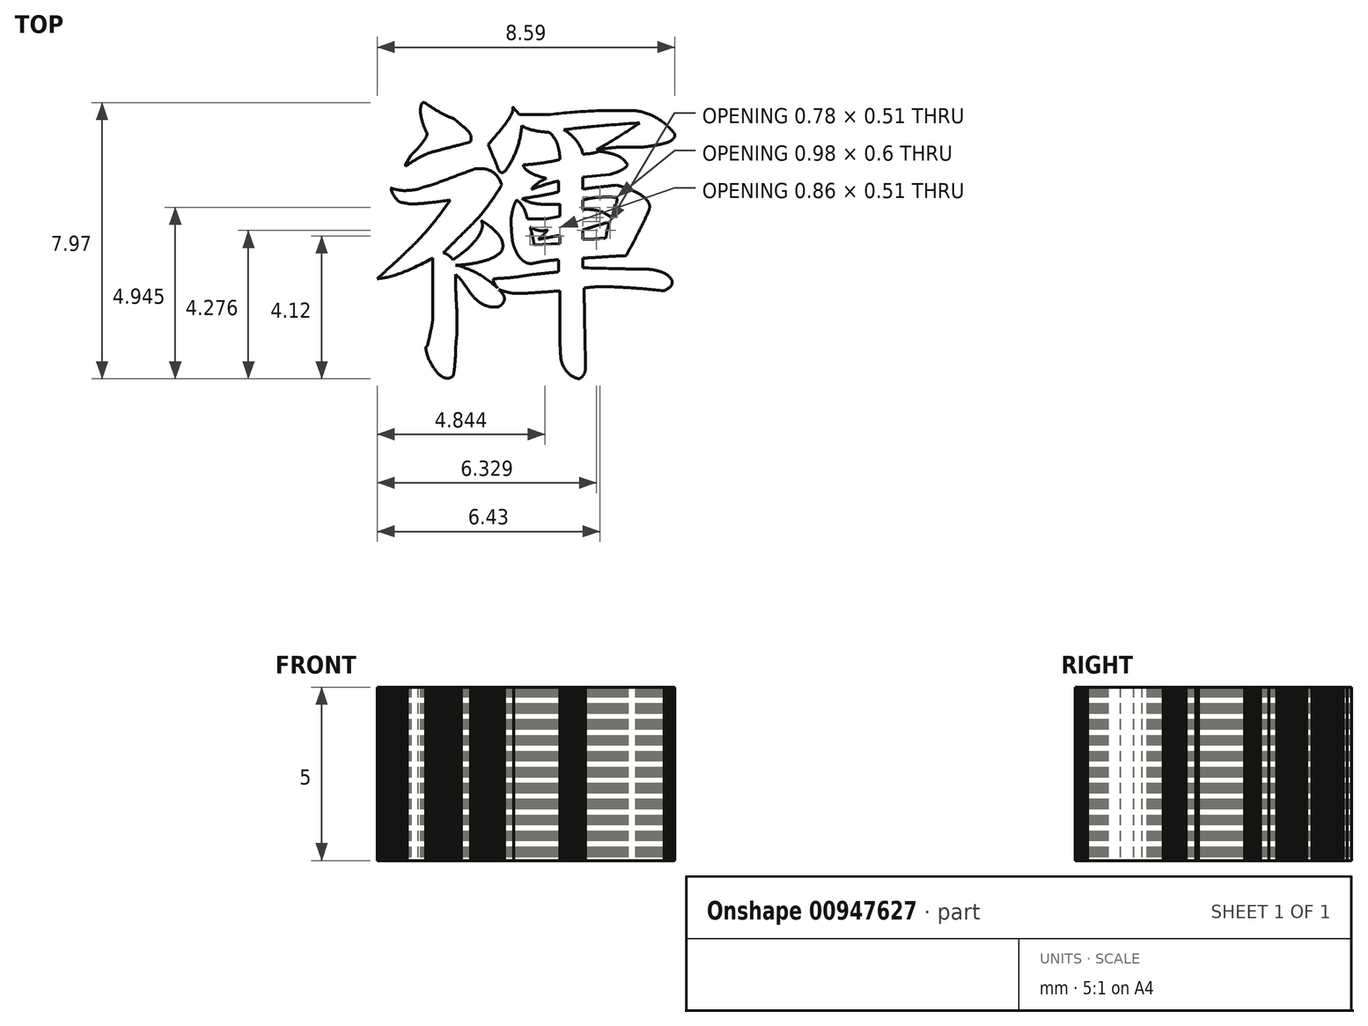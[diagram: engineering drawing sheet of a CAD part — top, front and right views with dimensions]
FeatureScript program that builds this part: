
annotation { "Feature Type Name" : "Feature", "Feature Type Description" : "" }
export const myFeature = defineFeature(function(context is Context, id is Id, definition is map)
    precondition{}
    {
        {
            var Q0;
            Q0=qCreatedBy(makeId("Top.planeOp"), FACE);
            var sketch = newSketch(context, id + "F0", { "sketchPlane" : qUnion([Q0])});
            skLineSegment(sketch, "E0", {"start": v(0.5, 4.13) * mm, "end": v(0.53, 4.13) * mm});
            skLineSegment(sketch, "E1", {"start": v(0.53, 4.13) * mm, "end": v(0.57, 4.12) * mm});
            skLineSegment(sketch, "E2", {"start": v(0.57, 4.12) * mm, "end": v(0.6, 4.11) * mm});
            skLineSegment(sketch, "E3", {"start": v(0.6, 4.11) * mm, "end": v(0.65, 4.1) * mm});
            skLineSegment(sketch, "E4", {"start": v(0.65, 4.1) * mm, "end": v(0.68, 4.1) * mm});
            skLineSegment(sketch, "E5", {"start": v(0.68, 4.1) * mm, "end": v(0.72, 4.09) * mm});
            skLineSegment(sketch, "E6", {"start": v(0.72, 4.09) * mm, "end": v(0.76, 4.08) * mm});
            skLineSegment(sketch, "E7", {"start": v(0.76, 4.08) * mm, "end": v(0.8, 4.06) * mm});
            skLineSegment(sketch, "E8", {"start": v(0.8, 4.06) * mm, "end": v(0.83, 4.05) * mm});
            skLineSegment(sketch, "E9", {"start": v(0.83, 4.05) * mm, "end": v(0.87, 4.04) * mm});
            skLineSegment(sketch, "E10", {"start": v(0.87, 4.04) * mm, "end": v(0.9, 4.02) * mm});
            skLineSegment(sketch, "E11", {"start": v(0.9, 4.02) * mm, "end": v(0.94, 4) * mm});
            skLineSegment(sketch, "E12", {"start": v(0.94, 4) * mm, "end": v(0.97, 4) * mm});
            skLineSegment(sketch, "E13", {"start": v(0.97, 4) * mm, "end": v(1, 3.97) * mm});
            skLineSegment(sketch, "E14", {"start": v(1, 3.97) * mm, "end": v(1.04, 3.96) * mm});
            skLineSegment(sketch, "E15", {"start": v(1.04, 3.96) * mm, "end": v(1.08, 3.94) * mm});
            skLineSegment(sketch, "E16", {"start": v(1.08, 3.94) * mm, "end": v(1.11, 3.92) * mm});
            skLineSegment(sketch, "E17", {"start": v(1.11, 3.92) * mm, "end": v(1.15, 3.9) * mm});
            skLineSegment(sketch, "E18", {"start": v(1.15, 3.9) * mm, "end": v(1.18, 3.87) * mm});
            skLineSegment(sketch, "E19", {"start": v(1.18, 3.87) * mm, "end": v(1.21, 3.85) * mm});
            skLineSegment(sketch, "E20", {"start": v(1.21, 3.85) * mm, "end": v(1.24, 3.83) * mm});
            skLineSegment(sketch, "E21", {"start": v(1.24, 3.83) * mm, "end": v(1.28, 3.8) * mm});
            skLineSegment(sketch, "E22", {"start": v(1.28, 3.8) * mm, "end": v(1.3, 3.78) * mm});
            skLineSegment(sketch, "E23", {"start": v(1.3, 3.78) * mm, "end": v(1.34, 3.75) * mm});
            skLineSegment(sketch, "E24", {"start": v(1.34, 3.75) * mm, "end": v(1.37, 3.72) * mm});
            skLineSegment(sketch, "E25", {"start": v(1.37, 3.72) * mm, "end": v(1.4, 3.7) * mm});
            skLineSegment(sketch, "E26", {"start": v(1.4, 3.7) * mm, "end": v(1.43, 3.67) * mm});
            skLineSegment(sketch, "E27", {"start": v(1.43, 3.67) * mm, "end": v(1.47, 3.64) * mm});
            skLineSegment(sketch, "E28", {"start": v(1.47, 3.64) * mm, "end": v(1.5, 3.6) * mm});
            skLineSegment(sketch, "E29", {"start": v(1.5, 3.6) * mm, "end": v(1.53, 3.57) * mm});
            skLineSegment(sketch, "E30", {"start": v(1.53, 3.57) * mm, "end": v(1.56, 3.54) * mm});
            skLineSegment(sketch, "E31", {"start": v(1.56, 3.54) * mm, "end": v(1.59, 3.5) * mm});
            skLineSegment(sketch, "E32", {"start": v(1.59, 3.5) * mm, "end": v(1.6, 3.5) * mm});
            skLineSegment(sketch, "E33", {"start": v(1.6, 3.5) * mm, "end": v(1.6, 3.5) * mm});
            skLineSegment(sketch, "E34", {"start": v(1.6, 3.5) * mm, "end": v(1.6, 3.49) * mm});
            skLineSegment(sketch, "E35", {"start": v(1.6, 3.49) * mm, "end": v(1.6, 3.48) * mm});
            skLineSegment(sketch, "E36", {"start": v(1.6, 3.48) * mm, "end": v(1.61, 3.47) * mm});
            skLineSegment(sketch, "E37", {"start": v(1.61, 3.47) * mm, "end": v(1.62, 3.46) * mm});
            skLineSegment(sketch, "E38", {"start": v(1.62, 3.46) * mm, "end": v(1.62, 3.45) * mm});
            skLineSegment(sketch, "E39", {"start": v(1.62, 3.45) * mm, "end": v(1.62, 3.45) * mm});
            skLineSegment(sketch, "E40", {"start": v(1.62, 3.45) * mm, "end": v(1.62, 3.44) * mm});
            skLineSegment(sketch, "E41", {"start": v(1.62, 3.44) * mm, "end": v(1.62, 3.43) * mm});
            skLineSegment(sketch, "E42", {"start": v(1.62, 3.43) * mm, "end": v(1.62, 3.42) * mm});
            skLineSegment(sketch, "E43", {"start": v(1.62, 3.42) * mm, "end": v(1.62, 3.41) * mm});
            skLineSegment(sketch, "E44", {"start": v(1.62, 3.41) * mm, "end": v(1.62, 3.4) * mm});
            skLineSegment(sketch, "E45", {"start": v(1.62, 3.4) * mm, "end": v(1.62, 3.4) * mm});
            skLineSegment(sketch, "E46", {"start": v(1.62, 3.4) * mm, "end": v(1.62, 3.39) * mm});
            skLineSegment(sketch, "E47", {"start": v(1.62, 3.39) * mm, "end": v(1.61, 3.38) * mm});
            skLineSegment(sketch, "E48", {"start": v(1.61, 3.38) * mm, "end": v(1.61, 3.37) * mm});
            skLineSegment(sketch, "E49", {"start": v(1.61, 3.37) * mm, "end": v(1.6, 3.36) * mm});
            skLineSegment(sketch, "E50", {"start": v(1.6, 3.36) * mm, "end": v(1.6, 3.35) * mm});
            skLineSegment(sketch, "E51", {"start": v(1.6, 3.35) * mm, "end": v(1.6, 3.35) * mm});
            skLineSegment(sketch, "E52", {"start": v(1.6, 3.35) * mm, "end": v(1.59, 3.34) * mm});
            skLineSegment(sketch, "E53", {"start": v(1.59, 3.34) * mm, "end": v(1.58, 3.33) * mm});
            skLineSegment(sketch, "E54", {"start": v(1.58, 3.33) * mm, "end": v(1.57, 3.32) * mm});
            skLineSegment(sketch, "E55", {"start": v(1.57, 3.32) * mm, "end": v(1.56, 3.31) * mm});
            skLineSegment(sketch, "E56", {"start": v(1.56, 3.31) * mm, "end": v(1.55, 3.3) * mm});
            skLineSegment(sketch, "E57", {"start": v(1.55, 3.3) * mm, "end": v(1.54, 3.3) * mm});
            skLineSegment(sketch, "E58", {"start": v(1.54, 3.3) * mm, "end": v(1.53, 3.28) * mm});
            skLineSegment(sketch, "E59", {"start": v(1.53, 3.28) * mm, "end": v(1.52, 3.27) * mm});
            skLineSegment(sketch, "E60", {"start": v(1.52, 3.27) * mm, "end": v(1.5, 3.26) * mm});
            skLineSegment(sketch, "E61", {"start": v(1.5, 3.26) * mm, "end": v(1.5, 3.25) * mm});
            skLineSegment(sketch, "E62", {"start": v(1.5, 3.25) * mm, "end": v(1.48, 3.24) * mm});
            skLineSegment(sketch, "E63", {"start": v(1.48, 3.24) * mm, "end": v(1.47, 3.23) * mm});
            skLineSegment(sketch, "E64", {"start": v(1.47, 3.23) * mm, "end": v(1.44, 3.23) * mm});
            skLineSegment(sketch, "E65", {"start": v(1.44, 3.23) * mm, "end": v(1.42, 3.22) * mm});
            skLineSegment(sketch, "E66", {"start": v(1.42, 3.22) * mm, "end": v(1.4, 3.21) * mm});
            skLineSegment(sketch, "E67", {"start": v(1.4, 3.21) * mm, "end": v(1.37, 3.2) * mm});
            skLineSegment(sketch, "E68", {"start": v(1.37, 3.2) * mm, "end": v(1.35, 3.2) * mm});
            skLineSegment(sketch, "E69", {"start": v(1.35, 3.2) * mm, "end": v(1.32, 3.2) * mm});
            skLineSegment(sketch, "E70", {"start": v(1.32, 3.2) * mm, "end": v(1.3, 3.19) * mm});
            skLineSegment(sketch, "E71", {"start": v(1.3, 3.19) * mm, "end": v(1.27, 3.18) * mm});
            skLineSegment(sketch, "E72", {"start": v(1.27, 3.18) * mm, "end": v(1.25, 3.17) * mm});
            skLineSegment(sketch, "E73", {"start": v(1.25, 3.17) * mm, "end": v(1.22, 3.17) * mm});
            skLineSegment(sketch, "E74", {"start": v(1.22, 3.17) * mm, "end": v(1.2, 3.16) * mm});
            skLineSegment(sketch, "E75", {"start": v(1.2, 3.16) * mm, "end": v(1.17, 3.16) * mm});
            skLineSegment(sketch, "E76", {"start": v(1.17, 3.16) * mm, "end": v(1.14, 3.15) * mm});
            skLineSegment(sketch, "E77", {"start": v(1.14, 3.15) * mm, "end": v(1.12, 3.15) * mm});
            skLineSegment(sketch, "E78", {"start": v(1.12, 3.15) * mm, "end": v(1.1, 3.14) * mm});
            skLineSegment(sketch, "E79", {"start": v(1.1, 3.14) * mm, "end": v(1.07, 3.14) * mm});
            skLineSegment(sketch, "E80", {"start": v(1.07, 3.14) * mm, "end": v(1.04, 3.13) * mm});
            skLineSegment(sketch, "E81", {"start": v(1.04, 3.13) * mm, "end": v(1.02, 3.13) * mm});
            skLineSegment(sketch, "E82", {"start": v(1.02, 3.13) * mm, "end": v(1, 3.12) * mm});
            skLineSegment(sketch, "E83", {"start": v(1, 3.12) * mm, "end": v(0.96, 3.12) * mm});
            skLineSegment(sketch, "E84", {"start": v(0.96, 3.12) * mm, "end": v(0.94, 3.11) * mm});
            skLineSegment(sketch, "E85", {"start": v(0.94, 3.11) * mm, "end": v(0.91, 3.11) * mm});
            skLineSegment(sketch, "E86", {"start": v(0.91, 3.11) * mm, "end": v(0.89, 3.1) * mm});
            skLineSegment(sketch, "E87", {"start": v(0.89, 3.1) * mm, "end": v(0.86, 3.1) * mm});
            skLineSegment(sketch, "E88", {"start": v(0.86, 3.1) * mm, "end": v(0.83, 3.1) * mm});
            skLineSegment(sketch, "E89", {"start": v(0.83, 3.1) * mm, "end": v(0.8, 3.1) * mm});
            skLineSegment(sketch, "E90", {"start": v(0.8, 3.1) * mm, "end": v(0.78, 3.1) * mm});
            skLineSegment(sketch, "E91", {"start": v(0.78, 3.1) * mm, "end": v(0.76, 3.09) * mm});
            skLineSegment(sketch, "E92", {"start": v(0.76, 3.09) * mm, "end": v(0.73, 3.09) * mm});
            skLineSegment(sketch, "E93", {"start": v(0.73, 3.09) * mm, "end": v(0.7, 3.08) * mm});
            skLineSegment(sketch, "E94", {"start": v(0.7, 3.08) * mm, "end": v(0.68, 3.08) * mm});
            skLineSegment(sketch, "E95", {"start": v(0.68, 3.08) * mm, "end": v(0.65, 3.08) * mm});
            skLineSegment(sketch, "E96", {"start": v(0.65, 3.08) * mm, "end": v(0.02, 3.08) * mm});
            skLineSegment(sketch, "E97", {"start": v(0.02, 3.08) * mm, "end": v(0.01, 3.08) * mm});
            skLineSegment(sketch, "E98", {"start": v(0.01, 3.08) * mm, "end": v(0, 3.08) * mm});
            skLineSegment(sketch, "E99", {"start": v(0, 3.08) * mm, "end": v(-0.02, 3.08) * mm});
            skLineSegment(sketch, "E100", {"start": v(-0.02, 3.08) * mm, "end": v(-0.03, 3.08) * mm});
            skLineSegment(sketch, "E101", {"start": v(-0.03, 3.08) * mm, "end": v(-0.04, 3.08) * mm});
            skLineSegment(sketch, "E102", {"start": v(-0.04, 3.08) * mm, "end": v(-0.06, 3.08) * mm});
            skLineSegment(sketch, "E103", {"start": v(-0.06, 3.08) * mm, "end": v(-0.08, 3.07) * mm});
            skLineSegment(sketch, "E104", {"start": v(-0.08, 3.07) * mm, "end": v(-0.1, 3.07) * mm});
            skLineSegment(sketch, "E105", {"start": v(-0.1, 3.07) * mm, "end": v(-0.1, 3.07) * mm});
            skLineSegment(sketch, "E106", {"start": v(-0.1, 3.07) * mm, "end": v(-0.13, 3.07) * mm});
            skLineSegment(sketch, "E107", {"start": v(-0.13, 3.07) * mm, "end": v(-0.14, 3.07) * mm});
            skLineSegment(sketch, "E108", {"start": v(-0.14, 3.07) * mm, "end": v(-0.16, 3.07) * mm});
            skLineSegment(sketch, "E109", {"start": v(-0.16, 3.07) * mm, "end": v(-0.18, 3.07) * mm});
            skLineSegment(sketch, "E110", {"start": v(-0.18, 3.07) * mm, "end": v(-0.2, 3.06) * mm});
            skLineSegment(sketch, "E111", {"start": v(-0.2, 3.06) * mm, "end": v(-0.22, 3.06) * mm});
            skLineSegment(sketch, "E112", {"start": v(-0.22, 3.06) * mm, "end": v(-0.24, 3.06) * mm});
            skLineSegment(sketch, "E113", {"start": v(-0.24, 3.06) * mm, "end": v(-0.26, 3.06) * mm});
            skLineSegment(sketch, "E114", {"start": v(-0.26, 3.06) * mm, "end": v(-0.28, 3.05) * mm});
            skLineSegment(sketch, "E115", {"start": v(-0.28, 3.05) * mm, "end": v(-0.3, 3.05) * mm});
            skLineSegment(sketch, "E116", {"start": v(-0.3, 3.05) * mm, "end": v(-0.33, 3.05) * mm});
            skLineSegment(sketch, "E117", {"start": v(-0.33, 3.05) * mm, "end": v(-0.35, 3.04) * mm});
            skLineSegment(sketch, "E118", {"start": v(-0.35, 3.04) * mm, "end": v(-0.37, 3.04) * mm});
            skLineSegment(sketch, "E119", {"start": v(-0.37, 3.04) * mm, "end": v(-0.4, 3.04) * mm});
            skLineSegment(sketch, "E120", {"start": v(-0.4, 3.04) * mm, "end": v(-0.42, 3.03) * mm});
            skLineSegment(sketch, "E121", {"start": v(-0.42, 3.03) * mm, "end": v(-0.45, 3.03) * mm});
            skLineSegment(sketch, "E122", {"start": v(-0.45, 3.03) * mm, "end": v(-0.48, 3.03) * mm});
            skLineSegment(sketch, "E123", {"start": v(-0.48, 3.03) * mm, "end": v(-0.5, 3.02) * mm});
            skLineSegment(sketch, "E124", {"start": v(-0.5, 3.02) * mm, "end": v(-0.53, 3.02) * mm});
            skLineSegment(sketch, "E125", {"start": v(-0.53, 3.02) * mm, "end": v(-0.56, 3.01) * mm});
            skLineSegment(sketch, "E126", {"start": v(-0.56, 3.01) * mm, "end": v(-0.58, 3) * mm});
            skLineSegment(sketch, "E127", {"start": v(-0.58, 3) * mm, "end": v(-0.61, 3) * mm});
            skLineSegment(sketch, "E128", {"start": v(-0.61, 3) * mm, "end": v(-0.64, 3) * mm});
            skLineSegment(sketch, "E129", {"start": v(-0.64, 3) * mm, "end": v(-0.6, 3.03) * mm});
            skLineSegment(sketch, "E130", {"start": v(-0.6, 3.03) * mm, "end": v(-0.55, 3.05) * mm});
            skLineSegment(sketch, "E131", {"start": v(-0.55, 3.05) * mm, "end": v(-0.5, 3.08) * mm});
            skLineSegment(sketch, "E132", {"start": v(-0.5, 3.08) * mm, "end": v(-0.46, 3.1) * mm});
            skLineSegment(sketch, "E133", {"start": v(-0.46, 3.1) * mm, "end": v(-0.41, 3.13) * mm});
            skLineSegment(sketch, "E134", {"start": v(-0.41, 3.13) * mm, "end": v(-0.37, 3.16) * mm});
            skLineSegment(sketch, "E135", {"start": v(-0.37, 3.16) * mm, "end": v(-0.33, 3.18) * mm});
            skLineSegment(sketch, "E136", {"start": v(-0.33, 3.18) * mm, "end": v(-0.28, 3.21) * mm});
            skLineSegment(sketch, "E137", {"start": v(-0.28, 3.21) * mm, "end": v(-0.24, 3.24) * mm});
            skLineSegment(sketch, "E138", {"start": v(-0.24, 3.24) * mm, "end": v(-0.2, 3.26) * mm});
            skLineSegment(sketch, "E139", {"start": v(-0.2, 3.26) * mm, "end": v(-0.16, 3.29) * mm});
            skLineSegment(sketch, "E140", {"start": v(-0.16, 3.29) * mm, "end": v(-0.12, 3.31) * mm});
            skLineSegment(sketch, "E141", {"start": v(-0.12, 3.31) * mm, "end": v(-0.08, 3.34) * mm});
            skLineSegment(sketch, "E142", {"start": v(-0.08, 3.34) * mm, "end": v(-0.04, 3.36) * mm});
            skLineSegment(sketch, "E143", {"start": v(-0.04, 3.36) * mm, "end": v(0, 3.39) * mm});
            skLineSegment(sketch, "E144", {"start": v(0, 3.39) * mm, "end": v(0.04, 3.41) * mm});
            skLineSegment(sketch, "E145", {"start": v(0.04, 3.41) * mm, "end": v(0.08, 3.43) * mm});
            skLineSegment(sketch, "E146", {"start": v(0.08, 3.43) * mm, "end": v(0.12, 3.46) * mm});
            skLineSegment(sketch, "E147", {"start": v(0.12, 3.46) * mm, "end": v(0.16, 3.48) * mm});
            skLineSegment(sketch, "E148", {"start": v(0.16, 3.48) * mm, "end": v(0.2, 3.5) * mm});
            skLineSegment(sketch, "E149", {"start": v(0.2, 3.5) * mm, "end": v(0.23, 3.53) * mm});
            skLineSegment(sketch, "E150", {"start": v(0.23, 3.53) * mm, "end": v(0.27, 3.55) * mm});
            skLineSegment(sketch, "E151", {"start": v(0.27, 3.55) * mm, "end": v(0.3, 3.58) * mm});
            skLineSegment(sketch, "E152", {"start": v(0.3, 3.58) * mm, "end": v(0.34, 3.6) * mm});
            skLineSegment(sketch, "E153", {"start": v(0.34, 3.6) * mm, "end": v(0.38, 3.62) * mm});
            skLineSegment(sketch, "E154", {"start": v(0.38, 3.62) * mm, "end": v(0.41, 3.65) * mm});
            skLineSegment(sketch, "E155", {"start": v(0.41, 3.65) * mm, "end": v(0.44, 3.67) * mm});
            skLineSegment(sketch, "E156", {"start": v(0.44, 3.67) * mm, "end": v(0.48, 3.7) * mm});
            skLineSegment(sketch, "E157", {"start": v(0.48, 3.7) * mm, "end": v(0.51, 3.72) * mm});
            skLineSegment(sketch, "E158", {"start": v(0.51, 3.72) * mm, "end": v(0.54, 3.74) * mm});
            skLineSegment(sketch, "E159", {"start": v(0.54, 3.74) * mm, "end": v(0.58, 3.76) * mm});
            skLineSegment(sketch, "E160", {"start": v(0.58, 3.76) * mm, "end": v(0.6, 3.78) * mm});
            skLineSegment(sketch, "E161", {"start": v(0.6, 3.78) * mm, "end": v(0.53, 3.78) * mm});
            skLineSegment(sketch, "E162", {"start": v(0.53, 3.78) * mm, "end": v(0.45, 3.77) * mm});
            skLineSegment(sketch, "E163", {"start": v(0.45, 3.77) * mm, "end": v(0.38, 3.77) * mm});
            skLineSegment(sketch, "E164", {"start": v(0.38, 3.77) * mm, "end": v(0.3, 3.76) * mm});
            skLineSegment(sketch, "E165", {"start": v(0.3, 3.76) * mm, "end": v(0.23, 3.76) * mm});
            skLineSegment(sketch, "E166", {"start": v(0.23, 3.76) * mm, "end": v(0.15, 3.75) * mm});
            skLineSegment(sketch, "E167", {"start": v(0.15, 3.75) * mm, "end": v(0.08, 3.75) * mm});
            skLineSegment(sketch, "E168", {"start": v(0.08, 3.75) * mm, "end": v(0, 3.74) * mm});
            skLineSegment(sketch, "E169", {"start": v(0, 3.74) * mm, "end": v(-0.07, 3.73) * mm});
            skLineSegment(sketch, "E170", {"start": v(-0.07, 3.73) * mm, "end": v(-0.14, 3.73) * mm});
            skLineSegment(sketch, "E171", {"start": v(-0.14, 3.73) * mm, "end": v(-0.21, 3.72) * mm});
            skLineSegment(sketch, "E172", {"start": v(-0.21, 3.72) * mm, "end": v(-0.28, 3.72) * mm});
            skLineSegment(sketch, "E173", {"start": v(-0.28, 3.72) * mm, "end": v(-0.36, 3.71) * mm});
            skLineSegment(sketch, "E174", {"start": v(-0.36, 3.71) * mm, "end": v(-0.43, 3.7) * mm});
            skLineSegment(sketch, "E175", {"start": v(-0.43, 3.7) * mm, "end": v(-0.5, 3.7) * mm});
            skLineSegment(sketch, "E176", {"start": v(-0.5, 3.7) * mm, "end": v(-0.56, 3.7) * mm});
            skLineSegment(sketch, "E177", {"start": v(-0.56, 3.7) * mm, "end": v(-0.63, 3.69) * mm});
            skLineSegment(sketch, "E178", {"start": v(-0.63, 3.69) * mm, "end": v(-0.7, 3.68) * mm});
            skLineSegment(sketch, "E179", {"start": v(-0.7, 3.68) * mm, "end": v(-0.77, 3.67) * mm});
            skLineSegment(sketch, "E180", {"start": v(-0.77, 3.67) * mm, "end": v(-0.83, 3.67) * mm});
            skLineSegment(sketch, "E181", {"start": v(-0.83, 3.67) * mm, "end": v(-0.9, 3.66) * mm});
            skLineSegment(sketch, "E182", {"start": v(-0.9, 3.66) * mm, "end": v(-0.96, 3.66) * mm});
            skLineSegment(sketch, "E183", {"start": v(-0.96, 3.66) * mm, "end": v(-1.03, 3.65) * mm});
            skLineSegment(sketch, "E184", {"start": v(-1.03, 3.65) * mm, "end": v(-1.1, 3.64) * mm});
            skLineSegment(sketch, "E185", {"start": v(-1.1, 3.64) * mm, "end": v(-1.15, 3.64) * mm});
            skLineSegment(sketch, "E186", {"start": v(-1.15, 3.64) * mm, "end": v(-1.22, 3.63) * mm});
            skLineSegment(sketch, "E187", {"start": v(-1.22, 3.63) * mm, "end": v(-1.28, 3.62) * mm});
            skLineSegment(sketch, "E188", {"start": v(-1.28, 3.62) * mm, "end": v(-1.34, 3.61) * mm});
            skLineSegment(sketch, "E189", {"start": v(-1.34, 3.61) * mm, "end": v(-1.4, 3.6) * mm});
            skLineSegment(sketch, "E190", {"start": v(-1.4, 3.6) * mm, "end": v(-1.46, 3.6) * mm});
            skLineSegment(sketch, "E191", {"start": v(-1.46, 3.6) * mm, "end": v(-1.52, 3.6) * mm});
            skLineSegment(sketch, "E192", {"start": v(-1.52, 3.6) * mm, "end": v(-1.58, 3.59) * mm});
            skLineSegment(sketch, "E193", {"start": v(-1.58, 3.59) * mm, "end": v(-1.55, 3.57) * mm});
            skLineSegment(sketch, "E194", {"start": v(-1.55, 3.57) * mm, "end": v(-1.52, 3.55) * mm});
            skLineSegment(sketch, "E195", {"start": v(-1.52, 3.55) * mm, "end": v(-1.5, 3.53) * mm});
            skLineSegment(sketch, "E196", {"start": v(-1.5, 3.53) * mm, "end": v(-1.47, 3.5) * mm});
            skLineSegment(sketch, "E197", {"start": v(-1.47, 3.5) * mm, "end": v(-1.44, 3.49) * mm});
            skLineSegment(sketch, "E198", {"start": v(-1.44, 3.49) * mm, "end": v(-1.42, 3.47) * mm});
            skLineSegment(sketch, "E199", {"start": v(-1.42, 3.47) * mm, "end": v(-1.4, 3.45) * mm});
            skLineSegment(sketch, "E200", {"start": v(-1.4, 3.45) * mm, "end": v(-1.37, 3.43) * mm});
            skLineSegment(sketch, "E201", {"start": v(-1.37, 3.43) * mm, "end": v(-1.35, 3.4) * mm});
            skLineSegment(sketch, "E202", {"start": v(-1.35, 3.4) * mm, "end": v(-1.32, 3.38) * mm});
            skLineSegment(sketch, "E203", {"start": v(-1.32, 3.38) * mm, "end": v(-1.3, 3.36) * mm});
            skLineSegment(sketch, "E204", {"start": v(-1.3, 3.36) * mm, "end": v(-1.28, 3.34) * mm});
            skLineSegment(sketch, "E205", {"start": v(-1.28, 3.34) * mm, "end": v(-1.26, 3.32) * mm});
            skLineSegment(sketch, "E206", {"start": v(-1.26, 3.32) * mm, "end": v(-1.24, 3.3) * mm});
            skLineSegment(sketch, "E207", {"start": v(-1.24, 3.3) * mm, "end": v(-1.23, 3.28) * mm});
            skLineSegment(sketch, "E208", {"start": v(-1.23, 3.28) * mm, "end": v(-1.2, 3.25) * mm});
            skLineSegment(sketch, "E209", {"start": v(-1.2, 3.25) * mm, "end": v(-1.2, 3.23) * mm});
            skLineSegment(sketch, "E210", {"start": v(-1.2, 3.23) * mm, "end": v(-1.18, 3.2) * mm});
            skLineSegment(sketch, "E211", {"start": v(-1.18, 3.2) * mm, "end": v(-1.16, 3.19) * mm});
            skLineSegment(sketch, "E212", {"start": v(-1.16, 3.19) * mm, "end": v(-1.15, 3.16) * mm});
            skLineSegment(sketch, "E213", {"start": v(-1.15, 3.16) * mm, "end": v(-1.13, 3.14) * mm});
            skLineSegment(sketch, "E214", {"start": v(-1.13, 3.14) * mm, "end": v(-1.12, 3.12) * mm});
            skLineSegment(sketch, "E215", {"start": v(-1.12, 3.12) * mm, "end": v(-1.1, 3.1) * mm});
            skLineSegment(sketch, "E216", {"start": v(-1.1, 3.1) * mm, "end": v(-1.1, 3.07) * mm});
            skLineSegment(sketch, "E217", {"start": v(-1.1, 3.07) * mm, "end": v(-1.08, 3.05) * mm});
            skLineSegment(sketch, "E218", {"start": v(-1.08, 3.05) * mm, "end": v(-1.07, 3.03) * mm});
            skLineSegment(sketch, "E219", {"start": v(-1.07, 3.03) * mm, "end": v(-1.07, 3) * mm});
            skLineSegment(sketch, "E220", {"start": v(-1.07, 3) * mm, "end": v(-1.06, 2.98) * mm});
            skLineSegment(sketch, "E221", {"start": v(-1.06, 2.98) * mm, "end": v(-1.05, 2.96) * mm});
            skLineSegment(sketch, "E222", {"start": v(-1.05, 2.96) * mm, "end": v(-1.04, 2.93) * mm});
            skLineSegment(sketch, "E223", {"start": v(-1.04, 2.93) * mm, "end": v(-1.04, 2.9) * mm});
            skLineSegment(sketch, "E224", {"start": v(-1.04, 2.9) * mm, "end": v(-1.03, 2.88) * mm});
            skLineSegment(sketch, "E225", {"start": v(-1.03, 2.88) * mm, "end": v(-1.01, 2.88) * mm});
            skLineSegment(sketch, "E226", {"start": v(-1.01, 2.88) * mm, "end": v(-1, 2.88) * mm});
            skLineSegment(sketch, "E227", {"start": v(-1, 2.88) * mm, "end": v(-0.98, 2.88) * mm});
            skLineSegment(sketch, "E228", {"start": v(-0.98, 2.88) * mm, "end": v(-0.96, 2.88) * mm});
            skLineSegment(sketch, "E229", {"start": v(-0.96, 2.88) * mm, "end": v(-0.95, 2.88) * mm});
            skLineSegment(sketch, "E230", {"start": v(-0.95, 2.88) * mm, "end": v(-0.93, 2.89) * mm});
            skLineSegment(sketch, "E231", {"start": v(-0.93, 2.89) * mm, "end": v(-0.92, 2.89) * mm});
            skLineSegment(sketch, "E232", {"start": v(-0.92, 2.89) * mm, "end": v(-0.9, 2.89) * mm});
            skLineSegment(sketch, "E233", {"start": v(-0.9, 2.89) * mm, "end": v(-0.88, 2.89) * mm});
            skLineSegment(sketch, "E234", {"start": v(-0.88, 2.89) * mm, "end": v(-0.87, 2.9) * mm});
            skLineSegment(sketch, "E235", {"start": v(-0.87, 2.9) * mm, "end": v(-0.85, 2.9) * mm});
            skLineSegment(sketch, "E236", {"start": v(-0.85, 2.9) * mm, "end": v(-0.84, 2.9) * mm});
            skLineSegment(sketch, "E237", {"start": v(-0.84, 2.9) * mm, "end": v(-0.82, 2.9) * mm});
            skLineSegment(sketch, "E238", {"start": v(-0.82, 2.9) * mm, "end": v(-0.8, 2.9) * mm});
            skLineSegment(sketch, "E239", {"start": v(-0.8, 2.9) * mm, "end": v(-0.8, 2.9) * mm});
            skLineSegment(sketch, "E240", {"start": v(-0.8, 2.9) * mm, "end": v(-0.78, 2.9) * mm});
            skLineSegment(sketch, "E241", {"start": v(-0.78, 2.9) * mm, "end": v(-0.76, 2.9) * mm});
            skLineSegment(sketch, "E242", {"start": v(-0.76, 2.9) * mm, "end": v(-0.75, 2.9) * mm});
            skLineSegment(sketch, "E243", {"start": v(-0.75, 2.9) * mm, "end": v(-0.74, 2.91) * mm});
            skLineSegment(sketch, "E244", {"start": v(-0.74, 2.91) * mm, "end": v(-0.72, 2.91) * mm});
            skLineSegment(sketch, "E245", {"start": v(-0.72, 2.91) * mm, "end": v(-0.7, 2.92) * mm});
            skLineSegment(sketch, "E246", {"start": v(-0.7, 2.92) * mm, "end": v(-0.7, 2.92) * mm});
            skLineSegment(sketch, "E247", {"start": v(-0.7, 2.92) * mm, "end": v(-0.68, 2.92) * mm});
            skLineSegment(sketch, "E248", {"start": v(-0.68, 2.92) * mm, "end": v(-0.67, 2.93) * mm});
            skLineSegment(sketch, "E249", {"start": v(-0.67, 2.93) * mm, "end": v(-0.65, 2.93) * mm});
            skLineSegment(sketch, "E250", {"start": v(-0.65, 2.93) * mm, "end": v(-0.64, 2.93) * mm});
            skLineSegment(sketch, "E251", {"start": v(-0.64, 2.93) * mm, "end": v(-0.63, 2.94) * mm});
            skLineSegment(sketch, "E252", {"start": v(-0.63, 2.94) * mm, "end": v(-0.61, 2.94) * mm});
            skLineSegment(sketch, "E253", {"start": v(-0.61, 2.94) * mm, "end": v(-0.6, 2.95) * mm});
            skLineSegment(sketch, "E254", {"start": v(-0.6, 2.95) * mm, "end": v(-0.59, 2.95) * mm});
            skLineSegment(sketch, "E255", {"start": v(-0.59, 2.95) * mm, "end": v(-0.58, 2.96) * mm});
            skLineSegment(sketch, "E256", {"start": v(-0.58, 2.96) * mm, "end": v(-0.56, 2.96) * mm});
            skLineSegment(sketch, "E257", {"start": v(-0.56, 2.96) * mm, "end": v(-0.54, 2.96) * mm});
            skLineSegment(sketch, "E258", {"start": v(-0.54, 2.96) * mm, "end": v(-0.52, 2.96) * mm});
            skLineSegment(sketch, "E259", {"start": v(-0.52, 2.96) * mm, "end": v(-0.5, 2.95) * mm});
            skLineSegment(sketch, "E260", {"start": v(-0.5, 2.95) * mm, "end": v(-0.49, 2.95) * mm});
            skLineSegment(sketch, "E261", {"start": v(-0.49, 2.95) * mm, "end": v(-0.47, 2.95) * mm});
            skLineSegment(sketch, "E262", {"start": v(-0.47, 2.95) * mm, "end": v(-0.45, 2.94) * mm});
            skLineSegment(sketch, "E263", {"start": v(-0.45, 2.94) * mm, "end": v(-0.43, 2.94) * mm});
            skLineSegment(sketch, "E264", {"start": v(-0.43, 2.94) * mm, "end": v(-0.41, 2.94) * mm});
            skLineSegment(sketch, "E265", {"start": v(-0.41, 2.94) * mm, "end": v(-0.4, 2.94) * mm});
            skLineSegment(sketch, "E266", {"start": v(-0.4, 2.94) * mm, "end": v(-0.38, 2.93) * mm});
            skLineSegment(sketch, "E267", {"start": v(-0.38, 2.93) * mm, "end": v(-0.36, 2.93) * mm});
            skLineSegment(sketch, "E268", {"start": v(-0.36, 2.93) * mm, "end": v(-0.35, 2.93) * mm});
            skLineSegment(sketch, "E269", {"start": v(-0.35, 2.93) * mm, "end": v(-0.33, 2.92) * mm});
            skLineSegment(sketch, "E270", {"start": v(-0.33, 2.92) * mm, "end": v(-0.31, 2.92) * mm});
            skLineSegment(sketch, "E271", {"start": v(-0.31, 2.92) * mm, "end": v(-0.3, 2.92) * mm});
            skLineSegment(sketch, "E272", {"start": v(-0.3, 2.92) * mm, "end": v(-0.28, 2.91) * mm});
            skLineSegment(sketch, "E273", {"start": v(-0.28, 2.91) * mm, "end": v(-0.26, 2.9) * mm});
            skLineSegment(sketch, "E274", {"start": v(-0.26, 2.9) * mm, "end": v(-0.25, 2.9) * mm});
            skLineSegment(sketch, "E275", {"start": v(-0.25, 2.9) * mm, "end": v(-0.23, 2.9) * mm});
            skLineSegment(sketch, "E276", {"start": v(-0.23, 2.9) * mm, "end": v(-0.22, 2.9) * mm});
            skLineSegment(sketch, "E277", {"start": v(-0.22, 2.9) * mm, "end": v(-0.2, 2.9) * mm});
            skLineSegment(sketch, "E278", {"start": v(-0.2, 2.9) * mm, "end": v(-0.19, 2.89) * mm});
            skLineSegment(sketch, "E279", {"start": v(-0.19, 2.89) * mm, "end": v(-0.17, 2.88) * mm});
            skLineSegment(sketch, "E280", {"start": v(-0.17, 2.88) * mm, "end": v(-0.16, 2.88) * mm});
            skLineSegment(sketch, "E281", {"start": v(-0.16, 2.88) * mm, "end": v(-0.15, 2.88) * mm});
            skLineSegment(sketch, "E282", {"start": v(-0.15, 2.88) * mm, "end": v(-0.13, 2.87) * mm});
            skLineSegment(sketch, "E283", {"start": v(-0.13, 2.87) * mm, "end": v(-0.12, 2.87) * mm});
            skLineSegment(sketch, "E284", {"start": v(-0.12, 2.87) * mm, "end": v(-0.1, 2.86) * mm});
            skLineSegment(sketch, "E285", {"start": v(-0.1, 2.86) * mm, "end": v(-0.1, 2.86) * mm});
            skLineSegment(sketch, "E286", {"start": v(-0.1, 2.86) * mm, "end": v(-0.08, 2.85) * mm});
            skLineSegment(sketch, "E287", {"start": v(-0.08, 2.85) * mm, "end": v(-0.07, 2.85) * mm});
            skLineSegment(sketch, "E288", {"start": v(-0.07, 2.85) * mm, "end": v(-0.06, 2.84) * mm});
            skLineSegment(sketch, "E289", {"start": v(-0.06, 2.84) * mm, "end": v(-0.04, 2.84) * mm});
            skLineSegment(sketch, "E290", {"start": v(-0.04, 2.84) * mm, "end": v(-0.03, 2.83) * mm});
            skLineSegment(sketch, "E291", {"start": v(-0.03, 2.83) * mm, "end": v(-0.02, 2.83) * mm});
            skLineSegment(sketch, "E292", {"start": v(-0.02, 2.83) * mm, "end": v(0, 2.82) * mm});
            skLineSegment(sketch, "E293", {"start": v(0, 2.82) * mm, "end": v(0, 2.82) * mm});
            skLineSegment(sketch, "E294", {"start": v(0, 2.82) * mm, "end": v(0.02, 2.81) * mm});
            skLineSegment(sketch, "E295", {"start": v(0.02, 2.81) * mm, "end": v(0.03, 2.8) * mm});
            skLineSegment(sketch, "E296", {"start": v(0.03, 2.8) * mm, "end": v(0.04, 2.8) * mm});
            skLineSegment(sketch, "E297", {"start": v(0.04, 2.8) * mm, "end": v(0.05, 2.8) * mm});
            skLineSegment(sketch, "E298", {"start": v(0.05, 2.8) * mm, "end": v(0.06, 2.78) * mm});
            skLineSegment(sketch, "E299", {"start": v(0.06, 2.78) * mm, "end": v(0.07, 2.78) * mm});
            skLineSegment(sketch, "E300", {"start": v(0.07, 2.78) * mm, "end": v(0.08, 2.77) * mm});
            skLineSegment(sketch, "E301", {"start": v(0.08, 2.77) * mm, "end": v(0.1, 2.76) * mm});
            skLineSegment(sketch, "E302", {"start": v(0.1, 2.76) * mm, "end": v(0.1, 2.75) * mm});
            skLineSegment(sketch, "E303", {"start": v(0.1, 2.75) * mm, "end": v(0.11, 2.75) * mm});
            skLineSegment(sketch, "E304", {"start": v(0.11, 2.75) * mm, "end": v(0.12, 2.74) * mm});
            skLineSegment(sketch, "E305", {"start": v(0.12, 2.74) * mm, "end": v(0.13, 2.73) * mm});
            skLineSegment(sketch, "E306", {"start": v(0.13, 2.73) * mm, "end": v(0.14, 2.72) * mm});
            skLineSegment(sketch, "E307", {"start": v(0.14, 2.72) * mm, "end": v(0.15, 2.71) * mm});
            skLineSegment(sketch, "E308", {"start": v(0.15, 2.71) * mm, "end": v(0.16, 2.7) * mm});
            skLineSegment(sketch, "E309", {"start": v(0.16, 2.7) * mm, "end": v(0.17, 2.7) * mm});
            skLineSegment(sketch, "E310", {"start": v(0.17, 2.7) * mm, "end": v(0.18, 2.68) * mm});
            skLineSegment(sketch, "E311", {"start": v(0.18, 2.68) * mm, "end": v(0.19, 2.67) * mm});
            skLineSegment(sketch, "E312", {"start": v(0.19, 2.67) * mm, "end": v(0.2, 2.66) * mm});
            skLineSegment(sketch, "E313", {"start": v(0.2, 2.66) * mm, "end": v(0.2, 2.65) * mm});
            skLineSegment(sketch, "E314", {"start": v(0.2, 2.65) * mm, "end": v(0.21, 2.64) * mm});
            skLineSegment(sketch, "E315", {"start": v(0.21, 2.64) * mm, "end": v(0.22, 2.63) * mm});
            skLineSegment(sketch, "E316", {"start": v(0.22, 2.63) * mm, "end": v(0.23, 2.62) * mm});
            skLineSegment(sketch, "E317", {"start": v(0.23, 2.62) * mm, "end": v(0.23, 2.6) * mm});
            skLineSegment(sketch, "E318", {"start": v(0.23, 2.6) * mm, "end": v(0.24, 2.6) * mm});
            skLineSegment(sketch, "E319", {"start": v(0.24, 2.6) * mm, "end": v(0.25, 2.58) * mm});
            skLineSegment(sketch, "E320", {"start": v(0.25, 2.58) * mm, "end": v(0.26, 2.57) * mm});
            skLineSegment(sketch, "E321", {"start": v(0.26, 2.57) * mm, "end": v(0.25, 2.56) * mm});
            skLineSegment(sketch, "E322", {"start": v(0.25, 2.56) * mm, "end": v(0.25, 2.55) * mm});
            skLineSegment(sketch, "E323", {"start": v(0.25, 2.55) * mm, "end": v(0.24, 2.54) * mm});
            skLineSegment(sketch, "E324", {"start": v(0.24, 2.54) * mm, "end": v(0.23, 2.53) * mm});
            skLineSegment(sketch, "E325", {"start": v(0.23, 2.53) * mm, "end": v(0.22, 2.52) * mm});
            skLineSegment(sketch, "E326", {"start": v(0.22, 2.52) * mm, "end": v(0.22, 2.51) * mm});
            skLineSegment(sketch, "E327", {"start": v(0.22, 2.51) * mm, "end": v(0.2, 2.5) * mm});
            skLineSegment(sketch, "E328", {"start": v(0.2, 2.5) * mm, "end": v(0.2, 2.5) * mm});
            skLineSegment(sketch, "E329", {"start": v(0.2, 2.5) * mm, "end": v(0.19, 2.49) * mm});
            skLineSegment(sketch, "E330", {"start": v(0.19, 2.49) * mm, "end": v(0.17, 2.48) * mm});
            skLineSegment(sketch, "E331", {"start": v(0.17, 2.48) * mm, "end": v(0.16, 2.47) * mm});
            skLineSegment(sketch, "E332", {"start": v(0.16, 2.47) * mm, "end": v(0.15, 2.46) * mm});
            skLineSegment(sketch, "E333", {"start": v(0.15, 2.46) * mm, "end": v(0.14, 2.45) * mm});
            skLineSegment(sketch, "E334", {"start": v(0.14, 2.45) * mm, "end": v(0.12, 2.44) * mm});
            skLineSegment(sketch, "E335", {"start": v(0.12, 2.44) * mm, "end": v(0.1, 2.43) * mm});
            skLineSegment(sketch, "E336", {"start": v(0.1, 2.43) * mm, "end": v(0.1, 2.42) * mm});
            skLineSegment(sketch, "E337", {"start": v(0.1, 2.42) * mm, "end": v(0.07, 2.42) * mm});
            skLineSegment(sketch, "E338", {"start": v(0.07, 2.42) * mm, "end": v(0.06, 2.4) * mm});
            skLineSegment(sketch, "E339", {"start": v(0.06, 2.4) * mm, "end": v(0.04, 2.4) * mm});
            skLineSegment(sketch, "E340", {"start": v(0.04, 2.4) * mm, "end": v(0.02, 2.4) * mm});
            skLineSegment(sketch, "E341", {"start": v(0.02, 2.4) * mm, "end": v(0, 2.38) * mm});
            skLineSegment(sketch, "E342", {"start": v(0, 2.38) * mm, "end": v(-0.02, 2.37) * mm});
            skLineSegment(sketch, "E343", {"start": v(-0.02, 2.37) * mm, "end": v(-0.04, 2.37) * mm});
            skLineSegment(sketch, "E344", {"start": v(-0.04, 2.37) * mm, "end": v(-0.06, 2.36) * mm});
            skLineSegment(sketch, "E345", {"start": v(-0.06, 2.36) * mm, "end": v(-0.08, 2.35) * mm});
            skLineSegment(sketch, "E346", {"start": v(-0.08, 2.35) * mm, "end": v(-0.1, 2.34) * mm});
            skLineSegment(sketch, "E347", {"start": v(-0.1, 2.34) * mm, "end": v(-0.13, 2.33) * mm});
            skLineSegment(sketch, "E348", {"start": v(-0.13, 2.33) * mm, "end": v(-0.15, 2.33) * mm});
            skLineSegment(sketch, "E349", {"start": v(-0.15, 2.33) * mm, "end": v(-0.17, 2.32) * mm});
            skLineSegment(sketch, "E350", {"start": v(-0.17, 2.32) * mm, "end": v(-0.2, 2.31) * mm});
            skLineSegment(sketch, "E351", {"start": v(-0.2, 2.31) * mm, "end": v(-0.22, 2.3) * mm});
            skLineSegment(sketch, "E352", {"start": v(-0.22, 2.3) * mm, "end": v(-0.25, 2.3) * mm});
            skLineSegment(sketch, "E353", {"start": v(-0.25, 2.3) * mm, "end": v(-1.03, 2.22) * mm});
            skLineSegment(sketch, "E354", {"start": v(-1.03, 2.22) * mm, "end": v(-1.03, 1.87) * mm});
            skLineSegment(sketch, "E355", {"start": v(-1.03, 1.87) * mm, "end": v(-1.02, 1.87) * mm});
            skLineSegment(sketch, "E356", {"start": v(-1.02, 1.87) * mm, "end": v(-1, 1.87) * mm});
            skLineSegment(sketch, "E357", {"start": v(-1, 1.87) * mm, "end": v(-0.99, 1.88) * mm});
            skLineSegment(sketch, "E358", {"start": v(-0.99, 1.88) * mm, "end": v(-0.97, 1.88) * mm});
            skLineSegment(sketch, "E359", {"start": v(-0.97, 1.88) * mm, "end": v(-0.96, 1.88) * mm});
            skLineSegment(sketch, "E360", {"start": v(-0.96, 1.88) * mm, "end": v(-0.94, 1.88) * mm});
            skLineSegment(sketch, "E361", {"start": v(-0.94, 1.88) * mm, "end": v(-0.92, 1.89) * mm});
            skLineSegment(sketch, "E362", {"start": v(-0.92, 1.89) * mm, "end": v(-0.9, 1.89) * mm});
            skLineSegment(sketch, "E363", {"start": v(-0.9, 1.89) * mm, "end": v(-0.88, 1.9) * mm});
            skLineSegment(sketch, "E364", {"start": v(-0.88, 1.9) * mm, "end": v(-0.85, 1.9) * mm});
            skLineSegment(sketch, "E365", {"start": v(-0.85, 1.9) * mm, "end": v(-0.83, 1.9) * mm});
            skLineSegment(sketch, "E366", {"start": v(-0.83, 1.9) * mm, "end": v(-0.8, 1.9) * mm});
            skLineSegment(sketch, "E367", {"start": v(-0.8, 1.9) * mm, "end": v(-0.78, 1.9) * mm});
            skLineSegment(sketch, "E368", {"start": v(-0.78, 1.9) * mm, "end": v(-0.75, 1.9) * mm});
            skLineSegment(sketch, "E369", {"start": v(-0.75, 1.9) * mm, "end": v(-0.72, 1.91) * mm});
            skLineSegment(sketch, "E370", {"start": v(-0.72, 1.91) * mm, "end": v(-0.69, 1.92) * mm});
            skLineSegment(sketch, "E371", {"start": v(-0.69, 1.92) * mm, "end": v(-0.66, 1.92) * mm});
            skLineSegment(sketch, "E372", {"start": v(-0.66, 1.92) * mm, "end": v(-0.63, 1.92) * mm});
            skLineSegment(sketch, "E373", {"start": v(-0.63, 1.92) * mm, "end": v(-0.6, 1.93) * mm});
            skLineSegment(sketch, "E374", {"start": v(-0.6, 1.93) * mm, "end": v(-0.56, 1.93) * mm});
            skLineSegment(sketch, "E375", {"start": v(-0.56, 1.93) * mm, "end": v(-0.52, 1.94) * mm});
            skLineSegment(sketch, "E376", {"start": v(-0.52, 1.94) * mm, "end": v(-0.49, 1.94) * mm});
            skLineSegment(sketch, "E377", {"start": v(-0.49, 1.94) * mm, "end": v(-0.45, 1.94) * mm});
            skLineSegment(sketch, "E378", {"start": v(-0.45, 1.94) * mm, "end": v(-0.4, 1.95) * mm});
            skLineSegment(sketch, "E379", {"start": v(-0.4, 1.95) * mm, "end": v(-0.37, 1.95) * mm});
            skLineSegment(sketch, "E380", {"start": v(-0.37, 1.95) * mm, "end": v(-0.33, 1.96) * mm});
            skLineSegment(sketch, "E381", {"start": v(-0.33, 1.96) * mm, "end": v(-0.28, 1.96) * mm});
            skLineSegment(sketch, "E382", {"start": v(-0.28, 1.96) * mm, "end": v(-0.24, 1.97) * mm});
            skLineSegment(sketch, "E383", {"start": v(-0.24, 1.97) * mm, "end": v(-0.2, 1.97) * mm});
            skLineSegment(sketch, "E384", {"start": v(-0.2, 1.97) * mm, "end": v(-0.15, 1.97) * mm});
            skLineSegment(sketch, "E385", {"start": v(-0.15, 1.97) * mm, "end": v(-0.1, 1.98) * mm});
            skLineSegment(sketch, "E386", {"start": v(-0.1, 1.98) * mm, "end": v(-0.06, 1.98) * mm});
            skLineSegment(sketch, "E387", {"start": v(-0.06, 1.98) * mm, "end": v(-0.04, 1.98) * mm});
            skLineSegment(sketch, "E388", {"start": v(-0.04, 1.98) * mm, "end": v(-0.02, 1.97) * mm});
            skLineSegment(sketch, "E389", {"start": v(-0.02, 1.97) * mm, "end": v(0, 1.97) * mm});
            skLineSegment(sketch, "E390", {"start": v(0, 1.97) * mm, "end": v(0.02, 1.96) * mm});
            skLineSegment(sketch, "E391", {"start": v(0.02, 1.96) * mm, "end": v(0.04, 1.96) * mm});
            skLineSegment(sketch, "E392", {"start": v(0.04, 1.96) * mm, "end": v(0.06, 1.95) * mm});
            skLineSegment(sketch, "E393", {"start": v(0.06, 1.95) * mm, "end": v(0.08, 1.95) * mm});
            skLineSegment(sketch, "E394", {"start": v(0.08, 1.95) * mm, "end": v(0.1, 1.94) * mm});
            skLineSegment(sketch, "E395", {"start": v(0.1, 1.94) * mm, "end": v(0.12, 1.93) * mm});
            skLineSegment(sketch, "E396", {"start": v(0.12, 1.93) * mm, "end": v(0.14, 1.93) * mm});
            skLineSegment(sketch, "E397", {"start": v(0.14, 1.93) * mm, "end": v(0.16, 1.92) * mm});
            skLineSegment(sketch, "E398", {"start": v(0.16, 1.92) * mm, "end": v(0.18, 1.91) * mm});
            skLineSegment(sketch, "E399", {"start": v(0.18, 1.91) * mm, "end": v(0.2, 1.9) * mm});
            skLineSegment(sketch, "E400", {"start": v(0.2, 1.9) * mm, "end": v(0.22, 1.9) * mm});
            skLineSegment(sketch, "E401", {"start": v(0.22, 1.9) * mm, "end": v(0.24, 1.9) * mm});
            skLineSegment(sketch, "E402", {"start": v(0.24, 1.9) * mm, "end": v(0.26, 1.89) * mm});
            skLineSegment(sketch, "E403", {"start": v(0.26, 1.89) * mm, "end": v(0.28, 1.88) * mm});
            skLineSegment(sketch, "E404", {"start": v(0.28, 1.88) * mm, "end": v(0.3, 1.87) * mm});
            skLineSegment(sketch, "E405", {"start": v(0.3, 1.87) * mm, "end": v(0.32, 1.86) * mm});
            skLineSegment(sketch, "E406", {"start": v(0.32, 1.86) * mm, "end": v(0.34, 1.86) * mm});
            skLineSegment(sketch, "E407", {"start": v(0.34, 1.86) * mm, "end": v(0.35, 1.85) * mm});
            skLineSegment(sketch, "E408", {"start": v(0.35, 1.85) * mm, "end": v(0.37, 1.84) * mm});
            skLineSegment(sketch, "E409", {"start": v(0.37, 1.84) * mm, "end": v(0.4, 1.83) * mm});
            skLineSegment(sketch, "E410", {"start": v(0.4, 1.83) * mm, "end": v(0.41, 1.82) * mm});
            skLineSegment(sketch, "E411", {"start": v(0.41, 1.82) * mm, "end": v(0.43, 1.81) * mm});
            skLineSegment(sketch, "E412", {"start": v(0.43, 1.81) * mm, "end": v(0.45, 1.8) * mm});
            skLineSegment(sketch, "E413", {"start": v(0.45, 1.8) * mm, "end": v(0.47, 1.8) * mm});
            skLineSegment(sketch, "E414", {"start": v(0.47, 1.8) * mm, "end": v(0.5, 1.79) * mm});
            skLineSegment(sketch, "E415", {"start": v(0.5, 1.79) * mm, "end": v(0.51, 1.78) * mm});
            skLineSegment(sketch, "E416", {"start": v(0.51, 1.78) * mm, "end": v(0.53, 1.77) * mm});
            skLineSegment(sketch, "E417", {"start": v(0.53, 1.77) * mm, "end": v(0.55, 1.76) * mm});
            skLineSegment(sketch, "E418", {"start": v(0.55, 1.76) * mm, "end": v(0.57, 1.75) * mm});
            skLineSegment(sketch, "E419", {"start": v(0.57, 1.75) * mm, "end": v(0.6, 1.74) * mm});
            skLineSegment(sketch, "E420", {"start": v(0.6, 1.74) * mm, "end": v(0.62, 1.72) * mm});
            skLineSegment(sketch, "E421", {"start": v(0.62, 1.72) * mm, "end": v(0.64, 1.7) * mm});
            skLineSegment(sketch, "E422", {"start": v(0.64, 1.7) * mm, "end": v(0.66, 1.7) * mm});
            skLineSegment(sketch, "E423", {"start": v(0.66, 1.7) * mm, "end": v(0.68, 1.68) * mm});
            skLineSegment(sketch, "E424", {"start": v(0.68, 1.68) * mm, "end": v(0.7, 1.66) * mm});
            skLineSegment(sketch, "E425", {"start": v(0.7, 1.66) * mm, "end": v(0.72, 1.65) * mm});
            skLineSegment(sketch, "E426", {"start": v(0.72, 1.65) * mm, "end": v(0.74, 1.63) * mm});
            skLineSegment(sketch, "E427", {"start": v(0.74, 1.63) * mm, "end": v(0.75, 1.62) * mm});
            skLineSegment(sketch, "E428", {"start": v(0.75, 1.62) * mm, "end": v(0.77, 1.6) * mm});
            skLineSegment(sketch, "E429", {"start": v(0.77, 1.6) * mm, "end": v(0.78, 1.59) * mm});
            skLineSegment(sketch, "E430", {"start": v(0.78, 1.59) * mm, "end": v(0.8, 1.57) * mm});
            skLineSegment(sketch, "E431", {"start": v(0.8, 1.57) * mm, "end": v(0.8, 1.56) * mm});
            skLineSegment(sketch, "E432", {"start": v(0.8, 1.56) * mm, "end": v(0.82, 1.55) * mm});
            skLineSegment(sketch, "E433", {"start": v(0.82, 1.55) * mm, "end": v(0.83, 1.53) * mm});
            skLineSegment(sketch, "E434", {"start": v(0.83, 1.53) * mm, "end": v(0.84, 1.52) * mm});
            skLineSegment(sketch, "E435", {"start": v(0.84, 1.52) * mm, "end": v(0.85, 1.5) * mm});
            skLineSegment(sketch, "E436", {"start": v(0.85, 1.5) * mm, "end": v(0.86, 1.49) * mm});
            skLineSegment(sketch, "E437", {"start": v(0.86, 1.49) * mm, "end": v(0.87, 1.47) * mm});
            skLineSegment(sketch, "E438", {"start": v(0.87, 1.47) * mm, "end": v(0.87, 1.46) * mm});
            skLineSegment(sketch, "E439", {"start": v(0.87, 1.46) * mm, "end": v(0.88, 1.44) * mm});
            skLineSegment(sketch, "E440", {"start": v(0.88, 1.44) * mm, "end": v(0.89, 1.43) * mm});
            skLineSegment(sketch, "E441", {"start": v(0.89, 1.43) * mm, "end": v(0.89, 1.41) * mm});
            skLineSegment(sketch, "E442", {"start": v(0.89, 1.41) * mm, "end": v(0.9, 1.4) * mm});
            skLineSegment(sketch, "E443", {"start": v(0.9, 1.4) * mm, "end": v(0.9, 1.38) * mm});
            skLineSegment(sketch, "E444", {"start": v(0.9, 1.38) * mm, "end": v(0.9, 1.37) * mm});
            skLineSegment(sketch, "E445", {"start": v(0.9, 1.37) * mm, "end": v(0.9, 1.35) * mm});
            skLineSegment(sketch, "E446", {"start": v(0.9, 1.35) * mm, "end": v(0.9, 1.34) * mm});
            skLineSegment(sketch, "E447", {"start": v(0.9, 1.34) * mm, "end": v(0.9, 1.33) * mm});
            skLineSegment(sketch, "E448", {"start": v(0.9, 1.33) * mm, "end": v(0.89, 1.31) * mm});
            skLineSegment(sketch, "E449", {"start": v(0.89, 1.31) * mm, "end": v(0.89, 1.3) * mm});
            skLineSegment(sketch, "E450", {"start": v(0.89, 1.3) * mm, "end": v(0.88, 1.28) * mm});
            skLineSegment(sketch, "E451", {"start": v(0.88, 1.28) * mm, "end": v(0.87, 1.25) * mm});
            skLineSegment(sketch, "E452", {"start": v(0.87, 1.25) * mm, "end": v(0.86, 1.22) * mm});
            skLineSegment(sketch, "E453", {"start": v(0.86, 1.22) * mm, "end": v(0.84, 1.2) * mm});
            skLineSegment(sketch, "E454", {"start": v(0.84, 1.2) * mm, "end": v(0.83, 1.16) * mm});
            skLineSegment(sketch, "E455", {"start": v(0.83, 1.16) * mm, "end": v(0.81, 1.13) * mm});
            skLineSegment(sketch, "E456", {"start": v(0.81, 1.13) * mm, "end": v(0.8, 1.1) * mm});
            skLineSegment(sketch, "E457", {"start": v(0.8, 1.1) * mm, "end": v(0.78, 1.06) * mm});
            skLineSegment(sketch, "E458", {"start": v(0.78, 1.06) * mm, "end": v(0.77, 1.02) * mm});
            skLineSegment(sketch, "E459", {"start": v(0.77, 1.02) * mm, "end": v(0.75, 0.99) * mm});
            skLineSegment(sketch, "E460", {"start": v(0.75, 0.99) * mm, "end": v(0.73, 0.95) * mm});
            skLineSegment(sketch, "E461", {"start": v(0.73, 0.95) * mm, "end": v(0.72, 0.91) * mm});
            skLineSegment(sketch, "E462", {"start": v(0.72, 0.91) * mm, "end": v(0.7, 0.88) * mm});
            skLineSegment(sketch, "E463", {"start": v(0.7, 0.88) * mm, "end": v(0.68, 0.84) * mm});
            skLineSegment(sketch, "E464", {"start": v(0.68, 0.84) * mm, "end": v(0.66, 0.8) * mm});
            skLineSegment(sketch, "E465", {"start": v(0.66, 0.8) * mm, "end": v(0.64, 0.76) * mm});
            skLineSegment(sketch, "E466", {"start": v(0.64, 0.76) * mm, "end": v(0.62, 0.72) * mm});
            skLineSegment(sketch, "E467", {"start": v(0.62, 0.72) * mm, "end": v(0.6, 0.67) * mm});
            skLineSegment(sketch, "E468", {"start": v(0.6, 0.67) * mm, "end": v(0.58, 0.63) * mm});
            skLineSegment(sketch, "E469", {"start": v(0.58, 0.63) * mm, "end": v(0.55, 0.59) * mm});
            skLineSegment(sketch, "E470", {"start": v(0.55, 0.59) * mm, "end": v(0.53, 0.54) * mm});
            skLineSegment(sketch, "E471", {"start": v(0.53, 0.54) * mm, "end": v(0.5, 0.5) * mm});
            skLineSegment(sketch, "E472", {"start": v(0.5, 0.5) * mm, "end": v(0.48, 0.45) * mm});
            skLineSegment(sketch, "E473", {"start": v(0.48, 0.45) * mm, "end": v(0.46, 0.4) * mm});
            skLineSegment(sketch, "E474", {"start": v(0.46, 0.4) * mm, "end": v(0.44, 0.36) * mm});
            skLineSegment(sketch, "E475", {"start": v(0.44, 0.36) * mm, "end": v(0.41, 0.31) * mm});
            skLineSegment(sketch, "E476", {"start": v(0.41, 0.31) * mm, "end": v(0.38, 0.26) * mm});
            skLineSegment(sketch, "E477", {"start": v(0.38, 0.26) * mm, "end": v(0.36, 0.21) * mm});
            skLineSegment(sketch, "E478", {"start": v(0.36, 0.21) * mm, "end": v(0.33, 0.16) * mm});
            skLineSegment(sketch, "E479", {"start": v(0.33, 0.16) * mm, "end": v(0.3, 0.11) * mm});
            skLineSegment(sketch, "E480", {"start": v(0.3, 0.11) * mm, "end": v(0.28, 0.06) * mm});
            skLineSegment(sketch, "E481", {"start": v(0.28, 0.06) * mm, "end": v(0.25, 0) * mm});
            skLineSegment(sketch, "E482", {"start": v(0.25, 0) * mm, "end": v(0.22, -0.05) * mm});
            skLineSegment(sketch, "E483", {"start": v(0.22, -0.05) * mm, "end": v(0.17, -0.05) * mm});
            skLineSegment(sketch, "E484", {"start": v(0.17, -0.05) * mm, "end": v(0.13, -0.05) * mm});
            skLineSegment(sketch, "E485", {"start": v(0.13, -0.05) * mm, "end": v(0.08, -0.05) * mm});
            skLineSegment(sketch, "E486", {"start": v(0.08, -0.05) * mm, "end": v(0.04, -0.06) * mm});
            skLineSegment(sketch, "E487", {"start": v(0.04, -0.06) * mm, "end": v(0, -0.06) * mm});
            skLineSegment(sketch, "E488", {"start": v(0, -0.06) * mm, "end": v(-0.05, -0.06) * mm});
            skLineSegment(sketch, "E489", {"start": v(-0.05, -0.06) * mm, "end": v(-0.1, -0.06) * mm});
            skLineSegment(sketch, "E490", {"start": v(-0.1, -0.06) * mm, "end": v(-0.14, -0.07) * mm});
            skLineSegment(sketch, "E491", {"start": v(-0.14, -0.07) * mm, "end": v(-0.18, -0.07) * mm});
            skLineSegment(sketch, "E492", {"start": v(-0.18, -0.07) * mm, "end": v(-0.22, -0.07) * mm});
            skLineSegment(sketch, "E493", {"start": v(-0.22, -0.07) * mm, "end": v(-0.26, -0.07) * mm});
            skLineSegment(sketch, "E494", {"start": v(-0.26, -0.07) * mm, "end": v(-0.3, -0.08) * mm});
            skLineSegment(sketch, "E495", {"start": v(-0.3, -0.08) * mm, "end": v(-0.35, -0.08) * mm});
            skLineSegment(sketch, "E496", {"start": v(-0.35, -0.08) * mm, "end": v(-0.39, -0.08) * mm});
            skLineSegment(sketch, "E497", {"start": v(-0.39, -0.08) * mm, "end": v(-0.43, -0.08) * mm});
            skLineSegment(sketch, "E498", {"start": v(-0.43, -0.08) * mm, "end": v(-0.47, -0.09) * mm});
            skLineSegment(sketch, "E499", {"start": v(-0.47, -0.09) * mm, "end": v(-0.5, -0.09) * mm});
            skLineSegment(sketch, "E500", {"start": v(-0.5, -0.09) * mm, "end": v(-0.54, -0.1) * mm});
            skLineSegment(sketch, "E501", {"start": v(-0.54, -0.1) * mm, "end": v(-0.58, -0.1) * mm});
            skLineSegment(sketch, "E502", {"start": v(-0.58, -0.1) * mm, "end": v(-0.62, -0.1) * mm});
            skLineSegment(sketch, "E503", {"start": v(-0.62, -0.1) * mm, "end": v(-0.66, -0.1) * mm});
            skLineSegment(sketch, "E504", {"start": v(-0.66, -0.1) * mm, "end": v(-0.7, -0.1) * mm});
            skLineSegment(sketch, "E505", {"start": v(-0.7, -0.1) * mm, "end": v(-0.73, -0.1) * mm});
            skLineSegment(sketch, "E506", {"start": v(-0.73, -0.1) * mm, "end": v(-0.76, -0.1) * mm});
            skLineSegment(sketch, "E507", {"start": v(-0.76, -0.1) * mm, "end": v(-0.8, -0.1) * mm});
            skLineSegment(sketch, "E508", {"start": v(-0.8, -0.1) * mm, "end": v(-0.83, -0.11) * mm});
            skLineSegment(sketch, "E509", {"start": v(-0.83, -0.11) * mm, "end": v(-0.87, -0.11) * mm});
            skLineSegment(sketch, "E510", {"start": v(-0.87, -0.11) * mm, "end": v(-0.9, -0.12) * mm});
            skLineSegment(sketch, "E511", {"start": v(-0.9, -0.12) * mm, "end": v(-0.93, -0.12) * mm});
            skLineSegment(sketch, "E512", {"start": v(-0.93, -0.12) * mm, "end": v(-0.97, -0.12) * mm});
            skLineSegment(sketch, "E513", {"start": v(-0.97, -0.12) * mm, "end": v(-1, -0.12) * mm});
            skLineSegment(sketch, "E514", {"start": v(-1, -0.12) * mm, "end": v(-1.03, -0.13) * mm});
            skLineSegment(sketch, "E515", {"start": v(-1.03, -0.13) * mm, "end": v(-1.03, -0.4) * mm});
            skLineSegment(sketch, "E516", {"start": v(-1.03, -0.4) * mm, "end": v(-0.95, -0.4) * mm});
            skLineSegment(sketch, "E517", {"start": v(-0.95, -0.4) * mm, "end": v(-0.87, -0.4) * mm});
            skLineSegment(sketch, "E518", {"start": v(-0.87, -0.4) * mm, "end": v(-0.8, -0.4) * mm});
            skLineSegment(sketch, "E519", {"start": v(-0.8, -0.4) * mm, "end": v(-0.71, -0.4) * mm});
            skLineSegment(sketch, "E520", {"start": v(-0.71, -0.4) * mm, "end": v(-0.64, -0.4) * mm});
            skLineSegment(sketch, "E521", {"start": v(-0.64, -0.4) * mm, "end": v(-0.57, -0.41) * mm});
            skLineSegment(sketch, "E522", {"start": v(-0.57, -0.41) * mm, "end": v(-0.5, -0.41) * mm});
            skLineSegment(sketch, "E523", {"start": v(-0.5, -0.41) * mm, "end": v(-0.42, -0.42) * mm});
            skLineSegment(sketch, "E524", {"start": v(-0.42, -0.42) * mm, "end": v(-0.36, -0.42) * mm});
            skLineSegment(sketch, "E525", {"start": v(-0.36, -0.42) * mm, "end": v(-0.29, -0.42) * mm});
            skLineSegment(sketch, "E526", {"start": v(-0.29, -0.42) * mm, "end": v(-0.22, -0.42) * mm});
            skLineSegment(sketch, "E527", {"start": v(-0.22, -0.42) * mm, "end": v(-0.16, -0.42) * mm});
            skLineSegment(sketch, "E528", {"start": v(-0.16, -0.42) * mm, "end": v(-0.1, -0.42) * mm});
            skLineSegment(sketch, "E529", {"start": v(-0.1, -0.42) * mm, "end": v(-0.04, -0.43) * mm});
            skLineSegment(sketch, "E530", {"start": v(-0.04, -0.43) * mm, "end": v(0.02, -0.43) * mm});
            skLineSegment(sketch, "E531", {"start": v(0.02, -0.43) * mm, "end": v(0.07, -0.43) * mm});
            skLineSegment(sketch, "E532", {"start": v(0.07, -0.43) * mm, "end": v(0.13, -0.43) * mm});
            skLineSegment(sketch, "E533", {"start": v(0.13, -0.43) * mm, "end": v(0.18, -0.43) * mm});
            skLineSegment(sketch, "E534", {"start": v(0.18, -0.43) * mm, "end": v(0.23, -0.43) * mm});
            skLineSegment(sketch, "E535", {"start": v(0.23, -0.43) * mm, "end": v(0.28, -0.43) * mm});
            skLineSegment(sketch, "E536", {"start": v(0.28, -0.43) * mm, "end": v(0.32, -0.43) * mm});
            skLineSegment(sketch, "E537", {"start": v(0.32, -0.43) * mm, "end": v(0.37, -0.43) * mm});
            skLineSegment(sketch, "E538", {"start": v(0.37, -0.43) * mm, "end": v(0.41, -0.43) * mm});
            skLineSegment(sketch, "E539", {"start": v(0.41, -0.43) * mm, "end": v(0.46, -0.43) * mm});
            skLineSegment(sketch, "E540", {"start": v(0.46, -0.43) * mm, "end": v(0.5, -0.44) * mm});
            skLineSegment(sketch, "E541", {"start": v(0.5, -0.44) * mm, "end": v(0.53, -0.44) * mm});
            skLineSegment(sketch, "E542", {"start": v(0.53, -0.44) * mm, "end": v(0.57, -0.44) * mm});
            skLineSegment(sketch, "E543", {"start": v(0.57, -0.44) * mm, "end": v(0.6, -0.44) * mm});
            skLineSegment(sketch, "E544", {"start": v(0.6, -0.44) * mm, "end": v(0.64, -0.44) * mm});
            skLineSegment(sketch, "E545", {"start": v(0.64, -0.44) * mm, "end": v(0.67, -0.44) * mm});
            skLineSegment(sketch, "E546", {"start": v(0.67, -0.44) * mm, "end": v(0.7, -0.44) * mm});
            skLineSegment(sketch, "E547", {"start": v(0.7, -0.44) * mm, "end": v(0.73, -0.44) * mm});
            skLineSegment(sketch, "E548", {"start": v(0.73, -0.44) * mm, "end": v(0.75, -0.44) * mm});
            skLineSegment(sketch, "E549", {"start": v(0.75, -0.44) * mm, "end": v(0.77, -0.44) * mm});
            skLineSegment(sketch, "E550", {"start": v(0.77, -0.44) * mm, "end": v(0.8, -0.44) * mm});
            skLineSegment(sketch, "E551", {"start": v(0.8, -0.44) * mm, "end": v(0.82, -0.44) * mm});
            skLineSegment(sketch, "E552", {"start": v(0.82, -0.44) * mm, "end": v(0.85, -0.44) * mm});
            skLineSegment(sketch, "E553", {"start": v(0.85, -0.44) * mm, "end": v(0.87, -0.44) * mm});
            skLineSegment(sketch, "E554", {"start": v(0.87, -0.44) * mm, "end": v(0.9, -0.44) * mm});
            skLineSegment(sketch, "E555", {"start": v(0.9, -0.44) * mm, "end": v(0.91, -0.45) * mm});
            skLineSegment(sketch, "E556", {"start": v(0.91, -0.45) * mm, "end": v(0.94, -0.45) * mm});
            skLineSegment(sketch, "E557", {"start": v(0.94, -0.45) * mm, "end": v(0.96, -0.45) * mm});
            skLineSegment(sketch, "E558", {"start": v(0.96, -0.45) * mm, "end": v(0.98, -0.46) * mm});
            skLineSegment(sketch, "E559", {"start": v(0.98, -0.46) * mm, "end": v(1, -0.46) * mm});
            skLineSegment(sketch, "E560", {"start": v(1, -0.46) * mm, "end": v(1.02, -0.46) * mm});
            skLineSegment(sketch, "E561", {"start": v(1.02, -0.46) * mm, "end": v(1.05, -0.47) * mm});
            skLineSegment(sketch, "E562", {"start": v(1.05, -0.47) * mm, "end": v(1.07, -0.47) * mm});
            skLineSegment(sketch, "E563", {"start": v(1.07, -0.47) * mm, "end": v(1.09, -0.48) * mm});
            skLineSegment(sketch, "E564", {"start": v(1.09, -0.48) * mm, "end": v(1.1, -0.48) * mm});
            skLineSegment(sketch, "E565", {"start": v(1.1, -0.48) * mm, "end": v(1.13, -0.49) * mm});
            skLineSegment(sketch, "E566", {"start": v(1.13, -0.49) * mm, "end": v(1.15, -0.5) * mm});
            skLineSegment(sketch, "E567", {"start": v(1.15, -0.5) * mm, "end": v(1.17, -0.5) * mm});
            skLineSegment(sketch, "E568", {"start": v(1.17, -0.5) * mm, "end": v(1.19, -0.5) * mm});
            skLineSegment(sketch, "E569", {"start": v(1.19, -0.5) * mm, "end": v(1.2, -0.51) * mm});
            skLineSegment(sketch, "E570", {"start": v(1.2, -0.51) * mm, "end": v(1.23, -0.52) * mm});
            skLineSegment(sketch, "E571", {"start": v(1.23, -0.52) * mm, "end": v(1.25, -0.53) * mm});
            skLineSegment(sketch, "E572", {"start": v(1.25, -0.53) * mm, "end": v(1.26, -0.53) * mm});
            skLineSegment(sketch, "E573", {"start": v(1.26, -0.53) * mm, "end": v(1.28, -0.54) * mm});
            skLineSegment(sketch, "E574", {"start": v(1.28, -0.54) * mm, "end": v(1.3, -0.55) * mm});
            skLineSegment(sketch, "E575", {"start": v(1.3, -0.55) * mm, "end": v(1.32, -0.56) * mm});
            skLineSegment(sketch, "E576", {"start": v(1.32, -0.56) * mm, "end": v(1.34, -0.57) * mm});
            skLineSegment(sketch, "E577", {"start": v(1.34, -0.57) * mm, "end": v(1.36, -0.57) * mm});
            skLineSegment(sketch, "E578", {"start": v(1.36, -0.57) * mm, "end": v(1.37, -0.58) * mm});
            skLineSegment(sketch, "E579", {"start": v(1.37, -0.58) * mm, "end": v(1.4, -0.6) * mm});
            skLineSegment(sketch, "E580", {"start": v(1.4, -0.6) * mm, "end": v(1.41, -0.61) * mm});
            skLineSegment(sketch, "E581", {"start": v(1.41, -0.61) * mm, "end": v(1.43, -0.63) * mm});
            skLineSegment(sketch, "E582", {"start": v(1.43, -0.63) * mm, "end": v(1.45, -0.64) * mm});
            skLineSegment(sketch, "E583", {"start": v(1.45, -0.64) * mm, "end": v(1.47, -0.66) * mm});
            skLineSegment(sketch, "E584", {"start": v(1.47, -0.66) * mm, "end": v(1.48, -0.68) * mm});
            skLineSegment(sketch, "E585", {"start": v(1.48, -0.68) * mm, "end": v(1.5, -0.7) * mm});
            skLineSegment(sketch, "E586", {"start": v(1.5, -0.7) * mm, "end": v(1.5, -0.7) * mm});
            skLineSegment(sketch, "E587", {"start": v(1.5, -0.7) * mm, "end": v(1.52, -0.73) * mm});
            skLineSegment(sketch, "E588", {"start": v(1.52, -0.73) * mm, "end": v(1.53, -0.74) * mm});
            skLineSegment(sketch, "E589", {"start": v(1.53, -0.74) * mm, "end": v(1.53, -0.76) * mm});
            skLineSegment(sketch, "E590", {"start": v(1.53, -0.76) * mm, "end": v(1.54, -0.77) * mm});
            skLineSegment(sketch, "E591", {"start": v(1.54, -0.77) * mm, "end": v(1.54, -0.79) * mm});
            skLineSegment(sketch, "E592", {"start": v(1.54, -0.79) * mm, "end": v(1.55, -0.8) * mm});
            skLineSegment(sketch, "E593", {"start": v(1.55, -0.8) * mm, "end": v(1.55, -0.82) * mm});
            skLineSegment(sketch, "E594", {"start": v(1.55, -0.82) * mm, "end": v(1.55, -0.83) * mm});
            skLineSegment(sketch, "E595", {"start": v(1.55, -0.83) * mm, "end": v(1.55, -0.85) * mm});
            skLineSegment(sketch, "E596", {"start": v(1.55, -0.85) * mm, "end": v(1.54, -0.86) * mm});
            skLineSegment(sketch, "E597", {"start": v(1.54, -0.86) * mm, "end": v(1.54, -0.88) * mm});
            skLineSegment(sketch, "E598", {"start": v(1.54, -0.88) * mm, "end": v(1.53, -0.9) * mm});
            skLineSegment(sketch, "E599", {"start": v(1.53, -0.9) * mm, "end": v(1.52, -0.9) * mm});
            skLineSegment(sketch, "E600", {"start": v(1.52, -0.9) * mm, "end": v(1.52, -0.92) * mm});
            skLineSegment(sketch, "E601", {"start": v(1.52, -0.92) * mm, "end": v(1.5, -0.93) * mm});
            skLineSegment(sketch, "E602", {"start": v(1.5, -0.93) * mm, "end": v(1.5, -0.95) * mm});
            skLineSegment(sketch, "E603", {"start": v(1.5, -0.95) * mm, "end": v(1.48, -0.96) * mm});
            skLineSegment(sketch, "E604", {"start": v(1.48, -0.96) * mm, "end": v(1.46, -0.97) * mm});
            skLineSegment(sketch, "E605", {"start": v(1.46, -0.97) * mm, "end": v(1.45, -0.99) * mm});
            skLineSegment(sketch, "E606", {"start": v(1.45, -0.99) * mm, "end": v(1.43, -1) * mm});
            skLineSegment(sketch, "E607", {"start": v(1.43, -1) * mm, "end": v(1.4, -1.01) * mm});
            skLineSegment(sketch, "E608", {"start": v(1.4, -1.01) * mm, "end": v(1.39, -1.03) * mm});
            skLineSegment(sketch, "E609", {"start": v(1.39, -1.03) * mm, "end": v(1.36, -1.04) * mm});
            skLineSegment(sketch, "E610", {"start": v(1.36, -1.04) * mm, "end": v(1.34, -1.05) * mm});
            skLineSegment(sketch, "E611", {"start": v(1.34, -1.05) * mm, "end": v(1.31, -1.06) * mm});
            skLineSegment(sketch, "E612", {"start": v(1.31, -1.06) * mm, "end": v(1.24, -1.06) * mm});
            skLineSegment(sketch, "E613", {"start": v(1.24, -1.06) * mm, "end": v(1.18, -1.05) * mm});
            skLineSegment(sketch, "E614", {"start": v(1.18, -1.05) * mm, "end": v(1.11, -1.04) * mm});
            skLineSegment(sketch, "E615", {"start": v(1.11, -1.04) * mm, "end": v(1.04, -1.03) * mm});
            skLineSegment(sketch, "E616", {"start": v(1.04, -1.03) * mm, "end": v(0.98, -1.03) * mm});
            skLineSegment(sketch, "E617", {"start": v(0.98, -1.03) * mm, "end": v(0.92, -1.02) * mm});
            skLineSegment(sketch, "E618", {"start": v(0.92, -1.02) * mm, "end": v(0.85, -1.02) * mm});
            skLineSegment(sketch, "E619", {"start": v(0.85, -1.02) * mm, "end": v(0.79, -1.01) * mm});
            skLineSegment(sketch, "E620", {"start": v(0.79, -1.01) * mm, "end": v(0.73, -1) * mm});
            skLineSegment(sketch, "E621", {"start": v(0.73, -1) * mm, "end": v(0.67, -1) * mm});
            skLineSegment(sketch, "E622", {"start": v(0.67, -1) * mm, "end": v(0.6, -1) * mm});
            skLineSegment(sketch, "E623", {"start": v(0.6, -1) * mm, "end": v(0.55, -1) * mm});
            skLineSegment(sketch, "E624", {"start": v(0.55, -1) * mm, "end": v(0.49, -0.99) * mm});
            skLineSegment(sketch, "E625", {"start": v(0.49, -0.99) * mm, "end": v(0.43, -0.98) * mm});
            skLineSegment(sketch, "E626", {"start": v(0.43, -0.98) * mm, "end": v(0.37, -0.98) * mm});
            skLineSegment(sketch, "E627", {"start": v(0.37, -0.98) * mm, "end": v(0.32, -0.97) * mm});
            skLineSegment(sketch, "E628", {"start": v(0.32, -0.97) * mm, "end": v(0.26, -0.97) * mm});
            skLineSegment(sketch, "E629", {"start": v(0.26, -0.97) * mm, "end": v(0.2, -0.97) * mm});
            skLineSegment(sketch, "E630", {"start": v(0.2, -0.97) * mm, "end": v(0.15, -0.96) * mm});
            skLineSegment(sketch, "E631", {"start": v(0.15, -0.96) * mm, "end": v(0.1, -0.96) * mm});
            skLineSegment(sketch, "E632", {"start": v(0.1, -0.96) * mm, "end": v(0.04, -0.96) * mm});
            skLineSegment(sketch, "E633", {"start": v(0.04, -0.96) * mm, "end": v(0, -0.96) * mm});
            skLineSegment(sketch, "E634", {"start": v(0, -0.96) * mm, "end": v(-0.06, -0.95) * mm});
            skLineSegment(sketch, "E635", {"start": v(-0.06, -0.95) * mm, "end": v(-0.1, -0.95) * mm});
            skLineSegment(sketch, "E636", {"start": v(-0.1, -0.95) * mm, "end": v(-0.16, -0.95) * mm});
            skLineSegment(sketch, "E637", {"start": v(-0.16, -0.95) * mm, "end": v(-0.2, -0.95) * mm});
            skLineSegment(sketch, "E638", {"start": v(-0.2, -0.95) * mm, "end": v(-0.26, -0.95) * mm});
            skLineSegment(sketch, "E639", {"start": v(-0.26, -0.95) * mm, "end": v(-0.3, -0.95) * mm});
            skLineSegment(sketch, "E640", {"start": v(-0.3, -0.95) * mm, "end": v(-0.35, -0.95) * mm});
            skLineSegment(sketch, "E641", {"start": v(-0.35, -0.95) * mm, "end": v(-0.4, -0.95) * mm});
            skLineSegment(sketch, "E642", {"start": v(-0.4, -0.95) * mm, "end": v(-0.44, -0.95) * mm});
            skLineSegment(sketch, "E643", {"start": v(-0.44, -0.95) * mm, "end": v(-0.49, -0.95) * mm});
            skLineSegment(sketch, "E644", {"start": v(-0.49, -0.95) * mm, "end": v(-0.5, -0.95) * mm});
            skLineSegment(sketch, "E645", {"start": v(-0.5, -0.95) * mm, "end": v(-0.52, -0.95) * mm});
            skLineSegment(sketch, "E646", {"start": v(-0.52, -0.95) * mm, "end": v(-0.54, -0.95) * mm});
            skLineSegment(sketch, "E647", {"start": v(-0.54, -0.95) * mm, "end": v(-0.55, -0.95) * mm});
            skLineSegment(sketch, "E648", {"start": v(-0.55, -0.95) * mm, "end": v(-0.57, -0.95) * mm});
            skLineSegment(sketch, "E649", {"start": v(-0.57, -0.95) * mm, "end": v(-0.59, -0.95) * mm});
            skLineSegment(sketch, "E650", {"start": v(-0.59, -0.95) * mm, "end": v(-0.6, -0.95) * mm});
            skLineSegment(sketch, "E651", {"start": v(-0.6, -0.95) * mm, "end": v(-0.62, -0.95) * mm});
            skLineSegment(sketch, "E652", {"start": v(-0.62, -0.95) * mm, "end": v(-0.64, -0.95) * mm});
            skLineSegment(sketch, "E653", {"start": v(-0.64, -0.95) * mm, "end": v(-0.65, -0.95) * mm});
            skLineSegment(sketch, "E654", {"start": v(-0.65, -0.95) * mm, "end": v(-0.67, -0.95) * mm});
            skLineSegment(sketch, "E655", {"start": v(-0.67, -0.95) * mm, "end": v(-0.68, -0.95) * mm});
            skLineSegment(sketch, "E656", {"start": v(-0.68, -0.95) * mm, "end": v(-0.7, -0.95) * mm});
            skLineSegment(sketch, "E657", {"start": v(-0.7, -0.95) * mm, "end": v(-0.72, -0.95) * mm});
            skLineSegment(sketch, "E658", {"start": v(-0.72, -0.95) * mm, "end": v(-0.73, -0.95) * mm});
            skLineSegment(sketch, "E659", {"start": v(-0.73, -0.95) * mm, "end": v(-0.75, -0.96) * mm});
            skLineSegment(sketch, "E660", {"start": v(-0.75, -0.96) * mm, "end": v(-0.76, -0.96) * mm});
            skLineSegment(sketch, "E661", {"start": v(-0.76, -0.96) * mm, "end": v(-0.78, -0.96) * mm});
            skLineSegment(sketch, "E662", {"start": v(-0.78, -0.96) * mm, "end": v(-0.8, -0.96) * mm});
            skLineSegment(sketch, "E663", {"start": v(-0.8, -0.96) * mm, "end": v(-0.81, -0.96) * mm});
            skLineSegment(sketch, "E664", {"start": v(-0.81, -0.96) * mm, "end": v(-0.83, -0.96) * mm});
            skLineSegment(sketch, "E665", {"start": v(-0.83, -0.96) * mm, "end": v(-0.84, -0.96) * mm});
            skLineSegment(sketch, "E666", {"start": v(-0.84, -0.96) * mm, "end": v(-0.86, -0.97) * mm});
            skLineSegment(sketch, "E667", {"start": v(-0.86, -0.97) * mm, "end": v(-0.87, -0.97) * mm});
            skLineSegment(sketch, "E668", {"start": v(-0.87, -0.97) * mm, "end": v(-0.89, -0.97) * mm});
            skLineSegment(sketch, "E669", {"start": v(-0.89, -0.97) * mm, "end": v(-0.9, -0.97) * mm});
            skLineSegment(sketch, "E670", {"start": v(-0.9, -0.97) * mm, "end": v(-0.92, -0.97) * mm});
            skLineSegment(sketch, "E671", {"start": v(-0.92, -0.97) * mm, "end": v(-0.93, -0.98) * mm});
            skLineSegment(sketch, "E672", {"start": v(-0.93, -0.98) * mm, "end": v(-0.95, -0.98) * mm});
            skLineSegment(sketch, "E673", {"start": v(-0.95, -0.98) * mm, "end": v(-0.96, -0.98) * mm});
            skLineSegment(sketch, "E674", {"start": v(-0.96, -0.98) * mm, "end": v(-0.98, -0.98) * mm});
            skLineSegment(sketch, "E675", {"start": v(-0.98, -0.98) * mm, "end": v(-1, -0.98) * mm});
            skLineSegment(sketch, "E676", {"start": v(-1, -0.98) * mm, "end": v(-1, -1.02) * mm});
            skLineSegment(sketch, "E677", {"start": v(-1, -1.02) * mm, "end": v(-1, -1.06) * mm});
            skLineSegment(sketch, "E678", {"start": v(-1, -1.06) * mm, "end": v(-1, -1.1) * mm});
            skLineSegment(sketch, "E679", {"start": v(-1, -1.1) * mm, "end": v(-1, -1.14) * mm});
            skLineSegment(sketch, "E680", {"start": v(-1, -1.14) * mm, "end": v(-1, -1.18) * mm});
            skLineSegment(sketch, "E681", {"start": v(-1, -1.18) * mm, "end": v(-1, -1.23) * mm});
            skLineSegment(sketch, "E682", {"start": v(-1, -1.23) * mm, "end": v(-1, -1.28) * mm});
            skLineSegment(sketch, "E683", {"start": v(-1, -1.28) * mm, "end": v(-1, -1.33) * mm});
            skLineSegment(sketch, "E684", {"start": v(-1, -1.33) * mm, "end": v(-0.99, -1.38) * mm});
            skLineSegment(sketch, "E685", {"start": v(-0.99, -1.38) * mm, "end": v(-0.99, -1.44) * mm});
            skLineSegment(sketch, "E686", {"start": v(-0.99, -1.44) * mm, "end": v(-0.99, -1.5) * mm});
            skLineSegment(sketch, "E687", {"start": v(-0.99, -1.5) * mm, "end": v(-0.99, -1.56) * mm});
            skLineSegment(sketch, "E688", {"start": v(-0.99, -1.56) * mm, "end": v(-0.99, -1.62) * mm});
            skLineSegment(sketch, "E689", {"start": v(-0.99, -1.62) * mm, "end": v(-0.99, -1.69) * mm});
            skLineSegment(sketch, "E690", {"start": v(-0.99, -1.69) * mm, "end": v(-0.98, -1.75) * mm});
            skLineSegment(sketch, "E691", {"start": v(-0.98, -1.75) * mm, "end": v(-0.98, -1.82) * mm});
            skLineSegment(sketch, "E692", {"start": v(-0.98, -1.82) * mm, "end": v(-0.98, -1.9) * mm});
            skLineSegment(sketch, "E693", {"start": v(-0.98, -1.9) * mm, "end": v(-0.98, -1.97) * mm});
            skLineSegment(sketch, "E694", {"start": v(-0.98, -1.97) * mm, "end": v(-0.98, -2.05) * mm});
            skLineSegment(sketch, "E695", {"start": v(-0.98, -2.05) * mm, "end": v(-0.98, -2.13) * mm});
            skLineSegment(sketch, "E696", {"start": v(-0.98, -2.13) * mm, "end": v(-0.98, -2.2) * mm});
            skLineSegment(sketch, "E697", {"start": v(-0.98, -2.2) * mm, "end": v(-0.97, -2.29) * mm});
            skLineSegment(sketch, "E698", {"start": v(-0.97, -2.29) * mm, "end": v(-0.97, -2.38) * mm});
            skLineSegment(sketch, "E699", {"start": v(-0.97, -2.38) * mm, "end": v(-0.97, -2.46) * mm});
            skLineSegment(sketch, "E700", {"start": v(-0.97, -2.46) * mm, "end": v(-0.97, -2.55) * mm});
            skLineSegment(sketch, "E701", {"start": v(-0.97, -2.55) * mm, "end": v(-0.97, -2.65) * mm});
            skLineSegment(sketch, "E702", {"start": v(-0.97, -2.65) * mm, "end": v(-0.96, -2.74) * mm});
            skLineSegment(sketch, "E703", {"start": v(-0.96, -2.74) * mm, "end": v(-0.96, -2.84) * mm});
            skLineSegment(sketch, "E704", {"start": v(-0.96, -2.84) * mm, "end": v(-0.96, -2.94) * mm});
            skLineSegment(sketch, "E705", {"start": v(-0.96, -2.94) * mm, "end": v(-0.96, -3.04) * mm});
            skLineSegment(sketch, "E706", {"start": v(-0.96, -3.04) * mm, "end": v(-0.96, -3.14) * mm});
            skLineSegment(sketch, "E707", {"start": v(-0.96, -3.14) * mm, "end": v(-0.95, -3.25) * mm});
            skLineSegment(sketch, "E708", {"start": v(-0.95, -3.25) * mm, "end": v(-0.95, -3.27) * mm});
            skLineSegment(sketch, "E709", {"start": v(-0.95, -3.27) * mm, "end": v(-0.95, -3.28) * mm});
            skLineSegment(sketch, "E710", {"start": v(-0.95, -3.28) * mm, "end": v(-0.96, -3.3) * mm});
            skLineSegment(sketch, "E711", {"start": v(-0.96, -3.3) * mm, "end": v(-0.96, -3.32) * mm});
            skLineSegment(sketch, "E712", {"start": v(-0.96, -3.32) * mm, "end": v(-0.96, -3.33) * mm});
            skLineSegment(sketch, "E713", {"start": v(-0.96, -3.33) * mm, "end": v(-0.96, -3.35) * mm});
            skLineSegment(sketch, "E714", {"start": v(-0.96, -3.35) * mm, "end": v(-0.96, -3.36) * mm});
            skLineSegment(sketch, "E715", {"start": v(-0.96, -3.36) * mm, "end": v(-0.97, -3.37) * mm});
            skLineSegment(sketch, "E716", {"start": v(-0.97, -3.37) * mm, "end": v(-0.97, -3.39) * mm});
            skLineSegment(sketch, "E717", {"start": v(-0.97, -3.39) * mm, "end": v(-0.97, -3.4) * mm});
            skLineSegment(sketch, "E718", {"start": v(-0.97, -3.4) * mm, "end": v(-0.98, -3.41) * mm});
            skLineSegment(sketch, "E719", {"start": v(-0.98, -3.41) * mm, "end": v(-0.98, -3.43) * mm});
            skLineSegment(sketch, "E720", {"start": v(-0.98, -3.43) * mm, "end": v(-0.99, -3.44) * mm});
            skLineSegment(sketch, "E721", {"start": v(-0.99, -3.44) * mm, "end": v(-1, -3.45) * mm});
            skLineSegment(sketch, "E722", {"start": v(-1, -3.45) * mm, "end": v(-1, -3.46) * mm});
            skLineSegment(sketch, "E723", {"start": v(-1, -3.46) * mm, "end": v(-1, -3.47) * mm});
            skLineSegment(sketch, "E724", {"start": v(-1, -3.47) * mm, "end": v(-1, -3.49) * mm});
            skLineSegment(sketch, "E725", {"start": v(-1, -3.49) * mm, "end": v(-1.02, -3.5) * mm});
            skLineSegment(sketch, "E726", {"start": v(-1.02, -3.5) * mm, "end": v(-1.02, -3.5) * mm});
            skLineSegment(sketch, "E727", {"start": v(-1.02, -3.5) * mm, "end": v(-1.03, -3.52) * mm});
            skLineSegment(sketch, "E728", {"start": v(-1.03, -3.52) * mm, "end": v(-1.04, -3.52) * mm});
            skLineSegment(sketch, "E729", {"start": v(-1.04, -3.52) * mm, "end": v(-1.05, -3.53) * mm});
            skLineSegment(sketch, "E730", {"start": v(-1.05, -3.53) * mm, "end": v(-1.05, -3.54) * mm});
            skLineSegment(sketch, "E731", {"start": v(-1.05, -3.54) * mm, "end": v(-1.06, -3.55) * mm});
            skLineSegment(sketch, "E732", {"start": v(-1.06, -3.55) * mm, "end": v(-1.07, -3.56) * mm});
            skLineSegment(sketch, "E733", {"start": v(-1.07, -3.56) * mm, "end": v(-1.08, -3.57) * mm});
            skLineSegment(sketch, "E734", {"start": v(-1.08, -3.57) * mm, "end": v(-1.1, -3.57) * mm});
            skLineSegment(sketch, "E735", {"start": v(-1.1, -3.57) * mm, "end": v(-1.1, -3.58) * mm});
            skLineSegment(sketch, "E736", {"start": v(-1.1, -3.58) * mm, "end": v(-1.11, -3.58) * mm});
            skLineSegment(sketch, "E737", {"start": v(-1.11, -3.58) * mm, "end": v(-1.13, -3.6) * mm});
            skLineSegment(sketch, "E738", {"start": v(-1.13, -3.6) * mm, "end": v(-1.14, -3.6) * mm});
            skLineSegment(sketch, "E739", {"start": v(-1.14, -3.6) * mm, "end": v(-1.15, -3.6) * mm});
            skLineSegment(sketch, "E740", {"start": v(-1.15, -3.6) * mm, "end": v(-1.17, -3.6) * mm});
            skLineSegment(sketch, "E741", {"start": v(-1.17, -3.6) * mm, "end": v(-1.2, -3.6) * mm});
            skLineSegment(sketch, "E742", {"start": v(-1.2, -3.6) * mm, "end": v(-1.21, -3.58) * mm});
            skLineSegment(sketch, "E743", {"start": v(-1.21, -3.58) * mm, "end": v(-1.23, -3.58) * mm});
            skLineSegment(sketch, "E744", {"start": v(-1.23, -3.58) * mm, "end": v(-1.25, -3.57) * mm});
            skLineSegment(sketch, "E745", {"start": v(-1.25, -3.57) * mm, "end": v(-1.27, -3.56) * mm});
            skLineSegment(sketch, "E746", {"start": v(-1.27, -3.56) * mm, "end": v(-1.3, -3.55) * mm});
            skLineSegment(sketch, "E747", {"start": v(-1.3, -3.55) * mm, "end": v(-1.31, -3.54) * mm});
            skLineSegment(sketch, "E748", {"start": v(-1.31, -3.54) * mm, "end": v(-1.33, -3.53) * mm});
            skLineSegment(sketch, "E749", {"start": v(-1.33, -3.53) * mm, "end": v(-1.35, -3.52) * mm});
            skLineSegment(sketch, "E750", {"start": v(-1.35, -3.52) * mm, "end": v(-1.37, -3.5) * mm});
            skLineSegment(sketch, "E751", {"start": v(-1.37, -3.5) * mm, "end": v(-1.39, -3.5) * mm});
            skLineSegment(sketch, "E752", {"start": v(-1.39, -3.5) * mm, "end": v(-1.4, -3.48) * mm});
            skLineSegment(sketch, "E753", {"start": v(-1.4, -3.48) * mm, "end": v(-1.42, -3.47) * mm});
            skLineSegment(sketch, "E754", {"start": v(-1.42, -3.47) * mm, "end": v(-1.44, -3.45) * mm});
            skLineSegment(sketch, "E755", {"start": v(-1.44, -3.45) * mm, "end": v(-1.45, -3.44) * mm});
            skLineSegment(sketch, "E756", {"start": v(-1.45, -3.44) * mm, "end": v(-1.47, -3.42) * mm});
            skLineSegment(sketch, "E757", {"start": v(-1.47, -3.42) * mm, "end": v(-1.48, -3.4) * mm});
            skLineSegment(sketch, "E758", {"start": v(-1.48, -3.4) * mm, "end": v(-1.5, -3.38) * mm});
            skLineSegment(sketch, "E759", {"start": v(-1.5, -3.38) * mm, "end": v(-1.51, -3.37) * mm});
            skLineSegment(sketch, "E760", {"start": v(-1.51, -3.37) * mm, "end": v(-1.53, -3.35) * mm});
            skLineSegment(sketch, "E761", {"start": v(-1.53, -3.35) * mm, "end": v(-1.54, -3.33) * mm});
            skLineSegment(sketch, "E762", {"start": v(-1.54, -3.33) * mm, "end": v(-1.55, -3.3) * mm});
            skLineSegment(sketch, "E763", {"start": v(-1.55, -3.3) * mm, "end": v(-1.57, -3.29) * mm});
            skLineSegment(sketch, "E764", {"start": v(-1.57, -3.29) * mm, "end": v(-1.58, -3.26) * mm});
            skLineSegment(sketch, "E765", {"start": v(-1.58, -3.26) * mm, "end": v(-1.6, -3.24) * mm});
            skLineSegment(sketch, "E766", {"start": v(-1.6, -3.24) * mm, "end": v(-1.6, -3.22) * mm});
            skLineSegment(sketch, "E767", {"start": v(-1.6, -3.22) * mm, "end": v(-1.61, -3.2) * mm});
            skLineSegment(sketch, "E768", {"start": v(-1.61, -3.2) * mm, "end": v(-1.63, -3.17) * mm});
            skLineSegment(sketch, "E769", {"start": v(-1.63, -3.17) * mm, "end": v(-1.64, -3.15) * mm});
            skLineSegment(sketch, "E770", {"start": v(-1.64, -3.15) * mm, "end": v(-1.65, -3.12) * mm});
            skLineSegment(sketch, "E771", {"start": v(-1.65, -3.12) * mm, "end": v(-1.66, -3.1) * mm});
            skLineSegment(sketch, "E772", {"start": v(-1.66, -3.1) * mm, "end": v(-1.66, -3.07) * mm});
            skLineSegment(sketch, "E773", {"start": v(-1.66, -3.07) * mm, "end": v(-1.66, -3.05) * mm});
            skLineSegment(sketch, "E774", {"start": v(-1.66, -3.05) * mm, "end": v(-1.66, -3.03) * mm});
            skLineSegment(sketch, "E775", {"start": v(-1.66, -3.03) * mm, "end": v(-1.67, -3.01) * mm});
            skLineSegment(sketch, "E776", {"start": v(-1.67, -3.01) * mm, "end": v(-1.67, -2.99) * mm});
            skLineSegment(sketch, "E777", {"start": v(-1.67, -2.99) * mm, "end": v(-1.67, -2.97) * mm});
            skLineSegment(sketch, "E778", {"start": v(-1.67, -2.97) * mm, "end": v(-1.67, -2.94) * mm});
            skLineSegment(sketch, "E779", {"start": v(-1.67, -2.94) * mm, "end": v(-1.67, -2.92) * mm});
            skLineSegment(sketch, "E780", {"start": v(-1.67, -2.92) * mm, "end": v(-1.68, -2.9) * mm});
            skLineSegment(sketch, "E781", {"start": v(-1.68, -2.9) * mm, "end": v(-1.68, -2.87) * mm});
            skLineSegment(sketch, "E782", {"start": v(-1.68, -2.87) * mm, "end": v(-1.68, -2.85) * mm});
            skLineSegment(sketch, "E783", {"start": v(-1.68, -2.85) * mm, "end": v(-1.68, -2.82) * mm});
            skLineSegment(sketch, "E784", {"start": v(-1.68, -2.82) * mm, "end": v(-1.68, -2.8) * mm});
            skLineSegment(sketch, "E785", {"start": v(-1.68, -2.8) * mm, "end": v(-1.68, -2.77) * mm});
            skLineSegment(sketch, "E786", {"start": v(-1.68, -2.77) * mm, "end": v(-1.69, -2.74) * mm});
            skLineSegment(sketch, "E787", {"start": v(-1.69, -2.74) * mm, "end": v(-1.69, -2.71) * mm});
            skLineSegment(sketch, "E788", {"start": v(-1.69, -2.71) * mm, "end": v(-1.69, -2.68) * mm});
            skLineSegment(sketch, "E789", {"start": v(-1.69, -2.68) * mm, "end": v(-1.69, -2.66) * mm});
            skLineSegment(sketch, "E790", {"start": v(-1.69, -2.66) * mm, "end": v(-1.7, -2.63) * mm});
            skLineSegment(sketch, "E791", {"start": v(-1.7, -2.63) * mm, "end": v(-1.7, -2.6) * mm});
            skLineSegment(sketch, "E792", {"start": v(-1.7, -2.6) * mm, "end": v(-1.7, -2.57) * mm});
            skLineSegment(sketch, "E793", {"start": v(-1.7, -2.57) * mm, "end": v(-1.7, -2.53) * mm});
            skLineSegment(sketch, "E794", {"start": v(-1.7, -2.53) * mm, "end": v(-1.7, -2.5) * mm});
            skLineSegment(sketch, "E795", {"start": v(-1.7, -2.5) * mm, "end": v(-1.7, -2.47) * mm});
            skLineSegment(sketch, "E796", {"start": v(-1.7, -2.47) * mm, "end": v(-1.7, -2.44) * mm});
            skLineSegment(sketch, "E797", {"start": v(-1.7, -2.44) * mm, "end": v(-1.7, -2.4) * mm});
            skLineSegment(sketch, "E798", {"start": v(-1.7, -2.4) * mm, "end": v(-1.7, -2.37) * mm});
            skLineSegment(sketch, "E799", {"start": v(-1.7, -2.37) * mm, "end": v(-1.7, -2.34) * mm});
            skLineSegment(sketch, "E800", {"start": v(-1.7, -2.34) * mm, "end": v(-1.7, -2.3) * mm});
            skLineSegment(sketch, "E801", {"start": v(-1.7, -2.3) * mm, "end": v(-1.7, -2.27) * mm});
            skLineSegment(sketch, "E802", {"start": v(-1.7, -2.27) * mm, "end": v(-1.7, -2.23) * mm});
            skLineSegment(sketch, "E803", {"start": v(-1.7, -2.23) * mm, "end": v(-1.7, -2.2) * mm});
            skLineSegment(sketch, "E804", {"start": v(-1.7, -2.2) * mm, "end": v(-1.7, -1.06) * mm});
            skLineSegment(sketch, "E805", {"start": v(-1.7, -1.06) * mm, "end": v(-1.75, -1.07) * mm});
            skLineSegment(sketch, "E806", {"start": v(-1.75, -1.07) * mm, "end": v(-1.8, -1.07) * mm});
            skLineSegment(sketch, "E807", {"start": v(-1.8, -1.07) * mm, "end": v(-1.86, -1.08) * mm});
            skLineSegment(sketch, "E808", {"start": v(-1.86, -1.08) * mm, "end": v(-1.91, -1.08) * mm});
            skLineSegment(sketch, "E809", {"start": v(-1.91, -1.08) * mm, "end": v(-1.97, -1.08) * mm});
            skLineSegment(sketch, "E810", {"start": v(-1.97, -1.08) * mm, "end": v(-2.02, -1.09) * mm});
            skLineSegment(sketch, "E811", {"start": v(-2.02, -1.09) * mm, "end": v(-2.07, -1.1) * mm});
            skLineSegment(sketch, "E812", {"start": v(-2.07, -1.1) * mm, "end": v(-2.12, -1.1) * mm});
            skLineSegment(sketch, "E813", {"start": v(-2.12, -1.1) * mm, "end": v(-2.16, -1.1) * mm});
            skLineSegment(sketch, "E814", {"start": v(-2.16, -1.1) * mm, "end": v(-2.21, -1.1) * mm});
            skLineSegment(sketch, "E815", {"start": v(-2.21, -1.1) * mm, "end": v(-2.26, -1.1) * mm});
            skLineSegment(sketch, "E816", {"start": v(-2.26, -1.1) * mm, "end": v(-2.3, -1.1) * mm});
            skLineSegment(sketch, "E817", {"start": v(-2.3, -1.1) * mm, "end": v(-2.35, -1.11) * mm});
            skLineSegment(sketch, "E818", {"start": v(-2.35, -1.11) * mm, "end": v(-2.4, -1.12) * mm});
            skLineSegment(sketch, "E819", {"start": v(-2.4, -1.12) * mm, "end": v(-2.44, -1.12) * mm});
            skLineSegment(sketch, "E820", {"start": v(-2.44, -1.12) * mm, "end": v(-2.48, -1.12) * mm});
            skLineSegment(sketch, "E821", {"start": v(-2.48, -1.12) * mm, "end": v(-2.52, -1.12) * mm});
            skLineSegment(sketch, "E822", {"start": v(-2.52, -1.12) * mm, "end": v(-2.56, -1.13) * mm});
            skLineSegment(sketch, "E823", {"start": v(-2.56, -1.13) * mm, "end": v(-2.6, -1.13) * mm});
            skLineSegment(sketch, "E824", {"start": v(-2.6, -1.13) * mm, "end": v(-2.64, -1.13) * mm});
            skLineSegment(sketch, "E825", {"start": v(-2.64, -1.13) * mm, "end": v(-2.67, -1.13) * mm});
            skLineSegment(sketch, "E826", {"start": v(-2.67, -1.13) * mm, "end": v(-2.71, -1.13) * mm});
            skLineSegment(sketch, "E827", {"start": v(-2.71, -1.13) * mm, "end": v(-2.75, -1.13) * mm});
            skLineSegment(sketch, "E828", {"start": v(-2.75, -1.13) * mm, "end": v(-2.78, -1.14) * mm});
            skLineSegment(sketch, "E829", {"start": v(-2.78, -1.14) * mm, "end": v(-2.81, -1.14) * mm});
            skLineSegment(sketch, "E830", {"start": v(-2.81, -1.14) * mm, "end": v(-2.85, -1.14) * mm});
            skLineSegment(sketch, "E831", {"start": v(-2.85, -1.14) * mm, "end": v(-2.88, -1.14) * mm});
            skLineSegment(sketch, "E832", {"start": v(-2.88, -1.14) * mm, "end": v(-2.9, -1.14) * mm});
            skLineSegment(sketch, "E833", {"start": v(-2.9, -1.14) * mm, "end": v(-2.94, -1.14) * mm});
            skLineSegment(sketch, "E834", {"start": v(-2.94, -1.14) * mm, "end": v(-2.97, -1.14) * mm});
            skLineSegment(sketch, "E835", {"start": v(-2.97, -1.14) * mm, "end": v(-3, -1.14) * mm});
            skLineSegment(sketch, "E836", {"start": v(-3, -1.14) * mm, "end": v(-3.02, -1.14) * mm});
            skLineSegment(sketch, "E837", {"start": v(-3.02, -1.14) * mm, "end": v(-3.04, -1.14) * mm});
            skLineSegment(sketch, "E838", {"start": v(-3.04, -1.14) * mm, "end": v(-3.05, -1.14) * mm});
            skLineSegment(sketch, "E839", {"start": v(-3.05, -1.14) * mm, "end": v(-3.07, -1.13) * mm});
            skLineSegment(sketch, "E840", {"start": v(-3.07, -1.13) * mm, "end": v(-3.08, -1.13) * mm});
            skLineSegment(sketch, "E841", {"start": v(-3.08, -1.13) * mm, "end": v(-3.1, -1.13) * mm});
            skLineSegment(sketch, "E842", {"start": v(-3.1, -1.13) * mm, "end": v(-3.11, -1.12) * mm});
            skLineSegment(sketch, "E843", {"start": v(-3.11, -1.12) * mm, "end": v(-3.13, -1.12) * mm});
            skLineSegment(sketch, "E844", {"start": v(-3.13, -1.12) * mm, "end": v(-3.14, -1.12) * mm});
            skLineSegment(sketch, "E845", {"start": v(-3.14, -1.12) * mm, "end": v(-3.15, -1.12) * mm});
            skLineSegment(sketch, "E846", {"start": v(-3.15, -1.12) * mm, "end": v(-3.17, -1.11) * mm});
            skLineSegment(sketch, "E847", {"start": v(-3.17, -1.11) * mm, "end": v(-3.18, -1.1) * mm});
            skLineSegment(sketch, "E848", {"start": v(-3.18, -1.1) * mm, "end": v(-3.2, -1.1) * mm});
            skLineSegment(sketch, "E849", {"start": v(-3.2, -1.1) * mm, "end": v(-3.2, -1.1) * mm});
            skLineSegment(sketch, "E850", {"start": v(-3.2, -1.1) * mm, "end": v(-3.22, -1.1) * mm});
            skLineSegment(sketch, "E851", {"start": v(-3.22, -1.1) * mm, "end": v(-3.24, -1.1) * mm});
            skLineSegment(sketch, "E852", {"start": v(-3.24, -1.1) * mm, "end": v(-3.25, -1.1) * mm});
            skLineSegment(sketch, "E853", {"start": v(-3.25, -1.1) * mm, "end": v(-3.26, -1.09) * mm});
            skLineSegment(sketch, "E854", {"start": v(-3.26, -1.09) * mm, "end": v(-3.28, -1.08) * mm});
            skLineSegment(sketch, "E855", {"start": v(-3.28, -1.08) * mm, "end": v(-3.29, -1.08) * mm});
            skLineSegment(sketch, "E856", {"start": v(-3.29, -1.08) * mm, "end": v(-3.3, -1.08) * mm});
            skLineSegment(sketch, "E857", {"start": v(-3.3, -1.08) * mm, "end": v(-3.32, -1.07) * mm});
            skLineSegment(sketch, "E858", {"start": v(-3.32, -1.07) * mm, "end": v(-3.33, -1.07) * mm});
            skLineSegment(sketch, "E859", {"start": v(-3.33, -1.07) * mm, "end": v(-3.34, -1.06) * mm});
            skLineSegment(sketch, "E860", {"start": v(-3.34, -1.06) * mm, "end": v(-3.35, -1.06) * mm});
            skLineSegment(sketch, "E861", {"start": v(-3.35, -1.06) * mm, "end": v(-3.37, -1.06) * mm});
            skLineSegment(sketch, "E862", {"start": v(-3.37, -1.06) * mm, "end": v(-3.38, -1.05) * mm});
            skLineSegment(sketch, "E863", {"start": v(-3.38, -1.05) * mm, "end": v(-3.4, -1.05) * mm});
            skLineSegment(sketch, "E864", {"start": v(-3.4, -1.05) * mm, "end": v(-3.4, -1.04) * mm});
            skLineSegment(sketch, "E865", {"start": v(-3.4, -1.04) * mm, "end": v(-3.42, -1.04) * mm});
            skLineSegment(sketch, "E866", {"start": v(-3.42, -1.04) * mm, "end": v(-3.43, -1.03) * mm});
            skLineSegment(sketch, "E867", {"start": v(-3.43, -1.03) * mm, "end": v(-3.44, -1.03) * mm});
            skLineSegment(sketch, "E868", {"start": v(-3.44, -1.03) * mm, "end": v(-3.45, -1.02) * mm});
            skLineSegment(sketch, "E869", {"start": v(-3.45, -1.02) * mm, "end": v(-3.44, -1.04) * mm});
            skLineSegment(sketch, "E870", {"start": v(-3.44, -1.04) * mm, "end": v(-3.43, -1.05) * mm});
            skLineSegment(sketch, "E871", {"start": v(-3.43, -1.05) * mm, "end": v(-3.42, -1.06) * mm});
            skLineSegment(sketch, "E872", {"start": v(-3.42, -1.06) * mm, "end": v(-3.4, -1.07) * mm});
            skLineSegment(sketch, "E873", {"start": v(-3.4, -1.07) * mm, "end": v(-3.4, -1.08) * mm});
            skLineSegment(sketch, "E874", {"start": v(-3.4, -1.08) * mm, "end": v(-3.39, -1.1) * mm});
            skLineSegment(sketch, "E875", {"start": v(-3.39, -1.1) * mm, "end": v(-3.38, -1.1) * mm});
            skLineSegment(sketch, "E876", {"start": v(-3.38, -1.1) * mm, "end": v(-3.37, -1.12) * mm});
            skLineSegment(sketch, "E877", {"start": v(-3.37, -1.12) * mm, "end": v(-3.36, -1.13) * mm});
            skLineSegment(sketch, "E878", {"start": v(-3.36, -1.13) * mm, "end": v(-3.35, -1.14) * mm});
            skLineSegment(sketch, "E879", {"start": v(-3.35, -1.14) * mm, "end": v(-3.35, -1.15) * mm});
            skLineSegment(sketch, "E880", {"start": v(-3.35, -1.15) * mm, "end": v(-3.34, -1.16) * mm});
            skLineSegment(sketch, "E881", {"start": v(-3.34, -1.16) * mm, "end": v(-3.33, -1.17) * mm});
            skLineSegment(sketch, "E882", {"start": v(-3.33, -1.17) * mm, "end": v(-3.33, -1.18) * mm});
            skLineSegment(sketch, "E883", {"start": v(-3.33, -1.18) * mm, "end": v(-3.32, -1.19) * mm});
            skLineSegment(sketch, "E884", {"start": v(-3.32, -1.19) * mm, "end": v(-3.32, -1.2) * mm});
            skLineSegment(sketch, "E885", {"start": v(-3.32, -1.2) * mm, "end": v(-3.31, -1.2) * mm});
            skLineSegment(sketch, "E886", {"start": v(-3.31, -1.2) * mm, "end": v(-3.3, -1.22) * mm});
            skLineSegment(sketch, "E887", {"start": v(-3.3, -1.22) * mm, "end": v(-3.3, -1.23) * mm});
            skLineSegment(sketch, "E888", {"start": v(-3.3, -1.23) * mm, "end": v(-3.3, -1.24) * mm});
            skLineSegment(sketch, "E889", {"start": v(-3.3, -1.24) * mm, "end": v(-3.3, -1.25) * mm});
            skLineSegment(sketch, "E890", {"start": v(-3.3, -1.25) * mm, "end": v(-3.3, -1.26) * mm});
            skLineSegment(sketch, "E891", {"start": v(-3.3, -1.26) * mm, "end": v(-3.3, -1.26) * mm});
            skLineSegment(sketch, "E892", {"start": v(-3.3, -1.26) * mm, "end": v(-3.3, -1.27) * mm});
            skLineSegment(sketch, "E893", {"start": v(-3.3, -1.27) * mm, "end": v(-3.3, -1.28) * mm});
            skLineSegment(sketch, "E894", {"start": v(-3.3, -1.28) * mm, "end": v(-3.3, -1.29) * mm});
            skLineSegment(sketch, "E895", {"start": v(-3.3, -1.29) * mm, "end": v(-3.3, -1.3) * mm});
            skLineSegment(sketch, "E896", {"start": v(-3.3, -1.3) * mm, "end": v(-3.3, -1.3) * mm});
            skLineSegment(sketch, "E897", {"start": v(-3.3, -1.3) * mm, "end": v(-3.3, -1.31) * mm});
            skLineSegment(sketch, "E898", {"start": v(-3.3, -1.31) * mm, "end": v(-3.3, -1.32) * mm});
            skLineSegment(sketch, "E899", {"start": v(-3.3, -1.32) * mm, "end": v(-3.3, -1.33) * mm});
            skLineSegment(sketch, "E900", {"start": v(-3.3, -1.33) * mm, "end": v(-3.3, -1.34) * mm});
            skLineSegment(sketch, "E901", {"start": v(-3.3, -1.34) * mm, "end": v(-3.3, -1.35) * mm});
            skLineSegment(sketch, "E902", {"start": v(-3.3, -1.35) * mm, "end": v(-3.3, -1.36) * mm});
            skLineSegment(sketch, "E903", {"start": v(-3.3, -1.36) * mm, "end": v(-3.31, -1.37) * mm});
            skLineSegment(sketch, "E904", {"start": v(-3.31, -1.37) * mm, "end": v(-3.32, -1.38) * mm});
            skLineSegment(sketch, "E905", {"start": v(-3.32, -1.38) * mm, "end": v(-3.32, -1.4) * mm});
            skLineSegment(sketch, "E906", {"start": v(-3.32, -1.4) * mm, "end": v(-3.33, -1.4) * mm});
            skLineSegment(sketch, "E907", {"start": v(-3.33, -1.4) * mm, "end": v(-3.34, -1.41) * mm});
            skLineSegment(sketch, "E908", {"start": v(-3.34, -1.41) * mm, "end": v(-3.34, -1.42) * mm});
            skLineSegment(sketch, "E909", {"start": v(-3.34, -1.42) * mm, "end": v(-3.35, -1.43) * mm});
            skLineSegment(sketch, "E910", {"start": v(-3.35, -1.43) * mm, "end": v(-3.35, -1.44) * mm});
            skLineSegment(sketch, "E911", {"start": v(-3.35, -1.44) * mm, "end": v(-3.36, -1.45) * mm});
            skLineSegment(sketch, "E912", {"start": v(-3.36, -1.45) * mm, "end": v(-3.37, -1.45) * mm});
            skLineSegment(sketch, "E913", {"start": v(-3.37, -1.45) * mm, "end": v(-3.37, -1.46) * mm});
            skLineSegment(sketch, "E914", {"start": v(-3.37, -1.46) * mm, "end": v(-3.38, -1.47) * mm});
            skLineSegment(sketch, "E915", {"start": v(-3.38, -1.47) * mm, "end": v(-3.39, -1.48) * mm});
            skLineSegment(sketch, "E916", {"start": v(-3.39, -1.48) * mm, "end": v(-3.4, -1.48) * mm});
            skLineSegment(sketch, "E917", {"start": v(-3.4, -1.48) * mm, "end": v(-3.4, -1.49) * mm});
            skLineSegment(sketch, "E918", {"start": v(-3.4, -1.49) * mm, "end": v(-3.41, -1.5) * mm});
            skLineSegment(sketch, "E919", {"start": v(-3.41, -1.5) * mm, "end": v(-3.42, -1.5) * mm});
            skLineSegment(sketch, "E920", {"start": v(-3.42, -1.5) * mm, "end": v(-3.43, -1.5) * mm});
            skLineSegment(sketch, "E921", {"start": v(-3.43, -1.5) * mm, "end": v(-3.43, -1.5) * mm});
            skLineSegment(sketch, "E922", {"start": v(-3.43, -1.5) * mm, "end": v(-3.44, -1.51) * mm});
            skLineSegment(sketch, "E923", {"start": v(-3.44, -1.51) * mm, "end": v(-3.45, -1.52) * mm});
            skLineSegment(sketch, "E924", {"start": v(-3.45, -1.52) * mm, "end": v(-3.46, -1.52) * mm});
            skLineSegment(sketch, "E925", {"start": v(-3.46, -1.52) * mm, "end": v(-3.47, -1.52) * mm});
            skLineSegment(sketch, "E926", {"start": v(-3.47, -1.52) * mm, "end": v(-3.48, -1.52) * mm});
            skLineSegment(sketch, "E927", {"start": v(-3.48, -1.52) * mm, "end": v(-3.49, -1.53) * mm});
            skLineSegment(sketch, "E928", {"start": v(-3.49, -1.53) * mm, "end": v(-3.5, -1.53) * mm});
            skLineSegment(sketch, "E929", {"start": v(-3.5, -1.53) * mm, "end": v(-3.5, -1.53) * mm});
            skLineSegment(sketch, "E930", {"start": v(-3.5, -1.53) * mm, "end": v(-3.51, -1.53) * mm});
            skLineSegment(sketch, "E931", {"start": v(-3.51, -1.53) * mm, "end": v(-3.52, -1.53) * mm});
            skLineSegment(sketch, "E932", {"start": v(-3.52, -1.53) * mm, "end": v(-3.53, -1.53) * mm});
            skLineSegment(sketch, "E933", {"start": v(-3.53, -1.53) * mm, "end": v(-3.56, -1.53) * mm});
            skLineSegment(sketch, "E934", {"start": v(-3.56, -1.53) * mm, "end": v(-3.58, -1.53) * mm});
            skLineSegment(sketch, "E935", {"start": v(-3.58, -1.53) * mm, "end": v(-3.6, -1.53) * mm});
            skLineSegment(sketch, "E936", {"start": v(-3.6, -1.53) * mm, "end": v(-3.63, -1.53) * mm});
            skLineSegment(sketch, "E937", {"start": v(-3.63, -1.53) * mm, "end": v(-3.65, -1.53) * mm});
            skLineSegment(sketch, "E938", {"start": v(-3.65, -1.53) * mm, "end": v(-3.68, -1.53) * mm});
            skLineSegment(sketch, "E939", {"start": v(-3.68, -1.53) * mm, "end": v(-3.7, -1.53) * mm});
            skLineSegment(sketch, "E940", {"start": v(-3.7, -1.53) * mm, "end": v(-3.73, -1.52) * mm});
            skLineSegment(sketch, "E941", {"start": v(-3.73, -1.52) * mm, "end": v(-3.75, -1.52) * mm});
            skLineSegment(sketch, "E942", {"start": v(-3.75, -1.52) * mm, "end": v(-3.77, -1.5) * mm});
            skLineSegment(sketch, "E943", {"start": v(-3.77, -1.5) * mm, "end": v(-3.8, -1.5) * mm});
            skLineSegment(sketch, "E944", {"start": v(-3.8, -1.5) * mm, "end": v(-3.82, -1.5) * mm});
            skLineSegment(sketch, "E945", {"start": v(-3.82, -1.5) * mm, "end": v(-3.84, -1.49) * mm});
            skLineSegment(sketch, "E946", {"start": v(-3.84, -1.49) * mm, "end": v(-3.87, -1.48) * mm});
            skLineSegment(sketch, "E947", {"start": v(-3.87, -1.48) * mm, "end": v(-3.9, -1.46) * mm});
            skLineSegment(sketch, "E948", {"start": v(-3.9, -1.46) * mm, "end": v(-3.91, -1.45) * mm});
            skLineSegment(sketch, "E949", {"start": v(-3.91, -1.45) * mm, "end": v(-3.94, -1.44) * mm});
            skLineSegment(sketch, "E950", {"start": v(-3.94, -1.44) * mm, "end": v(-3.96, -1.43) * mm});
            skLineSegment(sketch, "E951", {"start": v(-3.96, -1.43) * mm, "end": v(-3.98, -1.41) * mm});
            skLineSegment(sketch, "E952", {"start": v(-3.98, -1.41) * mm, "end": v(-4, -1.4) * mm});
            skLineSegment(sketch, "E953", {"start": v(-4, -1.4) * mm, "end": v(-4.03, -1.38) * mm});
            skLineSegment(sketch, "E954", {"start": v(-4.03, -1.38) * mm, "end": v(-4.05, -1.36) * mm});
            skLineSegment(sketch, "E955", {"start": v(-4.05, -1.36) * mm, "end": v(-4.07, -1.35) * mm});
            skLineSegment(sketch, "E956", {"start": v(-4.07, -1.35) * mm, "end": v(-4.1, -1.33) * mm});
            skLineSegment(sketch, "E957", {"start": v(-4.1, -1.33) * mm, "end": v(-4.12, -1.3) * mm});
            skLineSegment(sketch, "E958", {"start": v(-4.12, -1.3) * mm, "end": v(-4.14, -1.29) * mm});
            skLineSegment(sketch, "E959", {"start": v(-4.14, -1.29) * mm, "end": v(-4.16, -1.26) * mm});
            skLineSegment(sketch, "E960", {"start": v(-4.16, -1.26) * mm, "end": v(-4.19, -1.24) * mm});
            skLineSegment(sketch, "E961", {"start": v(-4.19, -1.24) * mm, "end": v(-4.2, -1.22) * mm});
            skLineSegment(sketch, "E962", {"start": v(-4.2, -1.22) * mm, "end": v(-4.23, -1.2) * mm});
            skLineSegment(sketch, "E963", {"start": v(-4.23, -1.2) * mm, "end": v(-4.25, -1.17) * mm});
            skLineSegment(sketch, "E964", {"start": v(-4.25, -1.17) * mm, "end": v(-4.27, -1.14) * mm});
            skLineSegment(sketch, "E965", {"start": v(-4.27, -1.14) * mm, "end": v(-4.3, -1.11) * mm});
            skLineSegment(sketch, "E966", {"start": v(-4.3, -1.11) * mm, "end": v(-4.3, -1.09) * mm});
            skLineSegment(sketch, "E967", {"start": v(-4.3, -1.09) * mm, "end": v(-4.33, -1.06) * mm});
            skLineSegment(sketch, "E968", {"start": v(-4.33, -1.06) * mm, "end": v(-4.34, -1.04) * mm});
            skLineSegment(sketch, "E969", {"start": v(-4.34, -1.04) * mm, "end": v(-4.36, -1.01) * mm});
            skLineSegment(sketch, "E970", {"start": v(-4.36, -1.01) * mm, "end": v(-4.37, -1) * mm});
            skLineSegment(sketch, "E971", {"start": v(-4.37, -1) * mm, "end": v(-4.39, -0.97) * mm});
            skLineSegment(sketch, "E972", {"start": v(-4.39, -0.97) * mm, "end": v(-4.4, -0.95) * mm});
            skLineSegment(sketch, "E973", {"start": v(-4.4, -0.95) * mm, "end": v(-4.42, -0.92) * mm});
            skLineSegment(sketch, "E974", {"start": v(-4.42, -0.92) * mm, "end": v(-4.43, -0.9) * mm});
            skLineSegment(sketch, "E975", {"start": v(-4.43, -0.9) * mm, "end": v(-4.45, -0.88) * mm});
            skLineSegment(sketch, "E976", {"start": v(-4.45, -0.88) * mm, "end": v(-4.46, -0.86) * mm});
            skLineSegment(sketch, "E977", {"start": v(-4.46, -0.86) * mm, "end": v(-4.48, -0.84) * mm});
            skLineSegment(sketch, "E978", {"start": v(-4.48, -0.84) * mm, "end": v(-4.5, -0.82) * mm});
            skLineSegment(sketch, "E979", {"start": v(-4.5, -0.82) * mm, "end": v(-4.5, -0.8) * mm});
            skLineSegment(sketch, "E980", {"start": v(-4.5, -0.8) * mm, "end": v(-4.52, -0.79) * mm});
            skLineSegment(sketch, "E981", {"start": v(-4.52, -0.79) * mm, "end": v(-4.53, -0.77) * mm});
            skLineSegment(sketch, "E982", {"start": v(-4.53, -0.77) * mm, "end": v(-4.55, -0.76) * mm});
            skLineSegment(sketch, "E983", {"start": v(-4.55, -0.76) * mm, "end": v(-4.56, -0.74) * mm});
            skLineSegment(sketch, "E984", {"start": v(-4.56, -0.74) * mm, "end": v(-4.57, -0.73) * mm});
            skLineSegment(sketch, "E985", {"start": v(-4.57, -0.73) * mm, "end": v(-4.58, -0.71) * mm});
            skLineSegment(sketch, "E986", {"start": v(-4.58, -0.71) * mm, "end": v(-4.6, -0.7) * mm});
            skLineSegment(sketch, "E987", {"start": v(-4.6, -0.7) * mm, "end": v(-4.6, -0.68) * mm});
            skLineSegment(sketch, "E988", {"start": v(-4.6, -0.68) * mm, "end": v(-4.62, -0.67) * mm});
            skLineSegment(sketch, "E989", {"start": v(-4.62, -0.67) * mm, "end": v(-4.63, -0.66) * mm});
            skLineSegment(sketch, "E990", {"start": v(-4.63, -0.66) * mm, "end": v(-4.64, -0.65) * mm});
            skLineSegment(sketch, "E991", {"start": v(-4.64, -0.65) * mm, "end": v(-4.65, -0.64) * mm});
            skLineSegment(sketch, "E992", {"start": v(-4.65, -0.64) * mm, "end": v(-4.66, -0.63) * mm});
            skLineSegment(sketch, "E993", {"start": v(-4.66, -0.63) * mm, "end": v(-4.67, -0.62) * mm});
            skLineSegment(sketch, "E994", {"start": v(-4.67, -0.62) * mm, "end": v(-4.68, -0.6) * mm});
            skLineSegment(sketch, "E995", {"start": v(-4.68, -0.6) * mm, "end": v(-4.7, -0.6) * mm});
            skLineSegment(sketch, "E996", {"start": v(-4.7, -0.6) * mm, "end": v(-4.7, -0.6) * mm});
            skLineSegment(sketch, "E997", {"start": v(-4.7, -0.6) * mm, "end": v(-4.7, -0.63) * mm});
            skLineSegment(sketch, "E998", {"start": v(-4.7, -0.63) * mm, "end": v(-4.7, -0.67) * mm});
            skLineSegment(sketch, "E999", {"start": v(-4.7, -0.67) * mm, "end": v(-4.7, -0.7) * mm});
            skLineSegment(sketch, "E1000", {"start": v(-4.7, -0.7) * mm, "end": v(-4.7, -0.74) * mm});
            skLineSegment(sketch, "E1001", {"start": v(-4.7, -0.74) * mm, "end": v(-4.7, -0.77) * mm});
            skLineSegment(sketch, "E1002", {"start": v(-4.7, -0.77) * mm, "end": v(-4.7, -0.81) * mm});
            skLineSegment(sketch, "E1003", {"start": v(-4.7, -0.81) * mm, "end": v(-4.7, -0.85) * mm});
            skLineSegment(sketch, "E1004", {"start": v(-4.7, -0.85) * mm, "end": v(-4.7, -0.88) * mm});
            skLineSegment(sketch, "E1005", {"start": v(-4.7, -0.88) * mm, "end": v(-4.7, -0.92) * mm});
            skLineSegment(sketch, "E1006", {"start": v(-4.7, -0.92) * mm, "end": v(-4.7, -0.95) * mm});
            skLineSegment(sketch, "E1007", {"start": v(-4.7, -0.95) * mm, "end": v(-4.7, -0.99) * mm});
            skLineSegment(sketch, "E1008", {"start": v(-4.7, -0.99) * mm, "end": v(-4.7, -1.02) * mm});
            skLineSegment(sketch, "E1009", {"start": v(-4.7, -1.02) * mm, "end": v(-4.7, -1.06) * mm});
            skLineSegment(sketch, "E1010", {"start": v(-4.7, -1.06) * mm, "end": v(-4.7, -1.1) * mm});
            skLineSegment(sketch, "E1011", {"start": v(-4.7, -1.1) * mm, "end": v(-4.7, -1.13) * mm});
            skLineSegment(sketch, "E1012", {"start": v(-4.7, -1.13) * mm, "end": v(-4.7, -1.16) * mm});
            skLineSegment(sketch, "E1013", {"start": v(-4.7, -1.16) * mm, "end": v(-4.7, -1.2) * mm});
            skLineSegment(sketch, "E1014", {"start": v(-4.7, -1.2) * mm, "end": v(-4.7, -1.23) * mm});
            skLineSegment(sketch, "E1015", {"start": v(-4.7, -1.23) * mm, "end": v(-4.7, -1.26) * mm});
            skLineSegment(sketch, "E1016", {"start": v(-4.7, -1.26) * mm, "end": v(-4.69, -1.3) * mm});
            skLineSegment(sketch, "E1017", {"start": v(-4.69, -1.3) * mm, "end": v(-4.69, -1.33) * mm});
            skLineSegment(sketch, "E1018", {"start": v(-4.69, -1.33) * mm, "end": v(-4.69, -1.36) * mm});
            skLineSegment(sketch, "E1019", {"start": v(-4.69, -1.36) * mm, "end": v(-4.68, -1.4) * mm});
            skLineSegment(sketch, "E1020", {"start": v(-4.68, -1.4) * mm, "end": v(-4.68, -1.43) * mm});
            skLineSegment(sketch, "E1021", {"start": v(-4.68, -1.43) * mm, "end": v(-4.68, -1.46) * mm});
            skLineSegment(sketch, "E1022", {"start": v(-4.68, -1.46) * mm, "end": v(-4.68, -1.5) * mm});
            skLineSegment(sketch, "E1023", {"start": v(-4.68, -1.5) * mm, "end": v(-4.68, -1.53) * mm});
            skLineSegment(sketch, "E1024", {"start": v(-4.68, -1.53) * mm, "end": v(-4.67, -1.56) * mm});
            skLineSegment(sketch, "E1025", {"start": v(-4.67, -1.56) * mm, "end": v(-4.67, -1.6) * mm});
            skLineSegment(sketch, "E1026", {"start": v(-4.67, -1.6) * mm, "end": v(-4.67, -1.62) * mm});
            skLineSegment(sketch, "E1027", {"start": v(-4.67, -1.62) * mm, "end": v(-4.67, -1.66) * mm});
            skLineSegment(sketch, "E1028", {"start": v(-4.67, -1.66) * mm, "end": v(-4.67, -1.69) * mm});
            skLineSegment(sketch, "E1029", {"start": v(-4.67, -1.69) * mm, "end": v(-4.67, -2.31) * mm});
            skLineSegment(sketch, "E1030", {"start": v(-4.67, -2.31) * mm, "end": v(-4.67, -2.33) * mm});
            skLineSegment(sketch, "E1031", {"start": v(-4.67, -2.33) * mm, "end": v(-4.67, -2.35) * mm});
            skLineSegment(sketch, "E1032", {"start": v(-4.67, -2.35) * mm, "end": v(-4.67, -2.36) * mm});
            skLineSegment(sketch, "E1033", {"start": v(-4.67, -2.36) * mm, "end": v(-4.67, -2.38) * mm});
            skLineSegment(sketch, "E1034", {"start": v(-4.67, -2.38) * mm, "end": v(-4.68, -2.4) * mm});
            skLineSegment(sketch, "E1035", {"start": v(-4.68, -2.4) * mm, "end": v(-4.68, -2.42) * mm});
            skLineSegment(sketch, "E1036", {"start": v(-4.68, -2.42) * mm, "end": v(-4.68, -2.43) * mm});
            skLineSegment(sketch, "E1037", {"start": v(-4.68, -2.43) * mm, "end": v(-4.68, -2.45) * mm});
            skLineSegment(sketch, "E1038", {"start": v(-4.68, -2.45) * mm, "end": v(-4.68, -2.47) * mm});
            skLineSegment(sketch, "E1039", {"start": v(-4.68, -2.47) * mm, "end": v(-4.69, -2.49) * mm});
            skLineSegment(sketch, "E1040", {"start": v(-4.69, -2.49) * mm, "end": v(-4.69, -2.5) * mm});
            skLineSegment(sketch, "E1041", {"start": v(-4.69, -2.5) * mm, "end": v(-4.69, -2.52) * mm});
            skLineSegment(sketch, "E1042", {"start": v(-4.69, -2.52) * mm, "end": v(-4.7, -2.54) * mm});
            skLineSegment(sketch, "E1043", {"start": v(-4.7, -2.54) * mm, "end": v(-4.7, -2.56) * mm});
            skLineSegment(sketch, "E1044", {"start": v(-4.7, -2.56) * mm, "end": v(-4.7, -2.58) * mm});
            skLineSegment(sketch, "E1045", {"start": v(-4.7, -2.58) * mm, "end": v(-4.7, -2.6) * mm});
            skLineSegment(sketch, "E1046", {"start": v(-4.7, -2.6) * mm, "end": v(-4.7, -2.61) * mm});
            skLineSegment(sketch, "E1047", {"start": v(-4.7, -2.61) * mm, "end": v(-4.7, -2.63) * mm});
            skLineSegment(sketch, "E1048", {"start": v(-4.7, -2.63) * mm, "end": v(-4.7, -2.65) * mm});
            skLineSegment(sketch, "E1049", {"start": v(-4.7, -2.65) * mm, "end": v(-4.7, -2.67) * mm});
            skLineSegment(sketch, "E1050", {"start": v(-4.7, -2.67) * mm, "end": v(-4.7, -2.69) * mm});
            skLineSegment(sketch, "E1051", {"start": v(-4.7, -2.69) * mm, "end": v(-4.7, -2.7) * mm});
            skLineSegment(sketch, "E1052", {"start": v(-4.7, -2.7) * mm, "end": v(-4.7, -2.73) * mm});
            skLineSegment(sketch, "E1053", {"start": v(-4.7, -2.73) * mm, "end": v(-4.7, -2.74) * mm});
            skLineSegment(sketch, "E1054", {"start": v(-4.7, -2.74) * mm, "end": v(-4.7, -2.76) * mm});
            skLineSegment(sketch, "E1055", {"start": v(-4.7, -2.76) * mm, "end": v(-4.7, -2.78) * mm});
            skLineSegment(sketch, "E1056", {"start": v(-4.7, -2.78) * mm, "end": v(-4.7, -2.8) * mm});
            skLineSegment(sketch, "E1057", {"start": v(-4.7, -2.8) * mm, "end": v(-4.7, -2.82) * mm});
            skLineSegment(sketch, "E1058", {"start": v(-4.7, -2.82) * mm, "end": v(-4.7, -2.84) * mm});
            skLineSegment(sketch, "E1059", {"start": v(-4.7, -2.84) * mm, "end": v(-4.7, -2.86) * mm});
            skLineSegment(sketch, "E1060", {"start": v(-4.7, -2.86) * mm, "end": v(-4.7, -2.88) * mm});
            skLineSegment(sketch, "E1061", {"start": v(-4.7, -2.88) * mm, "end": v(-4.7, -2.9) * mm});
            skLineSegment(sketch, "E1062", {"start": v(-4.7, -2.9) * mm, "end": v(-4.7, -2.93) * mm});
            skLineSegment(sketch, "E1063", {"start": v(-4.7, -2.93) * mm, "end": v(-4.7, -2.97) * mm});
            skLineSegment(sketch, "E1064", {"start": v(-4.7, -2.97) * mm, "end": v(-4.71, -3) * mm});
            skLineSegment(sketch, "E1065", {"start": v(-4.71, -3) * mm, "end": v(-4.71, -3.04) * mm});
            skLineSegment(sketch, "E1066", {"start": v(-4.71, -3.04) * mm, "end": v(-4.72, -3.07) * mm});
            skLineSegment(sketch, "E1067", {"start": v(-4.72, -3.07) * mm, "end": v(-4.72, -3.1) * mm});
            skLineSegment(sketch, "E1068", {"start": v(-4.72, -3.1) * mm, "end": v(-4.72, -3.13) * mm});
            skLineSegment(sketch, "E1069", {"start": v(-4.72, -3.13) * mm, "end": v(-4.72, -3.16) * mm});
            skLineSegment(sketch, "E1070", {"start": v(-4.72, -3.16) * mm, "end": v(-4.73, -3.18) * mm});
            skLineSegment(sketch, "E1071", {"start": v(-4.73, -3.18) * mm, "end": v(-4.73, -3.21) * mm});
            skLineSegment(sketch, "E1072", {"start": v(-4.73, -3.21) * mm, "end": v(-4.73, -3.24) * mm});
            skLineSegment(sketch, "E1073", {"start": v(-4.73, -3.24) * mm, "end": v(-4.73, -3.26) * mm});
            skLineSegment(sketch, "E1074", {"start": v(-4.73, -3.26) * mm, "end": v(-4.74, -3.28) * mm});
            skLineSegment(sketch, "E1075", {"start": v(-4.74, -3.28) * mm, "end": v(-4.74, -3.3) * mm});
            skLineSegment(sketch, "E1076", {"start": v(-4.74, -3.3) * mm, "end": v(-4.74, -3.33) * mm});
            skLineSegment(sketch, "E1077", {"start": v(-4.74, -3.33) * mm, "end": v(-4.74, -3.35) * mm});
            skLineSegment(sketch, "E1078", {"start": v(-4.74, -3.35) * mm, "end": v(-4.75, -3.37) * mm});
            skLineSegment(sketch, "E1079", {"start": v(-4.75, -3.37) * mm, "end": v(-4.75, -3.38) * mm});
            skLineSegment(sketch, "E1080", {"start": v(-4.75, -3.38) * mm, "end": v(-4.75, -3.4) * mm});
            skLineSegment(sketch, "E1081", {"start": v(-4.75, -3.4) * mm, "end": v(-4.75, -3.42) * mm});
            skLineSegment(sketch, "E1082", {"start": v(-4.75, -3.42) * mm, "end": v(-4.76, -3.43) * mm});
            skLineSegment(sketch, "E1083", {"start": v(-4.76, -3.43) * mm, "end": v(-4.76, -3.45) * mm});
            skLineSegment(sketch, "E1084", {"start": v(-4.76, -3.45) * mm, "end": v(-4.76, -3.46) * mm});
            skLineSegment(sketch, "E1085", {"start": v(-4.76, -3.46) * mm, "end": v(-4.76, -3.47) * mm});
            skLineSegment(sketch, "E1086", {"start": v(-4.76, -3.47) * mm, "end": v(-4.77, -3.48) * mm});
            skLineSegment(sketch, "E1087", {"start": v(-4.77, -3.48) * mm, "end": v(-4.77, -3.49) * mm});
            skLineSegment(sketch, "E1088", {"start": v(-4.77, -3.49) * mm, "end": v(-4.77, -3.5) * mm});
            skLineSegment(sketch, "E1089", {"start": v(-4.77, -3.5) * mm, "end": v(-4.77, -3.5) * mm});
            skLineSegment(sketch, "E1090", {"start": v(-4.77, -3.5) * mm, "end": v(-4.78, -3.51) * mm});
            skLineSegment(sketch, "E1091", {"start": v(-4.78, -3.51) * mm, "end": v(-4.78, -3.52) * mm});
            skLineSegment(sketch, "E1092", {"start": v(-4.78, -3.52) * mm, "end": v(-4.78, -3.52) * mm});
            skLineSegment(sketch, "E1093", {"start": v(-4.78, -3.52) * mm, "end": v(-4.8, -3.53) * mm});
            skLineSegment(sketch, "E1094", {"start": v(-4.8, -3.53) * mm, "end": v(-4.8, -3.54) * mm});
            skLineSegment(sketch, "E1095", {"start": v(-4.8, -3.54) * mm, "end": v(-4.82, -3.55) * mm});
            skLineSegment(sketch, "E1096", {"start": v(-4.82, -3.55) * mm, "end": v(-4.83, -3.56) * mm});
            skLineSegment(sketch, "E1097", {"start": v(-4.83, -3.56) * mm, "end": v(-4.84, -3.56) * mm});
            skLineSegment(sketch, "E1098", {"start": v(-4.84, -3.56) * mm, "end": v(-4.86, -3.57) * mm});
            skLineSegment(sketch, "E1099", {"start": v(-4.86, -3.57) * mm, "end": v(-4.87, -3.57) * mm});
            skLineSegment(sketch, "E1100", {"start": v(-4.87, -3.57) * mm, "end": v(-4.88, -3.58) * mm});
            skLineSegment(sketch, "E1101", {"start": v(-4.88, -3.58) * mm, "end": v(-4.9, -3.58) * mm});
            skLineSegment(sketch, "E1102", {"start": v(-4.9, -3.58) * mm, "end": v(-4.9, -3.58) * mm});
            skLineSegment(sketch, "E1103", {"start": v(-4.9, -3.58) * mm, "end": v(-4.92, -3.58) * mm});
            skLineSegment(sketch, "E1104", {"start": v(-4.92, -3.58) * mm, "end": v(-4.93, -3.59) * mm});
            skLineSegment(sketch, "E1105", {"start": v(-4.93, -3.59) * mm, "end": v(-4.95, -3.59) * mm});
            skLineSegment(sketch, "E1106", {"start": v(-4.95, -3.59) * mm, "end": v(-4.96, -3.59) * mm});
            skLineSegment(sketch, "E1107", {"start": v(-4.96, -3.59) * mm, "end": v(-4.97, -3.58) * mm});
            skLineSegment(sketch, "E1108", {"start": v(-4.97, -3.58) * mm, "end": v(-4.99, -3.58) * mm});
            skLineSegment(sketch, "E1109", {"start": v(-4.99, -3.58) * mm, "end": v(-5, -3.58) * mm});
            skLineSegment(sketch, "E1110", {"start": v(-5, -3.58) * mm, "end": v(-5.01, -3.58) * mm});
            skLineSegment(sketch, "E1111", {"start": v(-5.01, -3.58) * mm, "end": v(-5.03, -3.57) * mm});
            skLineSegment(sketch, "E1112", {"start": v(-5.03, -3.57) * mm, "end": v(-5.04, -3.57) * mm});
            skLineSegment(sketch, "E1113", {"start": v(-5.04, -3.57) * mm, "end": v(-5.06, -3.56) * mm});
            skLineSegment(sketch, "E1114", {"start": v(-5.06, -3.56) * mm, "end": v(-5.07, -3.55) * mm});
            skLineSegment(sketch, "E1115", {"start": v(-5.07, -3.55) * mm, "end": v(-5.08, -3.55) * mm});
            skLineSegment(sketch, "E1116", {"start": v(-5.08, -3.55) * mm, "end": v(-5.1, -3.54) * mm});
            skLineSegment(sketch, "E1117", {"start": v(-5.1, -3.54) * mm, "end": v(-5.11, -3.53) * mm});
            skLineSegment(sketch, "E1118", {"start": v(-5.11, -3.53) * mm, "end": v(-5.13, -3.52) * mm});
            skLineSegment(sketch, "E1119", {"start": v(-5.13, -3.52) * mm, "end": v(-5.14, -3.5) * mm});
            skLineSegment(sketch, "E1120", {"start": v(-5.14, -3.5) * mm, "end": v(-5.15, -3.5) * mm});
            skLineSegment(sketch, "E1121", {"start": v(-5.15, -3.5) * mm, "end": v(-5.17, -3.49) * mm});
            skLineSegment(sketch, "E1122", {"start": v(-5.17, -3.49) * mm, "end": v(-5.18, -3.47) * mm});
            skLineSegment(sketch, "E1123", {"start": v(-5.18, -3.47) * mm, "end": v(-5.2, -3.46) * mm});
            skLineSegment(sketch, "E1124", {"start": v(-5.2, -3.46) * mm, "end": v(-5.21, -3.44) * mm});
            skLineSegment(sketch, "E1125", {"start": v(-5.21, -3.44) * mm, "end": v(-5.23, -3.42) * mm});
            skLineSegment(sketch, "E1126", {"start": v(-5.23, -3.42) * mm, "end": v(-5.25, -3.4) * mm});
            skLineSegment(sketch, "E1127", {"start": v(-5.25, -3.4) * mm, "end": v(-5.27, -3.38) * mm});
            skLineSegment(sketch, "E1128", {"start": v(-5.27, -3.38) * mm, "end": v(-5.29, -3.36) * mm});
            skLineSegment(sketch, "E1129", {"start": v(-5.29, -3.36) * mm, "end": v(-5.3, -3.33) * mm});
            skLineSegment(sketch, "E1130", {"start": v(-5.3, -3.33) * mm, "end": v(-5.32, -3.31) * mm});
            skLineSegment(sketch, "E1131", {"start": v(-5.32, -3.31) * mm, "end": v(-5.34, -3.29) * mm});
            skLineSegment(sketch, "E1132", {"start": v(-5.34, -3.29) * mm, "end": v(-5.35, -3.27) * mm});
            skLineSegment(sketch, "E1133", {"start": v(-5.35, -3.27) * mm, "end": v(-5.37, -3.24) * mm});
            skLineSegment(sketch, "E1134", {"start": v(-5.37, -3.24) * mm, "end": v(-5.38, -3.22) * mm});
            skLineSegment(sketch, "E1135", {"start": v(-5.38, -3.22) * mm, "end": v(-5.4, -3.2) * mm});
            skLineSegment(sketch, "E1136", {"start": v(-5.4, -3.2) * mm, "end": v(-5.4, -3.18) * mm});
            skLineSegment(sketch, "E1137", {"start": v(-5.4, -3.18) * mm, "end": v(-5.42, -3.15) * mm});
            skLineSegment(sketch, "E1138", {"start": v(-5.42, -3.15) * mm, "end": v(-5.43, -3.13) * mm});
            skLineSegment(sketch, "E1139", {"start": v(-5.43, -3.13) * mm, "end": v(-5.45, -3.1) * mm});
            skLineSegment(sketch, "E1140", {"start": v(-5.45, -3.1) * mm, "end": v(-5.46, -3.08) * mm});
            skLineSegment(sketch, "E1141", {"start": v(-5.46, -3.08) * mm, "end": v(-5.47, -3.06) * mm});
            skLineSegment(sketch, "E1142", {"start": v(-5.47, -3.06) * mm, "end": v(-5.48, -3.04) * mm});
            skLineSegment(sketch, "E1143", {"start": v(-5.48, -3.04) * mm, "end": v(-5.49, -3.01) * mm});
            skLineSegment(sketch, "E1144", {"start": v(-5.49, -3.01) * mm, "end": v(-5.5, -3) * mm});
            skLineSegment(sketch, "E1145", {"start": v(-5.5, -3) * mm, "end": v(-5.5, -2.97) * mm});
            skLineSegment(sketch, "E1146", {"start": v(-5.5, -2.97) * mm, "end": v(-5.51, -2.94) * mm});
            skLineSegment(sketch, "E1147", {"start": v(-5.51, -2.94) * mm, "end": v(-5.52, -2.92) * mm});
            skLineSegment(sketch, "E1148", {"start": v(-5.52, -2.92) * mm, "end": v(-5.53, -2.9) * mm});
            skLineSegment(sketch, "E1149", {"start": v(-5.53, -2.9) * mm, "end": v(-5.53, -2.87) * mm});
            skLineSegment(sketch, "E1150", {"start": v(-5.53, -2.87) * mm, "end": v(-5.54, -2.85) * mm});
            skLineSegment(sketch, "E1151", {"start": v(-5.54, -2.85) * mm, "end": v(-5.55, -2.82) * mm});
            skLineSegment(sketch, "E1152", {"start": v(-5.55, -2.82) * mm, "end": v(-5.55, -2.8) * mm});
            skLineSegment(sketch, "E1153", {"start": v(-5.55, -2.8) * mm, "end": v(-5.55, -2.78) * mm});
            skLineSegment(sketch, "E1154", {"start": v(-5.55, -2.78) * mm, "end": v(-5.56, -2.75) * mm});
            skLineSegment(sketch, "E1155", {"start": v(-5.56, -2.75) * mm, "end": v(-5.56, -2.73) * mm});
            skLineSegment(sketch, "E1156", {"start": v(-5.56, -2.73) * mm, "end": v(-5.56, -2.7) * mm});
            skLineSegment(sketch, "E1157", {"start": v(-5.56, -2.7) * mm, "end": v(-5.52, -2.66) * mm});
            skLineSegment(sketch, "E1158", {"start": v(-5.52, -2.66) * mm, "end": v(-5.52, -2.64) * mm});
            skLineSegment(sketch, "E1159", {"start": v(-5.52, -2.64) * mm, "end": v(-5.51, -2.6) * mm});
            skLineSegment(sketch, "E1160", {"start": v(-5.51, -2.6) * mm, "end": v(-5.5, -2.58) * mm});
            skLineSegment(sketch, "E1161", {"start": v(-5.5, -2.58) * mm, "end": v(-5.5, -2.55) * mm});
            skLineSegment(sketch, "E1162", {"start": v(-5.5, -2.55) * mm, "end": v(-5.49, -2.52) * mm});
            skLineSegment(sketch, "E1163", {"start": v(-5.49, -2.52) * mm, "end": v(-5.48, -2.5) * mm});
            skLineSegment(sketch, "E1164", {"start": v(-5.48, -2.5) * mm, "end": v(-5.48, -2.47) * mm});
            skLineSegment(sketch, "E1165", {"start": v(-5.48, -2.47) * mm, "end": v(-5.47, -2.44) * mm});
            skLineSegment(sketch, "E1166", {"start": v(-5.47, -2.44) * mm, "end": v(-5.46, -2.42) * mm});
            skLineSegment(sketch, "E1167", {"start": v(-5.46, -2.42) * mm, "end": v(-5.46, -2.4) * mm});
            skLineSegment(sketch, "E1168", {"start": v(-5.46, -2.4) * mm, "end": v(-5.45, -2.36) * mm});
            skLineSegment(sketch, "E1169", {"start": v(-5.45, -2.36) * mm, "end": v(-5.45, -2.34) * mm});
            skLineSegment(sketch, "E1170", {"start": v(-5.45, -2.34) * mm, "end": v(-5.44, -2.32) * mm});
            skLineSegment(sketch, "E1171", {"start": v(-5.44, -2.32) * mm, "end": v(-5.44, -2.3) * mm});
            skLineSegment(sketch, "E1172", {"start": v(-5.44, -2.3) * mm, "end": v(-5.43, -2.27) * mm});
            skLineSegment(sketch, "E1173", {"start": v(-5.43, -2.27) * mm, "end": v(-5.43, -2.24) * mm});
            skLineSegment(sketch, "E1174", {"start": v(-5.43, -2.24) * mm, "end": v(-5.42, -2.22) * mm});
            skLineSegment(sketch, "E1175", {"start": v(-5.42, -2.22) * mm, "end": v(-5.42, -2.2) * mm});
            skLineSegment(sketch, "E1176", {"start": v(-5.42, -2.2) * mm, "end": v(-5.41, -2.18) * mm});
            skLineSegment(sketch, "E1177", {"start": v(-5.41, -2.18) * mm, "end": v(-5.4, -2.15) * mm});
            skLineSegment(sketch, "E1178", {"start": v(-5.4, -2.15) * mm, "end": v(-5.4, -2.13) * mm});
            skLineSegment(sketch, "E1179", {"start": v(-5.4, -2.13) * mm, "end": v(-5.4, -2.11) * mm});
            skLineSegment(sketch, "E1180", {"start": v(-5.4, -2.11) * mm, "end": v(-5.4, -2.1) * mm});
            skLineSegment(sketch, "E1181", {"start": v(-5.4, -2.1) * mm, "end": v(-5.4, -2.07) * mm});
            skLineSegment(sketch, "E1182", {"start": v(-5.4, -2.07) * mm, "end": v(-5.39, -2.05) * mm});
            skLineSegment(sketch, "E1183", {"start": v(-5.39, -2.05) * mm, "end": v(-5.39, -2.03) * mm});
            skLineSegment(sketch, "E1184", {"start": v(-5.39, -2.03) * mm, "end": v(-5.38, -2.01) * mm});
            skLineSegment(sketch, "E1185", {"start": v(-5.38, -2.01) * mm, "end": v(-5.38, -2) * mm});
            skLineSegment(sketch, "E1186", {"start": v(-5.38, -2) * mm, "end": v(-5.38, -1.97) * mm});
            skLineSegment(sketch, "E1187", {"start": v(-5.38, -1.97) * mm, "end": v(-5.37, -1.96) * mm});
            skLineSegment(sketch, "E1188", {"start": v(-5.37, -1.96) * mm, "end": v(-5.37, -1.94) * mm});
            skLineSegment(sketch, "E1189", {"start": v(-5.37, -1.94) * mm, "end": v(-5.37, -1.92) * mm});
            skLineSegment(sketch, "E1190", {"start": v(-5.37, -1.92) * mm, "end": v(-5.37, -0.13) * mm});
            skLineSegment(sketch, "E1191", {"start": v(-5.37, -0.13) * mm, "end": v(-5.44, -0.16) * mm});
            skLineSegment(sketch, "E1192", {"start": v(-5.44, -0.16) * mm, "end": v(-5.5, -0.2) * mm});
            skLineSegment(sketch, "E1193", {"start": v(-5.5, -0.2) * mm, "end": v(-5.57, -0.23) * mm});
            skLineSegment(sketch, "E1194", {"start": v(-5.57, -0.23) * mm, "end": v(-5.63, -0.26) * mm});
            skLineSegment(sketch, "E1195", {"start": v(-5.63, -0.26) * mm, "end": v(-5.7, -0.3) * mm});
            skLineSegment(sketch, "E1196", {"start": v(-5.7, -0.3) * mm, "end": v(-5.76, -0.32) * mm});
            skLineSegment(sketch, "E1197", {"start": v(-5.76, -0.32) * mm, "end": v(-5.82, -0.35) * mm});
            skLineSegment(sketch, "E1198", {"start": v(-5.82, -0.35) * mm, "end": v(-5.88, -0.38) * mm});
            skLineSegment(sketch, "E1199", {"start": v(-5.88, -0.38) * mm, "end": v(-5.94, -0.4) * mm});
            skLineSegment(sketch, "E1200", {"start": v(-5.94, -0.4) * mm, "end": v(-6, -0.43) * mm});
            skLineSegment(sketch, "E1201", {"start": v(-6, -0.43) * mm, "end": v(-6.05, -0.46) * mm});
            skLineSegment(sketch, "E1202", {"start": v(-6.05, -0.46) * mm, "end": v(-6.1, -0.48) * mm});
            skLineSegment(sketch, "E1203", {"start": v(-6.1, -0.48) * mm, "end": v(-6.16, -0.5) * mm});
            skLineSegment(sketch, "E1204", {"start": v(-6.16, -0.5) * mm, "end": v(-6.21, -0.53) * mm});
            skLineSegment(sketch, "E1205", {"start": v(-6.21, -0.53) * mm, "end": v(-6.27, -0.55) * mm});
            skLineSegment(sketch, "E1206", {"start": v(-6.27, -0.55) * mm, "end": v(-6.32, -0.56) * mm});
            skLineSegment(sketch, "E1207", {"start": v(-6.32, -0.56) * mm, "end": v(-6.37, -0.58) * mm});
            skLineSegment(sketch, "E1208", {"start": v(-6.37, -0.58) * mm, "end": v(-6.41, -0.6) * mm});
            skLineSegment(sketch, "E1209", {"start": v(-6.41, -0.6) * mm, "end": v(-6.46, -0.61) * mm});
            skLineSegment(sketch, "E1210", {"start": v(-6.46, -0.61) * mm, "end": v(-6.5, -0.63) * mm});
            skLineSegment(sketch, "E1211", {"start": v(-6.5, -0.63) * mm, "end": v(-6.55, -0.64) * mm});
            skLineSegment(sketch, "E1212", {"start": v(-6.55, -0.64) * mm, "end": v(-6.6, -0.65) * mm});
            skLineSegment(sketch, "E1213", {"start": v(-6.6, -0.65) * mm, "end": v(-6.64, -0.66) * mm});
            skLineSegment(sketch, "E1214", {"start": v(-6.64, -0.66) * mm, "end": v(-6.68, -0.67) * mm});
            skLineSegment(sketch, "E1215", {"start": v(-6.68, -0.67) * mm, "end": v(-6.72, -0.68) * mm});
            skLineSegment(sketch, "E1216", {"start": v(-6.72, -0.68) * mm, "end": v(-6.76, -0.7) * mm});
            skLineSegment(sketch, "E1217", {"start": v(-6.76, -0.7) * mm, "end": v(-6.8, -0.7) * mm});
            skLineSegment(sketch, "E1218", {"start": v(-6.8, -0.7) * mm, "end": v(-6.83, -0.7) * mm});
            skLineSegment(sketch, "E1219", {"start": v(-6.83, -0.7) * mm, "end": v(-6.87, -0.7) * mm});
            skLineSegment(sketch, "E1220", {"start": v(-6.87, -0.7) * mm, "end": v(-6.9, -0.7) * mm});
            skLineSegment(sketch, "E1221", {"start": v(-6.9, -0.7) * mm, "end": v(-6.94, -0.71) * mm});
            skLineSegment(sketch, "E1222", {"start": v(-6.94, -0.71) * mm, "end": v(-6.97, -0.71) * mm});
            skLineSegment(sketch, "E1223", {"start": v(-6.97, -0.71) * mm, "end": v(-6.93, -0.68) * mm});
            skLineSegment(sketch, "E1224", {"start": v(-6.93, -0.68) * mm, "end": v(-6.9, -0.64) * mm});
            skLineSegment(sketch, "E1225", {"start": v(-6.9, -0.64) * mm, "end": v(-6.85, -0.6) * mm});
            skLineSegment(sketch, "E1226", {"start": v(-6.85, -0.6) * mm, "end": v(-6.82, -0.58) * mm});
            skLineSegment(sketch, "E1227", {"start": v(-6.82, -0.58) * mm, "end": v(-6.78, -0.54) * mm});
            skLineSegment(sketch, "E1228", {"start": v(-6.78, -0.54) * mm, "end": v(-6.74, -0.5) * mm});
            skLineSegment(sketch, "E1229", {"start": v(-6.74, -0.5) * mm, "end": v(-6.7, -0.48) * mm});
            skLineSegment(sketch, "E1230", {"start": v(-6.7, -0.48) * mm, "end": v(-6.67, -0.44) * mm});
            skLineSegment(sketch, "E1231", {"start": v(-6.67, -0.44) * mm, "end": v(-6.63, -0.4) * mm});
            skLineSegment(sketch, "E1232", {"start": v(-6.63, -0.4) * mm, "end": v(-6.6, -0.38) * mm});
            skLineSegment(sketch, "E1233", {"start": v(-6.6, -0.38) * mm, "end": v(-6.56, -0.34) * mm});
            skLineSegment(sketch, "E1234", {"start": v(-6.56, -0.34) * mm, "end": v(-6.52, -0.31) * mm});
            skLineSegment(sketch, "E1235", {"start": v(-6.52, -0.31) * mm, "end": v(-6.49, -0.28) * mm});
            skLineSegment(sketch, "E1236", {"start": v(-6.49, -0.28) * mm, "end": v(-6.45, -0.25) * mm});
            skLineSegment(sketch, "E1237", {"start": v(-6.45, -0.25) * mm, "end": v(-6.42, -0.22) * mm});
            skLineSegment(sketch, "E1238", {"start": v(-6.42, -0.22) * mm, "end": v(-6.38, -0.18) * mm});
            skLineSegment(sketch, "E1239", {"start": v(-6.38, -0.18) * mm, "end": v(-6.35, -0.15) * mm});
            skLineSegment(sketch, "E1240", {"start": v(-6.35, -0.15) * mm, "end": v(-6.32, -0.12) * mm});
            skLineSegment(sketch, "E1241", {"start": v(-6.32, -0.12) * mm, "end": v(-6.28, -0.09) * mm});
            skLineSegment(sketch, "E1242", {"start": v(-6.28, -0.09) * mm, "end": v(-6.25, -0.06) * mm});
            skLineSegment(sketch, "E1243", {"start": v(-6.25, -0.06) * mm, "end": v(-6.22, -0.03) * mm});
            skLineSegment(sketch, "E1244", {"start": v(-6.22, -0.03) * mm, "end": v(-6.19, 0) * mm});
            skLineSegment(sketch, "E1245", {"start": v(-6.19, 0) * mm, "end": v(-6.15, 0.04) * mm});
            skLineSegment(sketch, "E1246", {"start": v(-6.15, 0.04) * mm, "end": v(-6.12, 0.07) * mm});
            skLineSegment(sketch, "E1247", {"start": v(-6.12, 0.07) * mm, "end": v(-6.09, 0.1) * mm});
            skLineSegment(sketch, "E1248", {"start": v(-6.09, 0.1) * mm, "end": v(-6.06, 0.13) * mm});
            skLineSegment(sketch, "E1249", {"start": v(-6.06, 0.13) * mm, "end": v(-6.03, 0.16) * mm});
            skLineSegment(sketch, "E1250", {"start": v(-6.03, 0.16) * mm, "end": v(-6, 0.19) * mm});
            skLineSegment(sketch, "E1251", {"start": v(-6, 0.19) * mm, "end": v(-5.97, 0.22) * mm});
            skLineSegment(sketch, "E1252", {"start": v(-5.97, 0.22) * mm, "end": v(-5.94, 0.25) * mm});
            skLineSegment(sketch, "E1253", {"start": v(-5.94, 0.25) * mm, "end": v(-5.9, 0.28) * mm});
            skLineSegment(sketch, "E1254", {"start": v(-5.9, 0.28) * mm, "end": v(-5.88, 0.3) * mm});
            skLineSegment(sketch, "E1255", {"start": v(-5.88, 0.3) * mm, "end": v(-5.85, 0.34) * mm});
            skLineSegment(sketch, "E1256", {"start": v(-5.85, 0.34) * mm, "end": v(-5.81, 0.37) * mm});
            skLineSegment(sketch, "E1257", {"start": v(-5.81, 0.37) * mm, "end": v(-5.78, 0.4) * mm});
            skLineSegment(sketch, "E1258", {"start": v(-5.78, 0.4) * mm, "end": v(-5.75, 0.44) * mm});
            skLineSegment(sketch, "E1259", {"start": v(-5.75, 0.44) * mm, "end": v(-5.72, 0.47) * mm});
            skLineSegment(sketch, "E1260", {"start": v(-5.72, 0.47) * mm, "end": v(-5.69, 0.5) * mm});
            skLineSegment(sketch, "E1261", {"start": v(-5.69, 0.5) * mm, "end": v(-5.65, 0.54) * mm});
            skLineSegment(sketch, "E1262", {"start": v(-5.65, 0.54) * mm, "end": v(-5.62, 0.57) * mm});
            skLineSegment(sketch, "E1263", {"start": v(-5.62, 0.57) * mm, "end": v(-5.6, 0.6) * mm});
            skLineSegment(sketch, "E1264", {"start": v(-5.6, 0.6) * mm, "end": v(-5.56, 0.65) * mm});
            skLineSegment(sketch, "E1265", {"start": v(-5.56, 0.65) * mm, "end": v(-5.53, 0.68) * mm});
            skLineSegment(sketch, "E1266", {"start": v(-5.53, 0.68) * mm, "end": v(-5.5, 0.72) * mm});
            skLineSegment(sketch, "E1267", {"start": v(-5.5, 0.72) * mm, "end": v(-5.46, 0.76) * mm});
            skLineSegment(sketch, "E1268", {"start": v(-5.46, 0.76) * mm, "end": v(-5.43, 0.8) * mm});
            skLineSegment(sketch, "E1269", {"start": v(-5.43, 0.8) * mm, "end": v(-5.4, 0.83) * mm});
            skLineSegment(sketch, "E1270", {"start": v(-5.4, 0.83) * mm, "end": v(-5.37, 0.87) * mm});
            skLineSegment(sketch, "E1271", {"start": v(-5.37, 0.87) * mm, "end": v(-5.34, 0.91) * mm});
            skLineSegment(sketch, "E1272", {"start": v(-5.34, 0.91) * mm, "end": v(-5.3, 0.95) * mm});
            skLineSegment(sketch, "E1273", {"start": v(-5.3, 0.95) * mm, "end": v(-5.27, 1) * mm});
            skLineSegment(sketch, "E1274", {"start": v(-5.27, 1) * mm, "end": v(-5.24, 1.03) * mm});
            skLineSegment(sketch, "E1275", {"start": v(-5.24, 1.03) * mm, "end": v(-5.2, 1.07) * mm});
            skLineSegment(sketch, "E1276", {"start": v(-5.2, 1.07) * mm, "end": v(-5.18, 1.11) * mm});
            skLineSegment(sketch, "E1277", {"start": v(-5.18, 1.11) * mm, "end": v(-5.15, 1.16) * mm});
            skLineSegment(sketch, "E1278", {"start": v(-5.15, 1.16) * mm, "end": v(-5.11, 1.2) * mm});
            skLineSegment(sketch, "E1279", {"start": v(-5.11, 1.2) * mm, "end": v(-5.08, 1.24) * mm});
            skLineSegment(sketch, "E1280", {"start": v(-5.08, 1.24) * mm, "end": v(-5.05, 1.28) * mm});
            skLineSegment(sketch, "E1281", {"start": v(-5.05, 1.28) * mm, "end": v(-5.02, 1.33) * mm});
            skLineSegment(sketch, "E1282", {"start": v(-5.02, 1.33) * mm, "end": v(-4.99, 1.37) * mm});
            skLineSegment(sketch, "E1283", {"start": v(-4.99, 1.37) * mm, "end": v(-4.96, 1.42) * mm});
            skLineSegment(sketch, "E1284", {"start": v(-4.96, 1.42) * mm, "end": v(-4.92, 1.46) * mm});
            skLineSegment(sketch, "E1285", {"start": v(-4.92, 1.46) * mm, "end": v(-4.9, 1.5) * mm});
            skLineSegment(sketch, "E1286", {"start": v(-4.9, 1.5) * mm, "end": v(-4.86, 1.55) * mm});
            skLineSegment(sketch, "E1287", {"start": v(-4.86, 1.55) * mm, "end": v(-4.91, 1.55) * mm});
            skLineSegment(sketch, "E1288", {"start": v(-4.91, 1.55) * mm, "end": v(-4.96, 1.54) * mm});
            skLineSegment(sketch, "E1289", {"start": v(-4.96, 1.54) * mm, "end": v(-5.01, 1.53) * mm});
            skLineSegment(sketch, "E1290", {"start": v(-5.01, 1.53) * mm, "end": v(-5.06, 1.53) * mm});
            skLineSegment(sketch, "E1291", {"start": v(-5.06, 1.53) * mm, "end": v(-5.1, 1.52) * mm});
            skLineSegment(sketch, "E1292", {"start": v(-5.1, 1.52) * mm, "end": v(-5.15, 1.51) * mm});
            skLineSegment(sketch, "E1293", {"start": v(-5.15, 1.51) * mm, "end": v(-5.2, 1.5) * mm});
            skLineSegment(sketch, "E1294", {"start": v(-5.2, 1.5) * mm, "end": v(-5.24, 1.5) * mm});
            skLineSegment(sketch, "E1295", {"start": v(-5.24, 1.5) * mm, "end": v(-5.29, 1.5) * mm});
            skLineSegment(sketch, "E1296", {"start": v(-5.29, 1.5) * mm, "end": v(-5.33, 1.5) * mm});
            skLineSegment(sketch, "E1297", {"start": v(-5.33, 1.5) * mm, "end": v(-5.37, 1.49) * mm});
            skLineSegment(sketch, "E1298", {"start": v(-5.37, 1.49) * mm, "end": v(-5.41, 1.48) * mm});
            skLineSegment(sketch, "E1299", {"start": v(-5.41, 1.48) * mm, "end": v(-5.45, 1.48) * mm});
            skLineSegment(sketch, "E1300", {"start": v(-5.45, 1.48) * mm, "end": v(-5.49, 1.47) * mm});
            skLineSegment(sketch, "E1301", {"start": v(-5.49, 1.47) * mm, "end": v(-5.53, 1.47) * mm});
            skLineSegment(sketch, "E1302", {"start": v(-5.53, 1.47) * mm, "end": v(-5.56, 1.47) * mm});
            skLineSegment(sketch, "E1303", {"start": v(-5.56, 1.47) * mm, "end": v(-5.6, 1.46) * mm});
            skLineSegment(sketch, "E1304", {"start": v(-5.6, 1.46) * mm, "end": v(-5.64, 1.46) * mm});
            skLineSegment(sketch, "E1305", {"start": v(-5.64, 1.46) * mm, "end": v(-5.67, 1.46) * mm});
            skLineSegment(sketch, "E1306", {"start": v(-5.67, 1.46) * mm, "end": v(-5.7, 1.45) * mm});
            skLineSegment(sketch, "E1307", {"start": v(-5.7, 1.45) * mm, "end": v(-5.74, 1.45) * mm});
            skLineSegment(sketch, "E1308", {"start": v(-5.74, 1.45) * mm, "end": v(-5.77, 1.45) * mm});
            skLineSegment(sketch, "E1309", {"start": v(-5.77, 1.45) * mm, "end": v(-5.8, 1.45) * mm});
            skLineSegment(sketch, "E1310", {"start": v(-5.8, 1.45) * mm, "end": v(-5.83, 1.45) * mm});
            skLineSegment(sketch, "E1311", {"start": v(-5.83, 1.45) * mm, "end": v(-5.86, 1.44) * mm});
            skLineSegment(sketch, "E1312", {"start": v(-5.86, 1.44) * mm, "end": v(-5.88, 1.44) * mm});
            skLineSegment(sketch, "E1313", {"start": v(-5.88, 1.44) * mm, "end": v(-5.91, 1.44) * mm});
            skLineSegment(sketch, "E1314", {"start": v(-5.91, 1.44) * mm, "end": v(-5.94, 1.44) * mm});
            skLineSegment(sketch, "E1315", {"start": v(-5.94, 1.44) * mm, "end": v(-5.96, 1.44) * mm});
            skLineSegment(sketch, "E1316", {"start": v(-5.96, 1.44) * mm, "end": v(-5.99, 1.44) * mm});
            skLineSegment(sketch, "E1317", {"start": v(-5.99, 1.44) * mm, "end": v(-6.01, 1.44) * mm});
            skLineSegment(sketch, "E1318", {"start": v(-6.01, 1.44) * mm, "end": v(-6.03, 1.44) * mm});
            skLineSegment(sketch, "E1319", {"start": v(-6.03, 1.44) * mm, "end": v(-6.04, 1.44) * mm});
            skLineSegment(sketch, "E1320", {"start": v(-6.04, 1.44) * mm, "end": v(-6.05, 1.44) * mm});
            skLineSegment(sketch, "E1321", {"start": v(-6.05, 1.44) * mm, "end": v(-6.05, 1.44) * mm});
            skLineSegment(sketch, "E1322", {"start": v(-6.05, 1.44) * mm, "end": v(-6.06, 1.45) * mm});
            skLineSegment(sketch, "E1323", {"start": v(-6.06, 1.45) * mm, "end": v(-6.07, 1.45) * mm});
            skLineSegment(sketch, "E1324", {"start": v(-6.07, 1.45) * mm, "end": v(-6.08, 1.45) * mm});
            skLineSegment(sketch, "E1325", {"start": v(-6.08, 1.45) * mm, "end": v(-6.08, 1.45) * mm});
            skLineSegment(sketch, "E1326", {"start": v(-6.08, 1.45) * mm, "end": v(-6.09, 1.45) * mm});
            skLineSegment(sketch, "E1327", {"start": v(-6.09, 1.45) * mm, "end": v(-6.1, 1.46) * mm});
            skLineSegment(sketch, "E1328", {"start": v(-6.1, 1.46) * mm, "end": v(-6.1, 1.46) * mm});
            skLineSegment(sketch, "E1329", {"start": v(-6.1, 1.46) * mm, "end": v(-6.12, 1.46) * mm});
            skLineSegment(sketch, "E1330", {"start": v(-6.12, 1.46) * mm, "end": v(-6.12, 1.46) * mm});
            skLineSegment(sketch, "E1331", {"start": v(-6.12, 1.46) * mm, "end": v(-6.13, 1.46) * mm});
            skLineSegment(sketch, "E1332", {"start": v(-6.13, 1.46) * mm, "end": v(-6.13, 1.47) * mm});
            skLineSegment(sketch, "E1333", {"start": v(-6.13, 1.47) * mm, "end": v(-6.14, 1.47) * mm});
            skLineSegment(sketch, "E1334", {"start": v(-6.14, 1.47) * mm, "end": v(-6.15, 1.47) * mm});
            skLineSegment(sketch, "E1335", {"start": v(-6.15, 1.47) * mm, "end": v(-6.15, 1.47) * mm});
            skLineSegment(sketch, "E1336", {"start": v(-6.15, 1.47) * mm, "end": v(-6.16, 1.47) * mm});
            skLineSegment(sketch, "E1337", {"start": v(-6.16, 1.47) * mm, "end": v(-6.16, 1.47) * mm});
            skLineSegment(sketch, "E1338", {"start": v(-6.16, 1.47) * mm, "end": v(-6.17, 1.47) * mm});
            skLineSegment(sketch, "E1339", {"start": v(-6.17, 1.47) * mm, "end": v(-6.18, 1.47) * mm});
            skLineSegment(sketch, "E1340", {"start": v(-6.18, 1.47) * mm, "end": v(-6.18, 1.47) * mm});
            skLineSegment(sketch, "E1341", {"start": v(-6.18, 1.47) * mm, "end": v(-6.19, 1.47) * mm});
            skLineSegment(sketch, "E1342", {"start": v(-6.19, 1.47) * mm, "end": v(-6.2, 1.47) * mm});
            skLineSegment(sketch, "E1343", {"start": v(-6.2, 1.47) * mm, "end": v(-6.2, 1.48) * mm});
            skLineSegment(sketch, "E1344", {"start": v(-6.2, 1.48) * mm, "end": v(-6.2, 1.48) * mm});
            skLineSegment(sketch, "E1345", {"start": v(-6.2, 1.48) * mm, "end": v(-6.21, 1.48) * mm});
            skLineSegment(sketch, "E1346", {"start": v(-6.21, 1.48) * mm, "end": v(-6.22, 1.48) * mm});
            skLineSegment(sketch, "E1347", {"start": v(-6.22, 1.48) * mm, "end": v(-6.22, 1.48) * mm});
            skLineSegment(sketch, "E1348", {"start": v(-6.22, 1.48) * mm, "end": v(-6.23, 1.48) * mm});
            skLineSegment(sketch, "E1349", {"start": v(-6.23, 1.48) * mm, "end": v(-6.24, 1.48) * mm});
            skLineSegment(sketch, "E1350", {"start": v(-6.24, 1.48) * mm, "end": v(-6.26, 1.48) * mm});
            skLineSegment(sketch, "E1351", {"start": v(-6.26, 1.48) * mm, "end": v(-6.27, 1.49) * mm});
            skLineSegment(sketch, "E1352", {"start": v(-6.27, 1.49) * mm, "end": v(-6.28, 1.5) * mm});
            skLineSegment(sketch, "E1353", {"start": v(-6.28, 1.5) * mm, "end": v(-6.3, 1.5) * mm});
            skLineSegment(sketch, "E1354", {"start": v(-6.3, 1.5) * mm, "end": v(-6.31, 1.5) * mm});
            skLineSegment(sketch, "E1355", {"start": v(-6.31, 1.5) * mm, "end": v(-6.33, 1.51) * mm});
            skLineSegment(sketch, "E1356", {"start": v(-6.33, 1.51) * mm, "end": v(-6.34, 1.52) * mm});
            skLineSegment(sketch, "E1357", {"start": v(-6.34, 1.52) * mm, "end": v(-6.35, 1.53) * mm});
            skLineSegment(sketch, "E1358", {"start": v(-6.35, 1.53) * mm, "end": v(-6.36, 1.54) * mm});
            skLineSegment(sketch, "E1359", {"start": v(-6.36, 1.54) * mm, "end": v(-6.38, 1.55) * mm});
            skLineSegment(sketch, "E1360", {"start": v(-6.38, 1.55) * mm, "end": v(-6.39, 1.56) * mm});
            skLineSegment(sketch, "E1361", {"start": v(-6.39, 1.56) * mm, "end": v(-6.4, 1.57) * mm});
            skLineSegment(sketch, "E1362", {"start": v(-6.4, 1.57) * mm, "end": v(-6.41, 1.58) * mm});
            skLineSegment(sketch, "E1363", {"start": v(-6.41, 1.58) * mm, "end": v(-6.42, 1.6) * mm});
            skLineSegment(sketch, "E1364", {"start": v(-6.42, 1.6) * mm, "end": v(-6.43, 1.6) * mm});
            skLineSegment(sketch, "E1365", {"start": v(-6.43, 1.6) * mm, "end": v(-6.44, 1.62) * mm});
            skLineSegment(sketch, "E1366", {"start": v(-6.44, 1.62) * mm, "end": v(-6.45, 1.63) * mm});
            skLineSegment(sketch, "E1367", {"start": v(-6.45, 1.63) * mm, "end": v(-6.46, 1.65) * mm});
            skLineSegment(sketch, "E1368", {"start": v(-6.46, 1.65) * mm, "end": v(-6.48, 1.66) * mm});
            skLineSegment(sketch, "E1369", {"start": v(-6.48, 1.66) * mm, "end": v(-6.49, 1.68) * mm});
            skLineSegment(sketch, "E1370", {"start": v(-6.49, 1.68) * mm, "end": v(-6.5, 1.7) * mm});
            skLineSegment(sketch, "E1371", {"start": v(-6.5, 1.7) * mm, "end": v(-6.5, 1.71) * mm});
            skLineSegment(sketch, "E1372", {"start": v(-6.5, 1.71) * mm, "end": v(-6.51, 1.73) * mm});
            skLineSegment(sketch, "E1373", {"start": v(-6.51, 1.73) * mm, "end": v(-6.52, 1.75) * mm});
            skLineSegment(sketch, "E1374", {"start": v(-6.52, 1.75) * mm, "end": v(-6.53, 1.77) * mm});
            skLineSegment(sketch, "E1375", {"start": v(-6.53, 1.77) * mm, "end": v(-6.54, 1.8) * mm});
            skLineSegment(sketch, "E1376", {"start": v(-6.54, 1.8) * mm, "end": v(-6.55, 1.81) * mm});
            skLineSegment(sketch, "E1377", {"start": v(-6.55, 1.81) * mm, "end": v(-6.56, 1.84) * mm});
            skLineSegment(sketch, "E1378", {"start": v(-6.56, 1.84) * mm, "end": v(-6.56, 1.86) * mm});
            skLineSegment(sketch, "E1379", {"start": v(-6.56, 1.86) * mm, "end": v(-6.57, 1.88) * mm});
            skLineSegment(sketch, "E1380", {"start": v(-6.57, 1.88) * mm, "end": v(-6.58, 1.9) * mm});
            skLineSegment(sketch, "E1381", {"start": v(-6.58, 1.9) * mm, "end": v(-6.57, 1.9) * mm});
            skLineSegment(sketch, "E1382", {"start": v(-6.57, 1.9) * mm, "end": v(-6.57, 1.9) * mm});
            skLineSegment(sketch, "E1383", {"start": v(-6.57, 1.9) * mm, "end": v(-6.56, 1.9) * mm});
            skLineSegment(sketch, "E1384", {"start": v(-6.56, 1.9) * mm, "end": v(-6.56, 1.9) * mm});
            skLineSegment(sketch, "E1385", {"start": v(-6.56, 1.9) * mm, "end": v(-6.55, 1.9) * mm});
            skLineSegment(sketch, "E1386", {"start": v(-6.55, 1.9) * mm, "end": v(-6.54, 1.9) * mm});
            skLineSegment(sketch, "E1387", {"start": v(-6.54, 1.9) * mm, "end": v(-6.54, 1.89) * mm});
            skLineSegment(sketch, "E1388", {"start": v(-6.54, 1.89) * mm, "end": v(-6.53, 1.89) * mm});
            skLineSegment(sketch, "E1389", {"start": v(-6.53, 1.89) * mm, "end": v(-6.52, 1.88) * mm});
            skLineSegment(sketch, "E1390", {"start": v(-6.52, 1.88) * mm, "end": v(-6.51, 1.88) * mm});
            skLineSegment(sketch, "E1391", {"start": v(-6.51, 1.88) * mm, "end": v(-6.5, 1.88) * mm});
            skLineSegment(sketch, "E1392", {"start": v(-6.5, 1.88) * mm, "end": v(-6.5, 1.88) * mm});
            skLineSegment(sketch, "E1393", {"start": v(-6.5, 1.88) * mm, "end": v(-6.48, 1.87) * mm});
            skLineSegment(sketch, "E1394", {"start": v(-6.48, 1.87) * mm, "end": v(-6.47, 1.87) * mm});
            skLineSegment(sketch, "E1395", {"start": v(-6.47, 1.87) * mm, "end": v(-6.46, 1.87) * mm});
            skLineSegment(sketch, "E1396", {"start": v(-6.46, 1.87) * mm, "end": v(-6.45, 1.87) * mm});
            skLineSegment(sketch, "E1397", {"start": v(-6.45, 1.87) * mm, "end": v(-6.44, 1.86) * mm});
            skLineSegment(sketch, "E1398", {"start": v(-6.44, 1.86) * mm, "end": v(-6.43, 1.86) * mm});
            skLineSegment(sketch, "E1399", {"start": v(-6.43, 1.86) * mm, "end": v(-6.42, 1.86) * mm});
            skLineSegment(sketch, "E1400", {"start": v(-6.42, 1.86) * mm, "end": v(-6.4, 1.86) * mm});
            skLineSegment(sketch, "E1401", {"start": v(-6.4, 1.86) * mm, "end": v(-6.4, 1.86) * mm});
            skLineSegment(sketch, "E1402", {"start": v(-6.4, 1.86) * mm, "end": v(-6.38, 1.85) * mm});
            skLineSegment(sketch, "E1403", {"start": v(-6.38, 1.85) * mm, "end": v(-6.37, 1.85) * mm});
            skLineSegment(sketch, "E1404", {"start": v(-6.37, 1.85) * mm, "end": v(-6.35, 1.85) * mm});
            skLineSegment(sketch, "E1405", {"start": v(-6.35, 1.85) * mm, "end": v(-6.34, 1.85) * mm});
            skLineSegment(sketch, "E1406", {"start": v(-6.34, 1.85) * mm, "end": v(-6.32, 1.84) * mm});
            skLineSegment(sketch, "E1407", {"start": v(-6.32, 1.84) * mm, "end": v(-6.3, 1.84) * mm});
            skLineSegment(sketch, "E1408", {"start": v(-6.3, 1.84) * mm, "end": v(-6.3, 1.84) * mm});
            skLineSegment(sketch, "E1409", {"start": v(-6.3, 1.84) * mm, "end": v(-6.28, 1.84) * mm});
            skLineSegment(sketch, "E1410", {"start": v(-6.28, 1.84) * mm, "end": v(-6.26, 1.83) * mm});
            skLineSegment(sketch, "E1411", {"start": v(-6.26, 1.83) * mm, "end": v(-6.25, 1.83) * mm});
            skLineSegment(sketch, "E1412", {"start": v(-6.25, 1.83) * mm, "end": v(-6.23, 1.83) * mm});
            skLineSegment(sketch, "E1413", {"start": v(-6.23, 1.83) * mm, "end": v(-6.21, 1.83) * mm});
            skLineSegment(sketch, "E1414", {"start": v(-6.21, 1.83) * mm, "end": v(-6.2, 1.83) * mm});
            skLineSegment(sketch, "E1415", {"start": v(-6.2, 1.83) * mm, "end": v(-6.18, 1.83) * mm});
            skLineSegment(sketch, "E1416", {"start": v(-6.18, 1.83) * mm, "end": v(-6.17, 1.83) * mm});
            skLineSegment(sketch, "E1417", {"start": v(-6.17, 1.83) * mm, "end": v(-6.16, 1.83) * mm});
            skLineSegment(sketch, "E1418", {"start": v(-6.16, 1.83) * mm, "end": v(-6.14, 1.83) * mm});
            skLineSegment(sketch, "E1419", {"start": v(-6.14, 1.83) * mm, "end": v(-6.13, 1.83) * mm});
            skLineSegment(sketch, "E1420", {"start": v(-6.13, 1.83) * mm, "end": v(-6.11, 1.83) * mm});
            skLineSegment(sketch, "E1421", {"start": v(-6.11, 1.83) * mm, "end": v(-6.1, 1.83) * mm});
            skLineSegment(sketch, "E1422", {"start": v(-6.1, 1.83) * mm, "end": v(-6.09, 1.83) * mm});
            skLineSegment(sketch, "E1423", {"start": v(-6.09, 1.83) * mm, "end": v(-6.07, 1.83) * mm});
            skLineSegment(sketch, "E1424", {"start": v(-6.07, 1.83) * mm, "end": v(-6.06, 1.83) * mm});
            skLineSegment(sketch, "E1425", {"start": v(-6.06, 1.83) * mm, "end": v(-6.04, 1.83) * mm});
            skLineSegment(sketch, "E1426", {"start": v(-6.04, 1.83) * mm, "end": v(-6.03, 1.84) * mm});
            skLineSegment(sketch, "E1427", {"start": v(-6.03, 1.84) * mm, "end": v(-6.02, 1.84) * mm});
            skLineSegment(sketch, "E1428", {"start": v(-6.02, 1.84) * mm, "end": v(-6, 1.84) * mm});
            skLineSegment(sketch, "E1429", {"start": v(-6, 1.84) * mm, "end": v(-6, 1.84) * mm});
            skLineSegment(sketch, "E1430", {"start": v(-6, 1.84) * mm, "end": v(-5.98, 1.84) * mm});
            skLineSegment(sketch, "E1431", {"start": v(-5.98, 1.84) * mm, "end": v(-5.96, 1.84) * mm});
            skLineSegment(sketch, "E1432", {"start": v(-5.96, 1.84) * mm, "end": v(-5.95, 1.84) * mm});
            skLineSegment(sketch, "E1433", {"start": v(-5.95, 1.84) * mm, "end": v(-5.94, 1.84) * mm});
            skLineSegment(sketch, "E1434", {"start": v(-5.94, 1.84) * mm, "end": v(-5.92, 1.85) * mm});
            skLineSegment(sketch, "E1435", {"start": v(-5.92, 1.85) * mm, "end": v(-5.91, 1.85) * mm});
            skLineSegment(sketch, "E1436", {"start": v(-5.91, 1.85) * mm, "end": v(-5.9, 1.85) * mm});
            skLineSegment(sketch, "E1437", {"start": v(-5.9, 1.85) * mm, "end": v(-5.89, 1.85) * mm});
            skLineSegment(sketch, "E1438", {"start": v(-5.89, 1.85) * mm, "end": v(-5.87, 1.85) * mm});
            skLineSegment(sketch, "E1439", {"start": v(-5.87, 1.85) * mm, "end": v(-5.86, 1.86) * mm});
            skLineSegment(sketch, "E1440", {"start": v(-5.86, 1.86) * mm, "end": v(-5.85, 1.86) * mm});
            skLineSegment(sketch, "E1441", {"start": v(-5.85, 1.86) * mm, "end": v(-5.84, 1.86) * mm});
            skLineSegment(sketch, "E1442", {"start": v(-5.84, 1.86) * mm, "end": v(-5.82, 1.86) * mm});
            skLineSegment(sketch, "E1443", {"start": v(-5.82, 1.86) * mm, "end": v(-5.81, 1.86) * mm});
            skLineSegment(sketch, "E1444", {"start": v(-5.81, 1.86) * mm, "end": v(-5.8, 1.87) * mm});
            skLineSegment(sketch, "E1445", {"start": v(-5.8, 1.87) * mm, "end": v(-5.79, 1.87) * mm});
            skLineSegment(sketch, "E1446", {"start": v(-5.79, 1.87) * mm, "end": v(-5.77, 1.88) * mm});
            skLineSegment(sketch, "E1447", {"start": v(-5.77, 1.88) * mm, "end": v(-5.76, 1.88) * mm});
            skLineSegment(sketch, "E1448", {"start": v(-5.76, 1.88) * mm, "end": v(-5.75, 1.89) * mm});
            skLineSegment(sketch, "E1449", {"start": v(-5.75, 1.89) * mm, "end": v(-5.74, 1.9) * mm});
            skLineSegment(sketch, "E1450", {"start": v(-5.74, 1.9) * mm, "end": v(-5.73, 1.9) * mm});
            skLineSegment(sketch, "E1451", {"start": v(-5.73, 1.9) * mm, "end": v(-5.71, 1.9) * mm});
            skLineSegment(sketch, "E1452", {"start": v(-5.71, 1.9) * mm, "end": v(-5.7, 1.9) * mm});
            skLineSegment(sketch, "E1453", {"start": v(-5.7, 1.9) * mm, "end": v(-5.69, 1.9) * mm});
            skLineSegment(sketch, "E1454", {"start": v(-5.69, 1.9) * mm, "end": v(-5.68, 1.91) * mm});
            skLineSegment(sketch, "E1455", {"start": v(-5.68, 1.91) * mm, "end": v(-5.66, 1.92) * mm});
            skLineSegment(sketch, "E1456", {"start": v(-5.66, 1.92) * mm, "end": v(-5.65, 1.92) * mm});
            skLineSegment(sketch, "E1457", {"start": v(-5.65, 1.92) * mm, "end": v(-5.64, 1.92) * mm});
            skLineSegment(sketch, "E1458", {"start": v(-5.64, 1.92) * mm, "end": v(-5.63, 1.93) * mm});
            skLineSegment(sketch, "E1459", {"start": v(-5.63, 1.93) * mm, "end": v(-5.62, 1.93) * mm});
            skLineSegment(sketch, "E1460", {"start": v(-5.62, 1.93) * mm, "end": v(-5.6, 1.94) * mm});
            skLineSegment(sketch, "E1461", {"start": v(-5.6, 1.94) * mm, "end": v(-5.6, 1.94) * mm});
            skLineSegment(sketch, "E1462", {"start": v(-5.6, 1.94) * mm, "end": v(-5.58, 1.94) * mm});
            skLineSegment(sketch, "E1463", {"start": v(-5.58, 1.94) * mm, "end": v(-5.57, 1.95) * mm});
            skLineSegment(sketch, "E1464", {"start": v(-5.57, 1.95) * mm, "end": v(-5.55, 1.95) * mm});
            skLineSegment(sketch, "E1465", {"start": v(-5.55, 1.95) * mm, "end": v(-5.54, 1.95) * mm});
            skLineSegment(sketch, "E1466", {"start": v(-5.54, 1.95) * mm, "end": v(-5.53, 1.96) * mm});
            skLineSegment(sketch, "E1467", {"start": v(-5.53, 1.96) * mm, "end": v(-5.52, 1.96) * mm});
            skLineSegment(sketch, "E1468", {"start": v(-5.52, 1.96) * mm, "end": v(-5.5, 1.96) * mm});
            skLineSegment(sketch, "E1469", {"start": v(-5.5, 1.96) * mm, "end": v(-5.5, 1.97) * mm});
            skLineSegment(sketch, "E1470", {"start": v(-5.5, 1.97) * mm, "end": v(-5.48, 1.97) * mm});
            skLineSegment(sketch, "E1471", {"start": v(-5.48, 1.97) * mm, "end": v(-5.47, 1.97) * mm});
            skLineSegment(sketch, "E1472", {"start": v(-5.47, 1.97) * mm, "end": v(-5.46, 1.97) * mm});
            skLineSegment(sketch, "E1473", {"start": v(-5.46, 1.97) * mm, "end": v(-5.44, 1.98) * mm});
            skLineSegment(sketch, "E1474", {"start": v(-5.44, 1.98) * mm, "end": v(-5.43, 1.98) * mm});
            skLineSegment(sketch, "E1475", {"start": v(-5.43, 1.98) * mm, "end": v(-5.42, 1.98) * mm});
            skLineSegment(sketch, "E1476", {"start": v(-5.42, 1.98) * mm, "end": v(-5.4, 1.98) * mm});
            skLineSegment(sketch, "E1477", {"start": v(-5.4, 1.98) * mm, "end": v(-5.37, 2) * mm});
            skLineSegment(sketch, "E1478", {"start": v(-5.37, 2) * mm, "end": v(-5.33, 2.01) * mm});
            skLineSegment(sketch, "E1479", {"start": v(-5.33, 2.01) * mm, "end": v(-5.3, 2.03) * mm});
            skLineSegment(sketch, "E1480", {"start": v(-5.3, 2.03) * mm, "end": v(-5.25, 2.04) * mm});
            skLineSegment(sketch, "E1481", {"start": v(-5.25, 2.04) * mm, "end": v(-5.21, 2.06) * mm});
            skLineSegment(sketch, "E1482", {"start": v(-5.21, 2.06) * mm, "end": v(-5.17, 2.07) * mm});
            skLineSegment(sketch, "E1483", {"start": v(-5.17, 2.07) * mm, "end": v(-5.13, 2.09) * mm});
            skLineSegment(sketch, "E1484", {"start": v(-5.13, 2.09) * mm, "end": v(-5.1, 2.1) * mm});
            skLineSegment(sketch, "E1485", {"start": v(-5.1, 2.1) * mm, "end": v(-5.06, 2.12) * mm});
            skLineSegment(sketch, "E1486", {"start": v(-5.06, 2.12) * mm, "end": v(-5.02, 2.13) * mm});
            skLineSegment(sketch, "E1487", {"start": v(-5.02, 2.13) * mm, "end": v(-4.98, 2.15) * mm});
            skLineSegment(sketch, "E1488", {"start": v(-4.98, 2.15) * mm, "end": v(-4.94, 2.16) * mm});
            skLineSegment(sketch, "E1489", {"start": v(-4.94, 2.16) * mm, "end": v(-4.9, 2.17) * mm});
            skLineSegment(sketch, "E1490", {"start": v(-4.9, 2.17) * mm, "end": v(-4.86, 2.19) * mm});
            skLineSegment(sketch, "E1491", {"start": v(-4.86, 2.19) * mm, "end": v(-4.82, 2.2) * mm});
            skLineSegment(sketch, "E1492", {"start": v(-4.82, 2.2) * mm, "end": v(-4.78, 2.22) * mm});
            skLineSegment(sketch, "E1493", {"start": v(-4.78, 2.22) * mm, "end": v(-4.74, 2.23) * mm});
            skLineSegment(sketch, "E1494", {"start": v(-4.74, 2.23) * mm, "end": v(-4.7, 2.25) * mm});
            skLineSegment(sketch, "E1495", {"start": v(-4.7, 2.25) * mm, "end": v(-4.67, 2.26) * mm});
            skLineSegment(sketch, "E1496", {"start": v(-4.67, 2.26) * mm, "end": v(-4.63, 2.28) * mm});
            skLineSegment(sketch, "E1497", {"start": v(-4.63, 2.28) * mm, "end": v(-4.59, 2.3) * mm});
            skLineSegment(sketch, "E1498", {"start": v(-4.59, 2.3) * mm, "end": v(-4.55, 2.3) * mm});
            skLineSegment(sketch, "E1499", {"start": v(-4.55, 2.3) * mm, "end": v(-4.5, 2.32) * mm});
            skLineSegment(sketch, "E1500", {"start": v(-4.5, 2.32) * mm, "end": v(-4.47, 2.34) * mm});
            skLineSegment(sketch, "E1501", {"start": v(-4.47, 2.34) * mm, "end": v(-4.43, 2.35) * mm});
            skLineSegment(sketch, "E1502", {"start": v(-4.43, 2.35) * mm, "end": v(-4.4, 2.37) * mm});
            skLineSegment(sketch, "E1503", {"start": v(-4.4, 2.37) * mm, "end": v(-4.35, 2.38) * mm});
            skLineSegment(sketch, "E1504", {"start": v(-4.35, 2.38) * mm, "end": v(-4.31, 2.4) * mm});
            skLineSegment(sketch, "E1505", {"start": v(-4.31, 2.4) * mm, "end": v(-4.27, 2.4) * mm});
            skLineSegment(sketch, "E1506", {"start": v(-4.27, 2.4) * mm, "end": v(-4.24, 2.42) * mm});
            skLineSegment(sketch, "E1507", {"start": v(-4.24, 2.42) * mm, "end": v(-4.2, 2.44) * mm});
            skLineSegment(sketch, "E1508", {"start": v(-4.2, 2.44) * mm, "end": v(-4.16, 2.45) * mm});
            skLineSegment(sketch, "E1509", {"start": v(-4.16, 2.45) * mm, "end": v(-4.12, 2.46) * mm});
            skLineSegment(sketch, "E1510", {"start": v(-4.12, 2.46) * mm, "end": v(-4.08, 2.46) * mm});
            skLineSegment(sketch, "E1511", {"start": v(-4.08, 2.46) * mm, "end": v(-4.04, 2.46) * mm});
            skLineSegment(sketch, "E1512", {"start": v(-4.04, 2.46) * mm, "end": v(-4, 2.46) * mm});
            skLineSegment(sketch, "E1513", {"start": v(-4, 2.46) * mm, "end": v(-3.97, 2.46) * mm});
            skLineSegment(sketch, "E1514", {"start": v(-3.97, 2.46) * mm, "end": v(-3.94, 2.46) * mm});
            skLineSegment(sketch, "E1515", {"start": v(-3.94, 2.46) * mm, "end": v(-3.9, 2.46) * mm});
            skLineSegment(sketch, "E1516", {"start": v(-3.9, 2.46) * mm, "end": v(-3.87, 2.45) * mm});
            skLineSegment(sketch, "E1517", {"start": v(-3.87, 2.45) * mm, "end": v(-3.84, 2.45) * mm});
            skLineSegment(sketch, "E1518", {"start": v(-3.84, 2.45) * mm, "end": v(-3.81, 2.44) * mm});
            skLineSegment(sketch, "E1519", {"start": v(-3.81, 2.44) * mm, "end": v(-3.78, 2.43) * mm});
            skLineSegment(sketch, "E1520", {"start": v(-3.78, 2.43) * mm, "end": v(-3.75, 2.42) * mm});
            skLineSegment(sketch, "E1521", {"start": v(-3.75, 2.42) * mm, "end": v(-3.73, 2.41) * mm});
            skLineSegment(sketch, "E1522", {"start": v(-3.73, 2.41) * mm, "end": v(-3.7, 2.4) * mm});
            skLineSegment(sketch, "E1523", {"start": v(-3.7, 2.4) * mm, "end": v(-3.67, 2.39) * mm});
            skLineSegment(sketch, "E1524", {"start": v(-3.67, 2.39) * mm, "end": v(-3.65, 2.38) * mm});
            skLineSegment(sketch, "E1525", {"start": v(-3.65, 2.38) * mm, "end": v(-3.63, 2.36) * mm});
            skLineSegment(sketch, "E1526", {"start": v(-3.63, 2.36) * mm, "end": v(-3.6, 2.34) * mm});
            skLineSegment(sketch, "E1527", {"start": v(-3.6, 2.34) * mm, "end": v(-3.58, 2.33) * mm});
            skLineSegment(sketch, "E1528", {"start": v(-3.58, 2.33) * mm, "end": v(-3.56, 2.3) * mm});
            skLineSegment(sketch, "E1529", {"start": v(-3.56, 2.3) * mm, "end": v(-3.54, 2.29) * mm});
            skLineSegment(sketch, "E1530", {"start": v(-3.54, 2.29) * mm, "end": v(-3.52, 2.27) * mm});
            skLineSegment(sketch, "E1531", {"start": v(-3.52, 2.27) * mm, "end": v(-3.5, 2.24) * mm});
            skLineSegment(sketch, "E1532", {"start": v(-3.5, 2.24) * mm, "end": v(-3.48, 2.22) * mm});
            skLineSegment(sketch, "E1533", {"start": v(-3.48, 2.22) * mm, "end": v(-3.47, 2.2) * mm});
            skLineSegment(sketch, "E1534", {"start": v(-3.47, 2.2) * mm, "end": v(-3.45, 2.17) * mm});
            skLineSegment(sketch, "E1535", {"start": v(-3.45, 2.17) * mm, "end": v(-3.44, 2.14) * mm});
            skLineSegment(sketch, "E1536", {"start": v(-3.44, 2.14) * mm, "end": v(-3.42, 2.11) * mm});
            skLineSegment(sketch, "E1537", {"start": v(-3.42, 2.11) * mm, "end": v(-3.4, 2.08) * mm});
            skLineSegment(sketch, "E1538", {"start": v(-3.4, 2.08) * mm, "end": v(-3.4, 2.05) * mm});
            skLineSegment(sketch, "E1539", {"start": v(-3.4, 2.05) * mm, "end": v(-3.39, 2.02) * mm});
            skLineSegment(sketch, "E1540", {"start": v(-3.39, 2.02) * mm, "end": v(-3.38, 1.98) * mm});
            skLineSegment(sketch, "E1541", {"start": v(-3.38, 1.98) * mm, "end": v(-3.4, 1.94) * mm});
            skLineSegment(sketch, "E1542", {"start": v(-3.4, 1.94) * mm, "end": v(-3.44, 1.89) * mm});
            skLineSegment(sketch, "E1543", {"start": v(-3.44, 1.89) * mm, "end": v(-3.46, 1.84) * mm});
            skLineSegment(sketch, "E1544", {"start": v(-3.46, 1.84) * mm, "end": v(-3.5, 1.8) * mm});
            skLineSegment(sketch, "E1545", {"start": v(-3.5, 1.8) * mm, "end": v(-3.52, 1.75) * mm});
            skLineSegment(sketch, "E1546", {"start": v(-3.52, 1.75) * mm, "end": v(-3.55, 1.7) * mm});
            skLineSegment(sketch, "E1547", {"start": v(-3.55, 1.7) * mm, "end": v(-3.59, 1.66) * mm});
            skLineSegment(sketch, "E1548", {"start": v(-3.59, 1.66) * mm, "end": v(-3.62, 1.61) * mm});
            skLineSegment(sketch, "E1549", {"start": v(-3.62, 1.61) * mm, "end": v(-3.65, 1.57) * mm});
            skLineSegment(sketch, "E1550", {"start": v(-3.65, 1.57) * mm, "end": v(-3.68, 1.52) * mm});
            skLineSegment(sketch, "E1551", {"start": v(-3.68, 1.52) * mm, "end": v(-3.7, 1.48) * mm});
            skLineSegment(sketch, "E1552", {"start": v(-3.7, 1.48) * mm, "end": v(-3.74, 1.44) * mm});
            skLineSegment(sketch, "E1553", {"start": v(-3.74, 1.44) * mm, "end": v(-3.77, 1.4) * mm});
            skLineSegment(sketch, "E1554", {"start": v(-3.77, 1.4) * mm, "end": v(-3.8, 1.35) * mm});
            skLineSegment(sketch, "E1555", {"start": v(-3.8, 1.35) * mm, "end": v(-3.83, 1.31) * mm});
            skLineSegment(sketch, "E1556", {"start": v(-3.83, 1.31) * mm, "end": v(-3.86, 1.27) * mm});
            skLineSegment(sketch, "E1557", {"start": v(-3.86, 1.27) * mm, "end": v(-3.9, 1.23) * mm});
            skLineSegment(sketch, "E1558", {"start": v(-3.9, 1.23) * mm, "end": v(-3.93, 1.2) * mm});
            skLineSegment(sketch, "E1559", {"start": v(-3.93, 1.2) * mm, "end": v(-3.96, 1.15) * mm});
            skLineSegment(sketch, "E1560", {"start": v(-3.96, 1.15) * mm, "end": v(-4, 1.11) * mm});
            skLineSegment(sketch, "E1561", {"start": v(-4, 1.11) * mm, "end": v(-4.03, 1.08) * mm});
            skLineSegment(sketch, "E1562", {"start": v(-4.03, 1.08) * mm, "end": v(-4.06, 1.04) * mm});
            skLineSegment(sketch, "E1563", {"start": v(-4.06, 1.04) * mm, "end": v(-4.1, 1) * mm});
            skLineSegment(sketch, "E1564", {"start": v(-4.1, 1) * mm, "end": v(-4.12, 0.97) * mm});
            skLineSegment(sketch, "E1565", {"start": v(-4.12, 0.97) * mm, "end": v(-4.16, 0.93) * mm});
            skLineSegment(sketch, "E1566", {"start": v(-4.16, 0.93) * mm, "end": v(-4.19, 0.9) * mm});
            skLineSegment(sketch, "E1567", {"start": v(-4.19, 0.9) * mm, "end": v(-4.22, 0.86) * mm});
            skLineSegment(sketch, "E1568", {"start": v(-4.22, 0.86) * mm, "end": v(-4.26, 0.83) * mm});
            skLineSegment(sketch, "E1569", {"start": v(-4.26, 0.83) * mm, "end": v(-4.29, 0.8) * mm});
            skLineSegment(sketch, "E1570", {"start": v(-4.29, 0.8) * mm, "end": v(-4.32, 0.76) * mm});
            skLineSegment(sketch, "E1571", {"start": v(-4.32, 0.76) * mm, "end": v(-4.36, 0.73) * mm});
            skLineSegment(sketch, "E1572", {"start": v(-4.36, 0.73) * mm, "end": v(-4.4, 0.7) * mm});
            skLineSegment(sketch, "E1573", {"start": v(-4.4, 0.7) * mm, "end": v(-4.42, 0.66) * mm});
            skLineSegment(sketch, "E1574", {"start": v(-4.42, 0.66) * mm, "end": v(-4.45, 0.63) * mm});
            skLineSegment(sketch, "E1575", {"start": v(-4.45, 0.63) * mm, "end": v(-4.48, 0.6) * mm});
            skLineSegment(sketch, "E1576", {"start": v(-4.48, 0.6) * mm, "end": v(-4.51, 0.57) * mm});
            skLineSegment(sketch, "E1577", {"start": v(-4.51, 0.57) * mm, "end": v(-4.54, 0.55) * mm});
            skLineSegment(sketch, "E1578", {"start": v(-4.54, 0.55) * mm, "end": v(-4.57, 0.52) * mm});
            skLineSegment(sketch, "E1579", {"start": v(-4.57, 0.52) * mm, "end": v(-4.6, 0.5) * mm});
            skLineSegment(sketch, "E1580", {"start": v(-4.6, 0.5) * mm, "end": v(-4.62, 0.46) * mm});
            skLineSegment(sketch, "E1581", {"start": v(-4.62, 0.46) * mm, "end": v(-4.65, 0.44) * mm});
            skLineSegment(sketch, "E1582", {"start": v(-4.65, 0.44) * mm, "end": v(-4.68, 0.41) * mm});
            skLineSegment(sketch, "E1583", {"start": v(-4.68, 0.41) * mm, "end": v(-4.7, 0.39) * mm});
            skLineSegment(sketch, "E1584", {"start": v(-4.7, 0.39) * mm, "end": v(-4.72, 0.36) * mm});
            skLineSegment(sketch, "E1585", {"start": v(-4.72, 0.36) * mm, "end": v(-4.75, 0.34) * mm});
            skLineSegment(sketch, "E1586", {"start": v(-4.75, 0.34) * mm, "end": v(-4.77, 0.32) * mm});
            skLineSegment(sketch, "E1587", {"start": v(-4.77, 0.32) * mm, "end": v(-4.8, 0.3) * mm});
            skLineSegment(sketch, "E1588", {"start": v(-4.8, 0.3) * mm, "end": v(-4.81, 0.28) * mm});
            skLineSegment(sketch, "E1589", {"start": v(-4.81, 0.28) * mm, "end": v(-4.83, 0.26) * mm});
            skLineSegment(sketch, "E1590", {"start": v(-4.83, 0.26) * mm, "end": v(-4.85, 0.24) * mm});
            skLineSegment(sketch, "E1591", {"start": v(-4.85, 0.24) * mm, "end": v(-4.87, 0.22) * mm});
            skLineSegment(sketch, "E1592", {"start": v(-4.87, 0.22) * mm, "end": v(-4.89, 0.2) * mm});
            skLineSegment(sketch, "E1593", {"start": v(-4.89, 0.2) * mm, "end": v(-4.9, 0.18) * mm});
            skLineSegment(sketch, "E1594", {"start": v(-4.9, 0.18) * mm, "end": v(-4.92, 0.16) * mm});
            skLineSegment(sketch, "E1595", {"start": v(-4.92, 0.16) * mm, "end": v(-4.94, 0.15) * mm});
            skLineSegment(sketch, "E1596", {"start": v(-4.94, 0.15) * mm, "end": v(-4.96, 0.13) * mm});
            skLineSegment(sketch, "E1597", {"start": v(-4.96, 0.13) * mm, "end": v(-4.97, 0.12) * mm});
            skLineSegment(sketch, "E1598", {"start": v(-4.97, 0.12) * mm, "end": v(-4.98, 0.1) * mm});
            skLineSegment(sketch, "E1599", {"start": v(-4.98, 0.1) * mm, "end": v(-5, 0.09) * mm});
            skLineSegment(sketch, "E1600", {"start": v(-5, 0.09) * mm, "end": v(-5.01, 0.08) * mm});
            skLineSegment(sketch, "E1601", {"start": v(-5.01, 0.08) * mm, "end": v(-5.02, 0.06) * mm});
            skLineSegment(sketch, "E1602", {"start": v(-5.02, 0.06) * mm, "end": v(-5.03, 0.05) * mm});
            skLineSegment(sketch, "E1603", {"start": v(-5.03, 0.05) * mm, "end": v(-5.05, 0.04) * mm});
            skLineSegment(sketch, "E1604", {"start": v(-5.05, 0.04) * mm, "end": v(-5.06, 0.03) * mm});
            skLineSegment(sketch, "E1605", {"start": v(-5.06, 0.03) * mm, "end": v(-5.05, 0.03) * mm});
            skLineSegment(sketch, "E1606", {"start": v(-5.05, 0.03) * mm, "end": v(-5.04, 0.03) * mm});
            skLineSegment(sketch, "E1607", {"start": v(-5.04, 0.03) * mm, "end": v(-5.03, 0.02) * mm});
            skLineSegment(sketch, "E1608", {"start": v(-5.03, 0.02) * mm, "end": v(-5.02, 0.02) * mm});
            skLineSegment(sketch, "E1609", {"start": v(-5.02, 0.02) * mm, "end": v(-5, 0.02) * mm});
            skLineSegment(sketch, "E1610", {"start": v(-5, 0.02) * mm, "end": v(-5, 0.01) * mm});
            skLineSegment(sketch, "E1611", {"start": v(-5, 0.01) * mm, "end": v(-4.99, 0) * mm});
            skLineSegment(sketch, "E1612", {"start": v(-4.99, 0) * mm, "end": v(-4.98, 0) * mm});
            skLineSegment(sketch, "E1613", {"start": v(-4.98, 0) * mm, "end": v(-4.97, 0) * mm});
            skLineSegment(sketch, "E1614", {"start": v(-4.97, 0) * mm, "end": v(-4.96, 0) * mm});
            skLineSegment(sketch, "E1615", {"start": v(-4.96, 0) * mm, "end": v(-4.95, 0) * mm});
            skLineSegment(sketch, "E1616", {"start": v(-4.95, 0) * mm, "end": v(-4.94, -0.01) * mm});
            skLineSegment(sketch, "E1617", {"start": v(-4.94, -0.01) * mm, "end": v(-4.94, -0.02) * mm});
            skLineSegment(sketch, "E1618", {"start": v(-4.94, -0.02) * mm, "end": v(-4.93, -0.03) * mm});
            skLineSegment(sketch, "E1619", {"start": v(-4.93, -0.03) * mm, "end": v(-4.92, -0.03) * mm});
            skLineSegment(sketch, "E1620", {"start": v(-4.92, -0.03) * mm, "end": v(-4.9, -0.04) * mm});
            skLineSegment(sketch, "E1621", {"start": v(-4.9, -0.04) * mm, "end": v(-4.9, -0.04) * mm});
            skLineSegment(sketch, "E1622", {"start": v(-4.9, -0.04) * mm, "end": v(-4.9, -0.05) * mm});
            skLineSegment(sketch, "E1623", {"start": v(-4.9, -0.05) * mm, "end": v(-4.88, -0.06) * mm});
            skLineSegment(sketch, "E1624", {"start": v(-4.88, -0.06) * mm, "end": v(-4.88, -0.06) * mm});
            skLineSegment(sketch, "E1625", {"start": v(-4.88, -0.06) * mm, "end": v(-4.87, -0.07) * mm});
            skLineSegment(sketch, "E1626", {"start": v(-4.87, -0.07) * mm, "end": v(-4.86, -0.08) * mm});
            skLineSegment(sketch, "E1627", {"start": v(-4.86, -0.08) * mm, "end": v(-4.85, -0.09) * mm});
            skLineSegment(sketch, "E1628", {"start": v(-4.85, -0.09) * mm, "end": v(-4.84, -0.1) * mm});
            skLineSegment(sketch, "E1629", {"start": v(-4.84, -0.1) * mm, "end": v(-4.84, -0.1) * mm});
            skLineSegment(sketch, "E1630", {"start": v(-4.84, -0.1) * mm, "end": v(-4.83, -0.1) * mm});
            skLineSegment(sketch, "E1631", {"start": v(-4.83, -0.1) * mm, "end": v(-4.82, -0.12) * mm});
            skLineSegment(sketch, "E1632", {"start": v(-4.82, -0.12) * mm, "end": v(-4.81, -0.13) * mm});
            skLineSegment(sketch, "E1633", {"start": v(-4.81, -0.13) * mm, "end": v(-4.8, -0.14) * mm});
            skLineSegment(sketch, "E1634", {"start": v(-4.8, -0.14) * mm, "end": v(-4.8, -0.14) * mm});
            skLineSegment(sketch, "E1635", {"start": v(-4.8, -0.14) * mm, "end": v(-4.79, -0.15) * mm});
            skLineSegment(sketch, "E1636", {"start": v(-4.79, -0.15) * mm, "end": v(-4.78, -0.16) * mm});
            skLineSegment(sketch, "E1637", {"start": v(-4.78, -0.16) * mm, "end": v(-4.75, -0.14) * mm});
            skLineSegment(sketch, "E1638", {"start": v(-4.75, -0.14) * mm, "end": v(-4.72, -0.12) * mm});
            skLineSegment(sketch, "E1639", {"start": v(-4.72, -0.12) * mm, "end": v(-4.68, -0.1) * mm});
            skLineSegment(sketch, "E1640", {"start": v(-4.68, -0.1) * mm, "end": v(-4.65, -0.08) * mm});
            skLineSegment(sketch, "E1641", {"start": v(-4.65, -0.08) * mm, "end": v(-4.62, -0.05) * mm});
            skLineSegment(sketch, "E1642", {"start": v(-4.62, -0.05) * mm, "end": v(-4.59, -0.03) * mm});
            skLineSegment(sketch, "E1643", {"start": v(-4.59, -0.03) * mm, "end": v(-4.56, 0) * mm});
            skLineSegment(sketch, "E1644", {"start": v(-4.56, 0) * mm, "end": v(-4.53, 0.01) * mm});
            skLineSegment(sketch, "E1645", {"start": v(-4.53, 0.01) * mm, "end": v(-4.5, 0.04) * mm});
            skLineSegment(sketch, "E1646", {"start": v(-4.5, 0.04) * mm, "end": v(-4.47, 0.06) * mm});
            skLineSegment(sketch, "E1647", {"start": v(-4.47, 0.06) * mm, "end": v(-4.44, 0.08) * mm});
            skLineSegment(sketch, "E1648", {"start": v(-4.44, 0.08) * mm, "end": v(-4.42, 0.1) * mm});
            skLineSegment(sketch, "E1649", {"start": v(-4.42, 0.1) * mm, "end": v(-4.39, 0.13) * mm});
            skLineSegment(sketch, "E1650", {"start": v(-4.39, 0.13) * mm, "end": v(-4.36, 0.15) * mm});
            skLineSegment(sketch, "E1651", {"start": v(-4.36, 0.15) * mm, "end": v(-4.34, 0.17) * mm});
            skLineSegment(sketch, "E1652", {"start": v(-4.34, 0.17) * mm, "end": v(-4.31, 0.2) * mm});
            skLineSegment(sketch, "E1653", {"start": v(-4.31, 0.2) * mm, "end": v(-4.29, 0.22) * mm});
            skLineSegment(sketch, "E1654", {"start": v(-4.29, 0.22) * mm, "end": v(-4.27, 0.24) * mm});
            skLineSegment(sketch, "E1655", {"start": v(-4.27, 0.24) * mm, "end": v(-4.24, 0.27) * mm});
            skLineSegment(sketch, "E1656", {"start": v(-4.24, 0.27) * mm, "end": v(-4.22, 0.3) * mm});
            skLineSegment(sketch, "E1657", {"start": v(-4.22, 0.3) * mm, "end": v(-4.2, 0.31) * mm});
            skLineSegment(sketch, "E1658", {"start": v(-4.2, 0.31) * mm, "end": v(-4.18, 0.34) * mm});
            skLineSegment(sketch, "E1659", {"start": v(-4.18, 0.34) * mm, "end": v(-4.16, 0.36) * mm});
            skLineSegment(sketch, "E1660", {"start": v(-4.16, 0.36) * mm, "end": v(-4.14, 0.39) * mm});
            skLineSegment(sketch, "E1661", {"start": v(-4.14, 0.39) * mm, "end": v(-4.12, 0.4) * mm});
            skLineSegment(sketch, "E1662", {"start": v(-4.12, 0.4) * mm, "end": v(-4.1, 0.43) * mm});
            skLineSegment(sketch, "E1663", {"start": v(-4.1, 0.43) * mm, "end": v(-4.08, 0.46) * mm});
            skLineSegment(sketch, "E1664", {"start": v(-4.08, 0.46) * mm, "end": v(-4.06, 0.48) * mm});
            skLineSegment(sketch, "E1665", {"start": v(-4.06, 0.48) * mm, "end": v(-4.05, 0.5) * mm});
            skLineSegment(sketch, "E1666", {"start": v(-4.05, 0.5) * mm, "end": v(-4.03, 0.53) * mm});
            skLineSegment(sketch, "E1667", {"start": v(-4.03, 0.53) * mm, "end": v(-4.02, 0.55) * mm});
            skLineSegment(sketch, "E1668", {"start": v(-4.02, 0.55) * mm, "end": v(-4, 0.58) * mm});
            skLineSegment(sketch, "E1669", {"start": v(-4, 0.58) * mm, "end": v(-4, 0.6) * mm});
            skLineSegment(sketch, "E1670", {"start": v(-4, 0.6) * mm, "end": v(-3.99, 0.6) * mm});
            skLineSegment(sketch, "E1671", {"start": v(-3.99, 0.6) * mm, "end": v(-3.98, 0.62) * mm});
            skLineSegment(sketch, "E1672", {"start": v(-3.98, 0.62) * mm, "end": v(-3.97, 0.64) * mm});
            skLineSegment(sketch, "E1673", {"start": v(-3.97, 0.64) * mm, "end": v(-3.97, 0.65) * mm});
            skLineSegment(sketch, "E1674", {"start": v(-3.97, 0.65) * mm, "end": v(-3.96, 0.66) * mm});
            skLineSegment(sketch, "E1675", {"start": v(-3.96, 0.66) * mm, "end": v(-3.96, 0.68) * mm});
            skLineSegment(sketch, "E1676", {"start": v(-3.96, 0.68) * mm, "end": v(-3.95, 0.7) * mm});
            skLineSegment(sketch, "E1677", {"start": v(-3.95, 0.7) * mm, "end": v(-3.95, 0.7) * mm});
            skLineSegment(sketch, "E1678", {"start": v(-3.95, 0.7) * mm, "end": v(-3.95, 0.72) * mm});
            skLineSegment(sketch, "E1679", {"start": v(-3.95, 0.72) * mm, "end": v(-3.94, 0.73) * mm});
            skLineSegment(sketch, "E1680", {"start": v(-3.94, 0.73) * mm, "end": v(-3.94, 0.74) * mm});
            skLineSegment(sketch, "E1681", {"start": v(-3.94, 0.74) * mm, "end": v(-3.94, 0.76) * mm});
            skLineSegment(sketch, "E1682", {"start": v(-3.94, 0.76) * mm, "end": v(-3.94, 0.77) * mm});
            skLineSegment(sketch, "E1683", {"start": v(-3.94, 0.77) * mm, "end": v(-3.93, 0.78) * mm});
            skLineSegment(sketch, "E1684", {"start": v(-3.93, 0.78) * mm, "end": v(-3.93, 0.8) * mm});
            skLineSegment(sketch, "E1685", {"start": v(-3.93, 0.8) * mm, "end": v(-3.93, 0.8) * mm});
            skLineSegment(sketch, "E1686", {"start": v(-3.93, 0.8) * mm, "end": v(-3.93, 0.82) * mm});
            skLineSegment(sketch, "E1687", {"start": v(-3.93, 0.82) * mm, "end": v(-3.93, 0.83) * mm});
            skLineSegment(sketch, "E1688", {"start": v(-3.93, 0.83) * mm, "end": v(-3.93, 0.84) * mm});
            skLineSegment(sketch, "E1689", {"start": v(-3.93, 0.84) * mm, "end": v(-3.93, 0.85) * mm});
            skLineSegment(sketch, "E1690", {"start": v(-3.93, 0.85) * mm, "end": v(-3.93, 0.86) * mm});
            skLineSegment(sketch, "E1691", {"start": v(-3.93, 0.86) * mm, "end": v(-3.93, 0.87) * mm});
            skLineSegment(sketch, "E1692", {"start": v(-3.93, 0.87) * mm, "end": v(-3.94, 0.89) * mm});
            skLineSegment(sketch, "E1693", {"start": v(-3.94, 0.89) * mm, "end": v(-3.94, 0.9) * mm});
            skLineSegment(sketch, "E1694", {"start": v(-3.94, 0.9) * mm, "end": v(-3.94, 0.9) * mm});
            skLineSegment(sketch, "E1695", {"start": v(-3.94, 0.9) * mm, "end": v(-3.94, 0.92) * mm});
            skLineSegment(sketch, "E1696", {"start": v(-3.94, 0.92) * mm, "end": v(-3.95, 0.93) * mm});
            skLineSegment(sketch, "E1697", {"start": v(-3.95, 0.93) * mm, "end": v(-3.95, 0.94) * mm});
            skLineSegment(sketch, "E1698", {"start": v(-3.95, 0.94) * mm, "end": v(-3.95, 0.95) * mm});
            skLineSegment(sketch, "E1699", {"start": v(-3.95, 0.95) * mm, "end": v(-3.96, 0.96) * mm});
            skLineSegment(sketch, "E1700", {"start": v(-3.96, 0.96) * mm, "end": v(-3.96, 0.97) * mm});
            skLineSegment(sketch, "E1701", {"start": v(-3.96, 0.97) * mm, "end": v(-3.92, 0.94) * mm});
            skLineSegment(sketch, "E1702", {"start": v(-3.92, 0.94) * mm, "end": v(-3.89, 0.92) * mm});
            skLineSegment(sketch, "E1703", {"start": v(-3.89, 0.92) * mm, "end": v(-3.85, 0.9) * mm});
            skLineSegment(sketch, "E1704", {"start": v(-3.85, 0.9) * mm, "end": v(-3.82, 0.87) * mm});
            skLineSegment(sketch, "E1705", {"start": v(-3.82, 0.87) * mm, "end": v(-3.78, 0.85) * mm});
            skLineSegment(sketch, "E1706", {"start": v(-3.78, 0.85) * mm, "end": v(-3.75, 0.82) * mm});
            skLineSegment(sketch, "E1707", {"start": v(-3.75, 0.82) * mm, "end": v(-3.72, 0.8) * mm});
            skLineSegment(sketch, "E1708", {"start": v(-3.72, 0.8) * mm, "end": v(-3.69, 0.78) * mm});
            skLineSegment(sketch, "E1709", {"start": v(-3.69, 0.78) * mm, "end": v(-3.66, 0.75) * mm});
            skLineSegment(sketch, "E1710", {"start": v(-3.66, 0.75) * mm, "end": v(-3.63, 0.73) * mm});
            skLineSegment(sketch, "E1711", {"start": v(-3.63, 0.73) * mm, "end": v(-3.6, 0.7) * mm});
            skLineSegment(sketch, "E1712", {"start": v(-3.6, 0.7) * mm, "end": v(-3.58, 0.68) * mm});
            skLineSegment(sketch, "E1713", {"start": v(-3.58, 0.68) * mm, "end": v(-3.56, 0.66) * mm});
            skLineSegment(sketch, "E1714", {"start": v(-3.56, 0.66) * mm, "end": v(-3.53, 0.63) * mm});
            skLineSegment(sketch, "E1715", {"start": v(-3.53, 0.63) * mm, "end": v(-3.51, 0.61) * mm});
            skLineSegment(sketch, "E1716", {"start": v(-3.51, 0.61) * mm, "end": v(-3.5, 0.59) * mm});
            skLineSegment(sketch, "E1717", {"start": v(-3.5, 0.59) * mm, "end": v(-3.47, 0.56) * mm});
            skLineSegment(sketch, "E1718", {"start": v(-3.47, 0.56) * mm, "end": v(-3.46, 0.54) * mm});
            skLineSegment(sketch, "E1719", {"start": v(-3.46, 0.54) * mm, "end": v(-3.44, 0.52) * mm});
            skLineSegment(sketch, "E1720", {"start": v(-3.44, 0.52) * mm, "end": v(-3.42, 0.5) * mm});
            skLineSegment(sketch, "E1721", {"start": v(-3.42, 0.5) * mm, "end": v(-3.41, 0.47) * mm});
            skLineSegment(sketch, "E1722", {"start": v(-3.41, 0.47) * mm, "end": v(-3.4, 0.45) * mm});
            skLineSegment(sketch, "E1723", {"start": v(-3.4, 0.45) * mm, "end": v(-3.39, 0.43) * mm});
            skLineSegment(sketch, "E1724", {"start": v(-3.39, 0.43) * mm, "end": v(-3.38, 0.4) * mm});
            skLineSegment(sketch, "E1725", {"start": v(-3.38, 0.4) * mm, "end": v(-3.37, 0.38) * mm});
            skLineSegment(sketch, "E1726", {"start": v(-3.37, 0.38) * mm, "end": v(-3.36, 0.36) * mm});
            skLineSegment(sketch, "E1727", {"start": v(-3.36, 0.36) * mm, "end": v(-3.35, 0.34) * mm});
            skLineSegment(sketch, "E1728", {"start": v(-3.35, 0.34) * mm, "end": v(-3.35, 0.32) * mm});
            skLineSegment(sketch, "E1729", {"start": v(-3.35, 0.32) * mm, "end": v(-3.34, 0.3) * mm});
            skLineSegment(sketch, "E1730", {"start": v(-3.34, 0.3) * mm, "end": v(-3.34, 0.27) * mm});
            skLineSegment(sketch, "E1731", {"start": v(-3.34, 0.27) * mm, "end": v(-3.34, 0.25) * mm});
            skLineSegment(sketch, "E1732", {"start": v(-3.34, 0.25) * mm, "end": v(-3.34, 0.23) * mm});
            skLineSegment(sketch, "E1733", {"start": v(-3.34, 0.23) * mm, "end": v(-3.34, 0.21) * mm});
            skLineSegment(sketch, "E1734", {"start": v(-3.34, 0.21) * mm, "end": v(-3.34, 0.2) * mm});
            skLineSegment(sketch, "E1735", {"start": v(-3.34, 0.2) * mm, "end": v(-3.34, 0.18) * mm});
            skLineSegment(sketch, "E1736", {"start": v(-3.34, 0.18) * mm, "end": v(-3.34, 0.17) * mm});
            skLineSegment(sketch, "E1737", {"start": v(-3.34, 0.17) * mm, "end": v(-3.35, 0.16) * mm});
            skLineSegment(sketch, "E1738", {"start": v(-3.35, 0.16) * mm, "end": v(-3.35, 0.14) * mm});
            skLineSegment(sketch, "E1739", {"start": v(-3.35, 0.14) * mm, "end": v(-3.36, 0.13) * mm});
            skLineSegment(sketch, "E1740", {"start": v(-3.36, 0.13) * mm, "end": v(-3.36, 0.11) * mm});
            skLineSegment(sketch, "E1741", {"start": v(-3.36, 0.11) * mm, "end": v(-3.37, 0.1) * mm});
            skLineSegment(sketch, "E1742", {"start": v(-3.37, 0.1) * mm, "end": v(-3.38, 0.09) * mm});
            skLineSegment(sketch, "E1743", {"start": v(-3.38, 0.09) * mm, "end": v(-3.39, 0.08) * mm});
            skLineSegment(sketch, "E1744", {"start": v(-3.39, 0.08) * mm, "end": v(-3.4, 0.06) * mm});
            skLineSegment(sketch, "E1745", {"start": v(-3.4, 0.06) * mm, "end": v(-3.4, 0.05) * mm});
            skLineSegment(sketch, "E1746", {"start": v(-3.4, 0.05) * mm, "end": v(-3.42, 0.04) * mm});
            skLineSegment(sketch, "E1747", {"start": v(-3.42, 0.04) * mm, "end": v(-3.43, 0.02) * mm});
            skLineSegment(sketch, "E1748", {"start": v(-3.43, 0.02) * mm, "end": v(-3.44, 0.01) * mm});
            skLineSegment(sketch, "E1749", {"start": v(-3.44, 0.01) * mm, "end": v(-3.46, 0) * mm});
            skLineSegment(sketch, "E1750", {"start": v(-3.46, 0) * mm, "end": v(-3.47, -0.01) * mm});
            skLineSegment(sketch, "E1751", {"start": v(-3.47, -0.01) * mm, "end": v(-3.49, -0.02) * mm});
            skLineSegment(sketch, "E1752", {"start": v(-3.49, -0.02) * mm, "end": v(-3.5, -0.04) * mm});
            skLineSegment(sketch, "E1753", {"start": v(-3.5, -0.04) * mm, "end": v(-3.52, -0.05) * mm});
            skLineSegment(sketch, "E1754", {"start": v(-3.52, -0.05) * mm, "end": v(-3.54, -0.06) * mm});
            skLineSegment(sketch, "E1755", {"start": v(-3.54, -0.06) * mm, "end": v(-3.56, -0.07) * mm});
            skLineSegment(sketch, "E1756", {"start": v(-3.56, -0.07) * mm, "end": v(-3.58, -0.08) * mm});
            skLineSegment(sketch, "E1757", {"start": v(-3.58, -0.08) * mm, "end": v(-3.6, -0.1) * mm});
            skLineSegment(sketch, "E1758", {"start": v(-3.6, -0.1) * mm, "end": v(-3.62, -0.1) * mm});
            skLineSegment(sketch, "E1759", {"start": v(-3.62, -0.1) * mm, "end": v(-3.64, -0.11) * mm});
            skLineSegment(sketch, "E1760", {"start": v(-3.64, -0.11) * mm, "end": v(-3.67, -0.12) * mm});
            skLineSegment(sketch, "E1761", {"start": v(-3.67, -0.12) * mm, "end": v(-3.69, -0.13) * mm});
            skLineSegment(sketch, "E1762", {"start": v(-3.69, -0.13) * mm, "end": v(-3.71, -0.14) * mm});
            skLineSegment(sketch, "E1763", {"start": v(-3.71, -0.14) * mm, "end": v(-3.74, -0.15) * mm});
            skLineSegment(sketch, "E1764", {"start": v(-3.74, -0.15) * mm, "end": v(-3.77, -0.16) * mm});
            skLineSegment(sketch, "E1765", {"start": v(-3.77, -0.16) * mm, "end": v(-3.8, -0.17) * mm});
            skLineSegment(sketch, "E1766", {"start": v(-3.8, -0.17) * mm, "end": v(-3.83, -0.18) * mm});
            skLineSegment(sketch, "E1767", {"start": v(-3.83, -0.18) * mm, "end": v(-3.85, -0.2) * mm});
            skLineSegment(sketch, "E1768", {"start": v(-3.85, -0.2) * mm, "end": v(-3.88, -0.2) * mm});
            skLineSegment(sketch, "E1769", {"start": v(-3.88, -0.2) * mm, "end": v(-3.91, -0.2) * mm});
            skLineSegment(sketch, "E1770", {"start": v(-3.91, -0.2) * mm, "end": v(-3.94, -0.22) * mm});
            skLineSegment(sketch, "E1771", {"start": v(-3.94, -0.22) * mm, "end": v(-3.97, -0.22) * mm});
            skLineSegment(sketch, "E1772", {"start": v(-3.97, -0.22) * mm, "end": v(-4, -0.23) * mm});
            skLineSegment(sketch, "E1773", {"start": v(-4, -0.23) * mm, "end": v(-4.03, -0.24) * mm});
            skLineSegment(sketch, "E1774", {"start": v(-4.03, -0.24) * mm, "end": v(-4.06, -0.25) * mm});
            skLineSegment(sketch, "E1775", {"start": v(-4.06, -0.25) * mm, "end": v(-4.09, -0.25) * mm});
            skLineSegment(sketch, "E1776", {"start": v(-4.09, -0.25) * mm, "end": v(-4.12, -0.26) * mm});
            skLineSegment(sketch, "E1777", {"start": v(-4.12, -0.26) * mm, "end": v(-4.15, -0.27) * mm});
            skLineSegment(sketch, "E1778", {"start": v(-4.15, -0.27) * mm, "end": v(-4.18, -0.27) * mm});
            skLineSegment(sketch, "E1779", {"start": v(-4.18, -0.27) * mm, "end": v(-4.2, -0.28) * mm});
            skLineSegment(sketch, "E1780", {"start": v(-4.2, -0.28) * mm, "end": v(-4.24, -0.28) * mm});
            skLineSegment(sketch, "E1781", {"start": v(-4.24, -0.28) * mm, "end": v(-4.26, -0.29) * mm});
            skLineSegment(sketch, "E1782", {"start": v(-4.26, -0.29) * mm, "end": v(-4.3, -0.3) * mm});
            skLineSegment(sketch, "E1783", {"start": v(-4.3, -0.3) * mm, "end": v(-4.32, -0.3) * mm});
            skLineSegment(sketch, "E1784", {"start": v(-4.32, -0.3) * mm, "end": v(-4.35, -0.3) * mm});
            skLineSegment(sketch, "E1785", {"start": v(-4.35, -0.3) * mm, "end": v(-4.38, -0.3) * mm});
            skLineSegment(sketch, "E1786", {"start": v(-4.38, -0.3) * mm, "end": v(-4.41, -0.3) * mm});
            skLineSegment(sketch, "E1787", {"start": v(-4.41, -0.3) * mm, "end": v(-4.44, -0.3) * mm});
            skLineSegment(sketch, "E1788", {"start": v(-4.44, -0.3) * mm, "end": v(-4.47, -0.31) * mm});
            skLineSegment(sketch, "E1789", {"start": v(-4.47, -0.31) * mm, "end": v(-4.5, -0.31) * mm});
            skLineSegment(sketch, "E1790", {"start": v(-4.5, -0.31) * mm, "end": v(-4.53, -0.31) * mm});
            skLineSegment(sketch, "E1791", {"start": v(-4.53, -0.31) * mm, "end": v(-4.56, -0.32) * mm});
            skLineSegment(sketch, "E1792", {"start": v(-4.56, -0.32) * mm, "end": v(-4.59, -0.32) * mm});
            skLineSegment(sketch, "E1793", {"start": v(-4.59, -0.32) * mm, "end": v(-4.62, -0.32) * mm});
            skLineSegment(sketch, "E1794", {"start": v(-4.62, -0.32) * mm, "end": v(-4.65, -0.32) * mm});
            skLineSegment(sketch, "E1795", {"start": v(-4.65, -0.32) * mm, "end": v(-4.68, -0.32) * mm});
            skLineSegment(sketch, "E1796", {"start": v(-4.68, -0.32) * mm, "end": v(-4.7, -0.32) * mm});
            skLineSegment(sketch, "E1797", {"start": v(-4.7, -0.32) * mm, "end": v(-4.66, -0.33) * mm});
            skLineSegment(sketch, "E1798", {"start": v(-4.66, -0.33) * mm, "end": v(-4.62, -0.34) * mm});
            skLineSegment(sketch, "E1799", {"start": v(-4.62, -0.34) * mm, "end": v(-4.58, -0.35) * mm});
            skLineSegment(sketch, "E1800", {"start": v(-4.58, -0.35) * mm, "end": v(-4.54, -0.36) * mm});
            skLineSegment(sketch, "E1801", {"start": v(-4.54, -0.36) * mm, "end": v(-4.5, -0.38) * mm});
            skLineSegment(sketch, "E1802", {"start": v(-4.5, -0.38) * mm, "end": v(-4.46, -0.4) * mm});
            skLineSegment(sketch, "E1803", {"start": v(-4.46, -0.4) * mm, "end": v(-4.42, -0.4) * mm});
            skLineSegment(sketch, "E1804", {"start": v(-4.42, -0.4) * mm, "end": v(-4.38, -0.42) * mm});
            skLineSegment(sketch, "E1805", {"start": v(-4.38, -0.42) * mm, "end": v(-4.34, -0.44) * mm});
            skLineSegment(sketch, "E1806", {"start": v(-4.34, -0.44) * mm, "end": v(-4.3, -0.45) * mm});
            skLineSegment(sketch, "E1807", {"start": v(-4.3, -0.45) * mm, "end": v(-4.26, -0.47) * mm});
            skLineSegment(sketch, "E1808", {"start": v(-4.26, -0.47) * mm, "end": v(-4.22, -0.49) * mm});
            skLineSegment(sketch, "E1809", {"start": v(-4.22, -0.49) * mm, "end": v(-4.18, -0.5) * mm});
            skLineSegment(sketch, "E1810", {"start": v(-4.18, -0.5) * mm, "end": v(-4.15, -0.52) * mm});
            skLineSegment(sketch, "E1811", {"start": v(-4.15, -0.52) * mm, "end": v(-4.1, -0.54) * mm});
            skLineSegment(sketch, "E1812", {"start": v(-4.1, -0.54) * mm, "end": v(-4.07, -0.56) * mm});
            skLineSegment(sketch, "E1813", {"start": v(-4.07, -0.56) * mm, "end": v(-4.03, -0.59) * mm});
            skLineSegment(sketch, "E1814", {"start": v(-4.03, -0.59) * mm, "end": v(-4, -0.6) * mm});
            skLineSegment(sketch, "E1815", {"start": v(-4, -0.6) * mm, "end": v(-3.96, -0.63) * mm});
            skLineSegment(sketch, "E1816", {"start": v(-3.96, -0.63) * mm, "end": v(-3.92, -0.65) * mm});
            skLineSegment(sketch, "E1817", {"start": v(-3.92, -0.65) * mm, "end": v(-3.88, -0.68) * mm});
            skLineSegment(sketch, "E1818", {"start": v(-3.88, -0.68) * mm, "end": v(-3.85, -0.7) * mm});
            skLineSegment(sketch, "E1819", {"start": v(-3.85, -0.7) * mm, "end": v(-3.81, -0.73) * mm});
            skLineSegment(sketch, "E1820", {"start": v(-3.81, -0.73) * mm, "end": v(-3.77, -0.75) * mm});
            skLineSegment(sketch, "E1821", {"start": v(-3.77, -0.75) * mm, "end": v(-3.74, -0.78) * mm});
            skLineSegment(sketch, "E1822", {"start": v(-3.74, -0.78) * mm, "end": v(-3.7, -0.8) * mm});
            skLineSegment(sketch, "E1823", {"start": v(-3.7, -0.8) * mm, "end": v(-3.67, -0.83) * mm});
            skLineSegment(sketch, "E1824", {"start": v(-3.67, -0.83) * mm, "end": v(-3.63, -0.86) * mm});
            skLineSegment(sketch, "E1825", {"start": v(-3.63, -0.86) * mm, "end": v(-3.6, -0.9) * mm});
            skLineSegment(sketch, "E1826", {"start": v(-3.6, -0.9) * mm, "end": v(-3.56, -0.92) * mm});
            skLineSegment(sketch, "E1827", {"start": v(-3.56, -0.92) * mm, "end": v(-3.53, -0.95) * mm});
            skLineSegment(sketch, "E1828", {"start": v(-3.53, -0.95) * mm, "end": v(-3.5, -0.98) * mm});
            skLineSegment(sketch, "E1829", {"start": v(-3.5, -0.98) * mm, "end": v(-3.5, -0.97) * mm});
            skLineSegment(sketch, "E1830", {"start": v(-3.5, -0.97) * mm, "end": v(-3.51, -0.96) * mm});
            skLineSegment(sketch, "E1831", {"start": v(-3.51, -0.96) * mm, "end": v(-3.52, -0.95) * mm});
            skLineSegment(sketch, "E1832", {"start": v(-3.52, -0.95) * mm, "end": v(-3.53, -0.94) * mm});
            skLineSegment(sketch, "E1833", {"start": v(-3.53, -0.94) * mm, "end": v(-3.54, -0.93) * mm});
            skLineSegment(sketch, "E1834", {"start": v(-3.54, -0.93) * mm, "end": v(-3.55, -0.92) * mm});
            skLineSegment(sketch, "E1835", {"start": v(-3.55, -0.92) * mm, "end": v(-3.55, -0.9) * mm});
            skLineSegment(sketch, "E1836", {"start": v(-3.55, -0.9) * mm, "end": v(-3.56, -0.9) * mm});
            skLineSegment(sketch, "E1837", {"start": v(-3.56, -0.9) * mm, "end": v(-3.57, -0.88) * mm});
            skLineSegment(sketch, "E1838", {"start": v(-3.57, -0.88) * mm, "end": v(-3.57, -0.87) * mm});
            skLineSegment(sketch, "E1839", {"start": v(-3.57, -0.87) * mm, "end": v(-3.58, -0.86) * mm});
            skLineSegment(sketch, "E1840", {"start": v(-3.58, -0.86) * mm, "end": v(-3.58, -0.85) * mm});
            skLineSegment(sketch, "E1841", {"start": v(-3.58, -0.85) * mm, "end": v(-3.59, -0.84) * mm});
            skLineSegment(sketch, "E1842", {"start": v(-3.59, -0.84) * mm, "end": v(-3.6, -0.84) * mm});
            skLineSegment(sketch, "E1843", {"start": v(-3.6, -0.84) * mm, "end": v(-3.6, -0.83) * mm});
            skLineSegment(sketch, "E1844", {"start": v(-3.6, -0.83) * mm, "end": v(-3.6, -0.82) * mm});
            skLineSegment(sketch, "E1845", {"start": v(-3.6, -0.82) * mm, "end": v(-3.6, -0.8) * mm});
            skLineSegment(sketch, "E1846", {"start": v(-3.6, -0.8) * mm, "end": v(-3.6, -0.8) * mm});
            skLineSegment(sketch, "E1847", {"start": v(-3.6, -0.8) * mm, "end": v(-3.61, -0.8) * mm});
            skLineSegment(sketch, "E1848", {"start": v(-3.61, -0.8) * mm, "end": v(-3.61, -0.79) * mm});
            skLineSegment(sketch, "E1849", {"start": v(-3.61, -0.79) * mm, "end": v(-3.61, -0.78) * mm});
            skLineSegment(sketch, "E1850", {"start": v(-3.61, -0.78) * mm, "end": v(-3.62, -0.77) * mm});
            skLineSegment(sketch, "E1851", {"start": v(-3.62, -0.77) * mm, "end": v(-3.62, -0.76) * mm});
            skLineSegment(sketch, "E1852", {"start": v(-3.62, -0.76) * mm, "end": v(-3.62, -0.76) * mm});
            skLineSegment(sketch, "E1853", {"start": v(-3.62, -0.76) * mm, "end": v(-3.62, -0.75) * mm});
            skLineSegment(sketch, "E1854", {"start": v(-3.62, -0.75) * mm, "end": v(-3.62, -0.74) * mm});
            skLineSegment(sketch, "E1855", {"start": v(-3.62, -0.74) * mm, "end": v(-3.62, -0.74) * mm});
            skLineSegment(sketch, "E1856", {"start": v(-3.62, -0.74) * mm, "end": v(-3.62, -0.73) * mm});
            skLineSegment(sketch, "E1857", {"start": v(-3.62, -0.73) * mm, "end": v(-3.62, -0.73) * mm});
            skLineSegment(sketch, "E1858", {"start": v(-3.62, -0.73) * mm, "end": v(-3.61, -0.72) * mm});
            skLineSegment(sketch, "E1859", {"start": v(-3.61, -0.72) * mm, "end": v(-3.61, -0.72) * mm});
            skLineSegment(sketch, "E1860", {"start": v(-3.61, -0.72) * mm, "end": v(-3.61, -0.71) * mm});
            skLineSegment(sketch, "E1861", {"start": v(-3.61, -0.71) * mm, "end": v(-3.58, -0.71) * mm});
            skLineSegment(sketch, "E1862", {"start": v(-3.58, -0.71) * mm, "end": v(-3.56, -0.71) * mm});
            skLineSegment(sketch, "E1863", {"start": v(-3.56, -0.71) * mm, "end": v(-3.53, -0.7) * mm});
            skLineSegment(sketch, "E1864", {"start": v(-3.53, -0.7) * mm, "end": v(-3.5, -0.7) * mm});
            skLineSegment(sketch, "E1865", {"start": v(-3.5, -0.7) * mm, "end": v(-3.47, -0.7) * mm});
            skLineSegment(sketch, "E1866", {"start": v(-3.47, -0.7) * mm, "end": v(-3.44, -0.7) * mm});
            skLineSegment(sketch, "E1867", {"start": v(-3.44, -0.7) * mm, "end": v(-3.4, -0.7) * mm});
            skLineSegment(sketch, "E1868", {"start": v(-3.4, -0.7) * mm, "end": v(-3.38, -0.7) * mm});
            skLineSegment(sketch, "E1869", {"start": v(-3.38, -0.7) * mm, "end": v(-3.35, -0.7) * mm});
            skLineSegment(sketch, "E1870", {"start": v(-3.35, -0.7) * mm, "end": v(-3.31, -0.7) * mm});
            skLineSegment(sketch, "E1871", {"start": v(-3.31, -0.7) * mm, "end": v(-3.28, -0.7) * mm});
            skLineSegment(sketch, "E1872", {"start": v(-3.28, -0.7) * mm, "end": v(-3.25, -0.7) * mm});
            skLineSegment(sketch, "E1873", {"start": v(-3.25, -0.7) * mm, "end": v(-3.22, -0.7) * mm});
            skLineSegment(sketch, "E1874", {"start": v(-3.22, -0.7) * mm, "end": v(-3.18, -0.69) * mm});
            skLineSegment(sketch, "E1875", {"start": v(-3.18, -0.69) * mm, "end": v(-3.15, -0.69) * mm});
            skLineSegment(sketch, "E1876", {"start": v(-3.15, -0.69) * mm, "end": v(-3.11, -0.68) * mm});
            skLineSegment(sketch, "E1877", {"start": v(-3.11, -0.68) * mm, "end": v(-3.08, -0.68) * mm});
            skLineSegment(sketch, "E1878", {"start": v(-3.08, -0.68) * mm, "end": v(-3.04, -0.67) * mm});
            skLineSegment(sketch, "E1879", {"start": v(-3.04, -0.67) * mm, "end": v(-3, -0.67) * mm});
            skLineSegment(sketch, "E1880", {"start": v(-3, -0.67) * mm, "end": v(-2.97, -0.66) * mm});
            skLineSegment(sketch, "E1881", {"start": v(-2.97, -0.66) * mm, "end": v(-2.93, -0.66) * mm});
            skLineSegment(sketch, "E1882", {"start": v(-2.93, -0.66) * mm, "end": v(-2.9, -0.66) * mm});
            skLineSegment(sketch, "E1883", {"start": v(-2.9, -0.66) * mm, "end": v(-2.85, -0.65) * mm});
            skLineSegment(sketch, "E1884", {"start": v(-2.85, -0.65) * mm, "end": v(-2.81, -0.64) * mm});
            skLineSegment(sketch, "E1885", {"start": v(-2.81, -0.64) * mm, "end": v(-2.77, -0.64) * mm});
            skLineSegment(sketch, "E1886", {"start": v(-2.77, -0.64) * mm, "end": v(-2.73, -0.63) * mm});
            skLineSegment(sketch, "E1887", {"start": v(-2.73, -0.63) * mm, "end": v(-2.7, -0.63) * mm});
            skLineSegment(sketch, "E1888", {"start": v(-2.7, -0.63) * mm, "end": v(-2.65, -0.62) * mm});
            skLineSegment(sketch, "E1889", {"start": v(-2.65, -0.62) * mm, "end": v(-2.6, -0.61) * mm});
            skLineSegment(sketch, "E1890", {"start": v(-2.6, -0.61) * mm, "end": v(-2.56, -0.6) * mm});
            skLineSegment(sketch, "E1891", {"start": v(-2.56, -0.6) * mm, "end": v(-2.52, -0.6) * mm});
            skLineSegment(sketch, "E1892", {"start": v(-2.52, -0.6) * mm, "end": v(-2.48, -0.6) * mm});
            skLineSegment(sketch, "E1893", {"start": v(-2.48, -0.6) * mm, "end": v(-2.45, -0.6) * mm});
            skLineSegment(sketch, "E1894", {"start": v(-2.45, -0.6) * mm, "end": v(-2.43, -0.59) * mm});
            skLineSegment(sketch, "E1895", {"start": v(-2.43, -0.59) * mm, "end": v(-2.4, -0.59) * mm});
            skLineSegment(sketch, "E1896", {"start": v(-2.4, -0.59) * mm, "end": v(-2.38, -0.58) * mm});
            skLineSegment(sketch, "E1897", {"start": v(-2.38, -0.58) * mm, "end": v(-2.36, -0.58) * mm});
            skLineSegment(sketch, "E1898", {"start": v(-2.36, -0.58) * mm, "end": v(-2.33, -0.58) * mm});
            skLineSegment(sketch, "E1899", {"start": v(-2.33, -0.58) * mm, "end": v(-2.3, -0.58) * mm});
            skLineSegment(sketch, "E1900", {"start": v(-2.3, -0.58) * mm, "end": v(-2.28, -0.57) * mm});
            skLineSegment(sketch, "E1901", {"start": v(-2.28, -0.57) * mm, "end": v(-2.26, -0.57) * mm});
            skLineSegment(sketch, "E1902", {"start": v(-2.26, -0.57) * mm, "end": v(-2.24, -0.57) * mm});
            skLineSegment(sketch, "E1903", {"start": v(-2.24, -0.57) * mm, "end": v(-2.21, -0.57) * mm});
            skLineSegment(sketch, "E1904", {"start": v(-2.21, -0.57) * mm, "end": v(-2.2, -0.56) * mm});
            skLineSegment(sketch, "E1905", {"start": v(-2.2, -0.56) * mm, "end": v(-2.17, -0.56) * mm});
            skLineSegment(sketch, "E1906", {"start": v(-2.17, -0.56) * mm, "end": v(-2.14, -0.56) * mm});
            skLineSegment(sketch, "E1907", {"start": v(-2.14, -0.56) * mm, "end": v(-2.12, -0.56) * mm});
            skLineSegment(sketch, "E1908", {"start": v(-2.12, -0.56) * mm, "end": v(-2.1, -0.55) * mm});
            skLineSegment(sketch, "E1909", {"start": v(-2.1, -0.55) * mm, "end": v(-2.07, -0.55) * mm});
            skLineSegment(sketch, "E1910", {"start": v(-2.07, -0.55) * mm, "end": v(-2.05, -0.55) * mm});
            skLineSegment(sketch, "E1911", {"start": v(-2.05, -0.55) * mm, "end": v(-2.03, -0.55) * mm});
            skLineSegment(sketch, "E1912", {"start": v(-2.03, -0.55) * mm, "end": v(-2, -0.54) * mm});
            skLineSegment(sketch, "E1913", {"start": v(-2, -0.54) * mm, "end": v(-1.98, -0.54) * mm});
            skLineSegment(sketch, "E1914", {"start": v(-1.98, -0.54) * mm, "end": v(-1.96, -0.54) * mm});
            skLineSegment(sketch, "E1915", {"start": v(-1.96, -0.54) * mm, "end": v(-1.94, -0.54) * mm});
            skLineSegment(sketch, "E1916", {"start": v(-1.94, -0.54) * mm, "end": v(-1.91, -0.53) * mm});
            skLineSegment(sketch, "E1917", {"start": v(-1.91, -0.53) * mm, "end": v(-1.9, -0.53) * mm});
            skLineSegment(sketch, "E1918", {"start": v(-1.9, -0.53) * mm, "end": v(-1.87, -0.53) * mm});
            skLineSegment(sketch, "E1919", {"start": v(-1.87, -0.53) * mm, "end": v(-1.85, -0.53) * mm});
            skLineSegment(sketch, "E1920", {"start": v(-1.85, -0.53) * mm, "end": v(-1.82, -0.53) * mm});
            skLineSegment(sketch, "E1921", {"start": v(-1.82, -0.53) * mm, "end": v(-1.8, -0.52) * mm});
            skLineSegment(sketch, "E1922", {"start": v(-1.8, -0.52) * mm, "end": v(-1.78, -0.52) * mm});
            skLineSegment(sketch, "E1923", {"start": v(-1.78, -0.52) * mm, "end": v(-1.76, -0.52) * mm});
            skLineSegment(sketch, "E1924", {"start": v(-1.76, -0.52) * mm, "end": v(-1.74, -0.52) * mm});
            skLineSegment(sketch, "E1925", {"start": v(-1.74, -0.52) * mm, "end": v(-1.74, -0.16) * mm});
            skLineSegment(sketch, "E1926", {"start": v(-1.74, -0.16) * mm, "end": v(-1.76, -0.17) * mm});
            skLineSegment(sketch, "E1927", {"start": v(-1.76, -0.17) * mm, "end": v(-1.8, -0.17) * mm});
            skLineSegment(sketch, "E1928", {"start": v(-1.8, -0.17) * mm, "end": v(-1.82, -0.17) * mm});
            skLineSegment(sketch, "E1929", {"start": v(-1.82, -0.17) * mm, "end": v(-1.85, -0.17) * mm});
            skLineSegment(sketch, "E1930", {"start": v(-1.85, -0.17) * mm, "end": v(-1.88, -0.18) * mm});
            skLineSegment(sketch, "E1931", {"start": v(-1.88, -0.18) * mm, "end": v(-1.9, -0.18) * mm});
            skLineSegment(sketch, "E1932", {"start": v(-1.9, -0.18) * mm, "end": v(-1.93, -0.18) * mm});
            skLineSegment(sketch, "E1933", {"start": v(-1.93, -0.18) * mm, "end": v(-1.96, -0.19) * mm});
            skLineSegment(sketch, "E1934", {"start": v(-1.96, -0.19) * mm, "end": v(-1.99, -0.19) * mm});
            skLineSegment(sketch, "E1935", {"start": v(-1.99, -0.19) * mm, "end": v(-2.01, -0.2) * mm});
            skLineSegment(sketch, "E1936", {"start": v(-2.01, -0.2) * mm, "end": v(-2.04, -0.2) * mm});
            skLineSegment(sketch, "E1937", {"start": v(-2.04, -0.2) * mm, "end": v(-2.06, -0.2) * mm});
            skLineSegment(sketch, "E1938", {"start": v(-2.06, -0.2) * mm, "end": v(-2.1, -0.2) * mm});
            skLineSegment(sketch, "E1939", {"start": v(-2.1, -0.2) * mm, "end": v(-2.12, -0.2) * mm});
            skLineSegment(sketch, "E1940", {"start": v(-2.12, -0.2) * mm, "end": v(-2.14, -0.2) * mm});
            skLineSegment(sketch, "E1941", {"start": v(-2.14, -0.2) * mm, "end": v(-2.17, -0.21) * mm});
            skLineSegment(sketch, "E1942", {"start": v(-2.17, -0.21) * mm, "end": v(-2.19, -0.22) * mm});
            skLineSegment(sketch, "E1943", {"start": v(-2.19, -0.22) * mm, "end": v(-2.21, -0.22) * mm});
            skLineSegment(sketch, "E1944", {"start": v(-2.21, -0.22) * mm, "end": v(-2.24, -0.22) * mm});
            skLineSegment(sketch, "E1945", {"start": v(-2.24, -0.22) * mm, "end": v(-2.26, -0.23) * mm});
            skLineSegment(sketch, "E1946", {"start": v(-2.26, -0.23) * mm, "end": v(-2.28, -0.23) * mm});
            skLineSegment(sketch, "E1947", {"start": v(-2.28, -0.23) * mm, "end": v(-2.3, -0.24) * mm});
            skLineSegment(sketch, "E1948", {"start": v(-2.3, -0.24) * mm, "end": v(-2.33, -0.24) * mm});
            skLineSegment(sketch, "E1949", {"start": v(-2.33, -0.24) * mm, "end": v(-2.35, -0.24) * mm});
            skLineSegment(sketch, "E1950", {"start": v(-2.35, -0.24) * mm, "end": v(-2.37, -0.25) * mm});
            skLineSegment(sketch, "E1951", {"start": v(-2.37, -0.25) * mm, "end": v(-2.4, -0.25) * mm});
            skLineSegment(sketch, "E1952", {"start": v(-2.4, -0.25) * mm, "end": v(-2.42, -0.26) * mm});
            skLineSegment(sketch, "E1953", {"start": v(-2.42, -0.26) * mm, "end": v(-2.44, -0.26) * mm});
            skLineSegment(sketch, "E1954", {"start": v(-2.44, -0.26) * mm, "end": v(-2.46, -0.27) * mm});
            skLineSegment(sketch, "E1955", {"start": v(-2.46, -0.27) * mm, "end": v(-2.48, -0.27) * mm});
            skLineSegment(sketch, "E1956", {"start": v(-2.48, -0.27) * mm, "end": v(-2.5, -0.28) * mm});
            skLineSegment(sketch, "E1957", {"start": v(-2.5, -0.28) * mm, "end": v(-2.52, -0.28) * mm});
            skLineSegment(sketch, "E1958", {"start": v(-2.52, -0.28) * mm, "end": v(-2.53, -0.28) * mm});
            skLineSegment(sketch, "E1959", {"start": v(-2.53, -0.28) * mm, "end": v(-2.54, -0.28) * mm});
            skLineSegment(sketch, "E1960", {"start": v(-2.54, -0.28) * mm, "end": v(-2.55, -0.28) * mm});
            skLineSegment(sketch, "E1961", {"start": v(-2.55, -0.28) * mm, "end": v(-2.56, -0.28) * mm});
            skLineSegment(sketch, "E1962", {"start": v(-2.56, -0.28) * mm, "end": v(-2.58, -0.28) * mm});
            skLineSegment(sketch, "E1963", {"start": v(-2.58, -0.28) * mm, "end": v(-2.59, -0.27) * mm});
            skLineSegment(sketch, "E1964", {"start": v(-2.59, -0.27) * mm, "end": v(-2.6, -0.27) * mm});
            skLineSegment(sketch, "E1965", {"start": v(-2.6, -0.27) * mm, "end": v(-2.61, -0.27) * mm});
            skLineSegment(sketch, "E1966", {"start": v(-2.61, -0.27) * mm, "end": v(-2.62, -0.27) * mm});
            skLineSegment(sketch, "E1967", {"start": v(-2.62, -0.27) * mm, "end": v(-2.63, -0.26) * mm});
            skLineSegment(sketch, "E1968", {"start": v(-2.63, -0.26) * mm, "end": v(-2.65, -0.26) * mm});
            skLineSegment(sketch, "E1969", {"start": v(-2.65, -0.26) * mm, "end": v(-2.66, -0.25) * mm});
            skLineSegment(sketch, "E1970", {"start": v(-2.66, -0.25) * mm, "end": v(-2.67, -0.25) * mm});
            skLineSegment(sketch, "E1971", {"start": v(-2.67, -0.25) * mm, "end": v(-2.68, -0.24) * mm});
            skLineSegment(sketch, "E1972", {"start": v(-2.68, -0.24) * mm, "end": v(-2.7, -0.24) * mm});
            skLineSegment(sketch, "E1973", {"start": v(-2.7, -0.24) * mm, "end": v(-2.7, -0.23) * mm});
            skLineSegment(sketch, "E1974", {"start": v(-2.7, -0.23) * mm, "end": v(-2.71, -0.23) * mm});
            skLineSegment(sketch, "E1975", {"start": v(-2.71, -0.23) * mm, "end": v(-2.72, -0.22) * mm});
            skLineSegment(sketch, "E1976", {"start": v(-2.72, -0.22) * mm, "end": v(-2.73, -0.21) * mm});
            skLineSegment(sketch, "E1977", {"start": v(-2.73, -0.21) * mm, "end": v(-2.75, -0.2) * mm});
            skLineSegment(sketch, "E1978", {"start": v(-2.75, -0.2) * mm, "end": v(-2.76, -0.2) * mm});
            skLineSegment(sketch, "E1979", {"start": v(-2.76, -0.2) * mm, "end": v(-2.77, -0.19) * mm});
            skLineSegment(sketch, "E1980", {"start": v(-2.77, -0.19) * mm, "end": v(-2.78, -0.18) * mm});
            skLineSegment(sketch, "E1981", {"start": v(-2.78, -0.18) * mm, "end": v(-2.79, -0.17) * mm});
            skLineSegment(sketch, "E1982", {"start": v(-2.79, -0.17) * mm, "end": v(-2.8, -0.16) * mm});
            skLineSegment(sketch, "E1983", {"start": v(-2.8, -0.16) * mm, "end": v(-2.8, -0.15) * mm});
            skLineSegment(sketch, "E1984", {"start": v(-2.8, -0.15) * mm, "end": v(-2.82, -0.14) * mm});
            skLineSegment(sketch, "E1985", {"start": v(-2.82, -0.14) * mm, "end": v(-2.83, -0.13) * mm});
            skLineSegment(sketch, "E1986", {"start": v(-2.83, -0.13) * mm, "end": v(-2.84, -0.12) * mm});
            skLineSegment(sketch, "E1987", {"start": v(-2.84, -0.12) * mm, "end": v(-2.85, -0.1) * mm});
            skLineSegment(sketch, "E1988", {"start": v(-2.85, -0.1) * mm, "end": v(-2.86, -0.1) * mm});
            skLineSegment(sketch, "E1989", {"start": v(-2.86, -0.1) * mm, "end": v(-2.87, -0.09) * mm});
            skLineSegment(sketch, "E1990", {"start": v(-2.87, -0.09) * mm, "end": v(-2.88, -0.07) * mm});
            skLineSegment(sketch, "E1991", {"start": v(-2.88, -0.07) * mm, "end": v(-2.89, -0.06) * mm});
            skLineSegment(sketch, "E1992", {"start": v(-2.89, -0.06) * mm, "end": v(-2.9, -0.04) * mm});
            skLineSegment(sketch, "E1993", {"start": v(-2.9, -0.04) * mm, "end": v(-2.9, -0.03) * mm});
            skLineSegment(sketch, "E1994", {"start": v(-2.9, -0.03) * mm, "end": v(-2.91, -0.01) * mm});
            skLineSegment(sketch, "E1995", {"start": v(-2.91, -0.01) * mm, "end": v(-2.92, 0) * mm});
            skLineSegment(sketch, "E1996", {"start": v(-2.92, 0) * mm, "end": v(-2.93, 0.02) * mm});
            skLineSegment(sketch, "E1997", {"start": v(-2.93, 0.02) * mm, "end": v(-2.94, 0.03) * mm});
            skLineSegment(sketch, "E1998", {"start": v(-2.94, 0.03) * mm, "end": v(-2.95, 0.05) * mm});
            skLineSegment(sketch, "E1999", {"start": v(-2.95, 0.05) * mm, "end": v(-2.95, 0.06) * mm});
            skLineSegment(sketch, "E2000", {"start": v(-2.95, 0.06) * mm, "end": v(-2.96, 0.08) * mm});
            skLineSegment(sketch, "E2001", {"start": v(-2.96, 0.08) * mm, "end": v(-2.97, 0.1) * mm});
            skLineSegment(sketch, "E2002", {"start": v(-2.97, 0.1) * mm, "end": v(-2.98, 0.1) * mm});
            skLineSegment(sketch, "E2003", {"start": v(-2.98, 0.1) * mm, "end": v(-2.98, 0.12) * mm});
            skLineSegment(sketch, "E2004", {"start": v(-2.98, 0.12) * mm, "end": v(-2.99, 0.13) * mm});
            skLineSegment(sketch, "E2005", {"start": v(-2.99, 0.13) * mm, "end": v(-3, 0.15) * mm});
            skLineSegment(sketch, "E2006", {"start": v(-3, 0.15) * mm, "end": v(-3, 0.16) * mm});
            skLineSegment(sketch, "E2007", {"start": v(-3, 0.16) * mm, "end": v(-3, 0.18) * mm});
            skLineSegment(sketch, "E2008", {"start": v(-3, 0.18) * mm, "end": v(-3.01, 0.2) * mm});
            skLineSegment(sketch, "E2009", {"start": v(-3.01, 0.2) * mm, "end": v(-3.02, 0.2) * mm});
            skLineSegment(sketch, "E2010", {"start": v(-3.02, 0.2) * mm, "end": v(-3.02, 0.22) * mm});
            skLineSegment(sketch, "E2011", {"start": v(-3.02, 0.22) * mm, "end": v(-3.03, 0.24) * mm});
            skLineSegment(sketch, "E2012", {"start": v(-3.03, 0.24) * mm, "end": v(-3.03, 0.25) * mm});
            skLineSegment(sketch, "E2013", {"start": v(-3.03, 0.25) * mm, "end": v(-3.04, 0.27) * mm});
            skLineSegment(sketch, "E2014", {"start": v(-3.04, 0.27) * mm, "end": v(-3.04, 0.28) * mm});
            skLineSegment(sketch, "E2015", {"start": v(-3.04, 0.28) * mm, "end": v(-3.05, 0.3) * mm});
            skLineSegment(sketch, "E2016", {"start": v(-3.05, 0.3) * mm, "end": v(-3.05, 0.3) * mm});
            skLineSegment(sketch, "E2017", {"start": v(-3.05, 0.3) * mm, "end": v(-3.05, 0.32) * mm});
            skLineSegment(sketch, "E2018", {"start": v(-3.05, 0.32) * mm, "end": v(-3.06, 0.34) * mm});
            skLineSegment(sketch, "E2019", {"start": v(-3.06, 0.34) * mm, "end": v(-3.06, 0.35) * mm});
            skLineSegment(sketch, "E2020", {"start": v(-3.06, 0.35) * mm, "end": v(-3.06, 0.37) * mm});
            skLineSegment(sketch, "E2021", {"start": v(-3.06, 0.37) * mm, "end": v(-3.06, 0.38) * mm});
            skLineSegment(sketch, "E2022", {"start": v(-3.06, 0.38) * mm, "end": v(-3.07, 0.4) * mm});
            skLineSegment(sketch, "E2023", {"start": v(-3.07, 0.4) * mm, "end": v(-3.07, 0.42) * mm});
            skLineSegment(sketch, "E2024", {"start": v(-3.07, 0.42) * mm, "end": v(-3.07, 0.44) * mm});
            skLineSegment(sketch, "E2025", {"start": v(-3.07, 0.44) * mm, "end": v(-3.07, 0.46) * mm});
            skLineSegment(sketch, "E2026", {"start": v(-3.07, 0.46) * mm, "end": v(-3.07, 0.48) * mm});
            skLineSegment(sketch, "E2027", {"start": v(-3.07, 0.48) * mm, "end": v(-3.08, 0.5) * mm});
            skLineSegment(sketch, "E2028", {"start": v(-3.08, 0.5) * mm, "end": v(-3.08, 0.52) * mm});
            skLineSegment(sketch, "E2029", {"start": v(-3.08, 0.52) * mm, "end": v(-3.08, 0.54) * mm});
            skLineSegment(sketch, "E2030", {"start": v(-3.08, 0.54) * mm, "end": v(-3.08, 0.56) * mm});
            skLineSegment(sketch, "E2031", {"start": v(-3.08, 0.56) * mm, "end": v(-3.08, 0.58) * mm});
            skLineSegment(sketch, "E2032", {"start": v(-3.08, 0.58) * mm, "end": v(-3.09, 0.6) * mm});
            skLineSegment(sketch, "E2033", {"start": v(-3.09, 0.6) * mm, "end": v(-3.09, 0.62) * mm});
            skLineSegment(sketch, "E2034", {"start": v(-3.09, 0.62) * mm, "end": v(-3.09, 0.64) * mm});
            skLineSegment(sketch, "E2035", {"start": v(-3.09, 0.64) * mm, "end": v(-3.1, 0.66) * mm});
            skLineSegment(sketch, "E2036", {"start": v(-3.1, 0.66) * mm, "end": v(-3.1, 0.68) * mm});
            skLineSegment(sketch, "E2037", {"start": v(-3.1, 0.68) * mm, "end": v(-3.1, 0.7) * mm});
            skLineSegment(sketch, "E2038", {"start": v(-3.1, 0.7) * mm, "end": v(-3.1, 0.71) * mm});
            skLineSegment(sketch, "E2039", {"start": v(-3.1, 0.71) * mm, "end": v(-3.1, 0.73) * mm});
            skLineSegment(sketch, "E2040", {"start": v(-3.1, 0.73) * mm, "end": v(-3.1, 0.75) * mm});
            skLineSegment(sketch, "E2041", {"start": v(-3.1, 0.75) * mm, "end": v(-3.1, 0.77) * mm});
            skLineSegment(sketch, "E2042", {"start": v(-3.1, 0.77) * mm, "end": v(-3.1, 0.8) * mm});
            skLineSegment(sketch, "E2043", {"start": v(-3.1, 0.8) * mm, "end": v(-3.1, 0.81) * mm});
            skLineSegment(sketch, "E2044", {"start": v(-3.1, 0.81) * mm, "end": v(-3.1, 0.83) * mm});
            skLineSegment(sketch, "E2045", {"start": v(-3.1, 0.83) * mm, "end": v(-3.1, 0.85) * mm});
            skLineSegment(sketch, "E2046", {"start": v(-3.1, 0.85) * mm, "end": v(-3.1, 0.87) * mm});
            skLineSegment(sketch, "E2047", {"start": v(-3.1, 0.87) * mm, "end": v(-3.1, 0.9) * mm});
            skLineSegment(sketch, "E2048", {"start": v(-3.1, 0.9) * mm, "end": v(-3.1, 0.91) * mm});
            skLineSegment(sketch, "E2049", {"start": v(-3.1, 0.91) * mm, "end": v(-3.1, 0.93) * mm});
            skLineSegment(sketch, "E2050", {"start": v(-3.1, 0.93) * mm, "end": v(-3.1, 0.95) * mm});
            skLineSegment(sketch, "E2051", {"start": v(-3.1, 0.95) * mm, "end": v(-3.1, 0.97) * mm});
            skLineSegment(sketch, "E2052", {"start": v(-3.1, 0.97) * mm, "end": v(-3.1, 0.99) * mm});
            skLineSegment(sketch, "E2053", {"start": v(-3.1, 0.99) * mm, "end": v(-3.1, 1) * mm});
            skLineSegment(sketch, "E2054", {"start": v(-3.1, 1) * mm, "end": v(-3.1, 1.03) * mm});
            skLineSegment(sketch, "E2055", {"start": v(-3.1, 1.03) * mm, "end": v(-3.1, 1.05) * mm});
            skLineSegment(sketch, "E2056", {"start": v(-3.1, 1.05) * mm, "end": v(-3.1, 1.07) * mm});
            skLineSegment(sketch, "E2057", {"start": v(-3.1, 1.07) * mm, "end": v(-3.1, 1.1) * mm});
            skLineSegment(sketch, "E2058", {"start": v(-3.1, 1.1) * mm, "end": v(-3.09, 1.11) * mm});
            skLineSegment(sketch, "E2059", {"start": v(-3.09, 1.11) * mm, "end": v(-3.09, 1.13) * mm});
            skLineSegment(sketch, "E2060", {"start": v(-3.09, 1.13) * mm, "end": v(-3.08, 1.15) * mm});
            skLineSegment(sketch, "E2061", {"start": v(-3.08, 1.15) * mm, "end": v(-3.08, 1.17) * mm});
            skLineSegment(sketch, "E2062", {"start": v(-3.08, 1.17) * mm, "end": v(-3.07, 1.2) * mm});
            skLineSegment(sketch, "E2063", {"start": v(-3.07, 1.2) * mm, "end": v(-3.07, 1.21) * mm});
            skLineSegment(sketch, "E2064", {"start": v(-3.07, 1.21) * mm, "end": v(-3.07, 1.23) * mm});
            skLineSegment(sketch, "E2065", {"start": v(-3.07, 1.23) * mm, "end": v(-3.06, 1.25) * mm});
            skLineSegment(sketch, "E2066", {"start": v(-3.06, 1.25) * mm, "end": v(-3.06, 1.27) * mm});
            skLineSegment(sketch, "E2067", {"start": v(-3.06, 1.27) * mm, "end": v(-3.05, 1.29) * mm});
            skLineSegment(sketch, "E2068", {"start": v(-3.05, 1.29) * mm, "end": v(-3.05, 1.3) * mm});
            skLineSegment(sketch, "E2069", {"start": v(-3.05, 1.3) * mm, "end": v(-3.04, 1.32) * mm});
            skLineSegment(sketch, "E2070", {"start": v(-3.04, 1.32) * mm, "end": v(-3.04, 1.34) * mm});
            skLineSegment(sketch, "E2071", {"start": v(-3.04, 1.34) * mm, "end": v(-3.03, 1.35) * mm});
            skLineSegment(sketch, "E2072", {"start": v(-3.03, 1.35) * mm, "end": v(-3.03, 1.37) * mm});
            skLineSegment(sketch, "E2073", {"start": v(-3.03, 1.37) * mm, "end": v(-3.02, 1.39) * mm});
            skLineSegment(sketch, "E2074", {"start": v(-3.02, 1.39) * mm, "end": v(-3.02, 1.4) * mm});
            skLineSegment(sketch, "E2075", {"start": v(-3.02, 1.4) * mm, "end": v(-3.01, 1.42) * mm});
            skLineSegment(sketch, "E2076", {"start": v(-3.01, 1.42) * mm, "end": v(-3, 1.43) * mm});
            skLineSegment(sketch, "E2077", {"start": v(-3, 1.43) * mm, "end": v(-3, 1.45) * mm});
            skLineSegment(sketch, "E2078", {"start": v(-3, 1.45) * mm, "end": v(-3, 1.46) * mm});
            skLineSegment(sketch, "E2079", {"start": v(-3, 1.46) * mm, "end": v(-2.99, 1.48) * mm});
            skLineSegment(sketch, "E2080", {"start": v(-2.99, 1.48) * mm, "end": v(-2.98, 1.49) * mm});
            skLineSegment(sketch, "E2081", {"start": v(-2.98, 1.49) * mm, "end": v(-2.97, 1.5) * mm});
            skLineSegment(sketch, "E2082", {"start": v(-2.97, 1.5) * mm, "end": v(-2.97, 1.52) * mm});
            skLineSegment(sketch, "E2083", {"start": v(-2.97, 1.52) * mm, "end": v(-2.96, 1.53) * mm});
            skLineSegment(sketch, "E2084", {"start": v(-2.96, 1.53) * mm, "end": v(-2.95, 1.54) * mm});
            skLineSegment(sketch, "E2085", {"start": v(-2.95, 1.54) * mm, "end": v(-2.95, 1.55) * mm});
            skLineSegment(sketch, "E2086", {"start": v(-2.95, 1.55) * mm, "end": v(-2.93, 1.54) * mm});
            skLineSegment(sketch, "E2087", {"start": v(-2.93, 1.54) * mm, "end": v(-2.92, 1.53) * mm});
            skLineSegment(sketch, "E2088", {"start": v(-2.92, 1.53) * mm, "end": v(-2.9, 1.52) * mm});
            skLineSegment(sketch, "E2089", {"start": v(-2.9, 1.52) * mm, "end": v(-2.9, 1.51) * mm});
            skLineSegment(sketch, "E2090", {"start": v(-2.9, 1.51) * mm, "end": v(-2.88, 1.5) * mm});
            skLineSegment(sketch, "E2091", {"start": v(-2.88, 1.5) * mm, "end": v(-2.86, 1.49) * mm});
            skLineSegment(sketch, "E2092", {"start": v(-2.86, 1.49) * mm, "end": v(-2.85, 1.48) * mm});
            skLineSegment(sketch, "E2093", {"start": v(-2.85, 1.48) * mm, "end": v(-2.84, 1.46) * mm});
            skLineSegment(sketch, "E2094", {"start": v(-2.84, 1.46) * mm, "end": v(-2.83, 1.45) * mm});
            skLineSegment(sketch, "E2095", {"start": v(-2.83, 1.45) * mm, "end": v(-2.82, 1.43) * mm});
            skLineSegment(sketch, "E2096", {"start": v(-2.82, 1.43) * mm, "end": v(-2.8, 1.42) * mm});
            skLineSegment(sketch, "E2097", {"start": v(-2.8, 1.42) * mm, "end": v(-2.8, 1.4) * mm});
            skLineSegment(sketch, "E2098", {"start": v(-2.8, 1.4) * mm, "end": v(-2.78, 1.39) * mm});
            skLineSegment(sketch, "E2099", {"start": v(-2.78, 1.39) * mm, "end": v(-2.77, 1.37) * mm});
            skLineSegment(sketch, "E2100", {"start": v(-2.77, 1.37) * mm, "end": v(-2.76, 1.36) * mm});
            skLineSegment(sketch, "E2101", {"start": v(-2.76, 1.36) * mm, "end": v(-2.75, 1.34) * mm});
            skLineSegment(sketch, "E2102", {"start": v(-2.75, 1.34) * mm, "end": v(-2.74, 1.32) * mm});
            skLineSegment(sketch, "E2103", {"start": v(-2.74, 1.32) * mm, "end": v(-2.73, 1.3) * mm});
            skLineSegment(sketch, "E2104", {"start": v(-2.73, 1.3) * mm, "end": v(-2.72, 1.29) * mm});
            skLineSegment(sketch, "E2105", {"start": v(-2.72, 1.29) * mm, "end": v(-2.71, 1.27) * mm});
            skLineSegment(sketch, "E2106", {"start": v(-2.71, 1.27) * mm, "end": v(-2.7, 1.25) * mm});
            skLineSegment(sketch, "E2107", {"start": v(-2.7, 1.25) * mm, "end": v(-2.7, 1.23) * mm});
            skLineSegment(sketch, "E2108", {"start": v(-2.7, 1.23) * mm, "end": v(-2.7, 1.2) * mm});
            skLineSegment(sketch, "E2109", {"start": v(-2.7, 1.2) * mm, "end": v(-2.68, 1.19) * mm});
            skLineSegment(sketch, "E2110", {"start": v(-2.68, 1.19) * mm, "end": v(-2.68, 1.17) * mm});
            skLineSegment(sketch, "E2111", {"start": v(-2.68, 1.17) * mm, "end": v(-2.67, 1.15) * mm});
            skLineSegment(sketch, "E2112", {"start": v(-2.67, 1.15) * mm, "end": v(-2.66, 1.12) * mm});
            skLineSegment(sketch, "E2113", {"start": v(-2.66, 1.12) * mm, "end": v(-2.66, 1.1) * mm});
            skLineSegment(sketch, "E2114", {"start": v(-2.66, 1.1) * mm, "end": v(-2.65, 1.08) * mm});
            skLineSegment(sketch, "E2115", {"start": v(-2.65, 1.08) * mm, "end": v(-2.64, 1.06) * mm});
            skLineSegment(sketch, "E2116", {"start": v(-2.64, 1.06) * mm, "end": v(-2.64, 1.03) * mm});
            skLineSegment(sketch, "E2117", {"start": v(-2.64, 1.03) * mm, "end": v(-2.63, 1) * mm});
            skLineSegment(sketch, "E2118", {"start": v(-2.63, 1) * mm, "end": v(-2.09, 1) * mm});
            skLineSegment(sketch, "E2119", {"start": v(-2.09, 1) * mm, "end": v(-1.7, 1.09) * mm});
            skLineSegment(sketch, "E2120", {"start": v(-1.7, 1.09) * mm, "end": v(-1.7, 1.44) * mm});
            skLineSegment(sketch, "E2121", {"start": v(-1.7, 1.44) * mm, "end": v(-1.73, 1.44) * mm});
            skLineSegment(sketch, "E2122", {"start": v(-1.73, 1.44) * mm, "end": v(-1.75, 1.43) * mm});
            skLineSegment(sketch, "E2123", {"start": v(-1.75, 1.43) * mm, "end": v(-1.78, 1.43) * mm});
            skLineSegment(sketch, "E2124", {"start": v(-1.78, 1.43) * mm, "end": v(-1.81, 1.43) * mm});
            skLineSegment(sketch, "E2125", {"start": v(-1.81, 1.43) * mm, "end": v(-1.84, 1.43) * mm});
            skLineSegment(sketch, "E2126", {"start": v(-1.84, 1.43) * mm, "end": v(-1.87, 1.43) * mm});
            skLineSegment(sketch, "E2127", {"start": v(-1.87, 1.43) * mm, "end": v(-1.9, 1.43) * mm});
            skLineSegment(sketch, "E2128", {"start": v(-1.9, 1.43) * mm, "end": v(-1.92, 1.43) * mm});
            skLineSegment(sketch, "E2129", {"start": v(-1.92, 1.43) * mm, "end": v(-1.95, 1.43) * mm});
            skLineSegment(sketch, "E2130", {"start": v(-1.95, 1.43) * mm, "end": v(-1.98, 1.42) * mm});
            skLineSegment(sketch, "E2131", {"start": v(-1.98, 1.42) * mm, "end": v(-2, 1.42) * mm});
            skLineSegment(sketch, "E2132", {"start": v(-2, 1.42) * mm, "end": v(-2.03, 1.42) * mm});
            skLineSegment(sketch, "E2133", {"start": v(-2.03, 1.42) * mm, "end": v(-2.06, 1.43) * mm});
            skLineSegment(sketch, "E2134", {"start": v(-2.06, 1.43) * mm, "end": v(-2.08, 1.43) * mm});
            skLineSegment(sketch, "E2135", {"start": v(-2.08, 1.43) * mm, "end": v(-2.1, 1.43) * mm});
            skLineSegment(sketch, "E2136", {"start": v(-2.1, 1.43) * mm, "end": v(-2.14, 1.43) * mm});
            skLineSegment(sketch, "E2137", {"start": v(-2.14, 1.43) * mm, "end": v(-2.16, 1.43) * mm});
            skLineSegment(sketch, "E2138", {"start": v(-2.16, 1.43) * mm, "end": v(-2.19, 1.43) * mm});
            skLineSegment(sketch, "E2139", {"start": v(-2.19, 1.43) * mm, "end": v(-2.21, 1.43) * mm});
            skLineSegment(sketch, "E2140", {"start": v(-2.21, 1.43) * mm, "end": v(-2.24, 1.43) * mm});
            skLineSegment(sketch, "E2141", {"start": v(-2.24, 1.43) * mm, "end": v(-2.26, 1.44) * mm});
            skLineSegment(sketch, "E2142", {"start": v(-2.26, 1.44) * mm, "end": v(-2.29, 1.44) * mm});
            skLineSegment(sketch, "E2143", {"start": v(-2.29, 1.44) * mm, "end": v(-2.3, 1.44) * mm});
            skLineSegment(sketch, "E2144", {"start": v(-2.3, 1.44) * mm, "end": v(-2.33, 1.45) * mm});
            skLineSegment(sketch, "E2145", {"start": v(-2.33, 1.45) * mm, "end": v(-2.36, 1.45) * mm});
            skLineSegment(sketch, "E2146", {"start": v(-2.36, 1.45) * mm, "end": v(-2.38, 1.45) * mm});
            skLineSegment(sketch, "E2147", {"start": v(-2.38, 1.45) * mm, "end": v(-2.4, 1.46) * mm});
            skLineSegment(sketch, "E2148", {"start": v(-2.4, 1.46) * mm, "end": v(-2.43, 1.46) * mm});
            skLineSegment(sketch, "E2149", {"start": v(-2.43, 1.46) * mm, "end": v(-2.45, 1.46) * mm});
            skLineSegment(sketch, "E2150", {"start": v(-2.45, 1.46) * mm, "end": v(-2.47, 1.47) * mm});
            skLineSegment(sketch, "E2151", {"start": v(-2.47, 1.47) * mm, "end": v(-2.5, 1.47) * mm});
            skLineSegment(sketch, "E2152", {"start": v(-2.5, 1.47) * mm, "end": v(-2.52, 1.48) * mm});
            skLineSegment(sketch, "E2153", {"start": v(-2.52, 1.48) * mm, "end": v(-2.52, 1.48) * mm});
            skLineSegment(sketch, "E2154", {"start": v(-2.52, 1.48) * mm, "end": v(-2.53, 1.48) * mm});
            skLineSegment(sketch, "E2155", {"start": v(-2.53, 1.48) * mm, "end": v(-2.54, 1.48) * mm});
            skLineSegment(sketch, "E2156", {"start": v(-2.54, 1.48) * mm, "end": v(-2.55, 1.49) * mm});
            skLineSegment(sketch, "E2157", {"start": v(-2.55, 1.49) * mm, "end": v(-2.55, 1.49) * mm});
            skLineSegment(sketch, "E2158", {"start": v(-2.55, 1.49) * mm, "end": v(-2.56, 1.5) * mm});
            skLineSegment(sketch, "E2159", {"start": v(-2.56, 1.5) * mm, "end": v(-2.57, 1.5) * mm});
            skLineSegment(sketch, "E2160", {"start": v(-2.57, 1.5) * mm, "end": v(-2.58, 1.5) * mm});
            skLineSegment(sketch, "E2161", {"start": v(-2.58, 1.5) * mm, "end": v(-2.59, 1.5) * mm});
            skLineSegment(sketch, "E2162", {"start": v(-2.59, 1.5) * mm, "end": v(-2.6, 1.5) * mm});
            skLineSegment(sketch, "E2163", {"start": v(-2.6, 1.5) * mm, "end": v(-2.6, 1.5) * mm});
            skLineSegment(sketch, "E2164", {"start": v(-2.6, 1.5) * mm, "end": v(-2.61, 1.51) * mm});
            skLineSegment(sketch, "E2165", {"start": v(-2.61, 1.51) * mm, "end": v(-2.62, 1.51) * mm});
            skLineSegment(sketch, "E2166", {"start": v(-2.62, 1.51) * mm, "end": v(-2.63, 1.52) * mm});
            skLineSegment(sketch, "E2167", {"start": v(-2.63, 1.52) * mm, "end": v(-2.64, 1.52) * mm});
            skLineSegment(sketch, "E2168", {"start": v(-2.64, 1.52) * mm, "end": v(-2.64, 1.53) * mm});
            skLineSegment(sketch, "E2169", {"start": v(-2.64, 1.53) * mm, "end": v(-2.65, 1.53) * mm});
            skLineSegment(sketch, "E2170", {"start": v(-2.65, 1.53) * mm, "end": v(-2.66, 1.53) * mm});
            skLineSegment(sketch, "E2171", {"start": v(-2.66, 1.53) * mm, "end": v(-2.67, 1.54) * mm});
            skLineSegment(sketch, "E2172", {"start": v(-2.67, 1.54) * mm, "end": v(-2.68, 1.54) * mm});
            skLineSegment(sketch, "E2173", {"start": v(-2.68, 1.54) * mm, "end": v(-2.69, 1.54) * mm});
            skLineSegment(sketch, "E2174", {"start": v(-2.69, 1.54) * mm, "end": v(-2.7, 1.55) * mm});
            skLineSegment(sketch, "E2175", {"start": v(-2.7, 1.55) * mm, "end": v(-2.7, 1.55) * mm});
            skLineSegment(sketch, "E2176", {"start": v(-2.7, 1.55) * mm, "end": v(-2.71, 1.56) * mm});
            skLineSegment(sketch, "E2177", {"start": v(-2.71, 1.56) * mm, "end": v(-2.72, 1.56) * mm});
            skLineSegment(sketch, "E2178", {"start": v(-2.72, 1.56) * mm, "end": v(-2.73, 1.57) * mm});
            skLineSegment(sketch, "E2179", {"start": v(-2.73, 1.57) * mm, "end": v(-2.74, 1.57) * mm});
            skLineSegment(sketch, "E2180", {"start": v(-2.74, 1.57) * mm, "end": v(-2.75, 1.58) * mm});
            skLineSegment(sketch, "E2181", {"start": v(-2.75, 1.58) * mm, "end": v(-2.76, 1.58) * mm});
            skLineSegment(sketch, "E2182", {"start": v(-2.76, 1.58) * mm, "end": v(-2.77, 1.58) * mm});
            skLineSegment(sketch, "E2183", {"start": v(-2.77, 1.58) * mm, "end": v(-2.78, 1.59) * mm});
            skLineSegment(sketch, "E2184", {"start": v(-2.78, 1.59) * mm, "end": v(-2.79, 1.6) * mm});
            skLineSegment(sketch, "E2185", {"start": v(-2.79, 1.6) * mm, "end": v(-2.76, 1.6) * mm});
            skLineSegment(sketch, "E2186", {"start": v(-2.76, 1.6) * mm, "end": v(-2.72, 1.6) * mm});
            skLineSegment(sketch, "E2187", {"start": v(-2.72, 1.6) * mm, "end": v(-2.69, 1.6) * mm});
            skLineSegment(sketch, "E2188", {"start": v(-2.69, 1.6) * mm, "end": v(-2.65, 1.61) * mm});
            skLineSegment(sketch, "E2189", {"start": v(-2.65, 1.61) * mm, "end": v(-2.62, 1.62) * mm});
            skLineSegment(sketch, "E2190", {"start": v(-2.62, 1.62) * mm, "end": v(-2.59, 1.62) * mm});
            skLineSegment(sketch, "E2191", {"start": v(-2.59, 1.62) * mm, "end": v(-2.55, 1.63) * mm});
            skLineSegment(sketch, "E2192", {"start": v(-2.55, 1.63) * mm, "end": v(-2.52, 1.64) * mm});
            skLineSegment(sketch, "E2193", {"start": v(-2.52, 1.64) * mm, "end": v(-2.49, 1.64) * mm});
            skLineSegment(sketch, "E2194", {"start": v(-2.49, 1.64) * mm, "end": v(-2.45, 1.65) * mm});
            skLineSegment(sketch, "E2195", {"start": v(-2.45, 1.65) * mm, "end": v(-2.42, 1.65) * mm});
            skLineSegment(sketch, "E2196", {"start": v(-2.42, 1.65) * mm, "end": v(-2.39, 1.66) * mm});
            skLineSegment(sketch, "E2197", {"start": v(-2.39, 1.66) * mm, "end": v(-2.35, 1.66) * mm});
            skLineSegment(sketch, "E2198", {"start": v(-2.35, 1.66) * mm, "end": v(-2.32, 1.67) * mm});
            skLineSegment(sketch, "E2199", {"start": v(-2.32, 1.67) * mm, "end": v(-2.29, 1.68) * mm});
            skLineSegment(sketch, "E2200", {"start": v(-2.29, 1.68) * mm, "end": v(-2.25, 1.68) * mm});
            skLineSegment(sketch, "E2201", {"start": v(-2.25, 1.68) * mm, "end": v(-2.22, 1.69) * mm});
            skLineSegment(sketch, "E2202", {"start": v(-2.22, 1.69) * mm, "end": v(-2.19, 1.7) * mm});
            skLineSegment(sketch, "E2203", {"start": v(-2.19, 1.7) * mm, "end": v(-2.15, 1.7) * mm});
            skLineSegment(sketch, "E2204", {"start": v(-2.15, 1.7) * mm, "end": v(-2.12, 1.7) * mm});
            skLineSegment(sketch, "E2205", {"start": v(-2.12, 1.7) * mm, "end": v(-2.09, 1.71) * mm});
            skLineSegment(sketch, "E2206", {"start": v(-2.09, 1.71) * mm, "end": v(-2.06, 1.72) * mm});
            skLineSegment(sketch, "E2207", {"start": v(-2.06, 1.72) * mm, "end": v(-2.02, 1.73) * mm});
            skLineSegment(sketch, "E2208", {"start": v(-2.02, 1.73) * mm, "end": v(-2, 1.73) * mm});
            skLineSegment(sketch, "E2209", {"start": v(-2, 1.73) * mm, "end": v(-1.96, 1.74) * mm});
            skLineSegment(sketch, "E2210", {"start": v(-1.96, 1.74) * mm, "end": v(-1.93, 1.75) * mm});
            skLineSegment(sketch, "E2211", {"start": v(-1.93, 1.75) * mm, "end": v(-1.9, 1.75) * mm});
            skLineSegment(sketch, "E2212", {"start": v(-1.9, 1.75) * mm, "end": v(-1.86, 1.76) * mm});
            skLineSegment(sketch, "E2213", {"start": v(-1.86, 1.76) * mm, "end": v(-1.83, 1.77) * mm});
            skLineSegment(sketch, "E2214", {"start": v(-1.83, 1.77) * mm, "end": v(-1.8, 1.77) * mm});
            skLineSegment(sketch, "E2215", {"start": v(-1.8, 1.77) * mm, "end": v(-1.77, 1.78) * mm});
            skLineSegment(sketch, "E2216", {"start": v(-1.77, 1.78) * mm, "end": v(-1.74, 1.79) * mm});
            skLineSegment(sketch, "E2217", {"start": v(-1.74, 1.79) * mm, "end": v(-1.74, 2.1) * mm});
            skLineSegment(sketch, "E2218", {"start": v(-1.74, 2.1) * mm, "end": v(-1.75, 2.1) * mm});
            skLineSegment(sketch, "E2219", {"start": v(-1.75, 2.1) * mm, "end": v(-1.77, 2.1) * mm});
            skLineSegment(sketch, "E2220", {"start": v(-1.77, 2.1) * mm, "end": v(-1.78, 2.1) * mm});
            skLineSegment(sketch, "E2221", {"start": v(-1.78, 2.1) * mm, "end": v(-1.8, 2.09) * mm});
            skLineSegment(sketch, "E2222", {"start": v(-1.8, 2.09) * mm, "end": v(-1.82, 2.09) * mm});
            skLineSegment(sketch, "E2223", {"start": v(-1.82, 2.09) * mm, "end": v(-1.83, 2.08) * mm});
            skLineSegment(sketch, "E2224", {"start": v(-1.83, 2.08) * mm, "end": v(-1.85, 2.08) * mm});
            skLineSegment(sketch, "E2225", {"start": v(-1.85, 2.08) * mm, "end": v(-1.87, 2.07) * mm});
            skLineSegment(sketch, "E2226", {"start": v(-1.87, 2.07) * mm, "end": v(-1.9, 2.07) * mm});
            skLineSegment(sketch, "E2227", {"start": v(-1.9, 2.07) * mm, "end": v(-1.91, 2.06) * mm});
            skLineSegment(sketch, "E2228", {"start": v(-1.91, 2.06) * mm, "end": v(-1.93, 2.06) * mm});
            skLineSegment(sketch, "E2229", {"start": v(-1.93, 2.06) * mm, "end": v(-1.96, 2.05) * mm});
            skLineSegment(sketch, "E2230", {"start": v(-1.96, 2.05) * mm, "end": v(-1.98, 2.04) * mm});
            skLineSegment(sketch, "E2231", {"start": v(-1.98, 2.04) * mm, "end": v(-2, 2.04) * mm});
            skLineSegment(sketch, "E2232", {"start": v(-2, 2.04) * mm, "end": v(-2.02, 2.03) * mm});
            skLineSegment(sketch, "E2233", {"start": v(-2.02, 2.03) * mm, "end": v(-2.05, 2.02) * mm});
            skLineSegment(sketch, "E2234", {"start": v(-2.05, 2.02) * mm, "end": v(-2.07, 2.02) * mm});
            skLineSegment(sketch, "E2235", {"start": v(-2.07, 2.02) * mm, "end": v(-2.1, 2) * mm});
            skLineSegment(sketch, "E2236", {"start": v(-2.1, 2) * mm, "end": v(-2.12, 2) * mm});
            skLineSegment(sketch, "E2237", {"start": v(-2.12, 2) * mm, "end": v(-2.15, 2) * mm});
            skLineSegment(sketch, "E2238", {"start": v(-2.15, 2) * mm, "end": v(-2.18, 1.98) * mm});
            skLineSegment(sketch, "E2239", {"start": v(-2.18, 1.98) * mm, "end": v(-2.2, 1.97) * mm});
            skLineSegment(sketch, "E2240", {"start": v(-2.2, 1.97) * mm, "end": v(-2.23, 1.96) * mm});
            skLineSegment(sketch, "E2241", {"start": v(-2.23, 1.96) * mm, "end": v(-2.26, 1.96) * mm});
            skLineSegment(sketch, "E2242", {"start": v(-2.26, 1.96) * mm, "end": v(-2.3, 1.95) * mm});
            skLineSegment(sketch, "E2243", {"start": v(-2.3, 1.95) * mm, "end": v(-2.32, 1.94) * mm});
            skLineSegment(sketch, "E2244", {"start": v(-2.32, 1.94) * mm, "end": v(-2.35, 1.92) * mm});
            skLineSegment(sketch, "E2245", {"start": v(-2.35, 1.92) * mm, "end": v(-2.38, 1.91) * mm});
            skLineSegment(sketch, "E2246", {"start": v(-2.38, 1.91) * mm, "end": v(-2.42, 1.9) * mm});
            skLineSegment(sketch, "E2247", {"start": v(-2.42, 1.9) * mm, "end": v(-2.45, 1.9) * mm});
            skLineSegment(sketch, "E2248", {"start": v(-2.45, 1.9) * mm, "end": v(-2.48, 1.88) * mm});
            skLineSegment(sketch, "E2249", {"start": v(-2.48, 1.88) * mm, "end": v(-2.52, 1.87) * mm});
            skLineSegment(sketch, "E2250", {"start": v(-2.52, 1.87) * mm, "end": v(-2.5, 1.88) * mm});
            skLineSegment(sketch, "E2251", {"start": v(-2.5, 1.88) * mm, "end": v(-2.5, 1.9) * mm});
            skLineSegment(sketch, "E2252", {"start": v(-2.5, 1.9) * mm, "end": v(-2.49, 1.9) * mm});
            skLineSegment(sketch, "E2253", {"start": v(-2.49, 1.9) * mm, "end": v(-2.48, 1.91) * mm});
            skLineSegment(sketch, "E2254", {"start": v(-2.48, 1.91) * mm, "end": v(-2.46, 1.93) * mm});
            skLineSegment(sketch, "E2255", {"start": v(-2.46, 1.93) * mm, "end": v(-2.45, 1.94) * mm});
            skLineSegment(sketch, "E2256", {"start": v(-2.45, 1.94) * mm, "end": v(-2.44, 1.95) * mm});
            skLineSegment(sketch, "E2257", {"start": v(-2.44, 1.95) * mm, "end": v(-2.43, 1.96) * mm});
            skLineSegment(sketch, "E2258", {"start": v(-2.43, 1.96) * mm, "end": v(-2.42, 1.97) * mm});
            skLineSegment(sketch, "E2259", {"start": v(-2.42, 1.97) * mm, "end": v(-2.4, 1.98) * mm});
            skLineSegment(sketch, "E2260", {"start": v(-2.4, 1.98) * mm, "end": v(-2.4, 2) * mm});
            skLineSegment(sketch, "E2261", {"start": v(-2.4, 2) * mm, "end": v(-2.38, 2) * mm});
            skLineSegment(sketch, "E2262", {"start": v(-2.38, 2) * mm, "end": v(-2.37, 2.01) * mm});
            skLineSegment(sketch, "E2263", {"start": v(-2.37, 2.01) * mm, "end": v(-2.36, 2.02) * mm});
            skLineSegment(sketch, "E2264", {"start": v(-2.36, 2.02) * mm, "end": v(-2.34, 2.03) * mm});
            skLineSegment(sketch, "E2265", {"start": v(-2.34, 2.03) * mm, "end": v(-2.33, 2.04) * mm});
            skLineSegment(sketch, "E2266", {"start": v(-2.33, 2.04) * mm, "end": v(-2.32, 2.05) * mm});
            skLineSegment(sketch, "E2267", {"start": v(-2.32, 2.05) * mm, "end": v(-2.3, 2.06) * mm});
            skLineSegment(sketch, "E2268", {"start": v(-2.3, 2.06) * mm, "end": v(-2.29, 2.07) * mm});
            skLineSegment(sketch, "E2269", {"start": v(-2.29, 2.07) * mm, "end": v(-2.28, 2.08) * mm});
            skLineSegment(sketch, "E2270", {"start": v(-2.28, 2.08) * mm, "end": v(-2.26, 2.1) * mm});
            skLineSegment(sketch, "E2271", {"start": v(-2.26, 2.1) * mm, "end": v(-2.25, 2.1) * mm});
            skLineSegment(sketch, "E2272", {"start": v(-2.25, 2.1) * mm, "end": v(-2.23, 2.1) * mm});
            skLineSegment(sketch, "E2273", {"start": v(-2.23, 2.1) * mm, "end": v(-2.22, 2.12) * mm});
            skLineSegment(sketch, "E2274", {"start": v(-2.22, 2.12) * mm, "end": v(-2.2, 2.12) * mm});
            skLineSegment(sketch, "E2275", {"start": v(-2.2, 2.12) * mm, "end": v(-2.19, 2.13) * mm});
            skLineSegment(sketch, "E2276", {"start": v(-2.19, 2.13) * mm, "end": v(-2.17, 2.14) * mm});
            skLineSegment(sketch, "E2277", {"start": v(-2.17, 2.14) * mm, "end": v(-2.15, 2.15) * mm});
            skLineSegment(sketch, "E2278", {"start": v(-2.15, 2.15) * mm, "end": v(-2.14, 2.16) * mm});
            skLineSegment(sketch, "E2279", {"start": v(-2.14, 2.16) * mm, "end": v(-2.12, 2.17) * mm});
            skLineSegment(sketch, "E2280", {"start": v(-2.12, 2.17) * mm, "end": v(-2.1, 2.17) * mm});
            skLineSegment(sketch, "E2281", {"start": v(-2.1, 2.17) * mm, "end": v(-2.09, 2.18) * mm});
            skLineSegment(sketch, "E2282", {"start": v(-2.09, 2.18) * mm, "end": v(-2.12, 2.19) * mm});
            skLineSegment(sketch, "E2283", {"start": v(-2.12, 2.19) * mm, "end": v(-2.16, 2.2) * mm});
            skLineSegment(sketch, "E2284", {"start": v(-2.16, 2.2) * mm, "end": v(-2.2, 2.2) * mm});
            skLineSegment(sketch, "E2285", {"start": v(-2.2, 2.2) * mm, "end": v(-2.23, 2.22) * mm});
            skLineSegment(sketch, "E2286", {"start": v(-2.23, 2.22) * mm, "end": v(-2.27, 2.23) * mm});
            skLineSegment(sketch, "E2287", {"start": v(-2.27, 2.23) * mm, "end": v(-2.3, 2.24) * mm});
            skLineSegment(sketch, "E2288", {"start": v(-2.3, 2.24) * mm, "end": v(-2.33, 2.25) * mm});
            skLineSegment(sketch, "E2289", {"start": v(-2.33, 2.25) * mm, "end": v(-2.36, 2.26) * mm});
            skLineSegment(sketch, "E2290", {"start": v(-2.36, 2.26) * mm, "end": v(-2.4, 2.27) * mm});
            skLineSegment(sketch, "E2291", {"start": v(-2.4, 2.27) * mm, "end": v(-2.42, 2.29) * mm});
            skLineSegment(sketch, "E2292", {"start": v(-2.42, 2.29) * mm, "end": v(-2.45, 2.3) * mm});
            skLineSegment(sketch, "E2293", {"start": v(-2.45, 2.3) * mm, "end": v(-2.47, 2.3) * mm});
            skLineSegment(sketch, "E2294", {"start": v(-2.47, 2.3) * mm, "end": v(-2.5, 2.32) * mm});
            skLineSegment(sketch, "E2295", {"start": v(-2.5, 2.32) * mm, "end": v(-2.52, 2.33) * mm});
            skLineSegment(sketch, "E2296", {"start": v(-2.52, 2.33) * mm, "end": v(-2.54, 2.34) * mm});
            skLineSegment(sketch, "E2297", {"start": v(-2.54, 2.34) * mm, "end": v(-2.57, 2.36) * mm});
            skLineSegment(sketch, "E2298", {"start": v(-2.57, 2.36) * mm, "end": v(-2.59, 2.37) * mm});
            skLineSegment(sketch, "E2299", {"start": v(-2.59, 2.37) * mm, "end": v(-2.6, 2.38) * mm});
            skLineSegment(sketch, "E2300", {"start": v(-2.6, 2.38) * mm, "end": v(-2.62, 2.4) * mm});
            skLineSegment(sketch, "E2301", {"start": v(-2.62, 2.4) * mm, "end": v(-2.64, 2.4) * mm});
            skLineSegment(sketch, "E2302", {"start": v(-2.64, 2.4) * mm, "end": v(-2.65, 2.42) * mm});
            skLineSegment(sketch, "E2303", {"start": v(-2.65, 2.42) * mm, "end": v(-2.67, 2.43) * mm});
            skLineSegment(sketch, "E2304", {"start": v(-2.67, 2.43) * mm, "end": v(-2.68, 2.45) * mm});
            skLineSegment(sketch, "E2305", {"start": v(-2.68, 2.45) * mm, "end": v(-2.7, 2.46) * mm});
            skLineSegment(sketch, "E2306", {"start": v(-2.7, 2.46) * mm, "end": v(-2.7, 2.47) * mm});
            skLineSegment(sketch, "E2307", {"start": v(-2.7, 2.47) * mm, "end": v(-2.72, 2.49) * mm});
            skLineSegment(sketch, "E2308", {"start": v(-2.72, 2.49) * mm, "end": v(-2.72, 2.5) * mm});
            skLineSegment(sketch, "E2309", {"start": v(-2.72, 2.5) * mm, "end": v(-2.73, 2.51) * mm});
            skLineSegment(sketch, "E2310", {"start": v(-2.73, 2.51) * mm, "end": v(-2.74, 2.53) * mm});
            skLineSegment(sketch, "E2311", {"start": v(-2.74, 2.53) * mm, "end": v(-2.74, 2.54) * mm});
            skLineSegment(sketch, "E2312", {"start": v(-2.74, 2.54) * mm, "end": v(-2.75, 2.56) * mm});
            skLineSegment(sketch, "E2313", {"start": v(-2.75, 2.56) * mm, "end": v(-2.75, 2.57) * mm});
            skLineSegment(sketch, "E2314", {"start": v(-2.75, 2.57) * mm, "end": v(-2.71, 2.57) * mm});
            skLineSegment(sketch, "E2315", {"start": v(-2.71, 2.57) * mm, "end": v(-2.67, 2.58) * mm});
            skLineSegment(sketch, "E2316", {"start": v(-2.67, 2.58) * mm, "end": v(-2.64, 2.58) * mm});
            skLineSegment(sketch, "E2317", {"start": v(-2.64, 2.58) * mm, "end": v(-2.6, 2.58) * mm});
            skLineSegment(sketch, "E2318", {"start": v(-2.6, 2.58) * mm, "end": v(-2.56, 2.58) * mm});
            skLineSegment(sketch, "E2319", {"start": v(-2.56, 2.58) * mm, "end": v(-2.52, 2.59) * mm});
            skLineSegment(sketch, "E2320", {"start": v(-2.52, 2.59) * mm, "end": v(-2.49, 2.6) * mm});
            skLineSegment(sketch, "E2321", {"start": v(-2.49, 2.6) * mm, "end": v(-2.45, 2.6) * mm});
            skLineSegment(sketch, "E2322", {"start": v(-2.45, 2.6) * mm, "end": v(-2.41, 2.6) * mm});
            skLineSegment(sketch, "E2323", {"start": v(-2.41, 2.6) * mm, "end": v(-2.38, 2.6) * mm});
            skLineSegment(sketch, "E2324", {"start": v(-2.38, 2.6) * mm, "end": v(-2.34, 2.6) * mm});
            skLineSegment(sketch, "E2325", {"start": v(-2.34, 2.6) * mm, "end": v(-2.3, 2.61) * mm});
            skLineSegment(sketch, "E2326", {"start": v(-2.3, 2.61) * mm, "end": v(-2.28, 2.62) * mm});
            skLineSegment(sketch, "E2327", {"start": v(-2.28, 2.62) * mm, "end": v(-2.24, 2.62) * mm});
            skLineSegment(sketch, "E2328", {"start": v(-2.24, 2.62) * mm, "end": v(-2.2, 2.62) * mm});
            skLineSegment(sketch, "E2329", {"start": v(-2.2, 2.62) * mm, "end": v(-2.17, 2.63) * mm});
            skLineSegment(sketch, "E2330", {"start": v(-2.17, 2.63) * mm, "end": v(-2.14, 2.63) * mm});
            skLineSegment(sketch, "E2331", {"start": v(-2.14, 2.63) * mm, "end": v(-2.1, 2.64) * mm});
            skLineSegment(sketch, "E2332", {"start": v(-2.1, 2.64) * mm, "end": v(-2.08, 2.64) * mm});
            skLineSegment(sketch, "E2333", {"start": v(-2.08, 2.64) * mm, "end": v(-2.05, 2.65) * mm});
            skLineSegment(sketch, "E2334", {"start": v(-2.05, 2.65) * mm, "end": v(-2.01, 2.66) * mm});
            skLineSegment(sketch, "E2335", {"start": v(-2.01, 2.66) * mm, "end": v(-1.98, 2.66) * mm});
            skLineSegment(sketch, "E2336", {"start": v(-1.98, 2.66) * mm, "end": v(-1.95, 2.67) * mm});
            skLineSegment(sketch, "E2337", {"start": v(-1.95, 2.67) * mm, "end": v(-1.92, 2.67) * mm});
            skLineSegment(sketch, "E2338", {"start": v(-1.92, 2.67) * mm, "end": v(-1.9, 2.68) * mm});
            skLineSegment(sketch, "E2339", {"start": v(-1.9, 2.68) * mm, "end": v(-1.86, 2.69) * mm});
            skLineSegment(sketch, "E2340", {"start": v(-1.86, 2.69) * mm, "end": v(-1.84, 2.7) * mm});
            skLineSegment(sketch, "E2341", {"start": v(-1.84, 2.7) * mm, "end": v(-1.8, 2.7) * mm});
            skLineSegment(sketch, "E2342", {"start": v(-1.8, 2.7) * mm, "end": v(-1.78, 2.7) * mm});
            skLineSegment(sketch, "E2343", {"start": v(-1.78, 2.7) * mm, "end": v(-1.75, 2.71) * mm});
            skLineSegment(sketch, "E2344", {"start": v(-1.75, 2.71) * mm, "end": v(-1.72, 2.72) * mm});
            skLineSegment(sketch, "E2345", {"start": v(-1.72, 2.72) * mm, "end": v(-1.7, 2.73) * mm});
            skLineSegment(sketch, "E2346", {"start": v(-1.7, 2.73) * mm, "end": v(-1.7, 2.74) * mm});
            skLineSegment(sketch, "E2347", {"start": v(-1.7, 2.74) * mm, "end": v(-1.7, 2.75) * mm});
            skLineSegment(sketch, "E2348", {"start": v(-1.7, 2.75) * mm, "end": v(-1.7, 2.76) * mm});
            skLineSegment(sketch, "E2349", {"start": v(-1.7, 2.76) * mm, "end": v(-1.7, 2.77) * mm});
            skLineSegment(sketch, "E2350", {"start": v(-1.7, 2.77) * mm, "end": v(-1.7, 2.79) * mm});
            skLineSegment(sketch, "E2351", {"start": v(-1.7, 2.79) * mm, "end": v(-1.7, 2.8) * mm});
            skLineSegment(sketch, "E2352", {"start": v(-1.7, 2.8) * mm, "end": v(-1.7, 2.8) * mm});
            skLineSegment(sketch, "E2353", {"start": v(-1.7, 2.8) * mm, "end": v(-1.7, 2.82) * mm});
            skLineSegment(sketch, "E2354", {"start": v(-1.7, 2.82) * mm, "end": v(-1.7, 2.83) * mm});
            skLineSegment(sketch, "E2355", {"start": v(-1.7, 2.83) * mm, "end": v(-1.7, 2.84) * mm});
            skLineSegment(sketch, "E2356", {"start": v(-1.7, 2.84) * mm, "end": v(-1.7, 2.85) * mm});
            skLineSegment(sketch, "E2357", {"start": v(-1.7, 2.85) * mm, "end": v(-1.7, 2.86) * mm});
            skLineSegment(sketch, "E2358", {"start": v(-1.7, 2.86) * mm, "end": v(-1.7, 2.87) * mm});
            skLineSegment(sketch, "E2359", {"start": v(-1.7, 2.87) * mm, "end": v(-1.7, 2.88) * mm});
            skLineSegment(sketch, "E2360", {"start": v(-1.7, 2.88) * mm, "end": v(-1.7, 2.9) * mm});
            skLineSegment(sketch, "E2361", {"start": v(-1.7, 2.9) * mm, "end": v(-1.7, 2.9) * mm});
            skLineSegment(sketch, "E2362", {"start": v(-1.7, 2.9) * mm, "end": v(-1.7, 2.91) * mm});
            skLineSegment(sketch, "E2363", {"start": v(-1.7, 2.91) * mm, "end": v(-1.7, 2.92) * mm});
            skLineSegment(sketch, "E2364", {"start": v(-1.7, 2.92) * mm, "end": v(-1.7, 2.93) * mm});
            skLineSegment(sketch, "E2365", {"start": v(-1.7, 2.93) * mm, "end": v(-1.71, 2.94) * mm});
            skLineSegment(sketch, "E2366", {"start": v(-1.71, 2.94) * mm, "end": v(-1.71, 2.95) * mm});
            skLineSegment(sketch, "E2367", {"start": v(-1.71, 2.95) * mm, "end": v(-1.71, 2.96) * mm});
            skLineSegment(sketch, "E2368", {"start": v(-1.71, 2.96) * mm, "end": v(-1.72, 2.97) * mm});
            skLineSegment(sketch, "E2369", {"start": v(-1.72, 2.97) * mm, "end": v(-1.72, 2.98) * mm});
            skLineSegment(sketch, "E2370", {"start": v(-1.72, 2.98) * mm, "end": v(-1.72, 2.98) * mm});
            skLineSegment(sketch, "E2371", {"start": v(-1.72, 2.98) * mm, "end": v(-1.72, 3) * mm});
            skLineSegment(sketch, "E2372", {"start": v(-1.72, 3) * mm, "end": v(-1.72, 3) * mm});
            skLineSegment(sketch, "E2373", {"start": v(-1.72, 3) * mm, "end": v(-1.73, 3) * mm});
            skLineSegment(sketch, "E2374", {"start": v(-1.73, 3) * mm, "end": v(-1.73, 3.02) * mm});
            skLineSegment(sketch, "E2375", {"start": v(-1.73, 3.02) * mm, "end": v(-1.73, 3.02) * mm});
            skLineSegment(sketch, "E2376", {"start": v(-1.73, 3.02) * mm, "end": v(-1.73, 3.03) * mm});
            skLineSegment(sketch, "E2377", {"start": v(-1.73, 3.03) * mm, "end": v(-1.74, 3.04) * mm});
            skLineSegment(sketch, "E2378", {"start": v(-1.74, 3.04) * mm, "end": v(-1.74, 3.06) * mm});
            skLineSegment(sketch, "E2379", {"start": v(-1.74, 3.06) * mm, "end": v(-1.74, 3.07) * mm});
            skLineSegment(sketch, "E2380", {"start": v(-1.74, 3.07) * mm, "end": v(-1.74, 3.09) * mm});
            skLineSegment(sketch, "E2381", {"start": v(-1.74, 3.09) * mm, "end": v(-1.75, 3.1) * mm});
            skLineSegment(sketch, "E2382", {"start": v(-1.75, 3.1) * mm, "end": v(-1.75, 3.12) * mm});
            skLineSegment(sketch, "E2383", {"start": v(-1.75, 3.12) * mm, "end": v(-1.76, 3.14) * mm});
            skLineSegment(sketch, "E2384", {"start": v(-1.76, 3.14) * mm, "end": v(-1.76, 3.16) * mm});
            skLineSegment(sketch, "E2385", {"start": v(-1.76, 3.16) * mm, "end": v(-1.77, 3.17) * mm});
            skLineSegment(sketch, "E2386", {"start": v(-1.77, 3.17) * mm, "end": v(-1.77, 3.19) * mm});
            skLineSegment(sketch, "E2387", {"start": v(-1.77, 3.19) * mm, "end": v(-1.78, 3.2) * mm});
            skLineSegment(sketch, "E2388", {"start": v(-1.78, 3.2) * mm, "end": v(-1.79, 3.22) * mm});
            skLineSegment(sketch, "E2389", {"start": v(-1.79, 3.22) * mm, "end": v(-1.8, 3.23) * mm});
            skLineSegment(sketch, "E2390", {"start": v(-1.8, 3.23) * mm, "end": v(-1.8, 3.25) * mm});
            skLineSegment(sketch, "E2391", {"start": v(-1.8, 3.25) * mm, "end": v(-1.8, 3.26) * mm});
            skLineSegment(sketch, "E2392", {"start": v(-1.8, 3.26) * mm, "end": v(-1.81, 3.28) * mm});
            skLineSegment(sketch, "E2393", {"start": v(-1.81, 3.28) * mm, "end": v(-1.82, 3.3) * mm});
            skLineSegment(sketch, "E2394", {"start": v(-1.82, 3.3) * mm, "end": v(-1.83, 3.3) * mm});
            skLineSegment(sketch, "E2395", {"start": v(-1.83, 3.3) * mm, "end": v(-1.84, 3.32) * mm});
            skLineSegment(sketch, "E2396", {"start": v(-1.84, 3.32) * mm, "end": v(-1.85, 3.34) * mm});
            skLineSegment(sketch, "E2397", {"start": v(-1.85, 3.34) * mm, "end": v(-1.86, 3.35) * mm});
            skLineSegment(sketch, "E2398", {"start": v(-1.86, 3.35) * mm, "end": v(-1.87, 3.36) * mm});
            skLineSegment(sketch, "E2399", {"start": v(-1.87, 3.36) * mm, "end": v(-1.88, 3.38) * mm});
            skLineSegment(sketch, "E2400", {"start": v(-1.88, 3.38) * mm, "end": v(-1.9, 3.4) * mm});
            skLineSegment(sketch, "E2401", {"start": v(-1.9, 3.4) * mm, "end": v(-1.9, 3.4) * mm});
            skLineSegment(sketch, "E2402", {"start": v(-1.9, 3.4) * mm, "end": v(-1.92, 3.42) * mm});
            skLineSegment(sketch, "E2403", {"start": v(-1.92, 3.42) * mm, "end": v(-1.93, 3.43) * mm});
            skLineSegment(sketch, "E2404", {"start": v(-1.93, 3.43) * mm, "end": v(-1.94, 3.45) * mm});
            skLineSegment(sketch, "E2405", {"start": v(-1.94, 3.45) * mm, "end": v(-1.95, 3.46) * mm});
            skLineSegment(sketch, "E2406", {"start": v(-1.95, 3.46) * mm, "end": v(-1.97, 3.47) * mm});
            skLineSegment(sketch, "E2407", {"start": v(-1.97, 3.47) * mm, "end": v(-1.98, 3.48) * mm});
            skLineSegment(sketch, "E2408", {"start": v(-1.98, 3.48) * mm, "end": v(-2, 3.5) * mm});
            skLineSegment(sketch, "E2409", {"start": v(-2, 3.5) * mm, "end": v(-2, 3.5) * mm});
            skLineSegment(sketch, "E2410", {"start": v(-2, 3.5) * mm, "end": v(-2.04, 3.51) * mm});
            skLineSegment(sketch, "E2411", {"start": v(-2.04, 3.51) * mm, "end": v(-2.08, 3.51) * mm});
            skLineSegment(sketch, "E2412", {"start": v(-2.08, 3.51) * mm, "end": v(-2.11, 3.52) * mm});
            skLineSegment(sketch, "E2413", {"start": v(-2.11, 3.52) * mm, "end": v(-2.15, 3.52) * mm});
            skLineSegment(sketch, "E2414", {"start": v(-2.15, 3.52) * mm, "end": v(-2.18, 3.52) * mm});
            skLineSegment(sketch, "E2415", {"start": v(-2.18, 3.52) * mm, "end": v(-2.21, 3.53) * mm});
            skLineSegment(sketch, "E2416", {"start": v(-2.21, 3.53) * mm, "end": v(-2.25, 3.53) * mm});
            skLineSegment(sketch, "E2417", {"start": v(-2.25, 3.53) * mm, "end": v(-2.28, 3.53) * mm});
            skLineSegment(sketch, "E2418", {"start": v(-2.28, 3.53) * mm, "end": v(-2.3, 3.54) * mm});
            skLineSegment(sketch, "E2419", {"start": v(-2.3, 3.54) * mm, "end": v(-2.34, 3.54) * mm});
            skLineSegment(sketch, "E2420", {"start": v(-2.34, 3.54) * mm, "end": v(-2.37, 3.55) * mm});
            skLineSegment(sketch, "E2421", {"start": v(-2.37, 3.55) * mm, "end": v(-2.4, 3.55) * mm});
            skLineSegment(sketch, "E2422", {"start": v(-2.4, 3.55) * mm, "end": v(-2.42, 3.56) * mm});
            skLineSegment(sketch, "E2423", {"start": v(-2.42, 3.56) * mm, "end": v(-2.45, 3.56) * mm});
            skLineSegment(sketch, "E2424", {"start": v(-2.45, 3.56) * mm, "end": v(-2.47, 3.57) * mm});
            skLineSegment(sketch, "E2425", {"start": v(-2.47, 3.57) * mm, "end": v(-2.5, 3.58) * mm});
            skLineSegment(sketch, "E2426", {"start": v(-2.5, 3.58) * mm, "end": v(-2.52, 3.58) * mm});
            skLineSegment(sketch, "E2427", {"start": v(-2.52, 3.58) * mm, "end": v(-2.54, 3.59) * mm});
            skLineSegment(sketch, "E2428", {"start": v(-2.54, 3.59) * mm, "end": v(-2.57, 3.6) * mm});
            skLineSegment(sketch, "E2429", {"start": v(-2.57, 3.6) * mm, "end": v(-2.59, 3.6) * mm});
            skLineSegment(sketch, "E2430", {"start": v(-2.59, 3.6) * mm, "end": v(-2.6, 3.6) * mm});
            skLineSegment(sketch, "E2431", {"start": v(-2.6, 3.6) * mm, "end": v(-2.63, 3.62) * mm});
            skLineSegment(sketch, "E2432", {"start": v(-2.63, 3.62) * mm, "end": v(-2.65, 3.62) * mm});
            skLineSegment(sketch, "E2433", {"start": v(-2.65, 3.62) * mm, "end": v(-2.67, 3.63) * mm});
            skLineSegment(sketch, "E2434", {"start": v(-2.67, 3.63) * mm, "end": v(-2.69, 3.64) * mm});
            skLineSegment(sketch, "E2435", {"start": v(-2.69, 3.64) * mm, "end": v(-2.7, 3.65) * mm});
            skLineSegment(sketch, "E2436", {"start": v(-2.7, 3.65) * mm, "end": v(-2.72, 3.66) * mm});
            skLineSegment(sketch, "E2437", {"start": v(-2.72, 3.66) * mm, "end": v(-2.74, 3.67) * mm});
            skLineSegment(sketch, "E2438", {"start": v(-2.74, 3.67) * mm, "end": v(-2.75, 3.68) * mm});
            skLineSegment(sketch, "E2439", {"start": v(-2.75, 3.68) * mm, "end": v(-2.76, 3.68) * mm});
            skLineSegment(sketch, "E2440", {"start": v(-2.76, 3.68) * mm, "end": v(-2.78, 3.7) * mm});
            skLineSegment(sketch, "E2441", {"start": v(-2.78, 3.7) * mm, "end": v(-2.79, 3.7) * mm});
            skLineSegment(sketch, "E2442", {"start": v(-2.79, 3.7) * mm, "end": v(-2.8, 3.66) * mm});
            skLineSegment(sketch, "E2443", {"start": v(-2.8, 3.66) * mm, "end": v(-2.8, 3.62) * mm});
            skLineSegment(sketch, "E2444", {"start": v(-2.8, 3.62) * mm, "end": v(-2.8, 3.57) * mm});
            skLineSegment(sketch, "E2445", {"start": v(-2.8, 3.57) * mm, "end": v(-2.81, 3.53) * mm});
            skLineSegment(sketch, "E2446", {"start": v(-2.81, 3.53) * mm, "end": v(-2.82, 3.49) * mm});
            skLineSegment(sketch, "E2447", {"start": v(-2.82, 3.49) * mm, "end": v(-2.83, 3.45) * mm});
            skLineSegment(sketch, "E2448", {"start": v(-2.83, 3.45) * mm, "end": v(-2.84, 3.4) * mm});
            skLineSegment(sketch, "E2449", {"start": v(-2.84, 3.4) * mm, "end": v(-2.84, 3.37) * mm});
            skLineSegment(sketch, "E2450", {"start": v(-2.84, 3.37) * mm, "end": v(-2.85, 3.33) * mm});
            skLineSegment(sketch, "E2451", {"start": v(-2.85, 3.33) * mm, "end": v(-2.86, 3.29) * mm});
            skLineSegment(sketch, "E2452", {"start": v(-2.86, 3.29) * mm, "end": v(-2.87, 3.25) * mm});
            skLineSegment(sketch, "E2453", {"start": v(-2.87, 3.25) * mm, "end": v(-2.88, 3.2) * mm});
            skLineSegment(sketch, "E2454", {"start": v(-2.88, 3.2) * mm, "end": v(-2.9, 3.17) * mm});
            skLineSegment(sketch, "E2455", {"start": v(-2.9, 3.17) * mm, "end": v(-2.9, 3.13) * mm});
            skLineSegment(sketch, "E2456", {"start": v(-2.9, 3.13) * mm, "end": v(-2.92, 3.1) * mm});
            skLineSegment(sketch, "E2457", {"start": v(-2.92, 3.1) * mm, "end": v(-2.93, 3.06) * mm});
            skLineSegment(sketch, "E2458", {"start": v(-2.93, 3.06) * mm, "end": v(-2.94, 3.02) * mm});
            skLineSegment(sketch, "E2459", {"start": v(-2.94, 3.02) * mm, "end": v(-2.95, 2.99) * mm});
            skLineSegment(sketch, "E2460", {"start": v(-2.95, 2.99) * mm, "end": v(-2.97, 2.95) * mm});
            skLineSegment(sketch, "E2461", {"start": v(-2.97, 2.95) * mm, "end": v(-2.98, 2.92) * mm});
            skLineSegment(sketch, "E2462", {"start": v(-2.98, 2.92) * mm, "end": v(-3, 2.88) * mm});
            skLineSegment(sketch, "E2463", {"start": v(-3, 2.88) * mm, "end": v(-3, 2.85) * mm});
            skLineSegment(sketch, "E2464", {"start": v(-3, 2.85) * mm, "end": v(-3.02, 2.81) * mm});
            skLineSegment(sketch, "E2465", {"start": v(-3.02, 2.81) * mm, "end": v(-3.04, 2.78) * mm});
            skLineSegment(sketch, "E2466", {"start": v(-3.04, 2.78) * mm, "end": v(-3.06, 2.75) * mm});
            skLineSegment(sketch, "E2467", {"start": v(-3.06, 2.75) * mm, "end": v(-3.07, 2.72) * mm});
            skLineSegment(sketch, "E2468", {"start": v(-3.07, 2.72) * mm, "end": v(-3.09, 2.68) * mm});
            skLineSegment(sketch, "E2469", {"start": v(-3.09, 2.68) * mm, "end": v(-3.1, 2.65) * mm});
            skLineSegment(sketch, "E2470", {"start": v(-3.1, 2.65) * mm, "end": v(-3.12, 2.62) * mm});
            skLineSegment(sketch, "E2471", {"start": v(-3.12, 2.62) * mm, "end": v(-3.14, 2.6) * mm});
            skLineSegment(sketch, "E2472", {"start": v(-3.14, 2.6) * mm, "end": v(-3.16, 2.56) * mm});
            skLineSegment(sketch, "E2473", {"start": v(-3.16, 2.56) * mm, "end": v(-3.18, 2.53) * mm});
            skLineSegment(sketch, "E2474", {"start": v(-3.18, 2.53) * mm, "end": v(-3.2, 2.5) * mm});
            skLineSegment(sketch, "E2475", {"start": v(-3.2, 2.5) * mm, "end": v(-3.2, 2.49) * mm});
            skLineSegment(sketch, "E2476", {"start": v(-3.2, 2.49) * mm, "end": v(-3.22, 2.47) * mm});
            skLineSegment(sketch, "E2477", {"start": v(-3.22, 2.47) * mm, "end": v(-3.23, 2.45) * mm});
            skLineSegment(sketch, "E2478", {"start": v(-3.23, 2.45) * mm, "end": v(-3.24, 2.44) * mm});
            skLineSegment(sketch, "E2479", {"start": v(-3.24, 2.44) * mm, "end": v(-3.25, 2.42) * mm});
            skLineSegment(sketch, "E2480", {"start": v(-3.25, 2.42) * mm, "end": v(-3.26, 2.4) * mm});
            skLineSegment(sketch, "E2481", {"start": v(-3.26, 2.4) * mm, "end": v(-3.27, 2.4) * mm});
            skLineSegment(sketch, "E2482", {"start": v(-3.27, 2.4) * mm, "end": v(-3.28, 2.39) * mm});
            skLineSegment(sketch, "E2483", {"start": v(-3.28, 2.39) * mm, "end": v(-3.3, 2.38) * mm});
            skLineSegment(sketch, "E2484", {"start": v(-3.3, 2.38) * mm, "end": v(-3.3, 2.37) * mm});
            skLineSegment(sketch, "E2485", {"start": v(-3.3, 2.37) * mm, "end": v(-3.32, 2.36) * mm});
            skLineSegment(sketch, "E2486", {"start": v(-3.32, 2.36) * mm, "end": v(-3.33, 2.36) * mm});
            skLineSegment(sketch, "E2487", {"start": v(-3.33, 2.36) * mm, "end": v(-3.34, 2.35) * mm});
            skLineSegment(sketch, "E2488", {"start": v(-3.34, 2.35) * mm, "end": v(-3.35, 2.35) * mm});
            skLineSegment(sketch, "E2489", {"start": v(-3.35, 2.35) * mm, "end": v(-3.36, 2.35) * mm});
            skLineSegment(sketch, "E2490", {"start": v(-3.36, 2.35) * mm, "end": v(-3.37, 2.35) * mm});
            skLineSegment(sketch, "E2491", {"start": v(-3.37, 2.35) * mm, "end": v(-3.38, 2.35) * mm});
            skLineSegment(sketch, "E2492", {"start": v(-3.38, 2.35) * mm, "end": v(-3.39, 2.35) * mm});
            skLineSegment(sketch, "E2493", {"start": v(-3.39, 2.35) * mm, "end": v(-3.4, 2.35) * mm});
            skLineSegment(sketch, "E2494", {"start": v(-3.4, 2.35) * mm, "end": v(-3.4, 2.36) * mm});
            skLineSegment(sketch, "E2495", {"start": v(-3.4, 2.36) * mm, "end": v(-3.41, 2.36) * mm});
            skLineSegment(sketch, "E2496", {"start": v(-3.41, 2.36) * mm, "end": v(-3.42, 2.37) * mm});
            skLineSegment(sketch, "E2497", {"start": v(-3.42, 2.37) * mm, "end": v(-3.43, 2.38) * mm});
            skLineSegment(sketch, "E2498", {"start": v(-3.43, 2.38) * mm, "end": v(-3.44, 2.39) * mm});
            skLineSegment(sketch, "E2499", {"start": v(-3.44, 2.39) * mm, "end": v(-3.45, 2.4) * mm});
            skLineSegment(sketch, "E2500", {"start": v(-3.45, 2.4) * mm, "end": v(-3.45, 2.41) * mm});
            skLineSegment(sketch, "E2501", {"start": v(-3.45, 2.41) * mm, "end": v(-3.46, 2.42) * mm});
            skLineSegment(sketch, "E2502", {"start": v(-3.46, 2.42) * mm, "end": v(-3.47, 2.44) * mm});
            skLineSegment(sketch, "E2503", {"start": v(-3.47, 2.44) * mm, "end": v(-3.48, 2.46) * mm});
            skLineSegment(sketch, "E2504", {"start": v(-3.48, 2.46) * mm, "end": v(-3.49, 2.47) * mm});
            skLineSegment(sketch, "E2505", {"start": v(-3.49, 2.47) * mm, "end": v(-3.5, 2.5) * mm});
            skLineSegment(sketch, "E2506", {"start": v(-3.5, 2.5) * mm, "end": v(-3.5, 2.51) * mm});
            skLineSegment(sketch, "E2507", {"start": v(-3.5, 2.51) * mm, "end": v(-3.5, 2.53) * mm});
            skLineSegment(sketch, "E2508", {"start": v(-3.5, 2.53) * mm, "end": v(-3.52, 2.55) * mm});
            skLineSegment(sketch, "E2509", {"start": v(-3.52, 2.55) * mm, "end": v(-3.52, 2.57) * mm});
            skLineSegment(sketch, "E2510", {"start": v(-3.52, 2.57) * mm, "end": v(-3.53, 2.6) * mm});
            skLineSegment(sketch, "E2511", {"start": v(-3.53, 2.6) * mm, "end": v(-3.54, 2.61) * mm});
            skLineSegment(sketch, "E2512", {"start": v(-3.54, 2.61) * mm, "end": v(-3.55, 2.63) * mm});
            skLineSegment(sketch, "E2513", {"start": v(-3.55, 2.63) * mm, "end": v(-3.55, 2.65) * mm});
            skLineSegment(sketch, "E2514", {"start": v(-3.55, 2.65) * mm, "end": v(-3.56, 2.67) * mm});
            skLineSegment(sketch, "E2515", {"start": v(-3.56, 2.67) * mm, "end": v(-3.57, 2.7) * mm});
            skLineSegment(sketch, "E2516", {"start": v(-3.57, 2.7) * mm, "end": v(-3.58, 2.71) * mm});
            skLineSegment(sketch, "E2517", {"start": v(-3.58, 2.71) * mm, "end": v(-3.59, 2.73) * mm});
            skLineSegment(sketch, "E2518", {"start": v(-3.59, 2.73) * mm, "end": v(-3.6, 2.75) * mm});
            skLineSegment(sketch, "E2519", {"start": v(-3.6, 2.75) * mm, "end": v(-3.6, 2.77) * mm});
            skLineSegment(sketch, "E2520", {"start": v(-3.6, 2.77) * mm, "end": v(-3.61, 2.8) * mm});
            skLineSegment(sketch, "E2521", {"start": v(-3.61, 2.8) * mm, "end": v(-3.62, 2.81) * mm});
            skLineSegment(sketch, "E2522", {"start": v(-3.62, 2.81) * mm, "end": v(-3.63, 2.84) * mm});
            skLineSegment(sketch, "E2523", {"start": v(-3.63, 2.84) * mm, "end": v(-3.64, 2.86) * mm});
            skLineSegment(sketch, "E2524", {"start": v(-3.64, 2.86) * mm, "end": v(-3.65, 2.88) * mm});
            skLineSegment(sketch, "E2525", {"start": v(-3.65, 2.88) * mm, "end": v(-3.66, 2.9) * mm});
            skLineSegment(sketch, "E2526", {"start": v(-3.66, 2.9) * mm, "end": v(-3.66, 2.92) * mm});
            skLineSegment(sketch, "E2527", {"start": v(-3.66, 2.92) * mm, "end": v(-3.67, 2.94) * mm});
            skLineSegment(sketch, "E2528", {"start": v(-3.67, 2.94) * mm, "end": v(-3.68, 2.96) * mm});
            skLineSegment(sketch, "E2529", {"start": v(-3.68, 2.96) * mm, "end": v(-3.7, 2.98) * mm});
            skLineSegment(sketch, "E2530", {"start": v(-3.7, 2.98) * mm, "end": v(-3.7, 3) * mm});
            skLineSegment(sketch, "E2531", {"start": v(-3.7, 3) * mm, "end": v(-3.7, 3.03) * mm});
            skLineSegment(sketch, "E2532", {"start": v(-3.7, 3.03) * mm, "end": v(-3.72, 3.05) * mm});
            skLineSegment(sketch, "E2533", {"start": v(-3.72, 3.05) * mm, "end": v(-3.73, 3.07) * mm});
            skLineSegment(sketch, "E2534", {"start": v(-3.73, 3.07) * mm, "end": v(-3.74, 3.1) * mm});
            skLineSegment(sketch, "E2535", {"start": v(-3.74, 3.1) * mm, "end": v(-3.75, 3.11) * mm});
            skLineSegment(sketch, "E2536", {"start": v(-3.75, 3.11) * mm, "end": v(-3.76, 3.13) * mm});
            skLineSegment(sketch, "E2537", {"start": v(-3.76, 3.13) * mm, "end": v(-3.77, 3.16) * mm});
            skLineSegment(sketch, "E2538", {"start": v(-3.77, 3.16) * mm, "end": v(-3.72, 3.21) * mm});
            skLineSegment(sketch, "E2539", {"start": v(-3.72, 3.21) * mm, "end": v(-3.67, 3.27) * mm});
            skLineSegment(sketch, "E2540", {"start": v(-3.67, 3.27) * mm, "end": v(-3.62, 3.32) * mm});
            skLineSegment(sketch, "E2541", {"start": v(-3.62, 3.32) * mm, "end": v(-3.58, 3.37) * mm});
            skLineSegment(sketch, "E2542", {"start": v(-3.58, 3.37) * mm, "end": v(-3.53, 3.42) * mm});
            skLineSegment(sketch, "E2543", {"start": v(-3.53, 3.42) * mm, "end": v(-3.5, 3.47) * mm});
            skLineSegment(sketch, "E2544", {"start": v(-3.5, 3.47) * mm, "end": v(-3.45, 3.52) * mm});
            skLineSegment(sketch, "E2545", {"start": v(-3.45, 3.52) * mm, "end": v(-3.42, 3.56) * mm});
            skLineSegment(sketch, "E2546", {"start": v(-3.42, 3.56) * mm, "end": v(-3.38, 3.6) * mm});
            skLineSegment(sketch, "E2547", {"start": v(-3.38, 3.6) * mm, "end": v(-3.35, 3.65) * mm});
            skLineSegment(sketch, "E2548", {"start": v(-3.35, 3.65) * mm, "end": v(-3.31, 3.7) * mm});
            skLineSegment(sketch, "E2549", {"start": v(-3.31, 3.7) * mm, "end": v(-3.28, 3.73) * mm});
            skLineSegment(sketch, "E2550", {"start": v(-3.28, 3.73) * mm, "end": v(-3.26, 3.77) * mm});
            skLineSegment(sketch, "E2551", {"start": v(-3.26, 3.77) * mm, "end": v(-3.23, 3.8) * mm});
            skLineSegment(sketch, "E2552", {"start": v(-3.23, 3.8) * mm, "end": v(-3.2, 3.84) * mm});
            skLineSegment(sketch, "E2553", {"start": v(-3.2, 3.84) * mm, "end": v(-3.18, 3.88) * mm});
            skLineSegment(sketch, "E2554", {"start": v(-3.18, 3.88) * mm, "end": v(-3.16, 3.91) * mm});
            skLineSegment(sketch, "E2555", {"start": v(-3.16, 3.91) * mm, "end": v(-3.14, 3.94) * mm});
            skLineSegment(sketch, "E2556", {"start": v(-3.14, 3.94) * mm, "end": v(-3.12, 3.98) * mm});
            skLineSegment(sketch, "E2557", {"start": v(-3.12, 3.98) * mm, "end": v(-3.1, 4) * mm});
            skLineSegment(sketch, "E2558", {"start": v(-3.1, 4) * mm, "end": v(-3.1, 4.03) * mm});
            skLineSegment(sketch, "E2559", {"start": v(-3.1, 4.03) * mm, "end": v(-3.08, 4.06) * mm});
            skLineSegment(sketch, "E2560", {"start": v(-3.08, 4.06) * mm, "end": v(-3.07, 4.08) * mm});
            skLineSegment(sketch, "E2561", {"start": v(-3.07, 4.08) * mm, "end": v(-3.06, 4.1) * mm});
            skLineSegment(sketch, "E2562", {"start": v(-3.06, 4.1) * mm, "end": v(-3.06, 4.13) * mm});
            skLineSegment(sketch, "E2563", {"start": v(-3.06, 4.13) * mm, "end": v(-3.05, 4.15) * mm});
            skLineSegment(sketch, "E2564", {"start": v(-3.05, 4.15) * mm, "end": v(-3.05, 4.17) * mm});
            skLineSegment(sketch, "E2565", {"start": v(-3.05, 4.17) * mm, "end": v(-3.05, 4.2) * mm});
            skLineSegment(sketch, "E2566", {"start": v(-3.05, 4.2) * mm, "end": v(-3.05, 4.2) * mm});
            skLineSegment(sketch, "E2567", {"start": v(-3.05, 4.2) * mm, "end": v(-3.05, 4.22) * mm});
            skLineSegment(sketch, "E2568", {"start": v(-3.05, 4.22) * mm, "end": v(-3.06, 4.24) * mm});
            skLineSegment(sketch, "E2569", {"start": v(-3.06, 4.24) * mm, "end": v(-3.06, 4.25) * mm});
            skLineSegment(sketch, "E2570", {"start": v(-3.06, 4.25) * mm, "end": v(-2.87, 4.02) * mm});
            skLineSegment(sketch, "E2571", {"start": v(-2.87, 4.02) * mm, "end": v(-2.05, 4.02) * mm});
            skLineSegment(sketch, "E2572", {"start": v(-2.05, 4.02) * mm, "end": v(-1.97, 4.03) * mm});
            skLineSegment(sketch, "E2573", {"start": v(-1.97, 4.03) * mm, "end": v(-1.9, 4.03) * mm});
            skLineSegment(sketch, "E2574", {"start": v(-1.9, 4.03) * mm, "end": v(-1.81, 4.04) * mm});
            skLineSegment(sketch, "E2575", {"start": v(-1.81, 4.04) * mm, "end": v(-1.73, 4.05) * mm});
            skLineSegment(sketch, "E2576", {"start": v(-1.73, 4.05) * mm, "end": v(-1.66, 4.06) * mm});
            skLineSegment(sketch, "E2577", {"start": v(-1.66, 4.06) * mm, "end": v(-1.58, 4.07) * mm});
            skLineSegment(sketch, "E2578", {"start": v(-1.58, 4.07) * mm, "end": v(-1.5, 4.07) * mm});
            skLineSegment(sketch, "E2579", {"start": v(-1.5, 4.07) * mm, "end": v(-1.42, 4.08) * mm});
            skLineSegment(sketch, "E2580", {"start": v(-1.42, 4.08) * mm, "end": v(-1.34, 4.09) * mm});
            skLineSegment(sketch, "E2581", {"start": v(-1.34, 4.09) * mm, "end": v(-1.26, 4.1) * mm});
            skLineSegment(sketch, "E2582", {"start": v(-1.26, 4.1) * mm, "end": v(-1.18, 4.1) * mm});
            skLineSegment(sketch, "E2583", {"start": v(-1.18, 4.1) * mm, "end": v(-1.1, 4.1) * mm});
            skLineSegment(sketch, "E2584", {"start": v(-1.1, 4.1) * mm, "end": v(-1.03, 4.11) * mm});
            skLineSegment(sketch, "E2585", {"start": v(-1.03, 4.11) * mm, "end": v(-0.95, 4.11) * mm});
            skLineSegment(sketch, "E2586", {"start": v(-0.95, 4.11) * mm, "end": v(-0.87, 4.12) * mm});
            skLineSegment(sketch, "E2587", {"start": v(-0.87, 4.12) * mm, "end": v(-0.79, 4.12) * mm});
            skLineSegment(sketch, "E2588", {"start": v(-0.79, 4.12) * mm, "end": v(-0.7, 4.13) * mm});
            skLineSegment(sketch, "E2589", {"start": v(-0.7, 4.13) * mm, "end": v(-0.63, 4.13) * mm});
            skLineSegment(sketch, "E2590", {"start": v(-0.63, 4.13) * mm, "end": v(-0.55, 4.13) * mm});
            skLineSegment(sketch, "E2591", {"start": v(-0.55, 4.13) * mm, "end": v(-0.47, 4.13) * mm});
            skLineSegment(sketch, "E2592", {"start": v(-0.47, 4.13) * mm, "end": v(-0.39, 4.14) * mm});
            skLineSegment(sketch, "E2593", {"start": v(-0.39, 4.14) * mm, "end": v(-0.31, 4.14) * mm});
            skLineSegment(sketch, "E2594", {"start": v(-0.31, 4.14) * mm, "end": v(-0.23, 4.14) * mm});
            skLineSegment(sketch, "E2595", {"start": v(-0.23, 4.14) * mm, "end": v(-0.15, 4.14) * mm});
            skLineSegment(sketch, "E2596", {"start": v(-0.15, 4.14) * mm, "end": v(-0.07, 4.14) * mm});
            skLineSegment(sketch, "E2597", {"start": v(-0.07, 4.14) * mm, "end": v(0, 4.14) * mm});
            skLineSegment(sketch, "E2598", {"start": v(0, 4.14) * mm, "end": v(0.09, 4.14) * mm});
            skLineSegment(sketch, "E2599", {"start": v(0.09, 4.14) * mm, "end": v(0.17, 4.14) * mm});
            skLineSegment(sketch, "E2600", {"start": v(0.17, 4.14) * mm, "end": v(0.25, 4.14) * mm});
            skLineSegment(sketch, "E2601", {"start": v(0.25, 4.14) * mm, "end": v(0.33, 4.14) * mm});
            skLineSegment(sketch, "E2602", {"start": v(0.33, 4.14) * mm, "end": v(0.41, 4.14) * mm});
            skLineSegment(sketch, "E2603", {"start": v(0.41, 4.14) * mm, "end": v(0.5, 4.13) * mm});
            skLineSegment(sketch, "E2604", {"start": v(-0.25, 0.93) * mm, "end": v(-0.28, 0.92) * mm});
            skLineSegment(sketch, "E2605", {"start": v(-0.28, 0.92) * mm, "end": v(-0.3, 0.91) * mm});
            skLineSegment(sketch, "E2606", {"start": v(-0.3, 0.91) * mm, "end": v(-0.32, 0.9) * mm});
            skLineSegment(sketch, "E2607", {"start": v(-0.32, 0.9) * mm, "end": v(-0.35, 0.9) * mm});
            skLineSegment(sketch, "E2608", {"start": v(-0.35, 0.9) * mm, "end": v(-0.37, 0.9) * mm});
            skLineSegment(sketch, "E2609", {"start": v(-0.37, 0.9) * mm, "end": v(-0.4, 0.89) * mm});
            skLineSegment(sketch, "E2610", {"start": v(-0.4, 0.89) * mm, "end": v(-0.42, 0.88) * mm});
            skLineSegment(sketch, "E2611", {"start": v(-0.42, 0.88) * mm, "end": v(-0.45, 0.87) * mm});
            skLineSegment(sketch, "E2612", {"start": v(-0.45, 0.87) * mm, "end": v(-0.47, 0.86) * mm});
            skLineSegment(sketch, "E2613", {"start": v(-0.47, 0.86) * mm, "end": v(-0.5, 0.86) * mm});
            skLineSegment(sketch, "E2614", {"start": v(-0.5, 0.86) * mm, "end": v(-0.52, 0.85) * mm});
            skLineSegment(sketch, "E2615", {"start": v(-0.52, 0.85) * mm, "end": v(-0.54, 0.84) * mm});
            skLineSegment(sketch, "E2616", {"start": v(-0.54, 0.84) * mm, "end": v(-0.57, 0.83) * mm});
            skLineSegment(sketch, "E2617", {"start": v(-0.57, 0.83) * mm, "end": v(-0.6, 0.83) * mm});
            skLineSegment(sketch, "E2618", {"start": v(-0.6, 0.83) * mm, "end": v(-0.62, 0.82) * mm});
            skLineSegment(sketch, "E2619", {"start": v(-0.62, 0.82) * mm, "end": v(-0.64, 0.81) * mm});
            skLineSegment(sketch, "E2620", {"start": v(-0.64, 0.81) * mm, "end": v(-0.67, 0.8) * mm});
            skLineSegment(sketch, "E2621", {"start": v(-0.67, 0.8) * mm, "end": v(-0.7, 0.8) * mm});
            skLineSegment(sketch, "E2622", {"start": v(-0.7, 0.8) * mm, "end": v(-0.71, 0.8) * mm});
            skLineSegment(sketch, "E2623", {"start": v(-0.71, 0.8) * mm, "end": v(-0.74, 0.78) * mm});
            skLineSegment(sketch, "E2624", {"start": v(-0.74, 0.78) * mm, "end": v(-0.76, 0.78) * mm});
            skLineSegment(sketch, "E2625", {"start": v(-0.76, 0.78) * mm, "end": v(-0.79, 0.77) * mm});
            skLineSegment(sketch, "E2626", {"start": v(-0.79, 0.77) * mm, "end": v(-0.81, 0.76) * mm});
            skLineSegment(sketch, "E2627", {"start": v(-0.81, 0.76) * mm, "end": v(-0.84, 0.75) * mm});
            skLineSegment(sketch, "E2628", {"start": v(-0.84, 0.75) * mm, "end": v(-0.86, 0.75) * mm});
            skLineSegment(sketch, "E2629", {"start": v(-0.86, 0.75) * mm, "end": v(-0.89, 0.74) * mm});
            skLineSegment(sketch, "E2630", {"start": v(-0.89, 0.74) * mm, "end": v(-0.9, 0.73) * mm});
            skLineSegment(sketch, "E2631", {"start": v(-0.9, 0.73) * mm, "end": v(-0.93, 0.72) * mm});
            skLineSegment(sketch, "E2632", {"start": v(-0.93, 0.72) * mm, "end": v(-0.96, 0.72) * mm});
            skLineSegment(sketch, "E2633", {"start": v(-0.96, 0.72) * mm, "end": v(-0.98, 0.71) * mm});
            skLineSegment(sketch, "E2634", {"start": v(-0.98, 0.71) * mm, "end": v(-1, 0.7) * mm});
            skLineSegment(sketch, "E2635", {"start": v(-1, 0.7) * mm, "end": v(-1.03, 0.7) * mm});
            skLineSegment(sketch, "E2636", {"start": v(-1.03, 0.7) * mm, "end": v(-1.03, 0.42) * mm});
            skLineSegment(sketch, "E2637", {"start": v(-1.03, 0.42) * mm, "end": v(-1.01, 0.42) * mm});
            skLineSegment(sketch, "E2638", {"start": v(-1.01, 0.42) * mm, "end": v(-1, 0.42) * mm});
            skLineSegment(sketch, "E2639", {"start": v(-1, 0.42) * mm, "end": v(-0.98, 0.42) * mm});
            skLineSegment(sketch, "E2640", {"start": v(-0.98, 0.42) * mm, "end": v(-0.96, 0.42) * mm});
            skLineSegment(sketch, "E2641", {"start": v(-0.96, 0.42) * mm, "end": v(-0.94, 0.42) * mm});
            skLineSegment(sketch, "E2642", {"start": v(-0.94, 0.42) * mm, "end": v(-0.93, 0.42) * mm});
            skLineSegment(sketch, "E2643", {"start": v(-0.93, 0.42) * mm, "end": v(-0.9, 0.42) * mm});
            skLineSegment(sketch, "E2644", {"start": v(-0.9, 0.42) * mm, "end": v(-0.89, 0.42) * mm});
            skLineSegment(sketch, "E2645", {"start": v(-0.89, 0.42) * mm, "end": v(-0.87, 0.43) * mm});
            skLineSegment(sketch, "E2646", {"start": v(-0.87, 0.43) * mm, "end": v(-0.85, 0.43) * mm});
            skLineSegment(sketch, "E2647", {"start": v(-0.85, 0.43) * mm, "end": v(-0.83, 0.43) * mm});
            skLineSegment(sketch, "E2648", {"start": v(-0.83, 0.43) * mm, "end": v(-0.81, 0.43) * mm});
            skLineSegment(sketch, "E2649", {"start": v(-0.81, 0.43) * mm, "end": v(-0.8, 0.43) * mm});
            skLineSegment(sketch, "E2650", {"start": v(-0.8, 0.43) * mm, "end": v(-0.77, 0.43) * mm});
            skLineSegment(sketch, "E2651", {"start": v(-0.77, 0.43) * mm, "end": v(-0.75, 0.43) * mm});
            skLineSegment(sketch, "E2652", {"start": v(-0.75, 0.43) * mm, "end": v(-0.73, 0.43) * mm});
            skLineSegment(sketch, "E2653", {"start": v(-0.73, 0.43) * mm, "end": v(-0.7, 0.43) * mm});
            skLineSegment(sketch, "E2654", {"start": v(-0.7, 0.43) * mm, "end": v(-0.69, 0.43) * mm});
            skLineSegment(sketch, "E2655", {"start": v(-0.69, 0.43) * mm, "end": v(-0.67, 0.44) * mm});
            skLineSegment(sketch, "E2656", {"start": v(-0.67, 0.44) * mm, "end": v(-0.64, 0.44) * mm});
            skLineSegment(sketch, "E2657", {"start": v(-0.64, 0.44) * mm, "end": v(-0.62, 0.44) * mm});
            skLineSegment(sketch, "E2658", {"start": v(-0.62, 0.44) * mm, "end": v(-0.6, 0.44) * mm});
            skLineSegment(sketch, "E2659", {"start": v(-0.6, 0.44) * mm, "end": v(-0.58, 0.44) * mm});
            skLineSegment(sketch, "E2660", {"start": v(-0.58, 0.44) * mm, "end": v(-0.56, 0.44) * mm});
            skLineSegment(sketch, "E2661", {"start": v(-0.56, 0.44) * mm, "end": v(-0.53, 0.45) * mm});
            skLineSegment(sketch, "E2662", {"start": v(-0.53, 0.45) * mm, "end": v(-0.51, 0.45) * mm});
            skLineSegment(sketch, "E2663", {"start": v(-0.51, 0.45) * mm, "end": v(-0.49, 0.45) * mm});
            skLineSegment(sketch, "E2664", {"start": v(-0.49, 0.45) * mm, "end": v(-0.46, 0.45) * mm});
            skLineSegment(sketch, "E2665", {"start": v(-0.46, 0.45) * mm, "end": v(-0.44, 0.45) * mm});
            skLineSegment(sketch, "E2666", {"start": v(-0.44, 0.45) * mm, "end": v(-0.42, 0.46) * mm});
            skLineSegment(sketch, "E2667", {"start": v(-0.42, 0.46) * mm, "end": v(-0.4, 0.46) * mm});
            skLineSegment(sketch, "E2668", {"start": v(-0.4, 0.46) * mm, "end": v(-0.37, 0.46) * mm});
            skLineSegment(sketch, "E2669", {"start": v(-0.37, 0.46) * mm, "end": v(-0.37, 0.48) * mm});
            skLineSegment(sketch, "E2670", {"start": v(-0.37, 0.48) * mm, "end": v(-0.36, 0.5) * mm});
            skLineSegment(sketch, "E2671", {"start": v(-0.36, 0.5) * mm, "end": v(-0.36, 0.51) * mm});
            skLineSegment(sketch, "E2672", {"start": v(-0.36, 0.51) * mm, "end": v(-0.36, 0.53) * mm});
            skLineSegment(sketch, "E2673", {"start": v(-0.36, 0.53) * mm, "end": v(-0.35, 0.54) * mm});
            skLineSegment(sketch, "E2674", {"start": v(-0.35, 0.54) * mm, "end": v(-0.35, 0.56) * mm});
            skLineSegment(sketch, "E2675", {"start": v(-0.35, 0.56) * mm, "end": v(-0.35, 0.58) * mm});
            skLineSegment(sketch, "E2676", {"start": v(-0.35, 0.58) * mm, "end": v(-0.35, 0.6) * mm});
            skLineSegment(sketch, "E2677", {"start": v(-0.35, 0.6) * mm, "end": v(-0.34, 0.6) * mm});
            skLineSegment(sketch, "E2678", {"start": v(-0.34, 0.6) * mm, "end": v(-0.34, 0.62) * mm});
            skLineSegment(sketch, "E2679", {"start": v(-0.34, 0.62) * mm, "end": v(-0.34, 0.64) * mm});
            skLineSegment(sketch, "E2680", {"start": v(-0.34, 0.64) * mm, "end": v(-0.33, 0.66) * mm});
            skLineSegment(sketch, "E2681", {"start": v(-0.33, 0.66) * mm, "end": v(-0.33, 0.67) * mm});
            skLineSegment(sketch, "E2682", {"start": v(-0.33, 0.67) * mm, "end": v(-0.33, 0.69) * mm});
            skLineSegment(sketch, "E2683", {"start": v(-0.33, 0.69) * mm, "end": v(-0.32, 0.7) * mm});
            skLineSegment(sketch, "E2684", {"start": v(-0.32, 0.7) * mm, "end": v(-0.32, 0.71) * mm});
            skLineSegment(sketch, "E2685", {"start": v(-0.32, 0.71) * mm, "end": v(-0.32, 0.73) * mm});
            skLineSegment(sketch, "E2686", {"start": v(-0.32, 0.73) * mm, "end": v(-0.31, 0.74) * mm});
            skLineSegment(sketch, "E2687", {"start": v(-0.31, 0.74) * mm, "end": v(-0.3, 0.76) * mm});
            skLineSegment(sketch, "E2688", {"start": v(-0.3, 0.76) * mm, "end": v(-0.3, 0.77) * mm});
            skLineSegment(sketch, "E2689", {"start": v(-0.3, 0.77) * mm, "end": v(-0.3, 0.79) * mm});
            skLineSegment(sketch, "E2690", {"start": v(-0.3, 0.79) * mm, "end": v(-0.3, 0.8) * mm});
            skLineSegment(sketch, "E2691", {"start": v(-0.3, 0.8) * mm, "end": v(-0.3, 0.81) * mm});
            skLineSegment(sketch, "E2692", {"start": v(-0.3, 0.81) * mm, "end": v(-0.29, 0.83) * mm});
            skLineSegment(sketch, "E2693", {"start": v(-0.29, 0.83) * mm, "end": v(-0.28, 0.84) * mm});
            skLineSegment(sketch, "E2694", {"start": v(-0.28, 0.84) * mm, "end": v(-0.28, 0.85) * mm});
            skLineSegment(sketch, "E2695", {"start": v(-0.28, 0.85) * mm, "end": v(-0.27, 0.87) * mm});
            skLineSegment(sketch, "E2696", {"start": v(-0.27, 0.87) * mm, "end": v(-0.27, 0.88) * mm});
            skLineSegment(sketch, "E2697", {"start": v(-0.27, 0.88) * mm, "end": v(-0.27, 0.9) * mm});
            skLineSegment(sketch, "E2698", {"start": v(-0.27, 0.9) * mm, "end": v(-0.26, 0.9) * mm});
            skLineSegment(sketch, "E2699", {"start": v(-0.26, 0.9) * mm, "end": v(-0.26, 0.92) * mm});
            skLineSegment(sketch, "E2700", {"start": v(-0.26, 0.92) * mm, "end": v(-0.25, 0.93) * mm});
            skLineSegment(sketch, "E2701", {"start": v(-5.6, 4.37) * mm, "end": v(-5.57, 4.35) * mm});
            skLineSegment(sketch, "E2702", {"start": v(-5.57, 4.35) * mm, "end": v(-5.54, 4.32) * mm});
            skLineSegment(sketch, "E2703", {"start": v(-5.54, 4.32) * mm, "end": v(-5.5, 4.3) * mm});
            skLineSegment(sketch, "E2704", {"start": v(-5.5, 4.3) * mm, "end": v(-5.48, 4.28) * mm});
            skLineSegment(sketch, "E2705", {"start": v(-5.48, 4.28) * mm, "end": v(-5.45, 4.26) * mm});
            skLineSegment(sketch, "E2706", {"start": v(-5.45, 4.26) * mm, "end": v(-5.42, 4.24) * mm});
            skLineSegment(sketch, "E2707", {"start": v(-5.42, 4.24) * mm, "end": v(-5.39, 4.23) * mm});
            skLineSegment(sketch, "E2708", {"start": v(-5.39, 4.23) * mm, "end": v(-5.36, 4.2) * mm});
            skLineSegment(sketch, "E2709", {"start": v(-5.36, 4.2) * mm, "end": v(-5.33, 4.19) * mm});
            skLineSegment(sketch, "E2710", {"start": v(-5.33, 4.19) * mm, "end": v(-5.3, 4.17) * mm});
            skLineSegment(sketch, "E2711", {"start": v(-5.3, 4.17) * mm, "end": v(-5.27, 4.15) * mm});
            skLineSegment(sketch, "E2712", {"start": v(-5.27, 4.15) * mm, "end": v(-5.24, 4.14) * mm});
            skLineSegment(sketch, "E2713", {"start": v(-5.24, 4.14) * mm, "end": v(-5.22, 4.12) * mm});
            skLineSegment(sketch, "E2714", {"start": v(-5.22, 4.12) * mm, "end": v(-5.19, 4.1) * mm});
            skLineSegment(sketch, "E2715", {"start": v(-5.19, 4.1) * mm, "end": v(-5.16, 4.09) * mm});
            skLineSegment(sketch, "E2716", {"start": v(-5.16, 4.09) * mm, "end": v(-5.13, 4.07) * mm});
            skLineSegment(sketch, "E2717", {"start": v(-5.13, 4.07) * mm, "end": v(-5.1, 4.06) * mm});
            skLineSegment(sketch, "E2718", {"start": v(-5.1, 4.06) * mm, "end": v(-5.08, 4.05) * mm});
            skLineSegment(sketch, "E2719", {"start": v(-5.08, 4.05) * mm, "end": v(-5.05, 4.03) * mm});
            skLineSegment(sketch, "E2720", {"start": v(-5.05, 4.03) * mm, "end": v(-5.03, 4.02) * mm});
            skLineSegment(sketch, "E2721", {"start": v(-5.03, 4.02) * mm, "end": v(-5, 4) * mm});
            skLineSegment(sketch, "E2722", {"start": v(-5, 4) * mm, "end": v(-4.98, 4) * mm});
            skLineSegment(sketch, "E2723", {"start": v(-4.98, 4) * mm, "end": v(-4.95, 3.98) * mm});
            skLineSegment(sketch, "E2724", {"start": v(-4.95, 3.98) * mm, "end": v(-4.93, 3.97) * mm});
            skLineSegment(sketch, "E2725", {"start": v(-4.93, 3.97) * mm, "end": v(-4.9, 3.96) * mm});
            skLineSegment(sketch, "E2726", {"start": v(-4.9, 3.96) * mm, "end": v(-4.88, 3.95) * mm});
            skLineSegment(sketch, "E2727", {"start": v(-4.88, 3.95) * mm, "end": v(-4.86, 3.94) * mm});
            skLineSegment(sketch, "E2728", {"start": v(-4.86, 3.94) * mm, "end": v(-4.83, 3.93) * mm});
            skLineSegment(sketch, "E2729", {"start": v(-4.83, 3.93) * mm, "end": v(-4.81, 3.92) * mm});
            skLineSegment(sketch, "E2730", {"start": v(-4.81, 3.92) * mm, "end": v(-4.79, 3.91) * mm});
            skLineSegment(sketch, "E2731", {"start": v(-4.79, 3.91) * mm, "end": v(-4.77, 3.9) * mm});
            skLineSegment(sketch, "E2732", {"start": v(-4.77, 3.9) * mm, "end": v(-4.74, 3.9) * mm});
            skLineSegment(sketch, "E2733", {"start": v(-4.74, 3.9) * mm, "end": v(-4.47, 3.66) * mm});
            skLineSegment(sketch, "E2734", {"start": v(-4.47, 3.66) * mm, "end": v(-4.45, 3.65) * mm});
            skLineSegment(sketch, "E2735", {"start": v(-4.45, 3.65) * mm, "end": v(-4.44, 3.64) * mm});
            skLineSegment(sketch, "E2736", {"start": v(-4.44, 3.64) * mm, "end": v(-4.42, 3.63) * mm});
            skLineSegment(sketch, "E2737", {"start": v(-4.42, 3.63) * mm, "end": v(-4.4, 3.61) * mm});
            skLineSegment(sketch, "E2738", {"start": v(-4.4, 3.61) * mm, "end": v(-4.4, 3.6) * mm});
            skLineSegment(sketch, "E2739", {"start": v(-4.4, 3.6) * mm, "end": v(-4.38, 3.59) * mm});
            skLineSegment(sketch, "E2740", {"start": v(-4.38, 3.59) * mm, "end": v(-4.37, 3.58) * mm});
            skLineSegment(sketch, "E2741", {"start": v(-4.37, 3.58) * mm, "end": v(-4.36, 3.56) * mm});
            skLineSegment(sketch, "E2742", {"start": v(-4.36, 3.56) * mm, "end": v(-4.34, 3.55) * mm});
            skLineSegment(sketch, "E2743", {"start": v(-4.34, 3.55) * mm, "end": v(-4.33, 3.54) * mm});
            skLineSegment(sketch, "E2744", {"start": v(-4.33, 3.54) * mm, "end": v(-4.32, 3.53) * mm});
            skLineSegment(sketch, "E2745", {"start": v(-4.32, 3.53) * mm, "end": v(-4.31, 3.51) * mm});
            skLineSegment(sketch, "E2746", {"start": v(-4.31, 3.51) * mm, "end": v(-4.3, 3.5) * mm});
            skLineSegment(sketch, "E2747", {"start": v(-4.3, 3.5) * mm, "end": v(-4.3, 3.49) * mm});
            skLineSegment(sketch, "E2748", {"start": v(-4.3, 3.49) * mm, "end": v(-4.3, 3.47) * mm});
            skLineSegment(sketch, "E2749", {"start": v(-4.3, 3.47) * mm, "end": v(-4.28, 3.46) * mm});
            skLineSegment(sketch, "E2750", {"start": v(-4.28, 3.46) * mm, "end": v(-4.28, 3.45) * mm});
            skLineSegment(sketch, "E2751", {"start": v(-4.28, 3.45) * mm, "end": v(-4.27, 3.43) * mm});
            skLineSegment(sketch, "E2752", {"start": v(-4.27, 3.43) * mm, "end": v(-4.27, 3.42) * mm});
            skLineSegment(sketch, "E2753", {"start": v(-4.27, 3.42) * mm, "end": v(-4.27, 3.4) * mm});
            skLineSegment(sketch, "E2754", {"start": v(-4.27, 3.4) * mm, "end": v(-4.26, 3.4) * mm});
            skLineSegment(sketch, "E2755", {"start": v(-4.26, 3.4) * mm, "end": v(-4.26, 3.38) * mm});
            skLineSegment(sketch, "E2756", {"start": v(-4.26, 3.38) * mm, "end": v(-4.26, 3.36) * mm});
            skLineSegment(sketch, "E2757", {"start": v(-4.26, 3.36) * mm, "end": v(-4.26, 3.35) * mm});
            skLineSegment(sketch, "E2758", {"start": v(-4.26, 3.35) * mm, "end": v(-4.26, 3.34) * mm});
            skLineSegment(sketch, "E2759", {"start": v(-4.26, 3.34) * mm, "end": v(-4.26, 3.32) * mm});
            skLineSegment(sketch, "E2760", {"start": v(-4.26, 3.32) * mm, "end": v(-4.26, 3.3) * mm});
            skLineSegment(sketch, "E2761", {"start": v(-4.26, 3.3) * mm, "end": v(-4.26, 3.3) * mm});
            skLineSegment(sketch, "E2762", {"start": v(-4.26, 3.3) * mm, "end": v(-4.26, 3.28) * mm});
            skLineSegment(sketch, "E2763", {"start": v(-4.26, 3.28) * mm, "end": v(-4.27, 3.26) * mm});
            skLineSegment(sketch, "E2764", {"start": v(-4.27, 3.26) * mm, "end": v(-4.27, 3.25) * mm});
            skLineSegment(sketch, "E2765", {"start": v(-4.27, 3.25) * mm, "end": v(-4.27, 3.23) * mm});
            skLineSegment(sketch, "E2766", {"start": v(-4.27, 3.23) * mm, "end": v(-4.55, 3.16) * mm});
            skLineSegment(sketch, "E2767", {"start": v(-4.55, 3.16) * mm, "end": v(-4.59, 3.15) * mm});
            skLineSegment(sketch, "E2768", {"start": v(-4.59, 3.15) * mm, "end": v(-4.62, 3.14) * mm});
            skLineSegment(sketch, "E2769", {"start": v(-4.62, 3.14) * mm, "end": v(-4.66, 3.13) * mm});
            skLineSegment(sketch, "E2770", {"start": v(-4.66, 3.13) * mm, "end": v(-4.7, 3.12) * mm});
            skLineSegment(sketch, "E2771", {"start": v(-4.7, 3.12) * mm, "end": v(-4.74, 3.1) * mm});
            skLineSegment(sketch, "E2772", {"start": v(-4.74, 3.1) * mm, "end": v(-4.77, 3.1) * mm});
            skLineSegment(sketch, "E2773", {"start": v(-4.77, 3.1) * mm, "end": v(-4.8, 3.1) * mm});
            skLineSegment(sketch, "E2774", {"start": v(-4.8, 3.1) * mm, "end": v(-4.84, 3.08) * mm});
            skLineSegment(sketch, "E2775", {"start": v(-4.84, 3.08) * mm, "end": v(-4.87, 3.07) * mm});
            skLineSegment(sketch, "E2776", {"start": v(-4.87, 3.07) * mm, "end": v(-4.9, 3.07) * mm});
            skLineSegment(sketch, "E2777", {"start": v(-4.9, 3.07) * mm, "end": v(-4.94, 3.06) * mm});
            skLineSegment(sketch, "E2778", {"start": v(-4.94, 3.06) * mm, "end": v(-4.97, 3.05) * mm});
            skLineSegment(sketch, "E2779", {"start": v(-4.97, 3.05) * mm, "end": v(-5, 3.04) * mm});
            skLineSegment(sketch, "E2780", {"start": v(-5, 3.04) * mm, "end": v(-5.03, 3.03) * mm});
            skLineSegment(sketch, "E2781", {"start": v(-5.03, 3.03) * mm, "end": v(-5.06, 3.03) * mm});
            skLineSegment(sketch, "E2782", {"start": v(-5.06, 3.03) * mm, "end": v(-5.09, 3.02) * mm});
            skLineSegment(sketch, "E2783", {"start": v(-5.09, 3.02) * mm, "end": v(-5.11, 3.01) * mm});
            skLineSegment(sketch, "E2784", {"start": v(-5.11, 3.01) * mm, "end": v(-5.14, 3) * mm});
            skLineSegment(sketch, "E2785", {"start": v(-5.14, 3) * mm, "end": v(-5.17, 3) * mm});
            skLineSegment(sketch, "E2786", {"start": v(-5.17, 3) * mm, "end": v(-5.2, 3) * mm});
            skLineSegment(sketch, "E2787", {"start": v(-5.2, 3) * mm, "end": v(-5.22, 2.98) * mm});
            skLineSegment(sketch, "E2788", {"start": v(-5.22, 2.98) * mm, "end": v(-5.24, 2.98) * mm});
            skLineSegment(sketch, "E2789", {"start": v(-5.24, 2.98) * mm, "end": v(-5.27, 2.97) * mm});
            skLineSegment(sketch, "E2790", {"start": v(-5.27, 2.97) * mm, "end": v(-5.29, 2.97) * mm});
            skLineSegment(sketch, "E2791", {"start": v(-5.29, 2.97) * mm, "end": v(-5.31, 2.96) * mm});
            skLineSegment(sketch, "E2792", {"start": v(-5.31, 2.96) * mm, "end": v(-5.33, 2.95) * mm});
            skLineSegment(sketch, "E2793", {"start": v(-5.33, 2.95) * mm, "end": v(-5.35, 2.95) * mm});
            skLineSegment(sketch, "E2794", {"start": v(-5.35, 2.95) * mm, "end": v(-5.37, 2.94) * mm});
            skLineSegment(sketch, "E2795", {"start": v(-5.37, 2.94) * mm, "end": v(-5.4, 2.94) * mm});
            skLineSegment(sketch, "E2796", {"start": v(-5.4, 2.94) * mm, "end": v(-5.41, 2.93) * mm});
            skLineSegment(sketch, "E2797", {"start": v(-5.41, 2.93) * mm, "end": v(-5.43, 2.93) * mm});
            skLineSegment(sketch, "E2798", {"start": v(-5.43, 2.93) * mm, "end": v(-5.45, 2.92) * mm});
            skLineSegment(sketch, "E2799", {"start": v(-5.45, 2.92) * mm, "end": v(-5.46, 2.92) * mm});
            skLineSegment(sketch, "E2800", {"start": v(-5.46, 2.92) * mm, "end": v(-5.48, 2.91) * mm});
            skLineSegment(sketch, "E2801", {"start": v(-5.48, 2.91) * mm, "end": v(-5.5, 2.9) * mm});
            skLineSegment(sketch, "E2802", {"start": v(-5.5, 2.9) * mm, "end": v(-5.5, 2.9) * mm});
            skLineSegment(sketch, "E2803", {"start": v(-5.5, 2.9) * mm, "end": v(-5.53, 2.9) * mm});
            skLineSegment(sketch, "E2804", {"start": v(-5.53, 2.9) * mm, "end": v(-5.54, 2.88) * mm});
            skLineSegment(sketch, "E2805", {"start": v(-5.54, 2.88) * mm, "end": v(-5.56, 2.88) * mm});
            skLineSegment(sketch, "E2806", {"start": v(-5.56, 2.88) * mm, "end": v(-5.58, 2.87) * mm});
            skLineSegment(sketch, "E2807", {"start": v(-5.58, 2.87) * mm, "end": v(-5.6, 2.86) * mm});
            skLineSegment(sketch, "E2808", {"start": v(-5.6, 2.86) * mm, "end": v(-5.62, 2.85) * mm});
            skLineSegment(sketch, "E2809", {"start": v(-5.62, 2.85) * mm, "end": v(-5.64, 2.84) * mm});
            skLineSegment(sketch, "E2810", {"start": v(-5.64, 2.84) * mm, "end": v(-5.66, 2.83) * mm});
            skLineSegment(sketch, "E2811", {"start": v(-5.66, 2.83) * mm, "end": v(-5.68, 2.82) * mm});
            skLineSegment(sketch, "E2812", {"start": v(-5.68, 2.82) * mm, "end": v(-5.7, 2.8) * mm});
            skLineSegment(sketch, "E2813", {"start": v(-5.7, 2.8) * mm, "end": v(-5.72, 2.8) * mm});
            skLineSegment(sketch, "E2814", {"start": v(-5.72, 2.8) * mm, "end": v(-5.74, 2.79) * mm});
            skLineSegment(sketch, "E2815", {"start": v(-5.74, 2.79) * mm, "end": v(-5.76, 2.77) * mm});
            skLineSegment(sketch, "E2816", {"start": v(-5.76, 2.77) * mm, "end": v(-5.78, 2.76) * mm});
            skLineSegment(sketch, "E2817", {"start": v(-5.78, 2.76) * mm, "end": v(-5.8, 2.75) * mm});
            skLineSegment(sketch, "E2818", {"start": v(-5.8, 2.75) * mm, "end": v(-5.83, 2.73) * mm});
            skLineSegment(sketch, "E2819", {"start": v(-5.83, 2.73) * mm, "end": v(-5.86, 2.72) * mm});
            skLineSegment(sketch, "E2820", {"start": v(-5.86, 2.72) * mm, "end": v(-5.88, 2.7) * mm});
            skLineSegment(sketch, "E2821", {"start": v(-5.88, 2.7) * mm, "end": v(-5.9, 2.69) * mm});
            skLineSegment(sketch, "E2822", {"start": v(-5.9, 2.69) * mm, "end": v(-5.93, 2.67) * mm});
            skLineSegment(sketch, "E2823", {"start": v(-5.93, 2.67) * mm, "end": v(-5.96, 2.66) * mm});
            skLineSegment(sketch, "E2824", {"start": v(-5.96, 2.66) * mm, "end": v(-5.98, 2.64) * mm});
            skLineSegment(sketch, "E2825", {"start": v(-5.98, 2.64) * mm, "end": v(-6, 2.62) * mm});
            skLineSegment(sketch, "E2826", {"start": v(-6, 2.62) * mm, "end": v(-6.04, 2.6) * mm});
            skLineSegment(sketch, "E2827", {"start": v(-6.04, 2.6) * mm, "end": v(-6.06, 2.59) * mm});
            skLineSegment(sketch, "E2828", {"start": v(-6.06, 2.59) * mm, "end": v(-6.1, 2.57) * mm});
            skLineSegment(sketch, "E2829", {"start": v(-6.1, 2.57) * mm, "end": v(-6.12, 2.55) * mm});
            skLineSegment(sketch, "E2830", {"start": v(-6.12, 2.55) * mm, "end": v(-6.15, 2.53) * mm});
            skLineSegment(sketch, "E2831", {"start": v(-6.15, 2.53) * mm, "end": v(-6.15, 2.57) * mm});
            skLineSegment(sketch, "E2832", {"start": v(-6.15, 2.57) * mm, "end": v(-6, 2.84) * mm});
            skLineSegment(sketch, "E2833", {"start": v(-6, 2.84) * mm, "end": v(-5.96, 2.87) * mm});
            skLineSegment(sketch, "E2834", {"start": v(-5.96, 2.87) * mm, "end": v(-5.94, 2.9) * mm});
            skLineSegment(sketch, "E2835", {"start": v(-5.94, 2.9) * mm, "end": v(-5.9, 2.93) * mm});
            skLineSegment(sketch, "E2836", {"start": v(-5.9, 2.93) * mm, "end": v(-5.88, 2.96) * mm});
            skLineSegment(sketch, "E2837", {"start": v(-5.88, 2.96) * mm, "end": v(-5.86, 2.98) * mm});
            skLineSegment(sketch, "E2838", {"start": v(-5.86, 2.98) * mm, "end": v(-5.83, 3) * mm});
            skLineSegment(sketch, "E2839", {"start": v(-5.83, 3) * mm, "end": v(-5.81, 3.03) * mm});
            skLineSegment(sketch, "E2840", {"start": v(-5.81, 3.03) * mm, "end": v(-5.79, 3.06) * mm});
            skLineSegment(sketch, "E2841", {"start": v(-5.79, 3.06) * mm, "end": v(-5.77, 3.08) * mm});
            skLineSegment(sketch, "E2842", {"start": v(-5.77, 3.08) * mm, "end": v(-5.75, 3.1) * mm});
            skLineSegment(sketch, "E2843", {"start": v(-5.75, 3.1) * mm, "end": v(-5.73, 3.13) * mm});
            skLineSegment(sketch, "E2844", {"start": v(-5.73, 3.13) * mm, "end": v(-5.7, 3.15) * mm});
            skLineSegment(sketch, "E2845", {"start": v(-5.7, 3.15) * mm, "end": v(-5.69, 3.17) * mm});
            skLineSegment(sketch, "E2846", {"start": v(-5.69, 3.17) * mm, "end": v(-5.67, 3.2) * mm});
            skLineSegment(sketch, "E2847", {"start": v(-5.67, 3.2) * mm, "end": v(-5.66, 3.21) * mm});
            skLineSegment(sketch, "E2848", {"start": v(-5.66, 3.21) * mm, "end": v(-5.64, 3.23) * mm});
            skLineSegment(sketch, "E2849", {"start": v(-5.64, 3.23) * mm, "end": v(-5.63, 3.25) * mm});
            skLineSegment(sketch, "E2850", {"start": v(-5.63, 3.25) * mm, "end": v(-5.61, 3.27) * mm});
            skLineSegment(sketch, "E2851", {"start": v(-5.61, 3.27) * mm, "end": v(-5.6, 3.3) * mm});
            skLineSegment(sketch, "E2852", {"start": v(-5.6, 3.3) * mm, "end": v(-5.6, 3.3) * mm});
            skLineSegment(sketch, "E2853", {"start": v(-5.6, 3.3) * mm, "end": v(-5.58, 3.32) * mm});
            skLineSegment(sketch, "E2854", {"start": v(-5.58, 3.32) * mm, "end": v(-5.57, 3.34) * mm});
            skLineSegment(sketch, "E2855", {"start": v(-5.57, 3.34) * mm, "end": v(-5.56, 3.36) * mm});
            skLineSegment(sketch, "E2856", {"start": v(-5.56, 3.36) * mm, "end": v(-5.55, 3.37) * mm});
            skLineSegment(sketch, "E2857", {"start": v(-5.55, 3.37) * mm, "end": v(-5.55, 3.39) * mm});
            skLineSegment(sketch, "E2858", {"start": v(-5.55, 3.39) * mm, "end": v(-5.54, 3.4) * mm});
            skLineSegment(sketch, "E2859", {"start": v(-5.54, 3.4) * mm, "end": v(-5.54, 3.41) * mm});
            skLineSegment(sketch, "E2860", {"start": v(-5.54, 3.41) * mm, "end": v(-5.53, 3.43) * mm});
            skLineSegment(sketch, "E2861", {"start": v(-5.53, 3.43) * mm, "end": v(-5.53, 3.44) * mm});
            skLineSegment(sketch, "E2862", {"start": v(-5.53, 3.44) * mm, "end": v(-5.53, 3.45) * mm});
            skLineSegment(sketch, "E2863", {"start": v(-5.53, 3.45) * mm, "end": v(-5.53, 3.46) * mm});
            skLineSegment(sketch, "E2864", {"start": v(-5.53, 3.46) * mm, "end": v(-5.52, 3.47) * mm});
            skLineSegment(sketch, "E2865", {"start": v(-5.52, 3.47) * mm, "end": v(-5.53, 3.49) * mm});
            skLineSegment(sketch, "E2866", {"start": v(-5.53, 3.49) * mm, "end": v(-5.54, 3.5) * mm});
            skLineSegment(sketch, "E2867", {"start": v(-5.54, 3.5) * mm, "end": v(-5.55, 3.53) * mm});
            skLineSegment(sketch, "E2868", {"start": v(-5.55, 3.53) * mm, "end": v(-5.56, 3.55) * mm});
            skLineSegment(sketch, "E2869", {"start": v(-5.56, 3.55) * mm, "end": v(-5.57, 3.57) * mm});
            skLineSegment(sketch, "E2870", {"start": v(-5.57, 3.57) * mm, "end": v(-5.58, 3.59) * mm});
            skLineSegment(sketch, "E2871", {"start": v(-5.58, 3.59) * mm, "end": v(-5.59, 3.6) * mm});
            skLineSegment(sketch, "E2872", {"start": v(-5.59, 3.6) * mm, "end": v(-5.6, 3.63) * mm});
            skLineSegment(sketch, "E2873", {"start": v(-5.6, 3.63) * mm, "end": v(-5.6, 3.64) * mm});
            skLineSegment(sketch, "E2874", {"start": v(-5.6, 3.64) * mm, "end": v(-5.61, 3.66) * mm});
            skLineSegment(sketch, "E2875", {"start": v(-5.61, 3.66) * mm, "end": v(-5.62, 3.68) * mm});
            skLineSegment(sketch, "E2876", {"start": v(-5.62, 3.68) * mm, "end": v(-5.63, 3.7) * mm});
            skLineSegment(sketch, "E2877", {"start": v(-5.63, 3.7) * mm, "end": v(-5.63, 3.72) * mm});
            skLineSegment(sketch, "E2878", {"start": v(-5.63, 3.72) * mm, "end": v(-5.64, 3.74) * mm});
            skLineSegment(sketch, "E2879", {"start": v(-5.64, 3.74) * mm, "end": v(-5.65, 3.76) * mm});
            skLineSegment(sketch, "E2880", {"start": v(-5.65, 3.76) * mm, "end": v(-5.65, 3.78) * mm});
            skLineSegment(sketch, "E2881", {"start": v(-5.65, 3.78) * mm, "end": v(-5.66, 3.8) * mm});
            skLineSegment(sketch, "E2882", {"start": v(-5.66, 3.8) * mm, "end": v(-5.66, 3.82) * mm});
            skLineSegment(sketch, "E2883", {"start": v(-5.66, 3.82) * mm, "end": v(-5.67, 3.84) * mm});
            skLineSegment(sketch, "E2884", {"start": v(-5.67, 3.84) * mm, "end": v(-5.67, 3.86) * mm});
            skLineSegment(sketch, "E2885", {"start": v(-5.67, 3.86) * mm, "end": v(-5.68, 3.88) * mm});
            skLineSegment(sketch, "E2886", {"start": v(-5.68, 3.88) * mm, "end": v(-5.68, 3.9) * mm});
            skLineSegment(sketch, "E2887", {"start": v(-5.68, 3.9) * mm, "end": v(-5.69, 3.92) * mm});
            skLineSegment(sketch, "E2888", {"start": v(-5.69, 3.92) * mm, "end": v(-5.7, 3.94) * mm});
            skLineSegment(sketch, "E2889", {"start": v(-5.7, 3.94) * mm, "end": v(-5.7, 3.96) * mm});
            skLineSegment(sketch, "E2890", {"start": v(-5.7, 3.96) * mm, "end": v(-5.7, 3.98) * mm});
            skLineSegment(sketch, "E2891", {"start": v(-5.7, 3.98) * mm, "end": v(-5.7, 4) * mm});
            skLineSegment(sketch, "E2892", {"start": v(-5.7, 4) * mm, "end": v(-5.7, 4.02) * mm});
            skLineSegment(sketch, "E2893", {"start": v(-5.7, 4.02) * mm, "end": v(-5.71, 4.04) * mm});
            skLineSegment(sketch, "E2894", {"start": v(-5.71, 4.04) * mm, "end": v(-5.72, 4.05) * mm});
            skLineSegment(sketch, "E2895", {"start": v(-5.72, 4.05) * mm, "end": v(-5.72, 4.07) * mm});
            skLineSegment(sketch, "E2896", {"start": v(-5.72, 4.07) * mm, "end": v(-5.72, 4.1) * mm});
            skLineSegment(sketch, "E2897", {"start": v(-5.72, 4.1) * mm, "end": v(-5.72, 4.11) * mm});
            skLineSegment(sketch, "E2898", {"start": v(-5.72, 4.11) * mm, "end": v(-5.72, 4.13) * mm});
            skLineSegment(sketch, "E2899", {"start": v(-5.72, 4.13) * mm, "end": v(-5.72, 4.15) * mm});
            skLineSegment(sketch, "E2900", {"start": v(-5.72, 4.15) * mm, "end": v(-5.72, 4.17) * mm});
            skLineSegment(sketch, "E2901", {"start": v(-5.72, 4.17) * mm, "end": v(-5.72, 4.18) * mm});
            skLineSegment(sketch, "E2902", {"start": v(-5.72, 4.18) * mm, "end": v(-5.72, 4.2) * mm});
            skLineSegment(sketch, "E2903", {"start": v(-5.72, 4.2) * mm, "end": v(-5.71, 4.21) * mm});
            skLineSegment(sketch, "E2904", {"start": v(-5.71, 4.21) * mm, "end": v(-5.71, 4.23) * mm});
            skLineSegment(sketch, "E2905", {"start": v(-5.71, 4.23) * mm, "end": v(-5.71, 4.24) * mm});
            skLineSegment(sketch, "E2906", {"start": v(-5.71, 4.24) * mm, "end": v(-5.7, 4.25) * mm});
            skLineSegment(sketch, "E2907", {"start": v(-5.7, 4.25) * mm, "end": v(-5.7, 4.27) * mm});
            skLineSegment(sketch, "E2908", {"start": v(-5.7, 4.27) * mm, "end": v(-5.7, 4.28) * mm});
            skLineSegment(sketch, "E2909", {"start": v(-5.7, 4.28) * mm, "end": v(-5.7, 4.29) * mm});
            skLineSegment(sketch, "E2910", {"start": v(-5.7, 4.29) * mm, "end": v(-5.7, 4.3) * mm});
            skLineSegment(sketch, "E2911", {"start": v(-5.7, 4.3) * mm, "end": v(-5.7, 4.3) * mm});
            skLineSegment(sketch, "E2912", {"start": v(-5.7, 4.3) * mm, "end": v(-5.7, 4.32) * mm});
            skLineSegment(sketch, "E2913", {"start": v(-5.7, 4.32) * mm, "end": v(-5.69, 4.33) * mm});
            skLineSegment(sketch, "E2914", {"start": v(-5.69, 4.33) * mm, "end": v(-5.68, 4.33) * mm});
            skLineSegment(sketch, "E2915", {"start": v(-5.68, 4.33) * mm, "end": v(-5.68, 4.34) * mm});
            skLineSegment(sketch, "E2916", {"start": v(-5.68, 4.34) * mm, "end": v(-5.67, 4.35) * mm});
            skLineSegment(sketch, "E2917", {"start": v(-5.67, 4.35) * mm, "end": v(-5.67, 4.35) * mm});
            skLineSegment(sketch, "E2918", {"start": v(-5.67, 4.35) * mm, "end": v(-5.66, 4.36) * mm});
            skLineSegment(sketch, "E2919", {"start": v(-5.66, 4.36) * mm, "end": v(-5.66, 4.36) * mm});
            skLineSegment(sketch, "E2920", {"start": v(-5.66, 4.36) * mm, "end": v(-5.65, 4.36) * mm});
            skLineSegment(sketch, "E2921", {"start": v(-5.65, 4.36) * mm, "end": v(-5.65, 4.37) * mm});
            skLineSegment(sketch, "E2922", {"start": v(-5.65, 4.37) * mm, "end": v(-5.64, 4.37) * mm});
            skLineSegment(sketch, "E2923", {"start": v(-5.64, 4.37) * mm, "end": v(-5.64, 4.37) * mm});
            skLineSegment(sketch, "E2924", {"start": v(-5.64, 4.37) * mm, "end": v(-5.63, 4.37) * mm});
            skLineSegment(sketch, "E2925", {"start": v(-5.63, 4.37) * mm, "end": v(-5.62, 4.37) * mm});
            skLineSegment(sketch, "E2926", {"start": v(-5.62, 4.37) * mm, "end": v(-5.62, 4.37) * mm});
            skLineSegment(sketch, "E2927", {"start": v(-5.62, 4.37) * mm, "end": v(-5.61, 4.37) * mm});
            skLineSegment(sketch, "E2928", {"start": v(-5.61, 4.37) * mm, "end": v(-5.6, 4.37) * mm});
            skLineSegment(sketch, "E2929", {"start": v(-0.06, 1.63) * mm, "end": v(-0.1, 1.64) * mm});
            skLineSegment(sketch, "E2930", {"start": v(-0.1, 1.64) * mm, "end": v(-0.13, 1.64) * mm});
            skLineSegment(sketch, "E2931", {"start": v(-0.13, 1.64) * mm, "end": v(-0.16, 1.64) * mm});
            skLineSegment(sketch, "E2932", {"start": v(-0.16, 1.64) * mm, "end": v(-0.2, 1.64) * mm});
            skLineSegment(sketch, "E2933", {"start": v(-0.2, 1.64) * mm, "end": v(-0.23, 1.64) * mm});
            skLineSegment(sketch, "E2934", {"start": v(-0.23, 1.64) * mm, "end": v(-0.27, 1.64) * mm});
            skLineSegment(sketch, "E2935", {"start": v(-0.27, 1.64) * mm, "end": v(-0.3, 1.64) * mm});
            skLineSegment(sketch, "E2936", {"start": v(-0.3, 1.64) * mm, "end": v(-0.34, 1.64) * mm});
            skLineSegment(sketch, "E2937", {"start": v(-0.34, 1.64) * mm, "end": v(-0.37, 1.64) * mm});
            skLineSegment(sketch, "E2938", {"start": v(-0.37, 1.64) * mm, "end": v(-0.4, 1.64) * mm});
            skLineSegment(sketch, "E2939", {"start": v(-0.4, 1.64) * mm, "end": v(-0.44, 1.64) * mm});
            skLineSegment(sketch, "E2940", {"start": v(-0.44, 1.64) * mm, "end": v(-0.47, 1.64) * mm});
            skLineSegment(sketch, "E2941", {"start": v(-0.47, 1.64) * mm, "end": v(-0.5, 1.64) * mm});
            skLineSegment(sketch, "E2942", {"start": v(-0.5, 1.64) * mm, "end": v(-0.53, 1.64) * mm});
            skLineSegment(sketch, "E2943", {"start": v(-0.53, 1.64) * mm, "end": v(-0.56, 1.64) * mm});
            skLineSegment(sketch, "E2944", {"start": v(-0.56, 1.64) * mm, "end": v(-0.6, 1.63) * mm});
            skLineSegment(sketch, "E2945", {"start": v(-0.6, 1.63) * mm, "end": v(-0.62, 1.63) * mm});
            skLineSegment(sketch, "E2946", {"start": v(-0.62, 1.63) * mm, "end": v(-0.65, 1.63) * mm});
            skLineSegment(sketch, "E2947", {"start": v(-0.65, 1.63) * mm, "end": v(-0.68, 1.62) * mm});
            skLineSegment(sketch, "E2948", {"start": v(-0.68, 1.62) * mm, "end": v(-0.71, 1.62) * mm});
            skLineSegment(sketch, "E2949", {"start": v(-0.71, 1.62) * mm, "end": v(-0.74, 1.62) * mm});
            skLineSegment(sketch, "E2950", {"start": v(-0.74, 1.62) * mm, "end": v(-0.77, 1.61) * mm});
            skLineSegment(sketch, "E2951", {"start": v(-0.77, 1.61) * mm, "end": v(-0.8, 1.6) * mm});
            skLineSegment(sketch, "E2952", {"start": v(-0.8, 1.6) * mm, "end": v(-0.82, 1.6) * mm});
            skLineSegment(sketch, "E2953", {"start": v(-0.82, 1.6) * mm, "end": v(-0.85, 1.6) * mm});
            skLineSegment(sketch, "E2954", {"start": v(-0.85, 1.6) * mm, "end": v(-0.88, 1.6) * mm});
            skLineSegment(sketch, "E2955", {"start": v(-0.88, 1.6) * mm, "end": v(-0.9, 1.59) * mm});
            skLineSegment(sketch, "E2956", {"start": v(-0.9, 1.59) * mm, "end": v(-0.93, 1.58) * mm});
            skLineSegment(sketch, "E2957", {"start": v(-0.93, 1.58) * mm, "end": v(-0.96, 1.58) * mm});
            skLineSegment(sketch, "E2958", {"start": v(-0.96, 1.58) * mm, "end": v(-0.98, 1.57) * mm});
            skLineSegment(sketch, "E2959", {"start": v(-0.98, 1.57) * mm, "end": v(-1, 1.56) * mm});
            skLineSegment(sketch, "E2960", {"start": v(-1, 1.56) * mm, "end": v(-1.03, 1.55) * mm});
            skLineSegment(sketch, "E2961", {"start": v(-1.03, 1.55) * mm, "end": v(-1.03, 1.28) * mm});
            skLineSegment(sketch, "E2962", {"start": v(-1.03, 1.28) * mm, "end": v(-1, 1.28) * mm});
            skLineSegment(sketch, "E2963", {"start": v(-1, 1.28) * mm, "end": v(-0.97, 1.29) * mm});
            skLineSegment(sketch, "E2964", {"start": v(-0.97, 1.29) * mm, "end": v(-0.94, 1.29) * mm});
            skLineSegment(sketch, "E2965", {"start": v(-0.94, 1.29) * mm, "end": v(-0.9, 1.29) * mm});
            skLineSegment(sketch, "E2966", {"start": v(-0.9, 1.29) * mm, "end": v(-0.88, 1.29) * mm});
            skLineSegment(sketch, "E2967", {"start": v(-0.88, 1.29) * mm, "end": v(-0.85, 1.29) * mm});
            skLineSegment(sketch, "E2968", {"start": v(-0.85, 1.29) * mm, "end": v(-0.82, 1.28) * mm});
            skLineSegment(sketch, "E2969", {"start": v(-0.82, 1.28) * mm, "end": v(-0.8, 1.28) * mm});
            skLineSegment(sketch, "E2970", {"start": v(-0.8, 1.28) * mm, "end": v(-0.76, 1.28) * mm});
            skLineSegment(sketch, "E2971", {"start": v(-0.76, 1.28) * mm, "end": v(-0.73, 1.28) * mm});
            skLineSegment(sketch, "E2972", {"start": v(-0.73, 1.28) * mm, "end": v(-0.7, 1.27) * mm});
            skLineSegment(sketch, "E2973", {"start": v(-0.7, 1.27) * mm, "end": v(-0.68, 1.27) * mm});
            skLineSegment(sketch, "E2974", {"start": v(-0.68, 1.27) * mm, "end": v(-0.65, 1.26) * mm});
            skLineSegment(sketch, "E2975", {"start": v(-0.65, 1.26) * mm, "end": v(-0.62, 1.26) * mm});
            skLineSegment(sketch, "E2976", {"start": v(-0.62, 1.26) * mm, "end": v(-0.6, 1.25) * mm});
            skLineSegment(sketch, "E2977", {"start": v(-0.6, 1.25) * mm, "end": v(-0.57, 1.24) * mm});
            skLineSegment(sketch, "E2978", {"start": v(-0.57, 1.24) * mm, "end": v(-0.55, 1.23) * mm});
            skLineSegment(sketch, "E2979", {"start": v(-0.55, 1.23) * mm, "end": v(-0.52, 1.23) * mm});
            skLineSegment(sketch, "E2980", {"start": v(-0.52, 1.23) * mm, "end": v(-0.5, 1.22) * mm});
            skLineSegment(sketch, "E2981", {"start": v(-0.5, 1.22) * mm, "end": v(-0.47, 1.2) * mm});
            skLineSegment(sketch, "E2982", {"start": v(-0.47, 1.2) * mm, "end": v(-0.45, 1.2) * mm});
            skLineSegment(sketch, "E2983", {"start": v(-0.45, 1.2) * mm, "end": v(-0.43, 1.19) * mm});
            skLineSegment(sketch, "E2984", {"start": v(-0.43, 1.19) * mm, "end": v(-0.4, 1.18) * mm});
            skLineSegment(sketch, "E2985", {"start": v(-0.4, 1.18) * mm, "end": v(-0.38, 1.16) * mm});
            skLineSegment(sketch, "E2986", {"start": v(-0.38, 1.16) * mm, "end": v(-0.36, 1.15) * mm});
            skLineSegment(sketch, "E2987", {"start": v(-0.36, 1.15) * mm, "end": v(-0.34, 1.14) * mm});
            skLineSegment(sketch, "E2988", {"start": v(-0.34, 1.14) * mm, "end": v(-0.31, 1.12) * mm});
            skLineSegment(sketch, "E2989", {"start": v(-0.31, 1.12) * mm, "end": v(-0.3, 1.11) * mm});
            skLineSegment(sketch, "E2990", {"start": v(-0.3, 1.11) * mm, "end": v(-0.27, 1.1) * mm});
            skLineSegment(sketch, "E2991", {"start": v(-0.27, 1.1) * mm, "end": v(-0.25, 1.08) * mm});
            skLineSegment(sketch, "E2992", {"start": v(-0.25, 1.08) * mm, "end": v(-0.23, 1.06) * mm});
            skLineSegment(sketch, "E2993", {"start": v(-0.23, 1.06) * mm, "end": v(-0.21, 1.05) * mm});
            skLineSegment(sketch, "E2994", {"start": v(-0.21, 1.05) * mm, "end": v(-0.2, 1.07) * mm});
            skLineSegment(sketch, "E2995", {"start": v(-0.2, 1.07) * mm, "end": v(-0.19, 1.1) * mm});
            skLineSegment(sketch, "E2996", {"start": v(-0.19, 1.1) * mm, "end": v(-0.18, 1.12) * mm});
            skLineSegment(sketch, "E2997", {"start": v(-0.18, 1.12) * mm, "end": v(-0.17, 1.14) * mm});
            skLineSegment(sketch, "E2998", {"start": v(-0.17, 1.14) * mm, "end": v(-0.16, 1.16) * mm});
            skLineSegment(sketch, "E2999", {"start": v(-0.16, 1.16) * mm, "end": v(-0.15, 1.19) * mm});
            skLineSegment(sketch, "E3000", {"start": v(-0.15, 1.19) * mm, "end": v(-0.14, 1.2) * mm});
            skLineSegment(sketch, "E3001", {"start": v(-0.14, 1.2) * mm, "end": v(-0.13, 1.23) * mm});
            skLineSegment(sketch, "E3002", {"start": v(-0.13, 1.23) * mm, "end": v(-0.12, 1.25) * mm});
            skLineSegment(sketch, "E3003", {"start": v(-0.12, 1.25) * mm, "end": v(-0.11, 1.27) * mm});
            skLineSegment(sketch, "E3004", {"start": v(-0.11, 1.27) * mm, "end": v(-0.1, 1.3) * mm});
            skLineSegment(sketch, "E3005", {"start": v(-0.1, 1.3) * mm, "end": v(-0.1, 1.31) * mm});
            skLineSegment(sketch, "E3006", {"start": v(-0.1, 1.31) * mm, "end": v(-0.1, 1.33) * mm});
            skLineSegment(sketch, "E3007", {"start": v(-0.1, 1.33) * mm, "end": v(-0.09, 1.35) * mm});
            skLineSegment(sketch, "E3008", {"start": v(-0.09, 1.35) * mm, "end": v(-0.08, 1.37) * mm});
            skLineSegment(sketch, "E3009", {"start": v(-0.08, 1.37) * mm, "end": v(-0.08, 1.39) * mm});
            skLineSegment(sketch, "E3010", {"start": v(-0.08, 1.39) * mm, "end": v(-0.07, 1.4) * mm});
            skLineSegment(sketch, "E3011", {"start": v(-0.07, 1.4) * mm, "end": v(-0.07, 1.42) * mm});
            skLineSegment(sketch, "E3012", {"start": v(-0.07, 1.42) * mm, "end": v(-0.06, 1.44) * mm});
            skLineSegment(sketch, "E3013", {"start": v(-0.06, 1.44) * mm, "end": v(-0.06, 1.46) * mm});
            skLineSegment(sketch, "E3014", {"start": v(-0.06, 1.46) * mm, "end": v(-0.06, 1.48) * mm});
            skLineSegment(sketch, "E3015", {"start": v(-0.06, 1.48) * mm, "end": v(-0.05, 1.5) * mm});
            skLineSegment(sketch, "E3016", {"start": v(-0.05, 1.5) * mm, "end": v(-0.05, 1.5) * mm});
            skLineSegment(sketch, "E3017", {"start": v(-0.05, 1.5) * mm, "end": v(-0.05, 1.52) * mm});
            skLineSegment(sketch, "E3018", {"start": v(-0.05, 1.52) * mm, "end": v(-0.05, 1.54) * mm});
            skLineSegment(sketch, "E3019", {"start": v(-0.05, 1.54) * mm, "end": v(-0.05, 1.55) * mm});
            skLineSegment(sketch, "E3020", {"start": v(-0.05, 1.55) * mm, "end": v(-0.05, 1.57) * mm});
            skLineSegment(sketch, "E3021", {"start": v(-0.05, 1.57) * mm, "end": v(-0.05, 1.58) * mm});
            skLineSegment(sketch, "E3022", {"start": v(-0.05, 1.58) * mm, "end": v(-0.05, 1.6) * mm});
            skLineSegment(sketch, "E3023", {"start": v(-0.05, 1.6) * mm, "end": v(-0.05, 1.6) * mm});
            skLineSegment(sketch, "E3024", {"start": v(-0.05, 1.6) * mm, "end": v(-0.05, 1.62) * mm});
            skLineSegment(sketch, "E3025", {"start": v(-0.05, 1.62) * mm, "end": v(-0.06, 1.63) * mm});
            skLineSegment(sketch, "E3026", {"start": v(-2.56, 0.77) * mm, "end": v(-2.55, 0.76) * mm});
            skLineSegment(sketch, "E3027", {"start": v(-2.55, 0.76) * mm, "end": v(-2.55, 0.74) * mm});
            skLineSegment(sketch, "E3028", {"start": v(-2.55, 0.74) * mm, "end": v(-2.54, 0.73) * mm});
            skLineSegment(sketch, "E3029", {"start": v(-2.54, 0.73) * mm, "end": v(-2.54, 0.71) * mm});
            skLineSegment(sketch, "E3030", {"start": v(-2.54, 0.71) * mm, "end": v(-2.53, 0.7) * mm});
            skLineSegment(sketch, "E3031", {"start": v(-2.53, 0.7) * mm, "end": v(-2.53, 0.68) * mm});
            skLineSegment(sketch, "E3032", {"start": v(-2.53, 0.68) * mm, "end": v(-2.52, 0.67) * mm});
            skLineSegment(sketch, "E3033", {"start": v(-2.52, 0.67) * mm, "end": v(-2.52, 0.65) * mm});
            skLineSegment(sketch, "E3034", {"start": v(-2.52, 0.65) * mm, "end": v(-2.51, 0.64) * mm});
            skLineSegment(sketch, "E3035", {"start": v(-2.51, 0.64) * mm, "end": v(-2.51, 0.62) * mm});
            skLineSegment(sketch, "E3036", {"start": v(-2.51, 0.62) * mm, "end": v(-2.5, 0.6) * mm});
            skLineSegment(sketch, "E3037", {"start": v(-2.5, 0.6) * mm, "end": v(-2.5, 0.6) * mm});
            skLineSegment(sketch, "E3038", {"start": v(-2.5, 0.6) * mm, "end": v(-2.5, 0.58) * mm});
            skLineSegment(sketch, "E3039", {"start": v(-2.5, 0.58) * mm, "end": v(-2.5, 0.56) * mm});
            skLineSegment(sketch, "E3040", {"start": v(-2.5, 0.56) * mm, "end": v(-2.5, 0.55) * mm});
            skLineSegment(sketch, "E3041", {"start": v(-2.5, 0.55) * mm, "end": v(-2.49, 0.53) * mm});
            skLineSegment(sketch, "E3042", {"start": v(-2.49, 0.53) * mm, "end": v(-2.48, 0.51) * mm});
            skLineSegment(sketch, "E3043", {"start": v(-2.48, 0.51) * mm, "end": v(-2.48, 0.5) * mm});
            skLineSegment(sketch, "E3044", {"start": v(-2.48, 0.5) * mm, "end": v(-2.48, 0.48) * mm});
            skLineSegment(sketch, "E3045", {"start": v(-2.48, 0.48) * mm, "end": v(-2.47, 0.47) * mm});
            skLineSegment(sketch, "E3046", {"start": v(-2.47, 0.47) * mm, "end": v(-2.47, 0.45) * mm});
            skLineSegment(sketch, "E3047", {"start": v(-2.47, 0.45) * mm, "end": v(-2.47, 0.43) * mm});
            skLineSegment(sketch, "E3048", {"start": v(-2.47, 0.43) * mm, "end": v(-2.46, 0.42) * mm});
            skLineSegment(sketch, "E3049", {"start": v(-2.46, 0.42) * mm, "end": v(-2.46, 0.4) * mm});
            skLineSegment(sketch, "E3050", {"start": v(-2.46, 0.4) * mm, "end": v(-2.46, 0.38) * mm});
            skLineSegment(sketch, "E3051", {"start": v(-2.46, 0.38) * mm, "end": v(-2.45, 0.37) * mm});
            skLineSegment(sketch, "E3052", {"start": v(-2.45, 0.37) * mm, "end": v(-2.45, 0.35) * mm});
            skLineSegment(sketch, "E3053", {"start": v(-2.45, 0.35) * mm, "end": v(-2.45, 0.33) * mm});
            skLineSegment(sketch, "E3054", {"start": v(-2.45, 0.33) * mm, "end": v(-2.45, 0.32) * mm});
            skLineSegment(sketch, "E3055", {"start": v(-2.45, 0.32) * mm, "end": v(-2.44, 0.3) * mm});
            skLineSegment(sketch, "E3056", {"start": v(-2.44, 0.3) * mm, "end": v(-2.44, 0.28) * mm});
            skLineSegment(sketch, "E3057", {"start": v(-2.44, 0.28) * mm, "end": v(-2.44, 0.27) * mm});
            skLineSegment(sketch, "E3058", {"start": v(-2.44, 0.27) * mm, "end": v(-1.7, 0.3) * mm});
            skLineSegment(sketch, "E3059", {"start": v(-1.7, 0.3) * mm, "end": v(-1.7, 0.54) * mm});
            skLineSegment(sketch, "E3060", {"start": v(-1.7, 0.54) * mm, "end": v(-1.72, 0.53) * mm});
            skLineSegment(sketch, "E3061", {"start": v(-1.72, 0.53) * mm, "end": v(-1.74, 0.53) * mm});
            skLineSegment(sketch, "E3062", {"start": v(-1.74, 0.53) * mm, "end": v(-1.77, 0.53) * mm});
            skLineSegment(sketch, "E3063", {"start": v(-1.77, 0.53) * mm, "end": v(-1.8, 0.52) * mm});
            skLineSegment(sketch, "E3064", {"start": v(-1.8, 0.52) * mm, "end": v(-1.81, 0.52) * mm});
            skLineSegment(sketch, "E3065", {"start": v(-1.81, 0.52) * mm, "end": v(-1.84, 0.51) * mm});
            skLineSegment(sketch, "E3066", {"start": v(-1.84, 0.51) * mm, "end": v(-1.86, 0.5) * mm});
            skLineSegment(sketch, "E3067", {"start": v(-1.86, 0.5) * mm, "end": v(-1.88, 0.5) * mm});
            skLineSegment(sketch, "E3068", {"start": v(-1.88, 0.5) * mm, "end": v(-1.9, 0.5) * mm});
            skLineSegment(sketch, "E3069", {"start": v(-1.9, 0.5) * mm, "end": v(-1.93, 0.5) * mm});
            skLineSegment(sketch, "E3070", {"start": v(-1.93, 0.5) * mm, "end": v(-1.95, 0.5) * mm});
            skLineSegment(sketch, "E3071", {"start": v(-1.95, 0.5) * mm, "end": v(-1.97, 0.49) * mm});
            skLineSegment(sketch, "E3072", {"start": v(-1.97, 0.49) * mm, "end": v(-1.99, 0.48) * mm});
            skLineSegment(sketch, "E3073", {"start": v(-1.99, 0.48) * mm, "end": v(-2, 0.48) * mm});
            skLineSegment(sketch, "E3074", {"start": v(-2, 0.48) * mm, "end": v(-2.03, 0.47) * mm});
            skLineSegment(sketch, "E3075", {"start": v(-2.03, 0.47) * mm, "end": v(-2.05, 0.47) * mm});
            skLineSegment(sketch, "E3076", {"start": v(-2.05, 0.47) * mm, "end": v(-2.07, 0.47) * mm});
            skLineSegment(sketch, "E3077", {"start": v(-2.07, 0.47) * mm, "end": v(-2.09, 0.46) * mm});
            skLineSegment(sketch, "E3078", {"start": v(-2.09, 0.46) * mm, "end": v(-2.1, 0.46) * mm});
            skLineSegment(sketch, "E3079", {"start": v(-2.1, 0.46) * mm, "end": v(-2.12, 0.46) * mm});
            skLineSegment(sketch, "E3080", {"start": v(-2.12, 0.46) * mm, "end": v(-2.14, 0.45) * mm});
            skLineSegment(sketch, "E3081", {"start": v(-2.14, 0.45) * mm, "end": v(-2.16, 0.45) * mm});
            skLineSegment(sketch, "E3082", {"start": v(-2.16, 0.45) * mm, "end": v(-2.18, 0.45) * mm});
            skLineSegment(sketch, "E3083", {"start": v(-2.18, 0.45) * mm, "end": v(-2.2, 0.44) * mm});
            skLineSegment(sketch, "E3084", {"start": v(-2.2, 0.44) * mm, "end": v(-2.21, 0.44) * mm});
            skLineSegment(sketch, "E3085", {"start": v(-2.21, 0.44) * mm, "end": v(-2.23, 0.44) * mm});
            skLineSegment(sketch, "E3086", {"start": v(-2.23, 0.44) * mm, "end": v(-2.24, 0.44) * mm});
            skLineSegment(sketch, "E3087", {"start": v(-2.24, 0.44) * mm, "end": v(-2.26, 0.43) * mm});
            skLineSegment(sketch, "E3088", {"start": v(-2.26, 0.43) * mm, "end": v(-2.28, 0.43) * mm});
            skLineSegment(sketch, "E3089", {"start": v(-2.28, 0.43) * mm, "end": v(-2.3, 0.43) * mm});
            skLineSegment(sketch, "E3090", {"start": v(-2.3, 0.43) * mm, "end": v(-2.3, 0.42) * mm});
            skLineSegment(sketch, "E3091", {"start": v(-2.3, 0.42) * mm, "end": v(-2.32, 0.42) * mm});
            skLineSegment(sketch, "E3092", {"start": v(-2.32, 0.42) * mm, "end": v(-2.31, 0.43) * mm});
            skLineSegment(sketch, "E3093", {"start": v(-2.31, 0.43) * mm, "end": v(-2.3, 0.44) * mm});
            skLineSegment(sketch, "E3094", {"start": v(-2.3, 0.44) * mm, "end": v(-2.3, 0.44) * mm});
            skLineSegment(sketch, "E3095", {"start": v(-2.3, 0.44) * mm, "end": v(-2.28, 0.45) * mm});
            skLineSegment(sketch, "E3096", {"start": v(-2.28, 0.45) * mm, "end": v(-2.27, 0.46) * mm});
            skLineSegment(sketch, "E3097", {"start": v(-2.27, 0.46) * mm, "end": v(-2.26, 0.47) * mm});
            skLineSegment(sketch, "E3098", {"start": v(-2.26, 0.47) * mm, "end": v(-2.25, 0.48) * mm});
            skLineSegment(sketch, "E3099", {"start": v(-2.25, 0.48) * mm, "end": v(-2.25, 0.48) * mm});
            skLineSegment(sketch, "E3100", {"start": v(-2.25, 0.48) * mm, "end": v(-2.24, 0.5) * mm});
            skLineSegment(sketch, "E3101", {"start": v(-2.24, 0.5) * mm, "end": v(-2.23, 0.5) * mm});
            skLineSegment(sketch, "E3102", {"start": v(-2.23, 0.5) * mm, "end": v(-2.22, 0.5) * mm});
            skLineSegment(sketch, "E3103", {"start": v(-2.22, 0.5) * mm, "end": v(-2.2, 0.52) * mm});
            skLineSegment(sketch, "E3104", {"start": v(-2.2, 0.52) * mm, "end": v(-2.2, 0.52) * mm});
            skLineSegment(sketch, "E3105", {"start": v(-2.2, 0.52) * mm, "end": v(-2.2, 0.53) * mm});
            skLineSegment(sketch, "E3106", {"start": v(-2.2, 0.53) * mm, "end": v(-2.18, 0.54) * mm});
            skLineSegment(sketch, "E3107", {"start": v(-2.18, 0.54) * mm, "end": v(-2.17, 0.55) * mm});
            skLineSegment(sketch, "E3108", {"start": v(-2.17, 0.55) * mm, "end": v(-2.17, 0.56) * mm});
            skLineSegment(sketch, "E3109", {"start": v(-2.17, 0.56) * mm, "end": v(-2.16, 0.57) * mm});
            skLineSegment(sketch, "E3110", {"start": v(-2.16, 0.57) * mm, "end": v(-2.15, 0.58) * mm});
            skLineSegment(sketch, "E3111", {"start": v(-2.15, 0.58) * mm, "end": v(-2.14, 0.58) * mm});
            skLineSegment(sketch, "E3112", {"start": v(-2.14, 0.58) * mm, "end": v(-2.13, 0.6) * mm});
            skLineSegment(sketch, "E3113", {"start": v(-2.13, 0.6) * mm, "end": v(-2.12, 0.6) * mm});
            skLineSegment(sketch, "E3114", {"start": v(-2.12, 0.6) * mm, "end": v(-2.12, 0.61) * mm});
            skLineSegment(sketch, "E3115", {"start": v(-2.12, 0.61) * mm, "end": v(-2.1, 0.62) * mm});
            skLineSegment(sketch, "E3116", {"start": v(-2.1, 0.62) * mm, "end": v(-2.1, 0.63) * mm});
            skLineSegment(sketch, "E3117", {"start": v(-2.1, 0.63) * mm, "end": v(-2.1, 0.64) * mm});
            skLineSegment(sketch, "E3118", {"start": v(-2.1, 0.64) * mm, "end": v(-2.09, 0.65) * mm});
            skLineSegment(sketch, "E3119", {"start": v(-2.09, 0.65) * mm, "end": v(-2.08, 0.66) * mm});
            skLineSegment(sketch, "E3120", {"start": v(-2.08, 0.66) * mm, "end": v(-2.07, 0.67) * mm});
            skLineSegment(sketch, "E3121", {"start": v(-2.07, 0.67) * mm, "end": v(-2.06, 0.68) * mm});
            skLineSegment(sketch, "E3122", {"start": v(-2.06, 0.68) * mm, "end": v(-2.06, 0.69) * mm});
            skLineSegment(sketch, "E3123", {"start": v(-2.06, 0.69) * mm, "end": v(-2.05, 0.7) * mm});
            skLineSegment(sketch, "E3124", {"start": v(-2.05, 0.7) * mm, "end": v(-2.06, 0.7) * mm});
            skLineSegment(sketch, "E3125", {"start": v(-2.06, 0.7) * mm, "end": v(-2.08, 0.69) * mm});
            skLineSegment(sketch, "E3126", {"start": v(-2.08, 0.69) * mm, "end": v(-2.1, 0.68) * mm});
            skLineSegment(sketch, "E3127", {"start": v(-2.1, 0.68) * mm, "end": v(-2.1, 0.68) * mm});
            skLineSegment(sketch, "E3128", {"start": v(-2.1, 0.68) * mm, "end": v(-2.12, 0.68) * mm});
            skLineSegment(sketch, "E3129", {"start": v(-2.12, 0.68) * mm, "end": v(-2.14, 0.67) * mm});
            skLineSegment(sketch, "E3130", {"start": v(-2.14, 0.67) * mm, "end": v(-2.15, 0.67) * mm});
            skLineSegment(sketch, "E3131", {"start": v(-2.15, 0.67) * mm, "end": v(-2.17, 0.67) * mm});
            skLineSegment(sketch, "E3132", {"start": v(-2.17, 0.67) * mm, "end": v(-2.18, 0.67) * mm});
            skLineSegment(sketch, "E3133", {"start": v(-2.18, 0.67) * mm, "end": v(-2.2, 0.67) * mm});
            skLineSegment(sketch, "E3134", {"start": v(-2.2, 0.67) * mm, "end": v(-2.21, 0.67) * mm});
            skLineSegment(sketch, "E3135", {"start": v(-2.21, 0.67) * mm, "end": v(-2.23, 0.67) * mm});
            skLineSegment(sketch, "E3136", {"start": v(-2.23, 0.67) * mm, "end": v(-2.24, 0.67) * mm});
            skLineSegment(sketch, "E3137", {"start": v(-2.24, 0.67) * mm, "end": v(-2.26, 0.67) * mm});
            skLineSegment(sketch, "E3138", {"start": v(-2.26, 0.67) * mm, "end": v(-2.28, 0.67) * mm});
            skLineSegment(sketch, "E3139", {"start": v(-2.28, 0.67) * mm, "end": v(-2.3, 0.68) * mm});
            skLineSegment(sketch, "E3140", {"start": v(-2.3, 0.68) * mm, "end": v(-2.3, 0.68) * mm});
            skLineSegment(sketch, "E3141", {"start": v(-2.3, 0.68) * mm, "end": v(-2.32, 0.68) * mm});
            skLineSegment(sketch, "E3142", {"start": v(-2.32, 0.68) * mm, "end": v(-2.34, 0.69) * mm});
            skLineSegment(sketch, "E3143", {"start": v(-2.34, 0.69) * mm, "end": v(-2.36, 0.69) * mm});
            skLineSegment(sketch, "E3144", {"start": v(-2.36, 0.69) * mm, "end": v(-2.37, 0.7) * mm});
            skLineSegment(sketch, "E3145", {"start": v(-2.37, 0.7) * mm, "end": v(-2.39, 0.7) * mm});
            skLineSegment(sketch, "E3146", {"start": v(-2.39, 0.7) * mm, "end": v(-2.4, 0.7) * mm});
            skLineSegment(sketch, "E3147", {"start": v(-2.4, 0.7) * mm, "end": v(-2.42, 0.71) * mm});
            skLineSegment(sketch, "E3148", {"start": v(-2.42, 0.71) * mm, "end": v(-2.44, 0.72) * mm});
            skLineSegment(sketch, "E3149", {"start": v(-2.44, 0.72) * mm, "end": v(-2.45, 0.72) * mm});
            skLineSegment(sketch, "E3150", {"start": v(-2.45, 0.72) * mm, "end": v(-2.47, 0.73) * mm});
            skLineSegment(sketch, "E3151", {"start": v(-2.47, 0.73) * mm, "end": v(-2.49, 0.74) * mm});
            skLineSegment(sketch, "E3152", {"start": v(-2.49, 0.74) * mm, "end": v(-2.5, 0.75) * mm});
            skLineSegment(sketch, "E3153", {"start": v(-2.5, 0.75) * mm, "end": v(-2.52, 0.76) * mm});
            skLineSegment(sketch, "E3154", {"start": v(-2.52, 0.76) * mm, "end": v(-2.54, 0.76) * mm});
            skLineSegment(sketch, "E3155", {"start": v(-2.54, 0.76) * mm, "end": v(-2.56, 0.77) * mm});
            skSolve(sketch);
        }
        {
            var Q0;
            Q0 = qSketchRegion(id + "F0", true);
            extrude(context, id + "F1", {"entities" : qUnion([Q0]), "depth" : 5 * mm, "offsetDistance" : 25 * mm});
        }
    });
